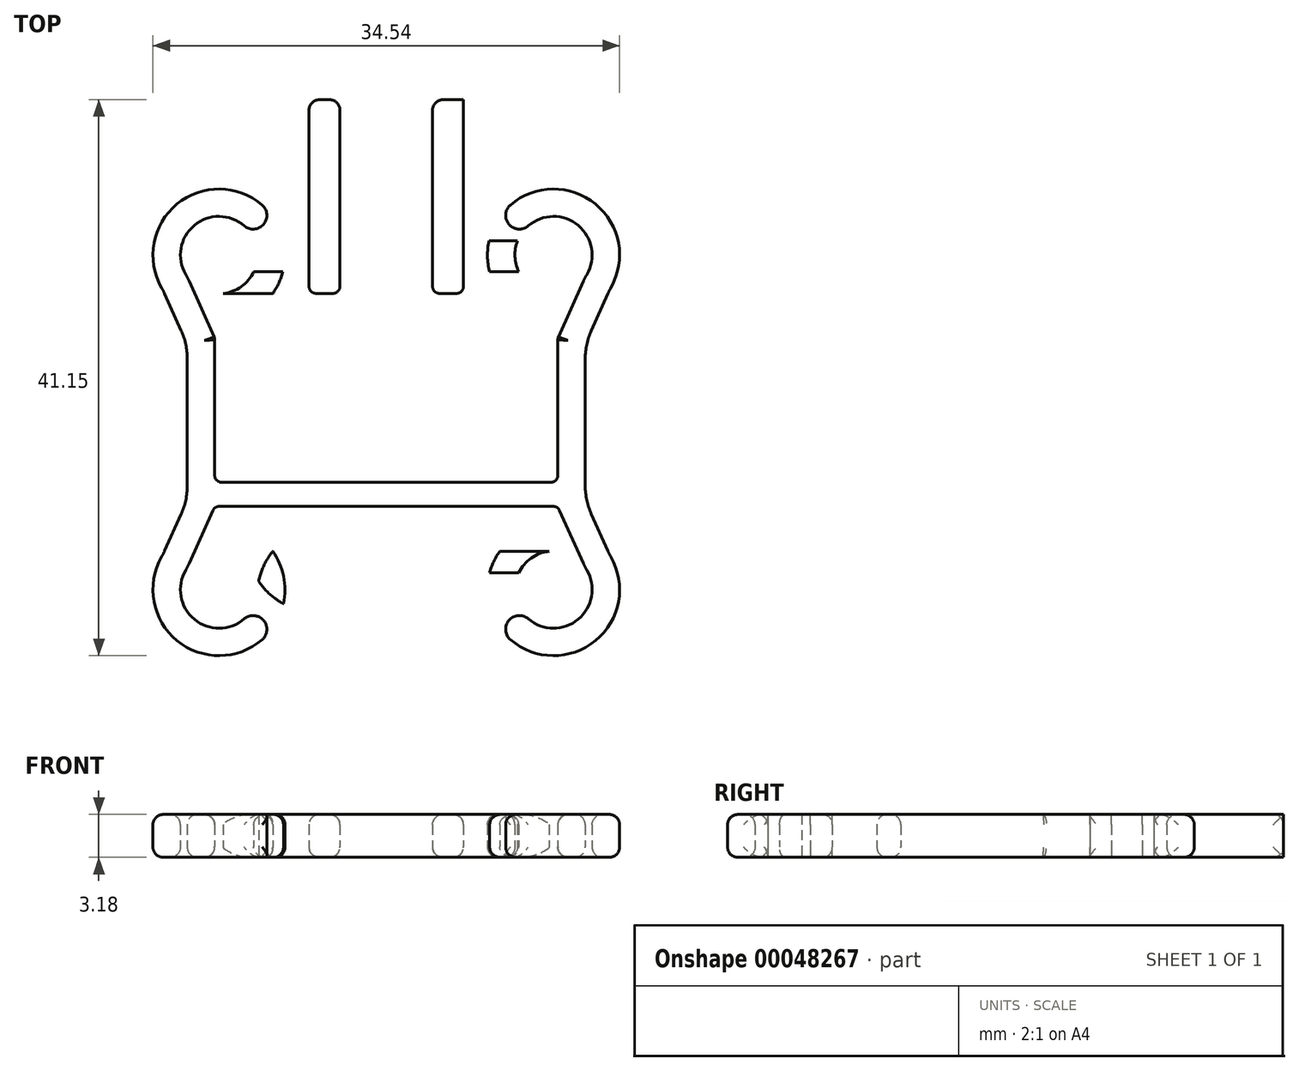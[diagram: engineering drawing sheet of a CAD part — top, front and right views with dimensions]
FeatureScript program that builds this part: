
annotation { "Feature Type Name" : "Feature", "Feature Type Description" : "" }
export const myFeature = defineFeature(function(context is Context, id is Id, definition is map)
    precondition{}
    {
        {
            var Q0;
            Q0=qCreatedBy(makeId("Top.planeOp"),FACE);
            var sketch = newSketch(context, id + "F0", { "sketchPlane" : qUnion([Q0])});
            skCircle(sketch, "E0", {"center": v(-12.38, 12.38) * mm, "radius": 2.86 * mm});
            skCircle(sketch, "E1", {"center": v(12.38, 12.38) * mm, "radius": 2.86 * mm});
            skCircle(sketch, "E2", {"center": v(12.38, -12.38) * mm, "radius": 2.86 * mm});
            skCircle(sketch, "E3", {"center": v(-12.38, -12.38) * mm, "radius": 2.86 * mm});
            skCircle(sketch, "E4", {"center": v(-12.38, 12.38) * mm, "radius": 4.89 * mm});
            skCircle(sketch, "E5", {"center": v(12.38, 12.38) * mm, "radius": 4.89 * mm});
            skCircle(sketch, "E6", {"center": v(12.38, -12.38) * mm, "radius": 4.89 * mm});
            skCircle(sketch, "E7", {"center": v(-12.38, -12.38) * mm, "radius": 4.89 * mm});
            skPoint(sketch, "E8.rect.middle", {"position": v(0, 0) * mm});
            skLineSegment(sketch, "E9.rect.bottom", {"start": v(14.73, 11.14) * mm, "end": v(-14.73, 11.14) * mm});
            skLineSegment(sketch, "E9.rect.top", {"start": v(14.73, -11.14) * mm, "end": v(-14.73, -11.14) * mm});
            skLineSegment(sketch, "E9.rect.left", {"start": v(14.73, 11.14) * mm, "end": v(14.73, -11.14) * mm});
            skLineSegment(sketch, "E9.rect.right", {"start": v(-14.73, 11.14) * mm, "end": v(-14.73, -11.14) * mm});
            skLineSegment(sketch, "E10.rect.bottom", {"start": v(12.7, 6.22) * mm, "end": v(-12.7, 6.22) * mm});
            skLineSegment(sketch, "E10.rect.top", {"start": v(12.7, -6.22) * mm, "end": v(-12.7, -6.22) * mm});
            skLineSegment(sketch, "E11.rect.bottom", {"start": v(12.7, 4.44) * mm, "end": v(-12.7, 4.44) * mm});
            skLineSegment(sketch, "E11.rect.top", {"start": v(12.7, -4.45) * mm, "end": v(-12.7, -4.45) * mm});
            skLineSegment(sketch, "E12.rect.bottom", {"start": v(12.7, 9.54) * mm, "end": v(-12.7, 9.54) * mm});
            skLineSegment(sketch, "E12.rect.top", {"start": v(12.7, -9.54) * mm, "end": v(-12.7, -9.54) * mm});
            skLineSegment(sketch, "E12.rect.left", {"start": v(12.7, 9.54) * mm, "end": v(12.7, -9.54) * mm});
            skLineSegment(sketch, "E12.rect.right", {"start": v(-12.7, 9.54) * mm, "end": v(-12.7, -9.54) * mm});
            skLineSegment(sketch, "E13.rect.bottom", {"start": v(5.72, 23.88) * mm, "end": v(3.43, 23.88) * mm});
            skLineSegment(sketch, "E13.rect.top", {"start": v(5.72, 11.14) * mm, "end": v(-5.71, 11.14) * mm});
            skLineSegment(sketch, "E13.rect.left", {"start": v(5.72, 23.88) * mm, "end": v(5.72, 11.14) * mm});
            skLineSegment(sketch, "E13.rect.right", {"start": v(-5.71, 23.88) * mm, "end": v(-5.71, 11.14) * mm});
            skLineSegment(sketch, "E14.top", {"start": v(-3.43, 11.14) * mm, "end": v(3.43, 11.14) * mm});
            skLineSegment(sketch, "E14.left", {"start": v(-3.43, 20.97) * mm, "end": v(-3.43, 11.14) * mm});
            skLineSegment(sketch, "E14.right", {"start": v(3.43, 20.97) * mm, "end": v(3.43, 11.14) * mm});
            skLineSegment(sketch, "E15", {"start": v(-5.71, 11.14) * mm, "end": v(-5.71, 6.22) * mm});
            skLineSegment(sketch, "E16", {"start": v(-5.71, 6.22) * mm, "end": v(-3.43, 6.22) * mm});
            skLineSegment(sketch, "E17", {"start": v(-3.43, 6.22) * mm, "end": v(-3.43, 11.14) * mm});
            skLineSegment(sketch, "E18", {"start": v(3.43, 11.14) * mm, "end": v(3.43, 6.22) * mm});
            skLineSegment(sketch, "E19", {"start": v(3.43, 6.22) * mm, "end": v(5.72, 6.22) * mm});
            skLineSegment(sketch, "E20", {"start": v(5.72, 6.22) * mm, "end": v(5.72, 11.14) * mm});
            skLineSegment(sketch, "E21.rect.bottom", {"start": v(-0.89, 4.44) * mm, "end": v(0.89, 4.44) * mm});
            skLineSegment(sketch, "E21.rect.top", {"start": v(-0.89, -4.44) * mm, "end": v(0.89, -4.44) * mm});
            skLineSegment(sketch, "E21.rect.left", {"start": v(-0.89, 4.44) * mm, "end": v(-0.89, -4.44) * mm});
            skLineSegment(sketch, "E21.rect.right", {"start": v(0.89, 4.44) * mm, "end": v(0.89, -4.44) * mm});
            skLineSegment(sketch, "E22.top", {"start": v(-3.43, 23.88) * mm, "end": v(-5.71, 23.88) * mm});
            skLineSegment(sketch, "E22.left", {"start": v(-3.43, 20.97) * mm, "end": v(-3.43, 23.88) * mm});
            skLineSegment(sketch, "E22.right", {"start": v(-5.71, 20.97) * mm, "end": v(-5.71, 23.88) * mm});
            skLineSegment(sketch, "E23.top", {"start": v(3.43, 23.88) * mm, "end": v(5.72, 23.88) * mm});
            skLineSegment(sketch, "E23.left", {"start": v(3.43, 20.97) * mm, "end": v(3.43, 23.88) * mm});
            skLineSegment(sketch, "E23.right", {"start": v(5.72, 20.97) * mm, "end": v(5.72, 23.88) * mm});
            skLineSegment(sketch, "E24.bottom", {"start": v(-10.35, 11.14) * mm, "end": v(-6.54, 11.14) * mm});
            skLineSegment(sketch, "E24.top", {"start": v(-10.35, 13.42) * mm, "end": v(-6.54, 13.42) * mm});
            skLineSegment(sketch, "E24.left", {"start": v(-10.35, 11.14) * mm, "end": v(-10.35, 13.42) * mm});
            skLineSegment(sketch, "E24.right", {"start": v(-6.54, 11.14) * mm, "end": v(-6.54, 13.42) * mm});
            skPoint(sketch, "E25.oppositeSnap0", {"position": v(-8.45, 13.42) * mm});
            skLineSegment(sketch, "E25.bottom", {"start": v(6.54, 11.14) * mm, "end": v(10.35, 11.14) * mm});
            skLineSegment(sketch, "E25.top", {"start": v(6.54, 13.42) * mm, "end": v(10.35, 13.42) * mm});
            skLineSegment(sketch, "E25.left", {"start": v(6.54, 11.14) * mm, "end": v(6.54, 13.42) * mm});
            skLineSegment(sketch, "E25.right", {"start": v(10.35, 11.14) * mm, "end": v(10.35, 13.42) * mm});
            skLineSegment(sketch, "E26", {"start": v(-10.35, 13.42) * mm, "end": v(-6.54, 17.1) * mm});
            skLineSegment(sketch, "E27", {"start": v(-6.54, 17.1) * mm, "end": v(-6.54, 13.42) * mm});
            skLineSegment(sketch, "E28", {"start": v(6.54, 13.42) * mm, "end": v(6.54, 17.1) * mm});
            skLineSegment(sketch, "E29", {"start": v(6.54, 17.1) * mm, "end": v(10.35, 13.42) * mm});
            skLineSegment(sketch, "E30.bottom", {"start": v(-10.35, -11.14) * mm, "end": v(-6.54, -11.14) * mm});
            skLineSegment(sketch, "E30.top", {"start": v(-10.35, -13.42) * mm, "end": v(-6.54, -13.42) * mm});
            skLineSegment(sketch, "E30.left", {"start": v(-10.35, -11.14) * mm, "end": v(-10.35, -13.42) * mm});
            skLineSegment(sketch, "E30.right", {"start": v(-6.54, -11.14) * mm, "end": v(-6.54, -13.42) * mm});
            skLineSegment(sketch, "E31.bottom", {"start": v(6.54, -13.42) * mm, "end": v(10.35, -13.42) * mm});
            skLineSegment(sketch, "E31.top", {"start": v(6.54, -11.14) * mm, "end": v(10.35, -11.14) * mm});
            skLineSegment(sketch, "E31.left", {"start": v(6.54, -13.42) * mm, "end": v(6.54, -11.14) * mm});
            skLineSegment(sketch, "E31.right", {"start": v(10.35, -13.42) * mm, "end": v(10.35, -11.14) * mm});
            skLineSegment(sketch, "E32", {"start": v(10.35, -13.42) * mm, "end": v(6.54, -17.1) * mm});
            skLineSegment(sketch, "E33", {"start": v(6.54, -17.1) * mm, "end": v(6.54, -13.42) * mm});
            skLineSegment(sketch, "E34", {"start": v(-6.54, -13.42) * mm, "end": v(-6.54, -17.1) * mm});
            skLineSegment(sketch, "E35", {"start": v(-6.54, -17.1) * mm, "end": v(-10.35, -13.42) * mm});
            skLineSegment(sketch, "E36", {"start": v(-12.7, -6.22) * mm, "end": v(-15.16, -11.7) * mm});
            skLineSegment(sketch, "E37", {"start": v(-15.16, -11.7) * mm, "end": v(-17.22, -11.7) * mm});
            skLineSegment(sketch, "E38", {"start": v(-17.22, -11.7) * mm, "end": v(-14.73, -6.15) * mm});
            skLineSegment(sketch, "E39", {"start": v(15.16, -11.7) * mm, "end": v(17.22, -11.7) * mm});
            skLineSegment(sketch, "E40", {"start": v(17.22, -11.7) * mm, "end": v(14.73, -6.15) * mm});
            skLineSegment(sketch, "E41", {"start": v(15.16, -11.7) * mm, "end": v(12.7, -6.22) * mm});
            skLineSegment(sketch, "E42", {"start": v(15.16, 11.7) * mm, "end": v(17.22, 11.7) * mm});
            skLineSegment(sketch, "E43", {"start": v(17.22, 11.7) * mm, "end": v(14.73, 6.14) * mm});
            skLineSegment(sketch, "E44", {"start": v(12.7, 6.22) * mm, "end": v(15.16, 11.7) * mm});
            skLineSegment(sketch, "E45", {"start": v(-15.16, 11.7) * mm, "end": v(-17.22, 11.7) * mm});
            skLineSegment(sketch, "E46", {"start": v(-17.22, 11.7) * mm, "end": v(-14.73, 6.14) * mm});
            skLineSegment(sketch, "E47", {"start": v(-15.16, 11.7) * mm, "end": v(-12.7, 6.22) * mm});
            skLineSegment(sketch, "E48", {"start": v(-16.52, 9.78) * mm, "end": v(-14.73, 5.79) * mm});
            skLineSegment(sketch, "E49", {"start": v(14.73, 5.79) * mm, "end": v(16.52, 9.78) * mm});
            skLineSegment(sketch, "E50", {"start": v(-16.52, -9.78) * mm, "end": v(-14.73, -5.79) * mm});
            skLineSegment(sketch, "E51", {"start": v(14.73, -5.79) * mm, "end": v(16.52, -9.78) * mm});
            skSolve(sketch);
        }
        {
            var Q0;
            {var subQ3=sQuery(id+"F0.wireOp",EDGE,"E9.rect.bottom");var subQ5=sQuery(id+"F0.wireOp",EDGE,"E0");var subQ7=makeQuery(id+"F0.imprint","INTERSECT",VERTEX,{"disambiguationData":[OD(0.0)],"derivedFrom":[subQ5,subQ3]});Q0=makeQuery(id+"F0.imprint","IMPRINT",FACE,{"disambiguationData":[TD([[makeQuery(id+"F0.imprint","IMPRINT",EDGE,{"disambiguationData":[TD([[subQ7,1.0]])],"derivedFrom":subQ5}),-1.0]])]});}
            var Q1;
            {var subQ0=sQuery(id+"F0.wireOp",EDGE,"E1");var subQ1=sQuery(id+"F0.wireOp",EDGE,"E9.rect.bottom");var subQ3=makeQuery(id+"F0.imprint","INTERSECT",VERTEX,{"disambiguationData":[OD(0.0)],"derivedFrom":[subQ0,subQ1]});Q1=makeQuery(id+"F0.imprint","IMPRINT",FACE,{"disambiguationData":[TD([[makeQuery(id+"F0.imprint","IMPRINT",EDGE,{"disambiguationData":[TD([[subQ3,1.0]])],"derivedFrom":subQ0}),-1.0]])]});}
            var Q2;
            {var subQ3=sQuery(id+"F0.wireOp",EDGE,"E9.rect.top");var subQ5=sQuery(id+"F0.wireOp",EDGE,"E2");var subQ7=makeQuery(id+"F0.imprint","INTERSECT",VERTEX,{"disambiguationData":[OD(0.0)],"derivedFrom":[subQ5,subQ3]});Q2=makeQuery(id+"F0.imprint","IMPRINT",FACE,{"disambiguationData":[TD([[makeQuery(id+"F0.imprint","IMPRINT",EDGE,{"disambiguationData":[TD([[subQ7,1.0]])],"derivedFrom":subQ5}),-1.0]])]});}
            var Q3;
            {var subQ3=sQuery(id+"F0.wireOp",EDGE,"E9.rect.top");var subQ5=sQuery(id+"F0.wireOp",EDGE,"E3");var subQ7=makeQuery(id+"F0.imprint","INTERSECT",VERTEX,{"disambiguationData":[OD(0.0)],"derivedFrom":[subQ5,subQ3]});Q3=makeQuery(id+"F0.imprint","IMPRINT",FACE,{"disambiguationData":[TD([[makeQuery(id+"F0.imprint","IMPRINT",EDGE,{"disambiguationData":[TD([[subQ7,1.0]])],"derivedFrom":subQ5}),-1.0]])]});}
            var Q4;
            {var subQ2=sQuery(id+"F0.wireOp",EDGE,"E10.rect.top");Q4=makeQuery(id+"F0.imprint","IMPRINT",FACE,{"disambiguationData":[TD([[makeQuery(id+"F0.imprint","IMPRINT",EDGE,{"derivedFrom":subQ2}),-1.0]])]});}
            var Q5;
            {var subQ1=sQuery(id+"F0.wireOp",EDGE,"E4");var subQ7=sQuery(id+"F0.wireOp",EDGE,"E9.rect.right");var subQ8=makeQuery(id+"F0.imprint","INTERSECT",VERTEX,{"derivedFrom":[subQ1,subQ7]});Q5=makeQuery(id+"F0.imprint","IMPRINT",FACE,{"disambiguationData":[TD([[makeQuery(id+"F0.imprint","IMPRINT",EDGE,{"disambiguationData":[TD([[subQ8,-1.0]])],"derivedFrom":subQ1}),1.0]])]});}
            var Q6;
            {var subQ7=sQuery(id+"F0.wireOp",EDGE,"E9.rect.right");var subQ9=sQuery(id+"F0.wireOp",EDGE,"E4");var subQ11=makeQuery(id+"F0.imprint","INTERSECT",VERTEX,{"derivedFrom":[subQ9,subQ7]});Q6=makeQuery(id+"F0.imprint","IMPRINT",FACE,{"disambiguationData":[TD([[makeQuery(id+"F0.imprint","IMPRINT",EDGE,{"disambiguationData":[TD([[subQ11,-1.0]])],"derivedFrom":subQ9}),-1.0]])]});}
            var Q7;
            {var subQ1=sQuery(id+"F0.wireOp",EDGE,"E7");var subQ5=sQuery(id+"F0.wireOp",EDGE,"E9.rect.right");var subQ6=makeQuery(id+"F0.imprint","INTERSECT",VERTEX,{"derivedFrom":[subQ1,subQ5]});Q7=makeQuery(id+"F0.imprint","IMPRINT",FACE,{"disambiguationData":[TD([[makeQuery(id+"F0.imprint","IMPRINT",EDGE,{"disambiguationData":[TD([[subQ6,1.0]])],"derivedFrom":subQ1}),1.0]])]});}
            var Q8;
            {var subQ7=sQuery(id+"F0.wireOp",EDGE,"E5");var subQ9=sQuery(id+"F0.wireOp",EDGE,"E9.rect.left");var subQ11=makeQuery(id+"F0.imprint","INTERSECT",VERTEX,{"derivedFrom":[subQ7,subQ9]});Q8=makeQuery(id+"F0.imprint","IMPRINT",FACE,{"disambiguationData":[TD([[makeQuery(id+"F0.imprint","IMPRINT",EDGE,{"disambiguationData":[TD([[subQ11,1.0]])],"derivedFrom":subQ7}),-1.0]])]});}
            var Q9;
            {var subQ1=sQuery(id+"F0.wireOp",EDGE,"E5");var subQ7=sQuery(id+"F0.wireOp",EDGE,"E9.rect.left");var subQ8=makeQuery(id+"F0.imprint","INTERSECT",VERTEX,{"derivedFrom":[subQ1,subQ7]});Q9=makeQuery(id+"F0.imprint","IMPRINT",FACE,{"disambiguationData":[TD([[makeQuery(id+"F0.imprint","IMPRINT",EDGE,{"disambiguationData":[TD([[subQ8,1.0]])],"derivedFrom":subQ1}),1.0]])]});}
            var Q10;
            {var subQ1=sQuery(id+"F0.wireOp",EDGE,"E6");var subQ7=sQuery(id+"F0.wireOp",EDGE,"E9.rect.left");var subQ9=makeQuery(id+"F0.imprint","INTERSECT",VERTEX,{"derivedFrom":[subQ1,subQ7]});Q10=makeQuery(id+"F0.imprint","IMPRINT",FACE,{"disambiguationData":[TD([[makeQuery(id+"F0.imprint","IMPRINT",EDGE,{"disambiguationData":[TD([[subQ9,-1.0]])],"derivedFrom":subQ1}),1.0]])]});}
            var Q11;
            {var subQ4=sQuery(id+"F0.wireOp",EDGE,"E16");Q11=makeQuery(id+"F0.imprint","IMPRINT",FACE,{"disambiguationData":[TD([[makeQuery(id+"F0.imprint","IMPRINT",EDGE,{"derivedFrom":subQ4}),1.0]])]});}
            var Q12;
            {var subQ0=sQuery(id+"F0.wireOp",EDGE,"E17");var subQ1=sQuery(id+"F0.wireOp",EDGE,"E12.rect.bottom");var subQ2=makeQuery(id+"F0.imprint","INTERSECT",VERTEX,{"derivedFrom":[subQ1,subQ0]});Q12=makeQuery(id+"F0.imprint","IMPRINT",FACE,{"disambiguationData":[TD([[makeQuery(id+"F0.imprint","IMPRINT",EDGE,{"disambiguationData":[TD([[subQ2,-1.0]])],"derivedFrom":subQ1}),-1.0]])]});}
            var Q13;
            {var subQ1=sQuery(id+"F0.wireOp",EDGE,"b3d8b3c6-d051-494b-8968-ba9f3ebd01f7.rect.top");var subQ5=sQuery(id+"F0.wireOp",EDGE,"E13.rect.right");var subQ6=makeQuery(id+"F0.imprint","INTERSECT",VERTEX,{"derivedFrom":[subQ5,subQ1]});Q13=makeQuery(id+"F0.imprint","IMPRINT",FACE,{"disambiguationData":[TD([[makeQuery(id+"F0.imprint","IMPRINT",EDGE,{"disambiguationData":[TD([[subQ6,1.0]])],"derivedFrom":subQ1}),1.0]])]});}
            var Q14;
            {var subQ1=sQuery(id+"F0.wireOp",EDGE,"b3d8b3c6-d051-494b-8968-ba9f3ebd01f7.rect.top");var subQ5=sQuery(id+"F0.wireOp",EDGE,"E13.rect.left");var subQ6=makeQuery(id+"F0.imprint","INTERSECT",VERTEX,{"derivedFrom":[subQ5,subQ1]});Q14=makeQuery(id+"F0.imprint","IMPRINT",FACE,{"disambiguationData":[TD([[makeQuery(id+"F0.imprint","IMPRINT",EDGE,{"disambiguationData":[TD([[subQ6,-1.0]])],"derivedFrom":subQ1}),1.0]])]});}
            var Q15;
            {var subQ1=sQuery(id+"F0.wireOp",EDGE,"E12.rect.bottom");var subQ5=sQuery(id+"F0.wireOp",EDGE,"E20");var subQ6=makeQuery(id+"F0.imprint","INTERSECT",VERTEX,{"derivedFrom":[subQ1,subQ5]});Q15=makeQuery(id+"F0.imprint","IMPRINT",FACE,{"disambiguationData":[TD([[makeQuery(id+"F0.imprint","IMPRINT",EDGE,{"disambiguationData":[TD([[subQ6,-1.0]])],"derivedFrom":subQ1}),-1.0]])]});}
            var Q16;
            {var subQ4=sQuery(id+"F0.wireOp",EDGE,"E19");Q16=makeQuery(id+"F0.imprint","IMPRINT",FACE,{"disambiguationData":[TD([[makeQuery(id+"F0.imprint","IMPRINT",EDGE,{"derivedFrom":subQ4}),1.0]])]});}
            var Q17;
            {var subQ0=sQuery(id+"F0.wireOp",EDGE,"E22.bottom");Q17=makeQuery(id+"F0.imprint","IMPRINT",FACE,{"disambiguationData":[TD([[makeQuery(id+"F0.imprint","IMPRINT",EDGE,{"derivedFrom":subQ0}),1.0]])]});}
            var Q18;
            Q18=makeQuery(id+"F0.imprint","IMPRINT",FACE,{"disambiguationData":[TD([[makeQuery(id+"F0.imprint","IMPRINT",EDGE,{"derivedFrom":sQuery(id+"F0.wireOp",EDGE,"E22.bottom")}),-1.0]])]});
            var Q19;
            {var subQ5=sQuery(id+"F0.wireOp",EDGE,"E23.bottom");Q19=makeQuery(id+"F0.imprint","IMPRINT",FACE,{"disambiguationData":[TD([[makeQuery(id+"F0.imprint","IMPRINT",EDGE,{"derivedFrom":subQ5}),-1.0]])]});}
            var Q20;
            Q20=makeQuery(id+"F0.imprint","IMPRINT",FACE,{"disambiguationData":[TD([[makeQuery(id+"F0.imprint","IMPRINT",EDGE,{"derivedFrom":sQuery(id+"F0.wireOp",EDGE,"E23.bottom")}),1.0]])]});
            var Q21;
            {var subQ2=sQuery(id+"F0.wireOp",EDGE,"E13.rect.right");Q21=makeQuery(id+"F0.imprint","IMPRINT",FACE,{"disambiguationData":[TD([[makeQuery(id+"F0.imprint","IMPRINT",EDGE,{"derivedFrom":subQ2}),1.0]])]});}
            var Q22;
            {var subQ2=sQuery(id+"F0.wireOp",EDGE,"E13.rect.left");Q22=makeQuery(id+"F0.imprint","IMPRINT",FACE,{"disambiguationData":[TD([[makeQuery(id+"F0.imprint","IMPRINT",EDGE,{"derivedFrom":subQ2}),-1.0]])]});}
            var Q23;
            {var subQ1=sQuery(id+"F0.wireOp",EDGE,"E3");var subQ5=sQuery(id+"F0.wireOp",EDGE,"E9.rect.top");var subQ6=makeQuery(id+"F0.imprint","INTERSECT",VERTEX,{"derivedFrom":[subQ1,subQ5]});Q23=makeQuery(id+"F0.imprint","IMPRINT",FACE,{"disambiguationData":[TD([[makeQuery(id+"F0.imprint","IMPRINT",EDGE,{"disambiguationData":[TD([[subQ6,-1.0]])],"derivedFrom":subQ1}),-1.0]])]});}
            var Q24;
            {var subQ0=sQuery(id+"F0.wireOp",EDGE,"E29");var subQ1=sQuery(id+"F0.wireOp",EDGE,"E1");var subQ2=makeQuery(id+"F0.imprint","INTERSECT",VERTEX,{"derivedFrom":[subQ1,subQ0]});Q24=makeQuery(id+"F0.imprint","IMPRINT",FACE,{"disambiguationData":[TD([[makeQuery(id+"F0.imprint","IMPRINT",EDGE,{"disambiguationData":[TD([[subQ2,1.0]])],"derivedFrom":subQ1}),-1.0]])]});}
            var Q25;
            {var subQ9=sQuery(id+"F0.wireOp",EDGE,"E16");Q25=makeQuery(id+"F0.imprint","IMPRINT",FACE,{"disambiguationData":[TD([[makeQuery(id+"F0.imprint","IMPRINT",EDGE,{"derivedFrom":subQ9}),-1.0]])]});}
            var Q26;
            {var subQ0=sQuery(id+"F0.wireOp",EDGE,"E45");Q26=makeQuery(id+"F0.imprint","IMPRINT",FACE,{"disambiguationData":[TD([[makeQuery(id+"F0.imprint","IMPRINT",EDGE,{"derivedFrom":subQ0}),-1.0]])]});}
            var Q27;
            {var subQ3=sQuery(id+"F0.wireOp",EDGE,"E42");Q27=makeQuery(id+"F0.imprint","IMPRINT",FACE,{"disambiguationData":[TD([[makeQuery(id+"F0.imprint","IMPRINT",EDGE,{"derivedFrom":subQ3}),-1.0]])]});}
            var Q28;
            {var subQ0=sQuery(id+"F0.wireOp",EDGE,"E39");Q28=makeQuery(id+"F0.imprint","IMPRINT",FACE,{"disambiguationData":[TD([[makeQuery(id+"F0.imprint","IMPRINT",EDGE,{"derivedFrom":subQ0}),-1.0]])]});}
            var Q29;
            {var subQ5=sQuery(id+"F0.wireOp",EDGE,"E37");Q29=makeQuery(id+"F0.imprint","IMPRINT",FACE,{"disambiguationData":[TD([[makeQuery(id+"F0.imprint","IMPRINT",EDGE,{"derivedFrom":subQ5}),1.0]])]});}
            var Q30;
            {var subQ0=sQuery(id+"F0.wireOp",EDGE,"E38");var subQ1=sQuery(id+"F0.wireOp",EDGE,"E7");var subQ2=makeQuery(id+"F0.imprint","INTERSECT",VERTEX,{"derivedFrom":[subQ1,subQ0]});Q30=makeQuery(id+"F0.imprint","IMPRINT",FACE,{"disambiguationData":[TD([[makeQuery(id+"F0.imprint","IMPRINT",EDGE,{"disambiguationData":[TD([[subQ2,1.0]])],"derivedFrom":subQ1}),-1.0]])]});}
            var Q31;
            {var subQ0=sQuery(id+"F0.wireOp",EDGE,"E40");var subQ1=sQuery(id+"F0.wireOp",EDGE,"E6");var subQ2=makeQuery(id+"F0.imprint","INTERSECT",VERTEX,{"derivedFrom":[subQ1,subQ0]});Q31=makeQuery(id+"F0.imprint","IMPRINT",FACE,{"disambiguationData":[TD([[makeQuery(id+"F0.imprint","IMPRINT",EDGE,{"disambiguationData":[TD([[subQ2,-1.0]])],"derivedFrom":subQ1}),-1.0]])]});}
            var Q32;
            {var subQ1=sQuery(id+"F0.wireOp",EDGE,"E5");var subQ3=sQuery(id+"F0.wireOp",EDGE,"E43");var subQ5=makeQuery(id+"F0.imprint","INTERSECT",VERTEX,{"derivedFrom":[subQ1,subQ3]});Q32=makeQuery(id+"F0.imprint","IMPRINT",FACE,{"disambiguationData":[TD([[makeQuery(id+"F0.imprint","IMPRINT",EDGE,{"disambiguationData":[TD([[subQ5,1.0]])],"derivedFrom":subQ1}),-1.0]])]});}
            var Q33;
            {var subQ0=sQuery(id+"F0.wireOp",EDGE,"E46");var subQ1=sQuery(id+"F0.wireOp",EDGE,"E4");var subQ2=makeQuery(id+"F0.imprint","INTERSECT",VERTEX,{"derivedFrom":[subQ1,subQ0]});Q33=makeQuery(id+"F0.imprint","IMPRINT",FACE,{"disambiguationData":[TD([[makeQuery(id+"F0.imprint","IMPRINT",EDGE,{"disambiguationData":[TD([[subQ2,-1.0]])],"derivedFrom":subQ1}),-1.0]])]});}
            var Q34;
            {var subQ0=sQuery(id+"F0.wireOp",EDGE,"E45");Q34=makeQuery(id+"F0.imprint","IMPRINT",FACE,{"disambiguationData":[TD([[makeQuery(id+"F0.imprint","IMPRINT",EDGE,{"derivedFrom":subQ0}),1.0]])]});}
            var Q35;
            {var subQ9=sQuery(id+"F0.wireOp",EDGE,"E37");Q35=makeQuery(id+"F0.imprint","IMPRINT",FACE,{"disambiguationData":[TD([[makeQuery(id+"F0.imprint","IMPRINT",EDGE,{"derivedFrom":subQ9}),-1.0]])]});}
            var Q36;
            {var subQ0=sQuery(id+"F0.wireOp",EDGE,"E39");Q36=makeQuery(id+"F0.imprint","IMPRINT",FACE,{"disambiguationData":[TD([[makeQuery(id+"F0.imprint","IMPRINT",EDGE,{"derivedFrom":subQ0}),1.0]])]});}
            var Q37;
            {var subQ0=sQuery(id+"F0.wireOp",EDGE,"E38");var subQ1=sQuery(id+"F0.wireOp",EDGE,"E7");var subQ3=makeQuery(id+"F0.imprint","INTERSECT",VERTEX,{"derivedFrom":[subQ1,subQ0]});Q37=makeQuery(id+"F0.imprint","IMPRINT",FACE,{"disambiguationData":[TD([[makeQuery(id+"F0.imprint","IMPRINT",EDGE,{"disambiguationData":[TD([[subQ3,-1.0]])],"derivedFrom":subQ1}),1.0]])]});}
            var Q38;
            {var subQ0=sQuery(id+"F0.wireOp",EDGE,"E40");var subQ1=sQuery(id+"F0.wireOp",EDGE,"E6");var subQ3=makeQuery(id+"F0.imprint","INTERSECT",VERTEX,{"derivedFrom":[subQ1,subQ0]});Q38=makeQuery(id+"F0.imprint","IMPRINT",FACE,{"disambiguationData":[TD([[makeQuery(id+"F0.imprint","IMPRINT",EDGE,{"disambiguationData":[TD([[subQ3,1.0]])],"derivedFrom":subQ1}),1.0]])]});}
            var Q39;
            {var subQ0=sQuery(id+"F0.wireOp",EDGE,"E43");var subQ1=sQuery(id+"F0.wireOp",EDGE,"E5");var subQ3=makeQuery(id+"F0.imprint","INTERSECT",VERTEX,{"derivedFrom":[subQ1,subQ0]});Q39=makeQuery(id+"F0.imprint","IMPRINT",FACE,{"disambiguationData":[TD([[makeQuery(id+"F0.imprint","IMPRINT",EDGE,{"disambiguationData":[TD([[subQ3,-1.0]])],"derivedFrom":subQ1}),1.0]])]});}
            var Q40;
            {var subQ0=sQuery(id+"F0.wireOp",EDGE,"E46");var subQ1=sQuery(id+"F0.wireOp",EDGE,"E4");var subQ3=makeQuery(id+"F0.imprint","INTERSECT",VERTEX,{"derivedFrom":[subQ1,subQ0]});Q40=makeQuery(id+"F0.imprint","IMPRINT",FACE,{"disambiguationData":[TD([[makeQuery(id+"F0.imprint","IMPRINT",EDGE,{"disambiguationData":[TD([[subQ3,1.0]])],"derivedFrom":subQ1}),1.0]])]});}
            var Q41;
            {var subQ0=sQuery(id+"F0.wireOp",EDGE,"E50");Q41=makeQuery(id+"F0.imprint","IMPRINT",FACE,{"disambiguationData":[TD([[makeQuery(id+"F0.imprint","IMPRINT",EDGE,{"derivedFrom":subQ0}),-1.0]])]});}
            var Q42;
            {var subQ0=sQuery(id+"F0.wireOp",EDGE,"E51");Q42=makeQuery(id+"F0.imprint","IMPRINT",FACE,{"disambiguationData":[TD([[makeQuery(id+"F0.imprint","IMPRINT",EDGE,{"derivedFrom":subQ0}),-1.0]])]});}
            var Q43;
            {var subQ0=sQuery(id+"F0.wireOp",EDGE,"E49");Q43=makeQuery(id+"F0.imprint","IMPRINT",FACE,{"disambiguationData":[TD([[makeQuery(id+"F0.imprint","IMPRINT",EDGE,{"derivedFrom":subQ0}),1.0]])]});}
            var Q44;
            {var subQ0=sQuery(id+"F0.wireOp",EDGE,"E48");Q44=makeQuery(id+"F0.imprint","IMPRINT",FACE,{"disambiguationData":[TD([[makeQuery(id+"F0.imprint","IMPRINT",EDGE,{"derivedFrom":subQ0}),1.0]])]});}
            extrude(context, id + "F1", {"entities" : qUnion([Q0, Q1, Q2, Q3, Q4, Q5, Q6, Q7, Q8, Q9, Q10, Q11, Q12, Q13, Q14, Q15, Q16, Q17, Q18, Q19, Q20, Q21, Q22, Q23, Q24, Q25, Q26, Q27, Q28, Q29, Q30, Q31, Q32, Q33, Q34, Q35, Q36, Q37, Q38, Q39, Q40, Q41, Q42, Q43, Q44]), "depth" : 3.17 * mm});
        }
        {
            var Q0;
            Q0=makeQuery(id+"F1.opExtrude","SWEPT_EDGE",EDGE,{"disambiguationData":[OSD([sQuery(id+"F0.wireOp",EDGE,"E0"),sQuery(id+"F0.wireOp",EDGE,"E26")])]});
            var Q1;
            Q1=makeQuery(id+"F1.opExtrude","SWEPT_EDGE",EDGE,{"disambiguationData":[OSD([sQuery(id+"F0.wireOp",EDGE,"E4"),sQuery(id+"F0.wireOp",EDGE,"E26")])]});
            var Q2;
            Q2=makeQuery(id+"F1.opExtrude","SWEPT_EDGE",EDGE,{"disambiguationData":[OSD([sQuery(id+"F0.wireOp",EDGE,"E1"),sQuery(id+"F0.wireOp",EDGE,"E29")])]});
            var Q3;
            Q3=makeQuery(id+"F1.opExtrude","SWEPT_EDGE",EDGE,{"disambiguationData":[OSD([sQuery(id+"F0.wireOp",EDGE,"E5"),sQuery(id+"F0.wireOp",EDGE,"E29")])]});
            var Q4;
            Q4=makeQuery(id+"F1.opExtrude","SWEPT_EDGE",EDGE,{"disambiguationData":[OSD([sQuery(id+"F0.wireOp",EDGE,"E7"),sQuery(id+"F0.wireOp",EDGE,"E35")])]});
            var Q5;
            Q5=makeQuery(id+"F1.opExtrude","SWEPT_EDGE",EDGE,{"disambiguationData":[OSD([sQuery(id+"F0.wireOp",EDGE,"E3"),sQuery(id+"F0.wireOp",EDGE,"E35")])]});
            var Q6;
            Q6=makeQuery(id+"F1.opExtrude","SWEPT_EDGE",EDGE,{"disambiguationData":[OSD([sQuery(id+"F0.wireOp",EDGE,"E6"),sQuery(id+"F0.wireOp",EDGE,"E32")])]});
            var Q7;
            Q7=makeQuery(id+"F1.opExtrude","SWEPT_EDGE",EDGE,{"disambiguationData":[OSD([sQuery(id+"F0.wireOp",EDGE,"E2"),sQuery(id+"F0.wireOp",EDGE,"E32")])]});
            fillet(context, id + "F2", {"entities" : qUnion([Q0, Q1, Q2, Q3, Q4, Q5, Q6, Q7]), "radius" : 1.02 * mm, "tangentPropagation" : true, "allowEdgeOverflow" : false});
        }
        {
            var Q0;
            Q0=makeQuery(id+"F1.opExtrude","SWEPT_EDGE",EDGE,{"disambiguationData":[OSD([sQuery(id+"F0.wireOp",EDGE,"E9.rect.right"),sQuery(id+"F0.wireOp",EDGE,"E48")])]});
            var Q1;
            Q1=makeQuery(id+"F1.opExtrude","SWEPT_EDGE",EDGE,{"disambiguationData":[OSD([sQuery(id+"F0.wireOp",EDGE,"E4"),sQuery(id+"F0.wireOp",EDGE,"E48")])]});
            var Q2;
            Q2=makeQuery(id+"F1.opExtrude","SWEPT_EDGE",EDGE,{"disambiguationData":[OSD([sQuery(id+"F0.wireOp",EDGE,"E9.rect.right"),sQuery(id+"F0.wireOp",EDGE,"E50")])]});
            var Q3;
            Q3=makeQuery(id+"F1.opExtrude","SWEPT_EDGE",EDGE,{"disambiguationData":[OSD([sQuery(id+"F0.wireOp",EDGE,"E7"),sQuery(id+"F0.wireOp",EDGE,"E50")])]});
            var Q4;
            Q4=makeQuery(id+"F1.opExtrude","SWEPT_EDGE",EDGE,{"disambiguationData":[OSD([sQuery(id+"F0.wireOp",EDGE,"E2"),sQuery(id+"F0.wireOp",EDGE,"E9.rect.left")])]});
            var Q5;
            Q5=makeQuery(id+"F1.opExtrude","SWEPT_EDGE",EDGE,{"disambiguationData":[OSD([sQuery(id+"F0.wireOp",EDGE,"E3"),sQuery(id+"F0.wireOp",EDGE,"E9.rect.right")])]});
            var Q6;
            Q6=makeQuery(id+"F1.opExtrude","SWEPT_EDGE",EDGE,{"disambiguationData":[OSD([sQuery(id+"F0.wireOp",EDGE,"E6"),sQuery(id+"F0.wireOp",EDGE,"E51")])]});
            var Q7;
            Q7=makeQuery(id+"F1.opExtrude","SWEPT_EDGE",EDGE,{"disambiguationData":[OSD([sQuery(id+"F0.wireOp",EDGE,"E9.rect.left"),sQuery(id+"F0.wireOp",EDGE,"E51")])]});
            var Q8;
            Q8=makeQuery(id+"F1.opExtrude","SWEPT_EDGE",EDGE,{"disambiguationData":[OSD([sQuery(id+"F0.wireOp",EDGE,"E9.rect.left"),sQuery(id+"F0.wireOp",EDGE,"E49")])]});
            var Q9;
            Q9=makeQuery(id+"F1.opExtrude","SWEPT_EDGE",EDGE,{"disambiguationData":[OSD([sQuery(id+"F0.wireOp",EDGE,"E5"),sQuery(id+"F0.wireOp",EDGE,"E49")])]});
            var Q10;
            Q10=makeQuery(id+"F1.opExtrude","SWEPT_EDGE",EDGE,{"disambiguationData":[OSD([sQuery(id+"F0.wireOp",EDGE,"E9.rect.left"),sQuery(id+"F0.wireOp",EDGE,"E44")])]});
            var Q11;
            Q11=makeQuery(id+"F1.opExtrude","SWEPT_EDGE",EDGE,{"disambiguationData":[OSD([sQuery(id+"F0.wireOp",EDGE,"E0"),sQuery(id+"F0.wireOp",EDGE,"E9.rect.right")])]});
            fillet(context, id + "F3", {"entities" : qUnion([Q0, Q1, Q2, Q3, Q4, Q5, Q6, Q7, Q8, Q9, Q10, Q11]), "radius" : 5.08 * mm, "tangentPropagation" : true, "allowEdgeOverflow" : false});
        }
        {
            var Q0;
            Q0=makeQuery(id+"F1.opExtrude","SWEPT_EDGE",EDGE,{"disambiguationData":[OSD([sQuery(id+"F0.wireOp",EDGE,"E11.rect.top"),sQuery(id+"F0.wireOp",EDGE,"E12.rect.left")])]});
            var Q1;
            Q1=makeQuery(id+"F1.opExtrude","SWEPT_EDGE",EDGE,{"disambiguationData":[OSD([sQuery(id+"F0.wireOp",EDGE,"E11.rect.bottom"),sQuery(id+"F0.wireOp",EDGE,"E12.rect.left")])]});
            var Q2;
            Q2=makeQuery(id+"F1.opExtrude","SWEPT_EDGE",EDGE,{"disambiguationData":[OSD([sQuery(id+"F0.wireOp",EDGE,"E10.rect.top"),sQuery(id+"F0.wireOp",EDGE,"E12.rect.left"),sQuery(id+"F0.wireOp",EDGE,"E41")])]});
            var Q3;
            Q3=makeQuery(id+"F1.opExtrude","SWEPT_EDGE",EDGE,{"disambiguationData":[OSD([sQuery(id+"F0.wireOp",EDGE,"E10.rect.top"),sQuery(id+"F0.wireOp",EDGE,"E12.rect.right"),sQuery(id+"F0.wireOp",EDGE,"E36")])]});
            var Q4;
            Q4=makeQuery(id+"F1.opExtrude","SWEPT_EDGE",EDGE,{"disambiguationData":[OSD([sQuery(id+"F0.wireOp",EDGE,"E11.rect.bottom"),sQuery(id+"F0.wireOp",EDGE,"E12.rect.right")])]});
            var Q5;
            Q5=makeQuery(id+"F1.opExtrude","SWEPT_EDGE",EDGE,{"disambiguationData":[OSD([sQuery(id+"F0.wireOp",EDGE,"E11.rect.top"),sQuery(id+"F0.wireOp",EDGE,"E12.rect.right")])]});
            var Q6;
            Q6=makeQuery(id+"F1.opExtrude","SWEPT_EDGE",EDGE,{"disambiguationData":[OSD([sQuery(id+"F0.wireOp",EDGE,"E10.rect.bottom"),sQuery(id+"F0.wireOp",EDGE,"E12.rect.right"),sQuery(id+"F0.wireOp",EDGE,"E47")])]});
            var Q7;
            Q7=makeQuery(id+"F1.opExtrude","SWEPT_EDGE",EDGE,{"disambiguationData":[OSD([sQuery(id+"F0.wireOp",EDGE,"E10.rect.bottom"),sQuery(id+"F0.wireOp",EDGE,"E16"),sQuery(id+"F0.wireOp",EDGE,"E17")])]});
            var Q8;
            Q8=makeQuery(id+"F1.opExtrude","SWEPT_EDGE",EDGE,{"disambiguationData":[OSD([sQuery(id+"F0.wireOp",EDGE,"E10.rect.bottom"),sQuery(id+"F0.wireOp",EDGE,"E19"),sQuery(id+"F0.wireOp",EDGE,"E20")])]});
            var Q9;
            Q9=makeQuery(id+"F1.opExtrude","SWEPT_EDGE",EDGE,{"disambiguationData":[OSD([sQuery(id+"F0.wireOp",EDGE,"E10.rect.bottom"),sQuery(id+"F0.wireOp",EDGE,"E15"),sQuery(id+"F0.wireOp",EDGE,"E16")])]});
            var Q10;
            Q10=makeQuery(id+"F1.opExtrude","SWEPT_EDGE",EDGE,{"disambiguationData":[OSD([sQuery(id+"F0.wireOp",EDGE,"E10.rect.bottom"),sQuery(id+"F0.wireOp",EDGE,"E18"),sQuery(id+"F0.wireOp",EDGE,"E19")])]});
            var Q11;
            Q11=makeQuery(id+"F1.opExtrude","SWEPT_EDGE",EDGE,{"disambiguationData":[OSD([sQuery(id+"F0.wireOp",EDGE,"E10.rect.bottom"),sQuery(id+"F0.wireOp",EDGE,"E12.rect.left"),sQuery(id+"F0.wireOp",EDGE,"E44")])]});
            fillet(context, id + "F4", {"entities" : qUnion([Q0, Q1, Q2, Q3, Q4, Q5, Q6, Q7, Q8, Q9, Q10, Q11]), "radius" : 0.5 * mm, "tangentPropagation" : true, "allowEdgeOverflow" : false});
        }
        {
            var Q0;
            Q0=makeQuery(id+"F1.opExtrude","CAP_EDGE",EDGE,{"disambiguationData":[OSD([sQuery(id+"F0.wireOp",EDGE,"E4")])],"isStart":false});
            var Q1;
            {var subQ0=sQuery(id+"F0.wireOp",EDGE,"E48");var subQ1=sQuery(id+"F0.wireOp",EDGE,"E4");Q1=makeQuery(id+"F3.opFillet","BLEND_EDGE",EDGE,{"blendedFrom":[makeQuery(id+"F1.opExtrude","SWEPT_EDGE",EDGE,{"disambiguationData":[OSD([subQ1,subQ0])]}),makeQuery(id+"F1.opExtrude","CAP_FACE",FACE,{"disambiguationData":[OSD([sQuery(id+"F0.wireOp",EDGE,"E0"),sQuery(id+"F0.wireOp",EDGE,"E1"),sQuery(id+"F0.wireOp",EDGE,"E2"),sQuery(id+"F0.wireOp",EDGE,"E3"),subQ1,sQuery(id+"F0.wireOp",EDGE,"E5"),sQuery(id+"F0.wireOp",EDGE,"E6"),sQuery(id+"F0.wireOp",EDGE,"E7"),sQuery(id+"F0.wireOp",EDGE,"E9.rect.left"),sQuery(id+"F0.wireOp",EDGE,"E9.rect.right"),sQuery(id+"F0.wireOp",EDGE,"E10.rect.bottom"),sQuery(id+"F0.wireOp",EDGE,"E10.rect.top"),sQuery(id+"F0.wireOp",EDGE,"E11.rect.bottom"),sQuery(id+"F0.wireOp",EDGE,"E11.rect.top"),sQuery(id+"F0.wireOp",EDGE,"E12.rect.left"),sQuery(id+"F0.wireOp",EDGE,"E12.rect.right"),sQuery(id+"F0.wireOp",EDGE,"E13.rect.left"),sQuery(id+"F0.wireOp",EDGE,"E13.rect.right"),sQuery(id+"F0.wireOp",EDGE,"E14.left"),sQuery(id+"F0.wireOp",EDGE,"E14.right"),sQuery(id+"F0.wireOp",EDGE,"E15"),sQuery(id+"F0.wireOp",EDGE,"E17"),sQuery(id+"F0.wireOp",EDGE,"E18"),sQuery(id+"F0.wireOp",EDGE,"E20"),sQuery(id+"F0.wireOp",EDGE,"E21.rect.bottom"),sQuery(id+"F0.wireOp",EDGE,"E21.rect.top"),sQuery(id+"F0.wireOp",EDGE,"E22.left"),sQuery(id+"F0.wireOp",EDGE,"E22.right"),sQuery(id+"F0.wireOp",EDGE,"E23.top"),sQuery(id+"F0.wireOp",EDGE,"E23.left"),sQuery(id+"F0.wireOp",EDGE,"E23.right"),sQuery(id+"F0.wireOp",EDGE,"E22.top"),sQuery(id+"F0.wireOp",EDGE,"E26"),sQuery(id+"F0.wireOp",EDGE,"E29"),sQuery(id+"F0.wireOp",EDGE,"E32"),sQuery(id+"F0.wireOp",EDGE,"E35"),sQuery(id+"F0.wireOp",EDGE,"E36"),sQuery(id+"F0.wireOp",EDGE,"E41"),sQuery(id+"F0.wireOp",EDGE,"E44"),sQuery(id+"F0.wireOp",EDGE,"E47"),subQ0,sQuery(id+"F0.wireOp",EDGE,"E49"),sQuery(id+"F0.wireOp",EDGE,"E50"),sQuery(id+"F0.wireOp",EDGE,"E51")])],"isStart":false})],"blendedInto":[makeQuery(id+"F1.opExtrude","CAP_FACE",FACE,{"disambiguationData":[OSD([sQuery(id+"F0.wireOp",EDGE,"E0"),sQuery(id+"F0.wireOp",EDGE,"E1"),sQuery(id+"F0.wireOp",EDGE,"E2"),sQuery(id+"F0.wireOp",EDGE,"E3"),subQ1,sQuery(id+"F0.wireOp",EDGE,"E5"),sQuery(id+"F0.wireOp",EDGE,"E6"),sQuery(id+"F0.wireOp",EDGE,"E7"),sQuery(id+"F0.wireOp",EDGE,"E9.rect.left"),sQuery(id+"F0.wireOp",EDGE,"E9.rect.right"),sQuery(id+"F0.wireOp",EDGE,"E10.rect.bottom"),sQuery(id+"F0.wireOp",EDGE,"E10.rect.top"),sQuery(id+"F0.wireOp",EDGE,"E11.rect.bottom"),sQuery(id+"F0.wireOp",EDGE,"E11.rect.top"),sQuery(id+"F0.wireOp",EDGE,"E12.rect.left"),sQuery(id+"F0.wireOp",EDGE,"E12.rect.right"),sQuery(id+"F0.wireOp",EDGE,"E13.rect.left"),sQuery(id+"F0.wireOp",EDGE,"E13.rect.right"),sQuery(id+"F0.wireOp",EDGE,"E14.left"),sQuery(id+"F0.wireOp",EDGE,"E14.right"),sQuery(id+"F0.wireOp",EDGE,"E15"),sQuery(id+"F0.wireOp",EDGE,"E17"),sQuery(id+"F0.wireOp",EDGE,"E18"),sQuery(id+"F0.wireOp",EDGE,"E20"),sQuery(id+"F0.wireOp",EDGE,"E21.rect.bottom"),sQuery(id+"F0.wireOp",EDGE,"E21.rect.top"),sQuery(id+"F0.wireOp",EDGE,"E22.left"),sQuery(id+"F0.wireOp",EDGE,"E22.right"),sQuery(id+"F0.wireOp",EDGE,"E23.top"),sQuery(id+"F0.wireOp",EDGE,"E23.left"),sQuery(id+"F0.wireOp",EDGE,"E23.right"),sQuery(id+"F0.wireOp",EDGE,"E22.top"),sQuery(id+"F0.wireOp",EDGE,"E26"),sQuery(id+"F0.wireOp",EDGE,"E29"),sQuery(id+"F0.wireOp",EDGE,"E32"),sQuery(id+"F0.wireOp",EDGE,"E35"),sQuery(id+"F0.wireOp",EDGE,"E36"),sQuery(id+"F0.wireOp",EDGE,"E41"),sQuery(id+"F0.wireOp",EDGE,"E44"),sQuery(id+"F0.wireOp",EDGE,"E47"),subQ0,sQuery(id+"F0.wireOp",EDGE,"E49"),sQuery(id+"F0.wireOp",EDGE,"E50"),sQuery(id+"F0.wireOp",EDGE,"E51")])],"isStart":false})]});}
            var Q2;
            Q2=makeQuery(id+"F1.opExtrude","CAP_EDGE",EDGE,{"disambiguationData":[OSD([sQuery(id+"F0.wireOp",EDGE,"E48")])],"isStart":false});
            var Q3;
            {var subQ0=sQuery(id+"F0.wireOp",EDGE,"E48");var subQ1=sQuery(id+"F0.wireOp",EDGE,"E9.rect.right");Q3=makeQuery(id+"F3.opFillet","BLEND_EDGE",EDGE,{"blendedFrom":[makeQuery(id+"F1.opExtrude","SWEPT_EDGE",EDGE,{"disambiguationData":[OSD([subQ1,subQ0])]}),makeQuery(id+"F1.opExtrude","CAP_FACE",FACE,{"disambiguationData":[OSD([sQuery(id+"F0.wireOp",EDGE,"E0"),sQuery(id+"F0.wireOp",EDGE,"E1"),sQuery(id+"F0.wireOp",EDGE,"E2"),sQuery(id+"F0.wireOp",EDGE,"E3"),sQuery(id+"F0.wireOp",EDGE,"E4"),sQuery(id+"F0.wireOp",EDGE,"E5"),sQuery(id+"F0.wireOp",EDGE,"E6"),sQuery(id+"F0.wireOp",EDGE,"E7"),sQuery(id+"F0.wireOp",EDGE,"E9.rect.left"),subQ1,sQuery(id+"F0.wireOp",EDGE,"E10.rect.bottom"),sQuery(id+"F0.wireOp",EDGE,"E10.rect.top"),sQuery(id+"F0.wireOp",EDGE,"E11.rect.bottom"),sQuery(id+"F0.wireOp",EDGE,"E11.rect.top"),sQuery(id+"F0.wireOp",EDGE,"E12.rect.left"),sQuery(id+"F0.wireOp",EDGE,"E12.rect.right"),sQuery(id+"F0.wireOp",EDGE,"E13.rect.left"),sQuery(id+"F0.wireOp",EDGE,"E13.rect.right"),sQuery(id+"F0.wireOp",EDGE,"E14.left"),sQuery(id+"F0.wireOp",EDGE,"E14.right"),sQuery(id+"F0.wireOp",EDGE,"E15"),sQuery(id+"F0.wireOp",EDGE,"E17"),sQuery(id+"F0.wireOp",EDGE,"E18"),sQuery(id+"F0.wireOp",EDGE,"E20"),sQuery(id+"F0.wireOp",EDGE,"E21.rect.bottom"),sQuery(id+"F0.wireOp",EDGE,"E21.rect.top"),sQuery(id+"F0.wireOp",EDGE,"E22.left"),sQuery(id+"F0.wireOp",EDGE,"E22.right"),sQuery(id+"F0.wireOp",EDGE,"E23.top"),sQuery(id+"F0.wireOp",EDGE,"E23.left"),sQuery(id+"F0.wireOp",EDGE,"E23.right"),sQuery(id+"F0.wireOp",EDGE,"E22.top"),sQuery(id+"F0.wireOp",EDGE,"E26"),sQuery(id+"F0.wireOp",EDGE,"E29"),sQuery(id+"F0.wireOp",EDGE,"E32"),sQuery(id+"F0.wireOp",EDGE,"E35"),sQuery(id+"F0.wireOp",EDGE,"E36"),sQuery(id+"F0.wireOp",EDGE,"E41"),sQuery(id+"F0.wireOp",EDGE,"E44"),sQuery(id+"F0.wireOp",EDGE,"E47"),subQ0,sQuery(id+"F0.wireOp",EDGE,"E49"),sQuery(id+"F0.wireOp",EDGE,"E50"),sQuery(id+"F0.wireOp",EDGE,"E51")])],"isStart":false})],"blendedInto":[makeQuery(id+"F1.opExtrude","CAP_FACE",FACE,{"disambiguationData":[OSD([sQuery(id+"F0.wireOp",EDGE,"E0"),sQuery(id+"F0.wireOp",EDGE,"E1"),sQuery(id+"F0.wireOp",EDGE,"E2"),sQuery(id+"F0.wireOp",EDGE,"E3"),sQuery(id+"F0.wireOp",EDGE,"E4"),sQuery(id+"F0.wireOp",EDGE,"E5"),sQuery(id+"F0.wireOp",EDGE,"E6"),sQuery(id+"F0.wireOp",EDGE,"E7"),sQuery(id+"F0.wireOp",EDGE,"E9.rect.left"),subQ1,sQuery(id+"F0.wireOp",EDGE,"E10.rect.bottom"),sQuery(id+"F0.wireOp",EDGE,"E10.rect.top"),sQuery(id+"F0.wireOp",EDGE,"E11.rect.bottom"),sQuery(id+"F0.wireOp",EDGE,"E11.rect.top"),sQuery(id+"F0.wireOp",EDGE,"E12.rect.left"),sQuery(id+"F0.wireOp",EDGE,"E12.rect.right"),sQuery(id+"F0.wireOp",EDGE,"E13.rect.left"),sQuery(id+"F0.wireOp",EDGE,"E13.rect.right"),sQuery(id+"F0.wireOp",EDGE,"E14.left"),sQuery(id+"F0.wireOp",EDGE,"E14.right"),sQuery(id+"F0.wireOp",EDGE,"E15"),sQuery(id+"F0.wireOp",EDGE,"E17"),sQuery(id+"F0.wireOp",EDGE,"E18"),sQuery(id+"F0.wireOp",EDGE,"E20"),sQuery(id+"F0.wireOp",EDGE,"E21.rect.bottom"),sQuery(id+"F0.wireOp",EDGE,"E21.rect.top"),sQuery(id+"F0.wireOp",EDGE,"E22.left"),sQuery(id+"F0.wireOp",EDGE,"E22.right"),sQuery(id+"F0.wireOp",EDGE,"E23.top"),sQuery(id+"F0.wireOp",EDGE,"E23.left"),sQuery(id+"F0.wireOp",EDGE,"E23.right"),sQuery(id+"F0.wireOp",EDGE,"E22.top"),sQuery(id+"F0.wireOp",EDGE,"E26"),sQuery(id+"F0.wireOp",EDGE,"E29"),sQuery(id+"F0.wireOp",EDGE,"E32"),sQuery(id+"F0.wireOp",EDGE,"E35"),sQuery(id+"F0.wireOp",EDGE,"E36"),sQuery(id+"F0.wireOp",EDGE,"E41"),sQuery(id+"F0.wireOp",EDGE,"E44"),sQuery(id+"F0.wireOp",EDGE,"E47"),subQ0,sQuery(id+"F0.wireOp",EDGE,"E49"),sQuery(id+"F0.wireOp",EDGE,"E50"),sQuery(id+"F0.wireOp",EDGE,"E51")])],"isStart":false})]});}
            var Q4;
            {var subQ0=sQuery(id+"F0.wireOp",EDGE,"E9.rect.right");Q4=makeQuery(id+"F1.opExtrude","CAP_EDGE",EDGE,{"disambiguationData":[OSD([subQ0]),TDD([makeQuery(id+"F0.imprint","IMPRINT",EDGE,{"disambiguationData":[TD([[makeQuery(id+"F0.imprint","INTERSECT",VERTEX,{"derivedFrom":[subQ0,sQuery(id+"F0.wireOp",EDGE,"E48")]}),-1.0]])],"derivedFrom":subQ0})])],"isStart":false});}
            var Q5;
            {var subQ0=sQuery(id+"F0.wireOp",EDGE,"E50");var subQ1=sQuery(id+"F0.wireOp",EDGE,"E9.rect.right");Q5=makeQuery(id+"F3.opFillet","BLEND_EDGE",EDGE,{"blendedFrom":[makeQuery(id+"F1.opExtrude","SWEPT_EDGE",EDGE,{"disambiguationData":[OSD([subQ1,subQ0])]}),makeQuery(id+"F1.opExtrude","CAP_FACE",FACE,{"disambiguationData":[OSD([sQuery(id+"F0.wireOp",EDGE,"E0"),sQuery(id+"F0.wireOp",EDGE,"E1"),sQuery(id+"F0.wireOp",EDGE,"E2"),sQuery(id+"F0.wireOp",EDGE,"E3"),sQuery(id+"F0.wireOp",EDGE,"E4"),sQuery(id+"F0.wireOp",EDGE,"E5"),sQuery(id+"F0.wireOp",EDGE,"E6"),sQuery(id+"F0.wireOp",EDGE,"E7"),sQuery(id+"F0.wireOp",EDGE,"E9.rect.left"),subQ1,sQuery(id+"F0.wireOp",EDGE,"E10.rect.bottom"),sQuery(id+"F0.wireOp",EDGE,"E10.rect.top"),sQuery(id+"F0.wireOp",EDGE,"E11.rect.bottom"),sQuery(id+"F0.wireOp",EDGE,"E11.rect.top"),sQuery(id+"F0.wireOp",EDGE,"E12.rect.left"),sQuery(id+"F0.wireOp",EDGE,"E12.rect.right"),sQuery(id+"F0.wireOp",EDGE,"E13.rect.left"),sQuery(id+"F0.wireOp",EDGE,"E13.rect.right"),sQuery(id+"F0.wireOp",EDGE,"E14.left"),sQuery(id+"F0.wireOp",EDGE,"E14.right"),sQuery(id+"F0.wireOp",EDGE,"E15"),sQuery(id+"F0.wireOp",EDGE,"E17"),sQuery(id+"F0.wireOp",EDGE,"E18"),sQuery(id+"F0.wireOp",EDGE,"E20"),sQuery(id+"F0.wireOp",EDGE,"E21.rect.bottom"),sQuery(id+"F0.wireOp",EDGE,"E21.rect.top"),sQuery(id+"F0.wireOp",EDGE,"E22.left"),sQuery(id+"F0.wireOp",EDGE,"E22.right"),sQuery(id+"F0.wireOp",EDGE,"E23.top"),sQuery(id+"F0.wireOp",EDGE,"E23.left"),sQuery(id+"F0.wireOp",EDGE,"E23.right"),sQuery(id+"F0.wireOp",EDGE,"E22.top"),sQuery(id+"F0.wireOp",EDGE,"E26"),sQuery(id+"F0.wireOp",EDGE,"E29"),sQuery(id+"F0.wireOp",EDGE,"E32"),sQuery(id+"F0.wireOp",EDGE,"E35"),sQuery(id+"F0.wireOp",EDGE,"E36"),sQuery(id+"F0.wireOp",EDGE,"E41"),sQuery(id+"F0.wireOp",EDGE,"E44"),sQuery(id+"F0.wireOp",EDGE,"E47"),sQuery(id+"F0.wireOp",EDGE,"E48"),sQuery(id+"F0.wireOp",EDGE,"E49"),subQ0,sQuery(id+"F0.wireOp",EDGE,"E51")])],"isStart":false})],"blendedInto":[makeQuery(id+"F1.opExtrude","CAP_FACE",FACE,{"disambiguationData":[OSD([sQuery(id+"F0.wireOp",EDGE,"E0"),sQuery(id+"F0.wireOp",EDGE,"E1"),sQuery(id+"F0.wireOp",EDGE,"E2"),sQuery(id+"F0.wireOp",EDGE,"E3"),sQuery(id+"F0.wireOp",EDGE,"E4"),sQuery(id+"F0.wireOp",EDGE,"E5"),sQuery(id+"F0.wireOp",EDGE,"E6"),sQuery(id+"F0.wireOp",EDGE,"E7"),sQuery(id+"F0.wireOp",EDGE,"E9.rect.left"),subQ1,sQuery(id+"F0.wireOp",EDGE,"E10.rect.bottom"),sQuery(id+"F0.wireOp",EDGE,"E10.rect.top"),sQuery(id+"F0.wireOp",EDGE,"E11.rect.bottom"),sQuery(id+"F0.wireOp",EDGE,"E11.rect.top"),sQuery(id+"F0.wireOp",EDGE,"E12.rect.left"),sQuery(id+"F0.wireOp",EDGE,"E12.rect.right"),sQuery(id+"F0.wireOp",EDGE,"E13.rect.left"),sQuery(id+"F0.wireOp",EDGE,"E13.rect.right"),sQuery(id+"F0.wireOp",EDGE,"E14.left"),sQuery(id+"F0.wireOp",EDGE,"E14.right"),sQuery(id+"F0.wireOp",EDGE,"E15"),sQuery(id+"F0.wireOp",EDGE,"E17"),sQuery(id+"F0.wireOp",EDGE,"E18"),sQuery(id+"F0.wireOp",EDGE,"E20"),sQuery(id+"F0.wireOp",EDGE,"E21.rect.bottom"),sQuery(id+"F0.wireOp",EDGE,"E21.rect.top"),sQuery(id+"F0.wireOp",EDGE,"E22.left"),sQuery(id+"F0.wireOp",EDGE,"E22.right"),sQuery(id+"F0.wireOp",EDGE,"E23.top"),sQuery(id+"F0.wireOp",EDGE,"E23.left"),sQuery(id+"F0.wireOp",EDGE,"E23.right"),sQuery(id+"F0.wireOp",EDGE,"E22.top"),sQuery(id+"F0.wireOp",EDGE,"E26"),sQuery(id+"F0.wireOp",EDGE,"E29"),sQuery(id+"F0.wireOp",EDGE,"E32"),sQuery(id+"F0.wireOp",EDGE,"E35"),sQuery(id+"F0.wireOp",EDGE,"E36"),sQuery(id+"F0.wireOp",EDGE,"E41"),sQuery(id+"F0.wireOp",EDGE,"E44"),sQuery(id+"F0.wireOp",EDGE,"E47"),sQuery(id+"F0.wireOp",EDGE,"E48"),sQuery(id+"F0.wireOp",EDGE,"E49"),subQ0,sQuery(id+"F0.wireOp",EDGE,"E51")])],"isStart":false})]});}
            var Q6;
            Q6=makeQuery(id+"F1.opExtrude","CAP_EDGE",EDGE,{"disambiguationData":[OSD([sQuery(id+"F0.wireOp",EDGE,"E50")])],"isStart":false});
            var Q7;
            Q7=makeQuery(id+"F1.opExtrude","CAP_EDGE",EDGE,{"disambiguationData":[OSD([sQuery(id+"F0.wireOp",EDGE,"E7")])],"isStart":false});
            var Q8;
            {var subQ0=sQuery(id+"F0.wireOp",EDGE,"E35");var subQ1=sQuery(id+"F0.wireOp",EDGE,"E3");Q8=makeQuery(id+"F2.opFillet","BLEND_EDGE",EDGE,{"blendedFrom":[makeQuery(id+"F1.opExtrude","SWEPT_EDGE",EDGE,{"disambiguationData":[OSD([subQ1,subQ0])]}),makeQuery(id+"F1.opExtrude","CAP_FACE",FACE,{"disambiguationData":[OSD([sQuery(id+"F0.wireOp",EDGE,"E0"),sQuery(id+"F0.wireOp",EDGE,"E1"),sQuery(id+"F0.wireOp",EDGE,"E2"),subQ1,sQuery(id+"F0.wireOp",EDGE,"E4"),sQuery(id+"F0.wireOp",EDGE,"E5"),sQuery(id+"F0.wireOp",EDGE,"E6"),sQuery(id+"F0.wireOp",EDGE,"E7"),sQuery(id+"F0.wireOp",EDGE,"E9.rect.left"),sQuery(id+"F0.wireOp",EDGE,"E9.rect.right"),sQuery(id+"F0.wireOp",EDGE,"E10.rect.bottom"),sQuery(id+"F0.wireOp",EDGE,"E10.rect.top"),sQuery(id+"F0.wireOp",EDGE,"E11.rect.bottom"),sQuery(id+"F0.wireOp",EDGE,"E11.rect.top"),sQuery(id+"F0.wireOp",EDGE,"E12.rect.left"),sQuery(id+"F0.wireOp",EDGE,"E12.rect.right"),sQuery(id+"F0.wireOp",EDGE,"E13.rect.left"),sQuery(id+"F0.wireOp",EDGE,"E13.rect.right"),sQuery(id+"F0.wireOp",EDGE,"E14.left"),sQuery(id+"F0.wireOp",EDGE,"E14.right"),sQuery(id+"F0.wireOp",EDGE,"E15"),sQuery(id+"F0.wireOp",EDGE,"E17"),sQuery(id+"F0.wireOp",EDGE,"E18"),sQuery(id+"F0.wireOp",EDGE,"E20"),sQuery(id+"F0.wireOp",EDGE,"E21.rect.bottom"),sQuery(id+"F0.wireOp",EDGE,"E21.rect.top"),sQuery(id+"F0.wireOp",EDGE,"E22.left"),sQuery(id+"F0.wireOp",EDGE,"E22.right"),sQuery(id+"F0.wireOp",EDGE,"E23.top"),sQuery(id+"F0.wireOp",EDGE,"E23.left"),sQuery(id+"F0.wireOp",EDGE,"E23.right"),sQuery(id+"F0.wireOp",EDGE,"E22.top"),sQuery(id+"F0.wireOp",EDGE,"E26"),sQuery(id+"F0.wireOp",EDGE,"E29"),sQuery(id+"F0.wireOp",EDGE,"E32"),subQ0,sQuery(id+"F0.wireOp",EDGE,"E36"),sQuery(id+"F0.wireOp",EDGE,"E41"),sQuery(id+"F0.wireOp",EDGE,"E44"),sQuery(id+"F0.wireOp",EDGE,"E47"),sQuery(id+"F0.wireOp",EDGE,"E48"),sQuery(id+"F0.wireOp",EDGE,"E49"),sQuery(id+"F0.wireOp",EDGE,"E50"),sQuery(id+"F0.wireOp",EDGE,"E51")])],"isStart":false})],"blendedInto":[makeQuery(id+"F1.opExtrude","CAP_FACE",FACE,{"disambiguationData":[OSD([sQuery(id+"F0.wireOp",EDGE,"E0"),sQuery(id+"F0.wireOp",EDGE,"E1"),sQuery(id+"F0.wireOp",EDGE,"E2"),subQ1,sQuery(id+"F0.wireOp",EDGE,"E4"),sQuery(id+"F0.wireOp",EDGE,"E5"),sQuery(id+"F0.wireOp",EDGE,"E6"),sQuery(id+"F0.wireOp",EDGE,"E7"),sQuery(id+"F0.wireOp",EDGE,"E9.rect.left"),sQuery(id+"F0.wireOp",EDGE,"E9.rect.right"),sQuery(id+"F0.wireOp",EDGE,"E10.rect.bottom"),sQuery(id+"F0.wireOp",EDGE,"E10.rect.top"),sQuery(id+"F0.wireOp",EDGE,"E11.rect.bottom"),sQuery(id+"F0.wireOp",EDGE,"E11.rect.top"),sQuery(id+"F0.wireOp",EDGE,"E12.rect.left"),sQuery(id+"F0.wireOp",EDGE,"E12.rect.right"),sQuery(id+"F0.wireOp",EDGE,"E13.rect.left"),sQuery(id+"F0.wireOp",EDGE,"E13.rect.right"),sQuery(id+"F0.wireOp",EDGE,"E14.left"),sQuery(id+"F0.wireOp",EDGE,"E14.right"),sQuery(id+"F0.wireOp",EDGE,"E15"),sQuery(id+"F0.wireOp",EDGE,"E17"),sQuery(id+"F0.wireOp",EDGE,"E18"),sQuery(id+"F0.wireOp",EDGE,"E20"),sQuery(id+"F0.wireOp",EDGE,"E21.rect.bottom"),sQuery(id+"F0.wireOp",EDGE,"E21.rect.top"),sQuery(id+"F0.wireOp",EDGE,"E22.left"),sQuery(id+"F0.wireOp",EDGE,"E22.right"),sQuery(id+"F0.wireOp",EDGE,"E23.top"),sQuery(id+"F0.wireOp",EDGE,"E23.left"),sQuery(id+"F0.wireOp",EDGE,"E23.right"),sQuery(id+"F0.wireOp",EDGE,"E22.top"),sQuery(id+"F0.wireOp",EDGE,"E26"),sQuery(id+"F0.wireOp",EDGE,"E29"),sQuery(id+"F0.wireOp",EDGE,"E32"),subQ0,sQuery(id+"F0.wireOp",EDGE,"E36"),sQuery(id+"F0.wireOp",EDGE,"E41"),sQuery(id+"F0.wireOp",EDGE,"E44"),sQuery(id+"F0.wireOp",EDGE,"E47"),sQuery(id+"F0.wireOp",EDGE,"E48"),sQuery(id+"F0.wireOp",EDGE,"E49"),sQuery(id+"F0.wireOp",EDGE,"E50"),sQuery(id+"F0.wireOp",EDGE,"E51")])],"isStart":false})]});}
            var Q9;
            Q9=makeQuery(id+"F1.opExtrude","CAP_EDGE",EDGE,{"disambiguationData":[OSD([sQuery(id+"F0.wireOp",EDGE,"E3")])],"isStart":false});
            var Q10;
            Q10=makeQuery(id+"F1.opExtrude","CAP_EDGE",EDGE,{"disambiguationData":[OSD([sQuery(id+"F0.wireOp",EDGE,"E36")])],"isStart":false});
            var Q11;
            Q11=makeQuery(id+"F1.opExtrude","CAP_EDGE",EDGE,{"disambiguationData":[OSD([sQuery(id+"F0.wireOp",EDGE,"E10.rect.top")])],"isStart":false});
            var Q12;
            {var subQ0=sQuery(id+"F0.wireOp",EDGE,"E36");var subQ1=sQuery(id+"F0.wireOp",EDGE,"E12.rect.right");var subQ2=sQuery(id+"F0.wireOp",EDGE,"E10.rect.top");Q12=makeQuery(id+"F4.opFillet","BLEND_EDGE",EDGE,{"blendedFrom":[makeQuery(id+"F1.opExtrude","SWEPT_EDGE",EDGE,{"disambiguationData":[OSD([subQ2,subQ1,subQ0])]}),makeQuery(id+"F1.opExtrude","CAP_FACE",FACE,{"disambiguationData":[OSD([sQuery(id+"F0.wireOp",EDGE,"E0"),sQuery(id+"F0.wireOp",EDGE,"E1"),sQuery(id+"F0.wireOp",EDGE,"E2"),sQuery(id+"F0.wireOp",EDGE,"E3"),sQuery(id+"F0.wireOp",EDGE,"E4"),sQuery(id+"F0.wireOp",EDGE,"E5"),sQuery(id+"F0.wireOp",EDGE,"E6"),sQuery(id+"F0.wireOp",EDGE,"E7"),sQuery(id+"F0.wireOp",EDGE,"E9.rect.left"),sQuery(id+"F0.wireOp",EDGE,"E9.rect.right"),sQuery(id+"F0.wireOp",EDGE,"E10.rect.bottom"),subQ2,sQuery(id+"F0.wireOp",EDGE,"E11.rect.bottom"),sQuery(id+"F0.wireOp",EDGE,"E11.rect.top"),sQuery(id+"F0.wireOp",EDGE,"E12.rect.left"),subQ1,sQuery(id+"F0.wireOp",EDGE,"E13.rect.left"),sQuery(id+"F0.wireOp",EDGE,"E13.rect.right"),sQuery(id+"F0.wireOp",EDGE,"E14.left"),sQuery(id+"F0.wireOp",EDGE,"E14.right"),sQuery(id+"F0.wireOp",EDGE,"E15"),sQuery(id+"F0.wireOp",EDGE,"E17"),sQuery(id+"F0.wireOp",EDGE,"E18"),sQuery(id+"F0.wireOp",EDGE,"E20"),sQuery(id+"F0.wireOp",EDGE,"E21.rect.bottom"),sQuery(id+"F0.wireOp",EDGE,"E21.rect.top"),sQuery(id+"F0.wireOp",EDGE,"E22.left"),sQuery(id+"F0.wireOp",EDGE,"E22.right"),sQuery(id+"F0.wireOp",EDGE,"E23.top"),sQuery(id+"F0.wireOp",EDGE,"E23.left"),sQuery(id+"F0.wireOp",EDGE,"E23.right"),sQuery(id+"F0.wireOp",EDGE,"E22.top"),sQuery(id+"F0.wireOp",EDGE,"E26"),sQuery(id+"F0.wireOp",EDGE,"E29"),sQuery(id+"F0.wireOp",EDGE,"E32"),sQuery(id+"F0.wireOp",EDGE,"E35"),subQ0,sQuery(id+"F0.wireOp",EDGE,"E41"),sQuery(id+"F0.wireOp",EDGE,"E44"),sQuery(id+"F0.wireOp",EDGE,"E47"),sQuery(id+"F0.wireOp",EDGE,"E48"),sQuery(id+"F0.wireOp",EDGE,"E49"),sQuery(id+"F0.wireOp",EDGE,"E50"),sQuery(id+"F0.wireOp",EDGE,"E51")])],"isStart":false})],"blendedInto":[makeQuery(id+"F1.opExtrude","CAP_FACE",FACE,{"disambiguationData":[OSD([sQuery(id+"F0.wireOp",EDGE,"E0"),sQuery(id+"F0.wireOp",EDGE,"E1"),sQuery(id+"F0.wireOp",EDGE,"E2"),sQuery(id+"F0.wireOp",EDGE,"E3"),sQuery(id+"F0.wireOp",EDGE,"E4"),sQuery(id+"F0.wireOp",EDGE,"E5"),sQuery(id+"F0.wireOp",EDGE,"E6"),sQuery(id+"F0.wireOp",EDGE,"E7"),sQuery(id+"F0.wireOp",EDGE,"E9.rect.left"),sQuery(id+"F0.wireOp",EDGE,"E9.rect.right"),sQuery(id+"F0.wireOp",EDGE,"E10.rect.bottom"),subQ2,sQuery(id+"F0.wireOp",EDGE,"E11.rect.bottom"),sQuery(id+"F0.wireOp",EDGE,"E11.rect.top"),sQuery(id+"F0.wireOp",EDGE,"E12.rect.left"),subQ1,sQuery(id+"F0.wireOp",EDGE,"E13.rect.left"),sQuery(id+"F0.wireOp",EDGE,"E13.rect.right"),sQuery(id+"F0.wireOp",EDGE,"E14.left"),sQuery(id+"F0.wireOp",EDGE,"E14.right"),sQuery(id+"F0.wireOp",EDGE,"E15"),sQuery(id+"F0.wireOp",EDGE,"E17"),sQuery(id+"F0.wireOp",EDGE,"E18"),sQuery(id+"F0.wireOp",EDGE,"E20"),sQuery(id+"F0.wireOp",EDGE,"E21.rect.bottom"),sQuery(id+"F0.wireOp",EDGE,"E21.rect.top"),sQuery(id+"F0.wireOp",EDGE,"E22.left"),sQuery(id+"F0.wireOp",EDGE,"E22.right"),sQuery(id+"F0.wireOp",EDGE,"E23.top"),sQuery(id+"F0.wireOp",EDGE,"E23.left"),sQuery(id+"F0.wireOp",EDGE,"E23.right"),sQuery(id+"F0.wireOp",EDGE,"E22.top"),sQuery(id+"F0.wireOp",EDGE,"E26"),sQuery(id+"F0.wireOp",EDGE,"E29"),sQuery(id+"F0.wireOp",EDGE,"E32"),sQuery(id+"F0.wireOp",EDGE,"E35"),subQ0,sQuery(id+"F0.wireOp",EDGE,"E41"),sQuery(id+"F0.wireOp",EDGE,"E44"),sQuery(id+"F0.wireOp",EDGE,"E47"),sQuery(id+"F0.wireOp",EDGE,"E48"),sQuery(id+"F0.wireOp",EDGE,"E49"),sQuery(id+"F0.wireOp",EDGE,"E50"),sQuery(id+"F0.wireOp",EDGE,"E51")])],"isStart":false})]});}
            var Q13;
            {var subQ0=sQuery(id+"F0.wireOp",EDGE,"E41");var subQ1=sQuery(id+"F0.wireOp",EDGE,"E12.rect.left");var subQ2=sQuery(id+"F0.wireOp",EDGE,"E10.rect.top");Q13=makeQuery(id+"F4.opFillet","BLEND_EDGE",EDGE,{"blendedFrom":[makeQuery(id+"F1.opExtrude","SWEPT_EDGE",EDGE,{"disambiguationData":[OSD([subQ2,subQ1,subQ0])]}),makeQuery(id+"F1.opExtrude","CAP_FACE",FACE,{"disambiguationData":[OSD([sQuery(id+"F0.wireOp",EDGE,"E0"),sQuery(id+"F0.wireOp",EDGE,"E1"),sQuery(id+"F0.wireOp",EDGE,"E2"),sQuery(id+"F0.wireOp",EDGE,"E3"),sQuery(id+"F0.wireOp",EDGE,"E4"),sQuery(id+"F0.wireOp",EDGE,"E5"),sQuery(id+"F0.wireOp",EDGE,"E6"),sQuery(id+"F0.wireOp",EDGE,"E7"),sQuery(id+"F0.wireOp",EDGE,"E9.rect.left"),sQuery(id+"F0.wireOp",EDGE,"E9.rect.right"),sQuery(id+"F0.wireOp",EDGE,"E10.rect.bottom"),subQ2,sQuery(id+"F0.wireOp",EDGE,"E11.rect.bottom"),sQuery(id+"F0.wireOp",EDGE,"E11.rect.top"),subQ1,sQuery(id+"F0.wireOp",EDGE,"E12.rect.right"),sQuery(id+"F0.wireOp",EDGE,"E13.rect.left"),sQuery(id+"F0.wireOp",EDGE,"E13.rect.right"),sQuery(id+"F0.wireOp",EDGE,"E14.left"),sQuery(id+"F0.wireOp",EDGE,"E14.right"),sQuery(id+"F0.wireOp",EDGE,"E15"),sQuery(id+"F0.wireOp",EDGE,"E17"),sQuery(id+"F0.wireOp",EDGE,"E18"),sQuery(id+"F0.wireOp",EDGE,"E20"),sQuery(id+"F0.wireOp",EDGE,"E21.rect.bottom"),sQuery(id+"F0.wireOp",EDGE,"E21.rect.top"),sQuery(id+"F0.wireOp",EDGE,"E22.left"),sQuery(id+"F0.wireOp",EDGE,"E22.right"),sQuery(id+"F0.wireOp",EDGE,"E23.top"),sQuery(id+"F0.wireOp",EDGE,"E23.left"),sQuery(id+"F0.wireOp",EDGE,"E23.right"),sQuery(id+"F0.wireOp",EDGE,"E22.top"),sQuery(id+"F0.wireOp",EDGE,"E26"),sQuery(id+"F0.wireOp",EDGE,"E29"),sQuery(id+"F0.wireOp",EDGE,"E32"),sQuery(id+"F0.wireOp",EDGE,"E35"),sQuery(id+"F0.wireOp",EDGE,"E36"),subQ0,sQuery(id+"F0.wireOp",EDGE,"E44"),sQuery(id+"F0.wireOp",EDGE,"E47"),sQuery(id+"F0.wireOp",EDGE,"E48"),sQuery(id+"F0.wireOp",EDGE,"E49"),sQuery(id+"F0.wireOp",EDGE,"E50"),sQuery(id+"F0.wireOp",EDGE,"E51")])],"isStart":false})],"blendedInto":[makeQuery(id+"F1.opExtrude","CAP_FACE",FACE,{"disambiguationData":[OSD([sQuery(id+"F0.wireOp",EDGE,"E0"),sQuery(id+"F0.wireOp",EDGE,"E1"),sQuery(id+"F0.wireOp",EDGE,"E2"),sQuery(id+"F0.wireOp",EDGE,"E3"),sQuery(id+"F0.wireOp",EDGE,"E4"),sQuery(id+"F0.wireOp",EDGE,"E5"),sQuery(id+"F0.wireOp",EDGE,"E6"),sQuery(id+"F0.wireOp",EDGE,"E7"),sQuery(id+"F0.wireOp",EDGE,"E9.rect.left"),sQuery(id+"F0.wireOp",EDGE,"E9.rect.right"),sQuery(id+"F0.wireOp",EDGE,"E10.rect.bottom"),subQ2,sQuery(id+"F0.wireOp",EDGE,"E11.rect.bottom"),sQuery(id+"F0.wireOp",EDGE,"E11.rect.top"),subQ1,sQuery(id+"F0.wireOp",EDGE,"E12.rect.right"),sQuery(id+"F0.wireOp",EDGE,"E13.rect.left"),sQuery(id+"F0.wireOp",EDGE,"E13.rect.right"),sQuery(id+"F0.wireOp",EDGE,"E14.left"),sQuery(id+"F0.wireOp",EDGE,"E14.right"),sQuery(id+"F0.wireOp",EDGE,"E15"),sQuery(id+"F0.wireOp",EDGE,"E17"),sQuery(id+"F0.wireOp",EDGE,"E18"),sQuery(id+"F0.wireOp",EDGE,"E20"),sQuery(id+"F0.wireOp",EDGE,"E21.rect.bottom"),sQuery(id+"F0.wireOp",EDGE,"E21.rect.top"),sQuery(id+"F0.wireOp",EDGE,"E22.left"),sQuery(id+"F0.wireOp",EDGE,"E22.right"),sQuery(id+"F0.wireOp",EDGE,"E23.top"),sQuery(id+"F0.wireOp",EDGE,"E23.left"),sQuery(id+"F0.wireOp",EDGE,"E23.right"),sQuery(id+"F0.wireOp",EDGE,"E22.top"),sQuery(id+"F0.wireOp",EDGE,"E26"),sQuery(id+"F0.wireOp",EDGE,"E29"),sQuery(id+"F0.wireOp",EDGE,"E32"),sQuery(id+"F0.wireOp",EDGE,"E35"),sQuery(id+"F0.wireOp",EDGE,"E36"),subQ0,sQuery(id+"F0.wireOp",EDGE,"E44"),sQuery(id+"F0.wireOp",EDGE,"E47"),sQuery(id+"F0.wireOp",EDGE,"E48"),sQuery(id+"F0.wireOp",EDGE,"E49"),sQuery(id+"F0.wireOp",EDGE,"E50"),sQuery(id+"F0.wireOp",EDGE,"E51")])],"isStart":false})]});}
            var Q14;
            Q14=makeQuery(id+"F1.opExtrude","CAP_EDGE",EDGE,{"disambiguationData":[OSD([sQuery(id+"F0.wireOp",EDGE,"E41")])],"isStart":false});
            var Q15;
            {var subQ0=sQuery(id+"F0.wireOp",EDGE,"E9.rect.left");var subQ1=sQuery(id+"F0.wireOp",EDGE,"E2");Q15=makeQuery(id+"F3.opFillet","BLEND_EDGE",EDGE,{"blendedFrom":[makeQuery(id+"F1.opExtrude","SWEPT_EDGE",EDGE,{"disambiguationData":[OSD([subQ1,subQ0])]}),makeQuery(id+"F1.opExtrude","CAP_FACE",FACE,{"disambiguationData":[OSD([sQuery(id+"F0.wireOp",EDGE,"E0"),sQuery(id+"F0.wireOp",EDGE,"E1"),subQ1,sQuery(id+"F0.wireOp",EDGE,"E3"),sQuery(id+"F0.wireOp",EDGE,"E4"),sQuery(id+"F0.wireOp",EDGE,"E5"),sQuery(id+"F0.wireOp",EDGE,"E6"),sQuery(id+"F0.wireOp",EDGE,"E7"),subQ0,sQuery(id+"F0.wireOp",EDGE,"E9.rect.right"),sQuery(id+"F0.wireOp",EDGE,"E10.rect.bottom"),sQuery(id+"F0.wireOp",EDGE,"E10.rect.top"),sQuery(id+"F0.wireOp",EDGE,"E11.rect.bottom"),sQuery(id+"F0.wireOp",EDGE,"E11.rect.top"),sQuery(id+"F0.wireOp",EDGE,"E12.rect.left"),sQuery(id+"F0.wireOp",EDGE,"E12.rect.right"),sQuery(id+"F0.wireOp",EDGE,"E13.rect.left"),sQuery(id+"F0.wireOp",EDGE,"E13.rect.right"),sQuery(id+"F0.wireOp",EDGE,"E14.left"),sQuery(id+"F0.wireOp",EDGE,"E14.right"),sQuery(id+"F0.wireOp",EDGE,"E15"),sQuery(id+"F0.wireOp",EDGE,"E17"),sQuery(id+"F0.wireOp",EDGE,"E18"),sQuery(id+"F0.wireOp",EDGE,"E20"),sQuery(id+"F0.wireOp",EDGE,"E21.rect.bottom"),sQuery(id+"F0.wireOp",EDGE,"E21.rect.top"),sQuery(id+"F0.wireOp",EDGE,"E22.left"),sQuery(id+"F0.wireOp",EDGE,"E22.right"),sQuery(id+"F0.wireOp",EDGE,"E23.top"),sQuery(id+"F0.wireOp",EDGE,"E23.left"),sQuery(id+"F0.wireOp",EDGE,"E23.right"),sQuery(id+"F0.wireOp",EDGE,"E22.top"),sQuery(id+"F0.wireOp",EDGE,"E26"),sQuery(id+"F0.wireOp",EDGE,"E29"),sQuery(id+"F0.wireOp",EDGE,"E32"),sQuery(id+"F0.wireOp",EDGE,"E35"),sQuery(id+"F0.wireOp",EDGE,"E36"),sQuery(id+"F0.wireOp",EDGE,"E41"),sQuery(id+"F0.wireOp",EDGE,"E44"),sQuery(id+"F0.wireOp",EDGE,"E47"),sQuery(id+"F0.wireOp",EDGE,"E48"),sQuery(id+"F0.wireOp",EDGE,"E49"),sQuery(id+"F0.wireOp",EDGE,"E50"),sQuery(id+"F0.wireOp",EDGE,"E51")])],"isStart":false})],"blendedInto":[makeQuery(id+"F1.opExtrude","CAP_FACE",FACE,{"disambiguationData":[OSD([sQuery(id+"F0.wireOp",EDGE,"E0"),sQuery(id+"F0.wireOp",EDGE,"E1"),subQ1,sQuery(id+"F0.wireOp",EDGE,"E3"),sQuery(id+"F0.wireOp",EDGE,"E4"),sQuery(id+"F0.wireOp",EDGE,"E5"),sQuery(id+"F0.wireOp",EDGE,"E6"),sQuery(id+"F0.wireOp",EDGE,"E7"),subQ0,sQuery(id+"F0.wireOp",EDGE,"E9.rect.right"),sQuery(id+"F0.wireOp",EDGE,"E10.rect.bottom"),sQuery(id+"F0.wireOp",EDGE,"E10.rect.top"),sQuery(id+"F0.wireOp",EDGE,"E11.rect.bottom"),sQuery(id+"F0.wireOp",EDGE,"E11.rect.top"),sQuery(id+"F0.wireOp",EDGE,"E12.rect.left"),sQuery(id+"F0.wireOp",EDGE,"E12.rect.right"),sQuery(id+"F0.wireOp",EDGE,"E13.rect.left"),sQuery(id+"F0.wireOp",EDGE,"E13.rect.right"),sQuery(id+"F0.wireOp",EDGE,"E14.left"),sQuery(id+"F0.wireOp",EDGE,"E14.right"),sQuery(id+"F0.wireOp",EDGE,"E15"),sQuery(id+"F0.wireOp",EDGE,"E17"),sQuery(id+"F0.wireOp",EDGE,"E18"),sQuery(id+"F0.wireOp",EDGE,"E20"),sQuery(id+"F0.wireOp",EDGE,"E21.rect.bottom"),sQuery(id+"F0.wireOp",EDGE,"E21.rect.top"),sQuery(id+"F0.wireOp",EDGE,"E22.left"),sQuery(id+"F0.wireOp",EDGE,"E22.right"),sQuery(id+"F0.wireOp",EDGE,"E23.top"),sQuery(id+"F0.wireOp",EDGE,"E23.left"),sQuery(id+"F0.wireOp",EDGE,"E23.right"),sQuery(id+"F0.wireOp",EDGE,"E22.top"),sQuery(id+"F0.wireOp",EDGE,"E26"),sQuery(id+"F0.wireOp",EDGE,"E29"),sQuery(id+"F0.wireOp",EDGE,"E32"),sQuery(id+"F0.wireOp",EDGE,"E35"),sQuery(id+"F0.wireOp",EDGE,"E36"),sQuery(id+"F0.wireOp",EDGE,"E41"),sQuery(id+"F0.wireOp",EDGE,"E44"),sQuery(id+"F0.wireOp",EDGE,"E47"),sQuery(id+"F0.wireOp",EDGE,"E48"),sQuery(id+"F0.wireOp",EDGE,"E49"),sQuery(id+"F0.wireOp",EDGE,"E50"),sQuery(id+"F0.wireOp",EDGE,"E51")])],"isStart":false})]});}
            var Q16;
            {var subQ0=sQuery(id+"F0.wireOp",EDGE,"E9.rect.right");var subQ1=sQuery(id+"F0.wireOp",EDGE,"E3");Q16=makeQuery(id+"F3.opFillet","BLEND_EDGE",EDGE,{"blendedFrom":[makeQuery(id+"F1.opExtrude","SWEPT_EDGE",EDGE,{"disambiguationData":[OSD([subQ1,subQ0])]}),makeQuery(id+"F1.opExtrude","CAP_FACE",FACE,{"disambiguationData":[OSD([sQuery(id+"F0.wireOp",EDGE,"E0"),sQuery(id+"F0.wireOp",EDGE,"E1"),sQuery(id+"F0.wireOp",EDGE,"E2"),subQ1,sQuery(id+"F0.wireOp",EDGE,"E4"),sQuery(id+"F0.wireOp",EDGE,"E5"),sQuery(id+"F0.wireOp",EDGE,"E6"),sQuery(id+"F0.wireOp",EDGE,"E7"),sQuery(id+"F0.wireOp",EDGE,"E9.rect.left"),subQ0,sQuery(id+"F0.wireOp",EDGE,"E10.rect.bottom"),sQuery(id+"F0.wireOp",EDGE,"E10.rect.top"),sQuery(id+"F0.wireOp",EDGE,"E11.rect.bottom"),sQuery(id+"F0.wireOp",EDGE,"E11.rect.top"),sQuery(id+"F0.wireOp",EDGE,"E12.rect.left"),sQuery(id+"F0.wireOp",EDGE,"E12.rect.right"),sQuery(id+"F0.wireOp",EDGE,"E13.rect.left"),sQuery(id+"F0.wireOp",EDGE,"E13.rect.right"),sQuery(id+"F0.wireOp",EDGE,"E14.left"),sQuery(id+"F0.wireOp",EDGE,"E14.right"),sQuery(id+"F0.wireOp",EDGE,"E15"),sQuery(id+"F0.wireOp",EDGE,"E17"),sQuery(id+"F0.wireOp",EDGE,"E18"),sQuery(id+"F0.wireOp",EDGE,"E20"),sQuery(id+"F0.wireOp",EDGE,"E21.rect.bottom"),sQuery(id+"F0.wireOp",EDGE,"E21.rect.top"),sQuery(id+"F0.wireOp",EDGE,"E22.left"),sQuery(id+"F0.wireOp",EDGE,"E22.right"),sQuery(id+"F0.wireOp",EDGE,"E23.top"),sQuery(id+"F0.wireOp",EDGE,"E23.left"),sQuery(id+"F0.wireOp",EDGE,"E23.right"),sQuery(id+"F0.wireOp",EDGE,"E22.top"),sQuery(id+"F0.wireOp",EDGE,"E26"),sQuery(id+"F0.wireOp",EDGE,"E29"),sQuery(id+"F0.wireOp",EDGE,"E32"),sQuery(id+"F0.wireOp",EDGE,"E35"),sQuery(id+"F0.wireOp",EDGE,"E36"),sQuery(id+"F0.wireOp",EDGE,"E41"),sQuery(id+"F0.wireOp",EDGE,"E44"),sQuery(id+"F0.wireOp",EDGE,"E47"),sQuery(id+"F0.wireOp",EDGE,"E48"),sQuery(id+"F0.wireOp",EDGE,"E49"),sQuery(id+"F0.wireOp",EDGE,"E50"),sQuery(id+"F0.wireOp",EDGE,"E51")])],"isStart":false})],"blendedInto":[makeQuery(id+"F1.opExtrude","CAP_FACE",FACE,{"disambiguationData":[OSD([sQuery(id+"F0.wireOp",EDGE,"E0"),sQuery(id+"F0.wireOp",EDGE,"E1"),sQuery(id+"F0.wireOp",EDGE,"E2"),subQ1,sQuery(id+"F0.wireOp",EDGE,"E4"),sQuery(id+"F0.wireOp",EDGE,"E5"),sQuery(id+"F0.wireOp",EDGE,"E6"),sQuery(id+"F0.wireOp",EDGE,"E7"),sQuery(id+"F0.wireOp",EDGE,"E9.rect.left"),subQ0,sQuery(id+"F0.wireOp",EDGE,"E10.rect.bottom"),sQuery(id+"F0.wireOp",EDGE,"E10.rect.top"),sQuery(id+"F0.wireOp",EDGE,"E11.rect.bottom"),sQuery(id+"F0.wireOp",EDGE,"E11.rect.top"),sQuery(id+"F0.wireOp",EDGE,"E12.rect.left"),sQuery(id+"F0.wireOp",EDGE,"E12.rect.right"),sQuery(id+"F0.wireOp",EDGE,"E13.rect.left"),sQuery(id+"F0.wireOp",EDGE,"E13.rect.right"),sQuery(id+"F0.wireOp",EDGE,"E14.left"),sQuery(id+"F0.wireOp",EDGE,"E14.right"),sQuery(id+"F0.wireOp",EDGE,"E15"),sQuery(id+"F0.wireOp",EDGE,"E17"),sQuery(id+"F0.wireOp",EDGE,"E18"),sQuery(id+"F0.wireOp",EDGE,"E20"),sQuery(id+"F0.wireOp",EDGE,"E21.rect.bottom"),sQuery(id+"F0.wireOp",EDGE,"E21.rect.top"),sQuery(id+"F0.wireOp",EDGE,"E22.left"),sQuery(id+"F0.wireOp",EDGE,"E22.right"),sQuery(id+"F0.wireOp",EDGE,"E23.top"),sQuery(id+"F0.wireOp",EDGE,"E23.left"),sQuery(id+"F0.wireOp",EDGE,"E23.right"),sQuery(id+"F0.wireOp",EDGE,"E22.top"),sQuery(id+"F0.wireOp",EDGE,"E26"),sQuery(id+"F0.wireOp",EDGE,"E29"),sQuery(id+"F0.wireOp",EDGE,"E32"),sQuery(id+"F0.wireOp",EDGE,"E35"),sQuery(id+"F0.wireOp",EDGE,"E36"),sQuery(id+"F0.wireOp",EDGE,"E41"),sQuery(id+"F0.wireOp",EDGE,"E44"),sQuery(id+"F0.wireOp",EDGE,"E47"),sQuery(id+"F0.wireOp",EDGE,"E48"),sQuery(id+"F0.wireOp",EDGE,"E49"),sQuery(id+"F0.wireOp",EDGE,"E50"),sQuery(id+"F0.wireOp",EDGE,"E51")])],"isStart":false})]});}
            var Q17;
            Q17=makeQuery(id+"F1.opExtrude","CAP_EDGE",EDGE,{"disambiguationData":[OSD([sQuery(id+"F0.wireOp",EDGE,"E2")])],"isStart":false});
            var Q18;
            {var subQ0=sQuery(id+"F0.wireOp",EDGE,"E32");var subQ1=sQuery(id+"F0.wireOp",EDGE,"E6");Q18=makeQuery(id+"F2.opFillet","BLEND_EDGE",EDGE,{"blendedFrom":[makeQuery(id+"F1.opExtrude","SWEPT_EDGE",EDGE,{"disambiguationData":[OSD([subQ1,subQ0])]}),makeQuery(id+"F1.opExtrude","CAP_FACE",FACE,{"disambiguationData":[OSD([sQuery(id+"F0.wireOp",EDGE,"E0"),sQuery(id+"F0.wireOp",EDGE,"E1"),sQuery(id+"F0.wireOp",EDGE,"E2"),sQuery(id+"F0.wireOp",EDGE,"E3"),sQuery(id+"F0.wireOp",EDGE,"E4"),sQuery(id+"F0.wireOp",EDGE,"E5"),subQ1,sQuery(id+"F0.wireOp",EDGE,"E7"),sQuery(id+"F0.wireOp",EDGE,"E9.rect.left"),sQuery(id+"F0.wireOp",EDGE,"E9.rect.right"),sQuery(id+"F0.wireOp",EDGE,"E10.rect.bottom"),sQuery(id+"F0.wireOp",EDGE,"E10.rect.top"),sQuery(id+"F0.wireOp",EDGE,"E11.rect.bottom"),sQuery(id+"F0.wireOp",EDGE,"E11.rect.top"),sQuery(id+"F0.wireOp",EDGE,"E12.rect.left"),sQuery(id+"F0.wireOp",EDGE,"E12.rect.right"),sQuery(id+"F0.wireOp",EDGE,"E13.rect.left"),sQuery(id+"F0.wireOp",EDGE,"E13.rect.right"),sQuery(id+"F0.wireOp",EDGE,"E14.left"),sQuery(id+"F0.wireOp",EDGE,"E14.right"),sQuery(id+"F0.wireOp",EDGE,"E15"),sQuery(id+"F0.wireOp",EDGE,"E17"),sQuery(id+"F0.wireOp",EDGE,"E18"),sQuery(id+"F0.wireOp",EDGE,"E20"),sQuery(id+"F0.wireOp",EDGE,"E21.rect.bottom"),sQuery(id+"F0.wireOp",EDGE,"E21.rect.top"),sQuery(id+"F0.wireOp",EDGE,"E22.left"),sQuery(id+"F0.wireOp",EDGE,"E22.right"),sQuery(id+"F0.wireOp",EDGE,"E23.top"),sQuery(id+"F0.wireOp",EDGE,"E23.left"),sQuery(id+"F0.wireOp",EDGE,"E23.right"),sQuery(id+"F0.wireOp",EDGE,"E22.top"),sQuery(id+"F0.wireOp",EDGE,"E26"),sQuery(id+"F0.wireOp",EDGE,"E29"),subQ0,sQuery(id+"F0.wireOp",EDGE,"E35"),sQuery(id+"F0.wireOp",EDGE,"E36"),sQuery(id+"F0.wireOp",EDGE,"E41"),sQuery(id+"F0.wireOp",EDGE,"E44"),sQuery(id+"F0.wireOp",EDGE,"E47"),sQuery(id+"F0.wireOp",EDGE,"E48"),sQuery(id+"F0.wireOp",EDGE,"E49"),sQuery(id+"F0.wireOp",EDGE,"E50"),sQuery(id+"F0.wireOp",EDGE,"E51")])],"isStart":false})],"blendedInto":[makeQuery(id+"F1.opExtrude","CAP_FACE",FACE,{"disambiguationData":[OSD([sQuery(id+"F0.wireOp",EDGE,"E0"),sQuery(id+"F0.wireOp",EDGE,"E1"),sQuery(id+"F0.wireOp",EDGE,"E2"),sQuery(id+"F0.wireOp",EDGE,"E3"),sQuery(id+"F0.wireOp",EDGE,"E4"),sQuery(id+"F0.wireOp",EDGE,"E5"),subQ1,sQuery(id+"F0.wireOp",EDGE,"E7"),sQuery(id+"F0.wireOp",EDGE,"E9.rect.left"),sQuery(id+"F0.wireOp",EDGE,"E9.rect.right"),sQuery(id+"F0.wireOp",EDGE,"E10.rect.bottom"),sQuery(id+"F0.wireOp",EDGE,"E10.rect.top"),sQuery(id+"F0.wireOp",EDGE,"E11.rect.bottom"),sQuery(id+"F0.wireOp",EDGE,"E11.rect.top"),sQuery(id+"F0.wireOp",EDGE,"E12.rect.left"),sQuery(id+"F0.wireOp",EDGE,"E12.rect.right"),sQuery(id+"F0.wireOp",EDGE,"E13.rect.left"),sQuery(id+"F0.wireOp",EDGE,"E13.rect.right"),sQuery(id+"F0.wireOp",EDGE,"E14.left"),sQuery(id+"F0.wireOp",EDGE,"E14.right"),sQuery(id+"F0.wireOp",EDGE,"E15"),sQuery(id+"F0.wireOp",EDGE,"E17"),sQuery(id+"F0.wireOp",EDGE,"E18"),sQuery(id+"F0.wireOp",EDGE,"E20"),sQuery(id+"F0.wireOp",EDGE,"E21.rect.bottom"),sQuery(id+"F0.wireOp",EDGE,"E21.rect.top"),sQuery(id+"F0.wireOp",EDGE,"E22.left"),sQuery(id+"F0.wireOp",EDGE,"E22.right"),sQuery(id+"F0.wireOp",EDGE,"E23.top"),sQuery(id+"F0.wireOp",EDGE,"E23.left"),sQuery(id+"F0.wireOp",EDGE,"E23.right"),sQuery(id+"F0.wireOp",EDGE,"E22.top"),sQuery(id+"F0.wireOp",EDGE,"E26"),sQuery(id+"F0.wireOp",EDGE,"E29"),subQ0,sQuery(id+"F0.wireOp",EDGE,"E35"),sQuery(id+"F0.wireOp",EDGE,"E36"),sQuery(id+"F0.wireOp",EDGE,"E41"),sQuery(id+"F0.wireOp",EDGE,"E44"),sQuery(id+"F0.wireOp",EDGE,"E47"),sQuery(id+"F0.wireOp",EDGE,"E48"),sQuery(id+"F0.wireOp",EDGE,"E49"),sQuery(id+"F0.wireOp",EDGE,"E50"),sQuery(id+"F0.wireOp",EDGE,"E51")])],"isStart":false})]});}
            var Q19;
            Q19=makeQuery(id+"F1.opExtrude","CAP_EDGE",EDGE,{"disambiguationData":[OSD([sQuery(id+"F0.wireOp",EDGE,"E6")])],"isStart":false});
            var Q20;
            Q20=makeQuery(id+"F1.opExtrude","CAP_EDGE",EDGE,{"disambiguationData":[OSD([sQuery(id+"F0.wireOp",EDGE,"E51")])],"isStart":false});
            var Q21;
            {var subQ0=sQuery(id+"F0.wireOp",EDGE,"E51");var subQ1=sQuery(id+"F0.wireOp",EDGE,"E6");Q21=makeQuery(id+"F3.opFillet","BLEND_EDGE",EDGE,{"blendedFrom":[makeQuery(id+"F1.opExtrude","SWEPT_EDGE",EDGE,{"disambiguationData":[OSD([subQ1,subQ0])]}),makeQuery(id+"F1.opExtrude","CAP_FACE",FACE,{"disambiguationData":[OSD([sQuery(id+"F0.wireOp",EDGE,"E0"),sQuery(id+"F0.wireOp",EDGE,"E1"),sQuery(id+"F0.wireOp",EDGE,"E2"),sQuery(id+"F0.wireOp",EDGE,"E3"),sQuery(id+"F0.wireOp",EDGE,"E4"),sQuery(id+"F0.wireOp",EDGE,"E5"),subQ1,sQuery(id+"F0.wireOp",EDGE,"E7"),sQuery(id+"F0.wireOp",EDGE,"E9.rect.left"),sQuery(id+"F0.wireOp",EDGE,"E9.rect.right"),sQuery(id+"F0.wireOp",EDGE,"E10.rect.bottom"),sQuery(id+"F0.wireOp",EDGE,"E10.rect.top"),sQuery(id+"F0.wireOp",EDGE,"E11.rect.bottom"),sQuery(id+"F0.wireOp",EDGE,"E11.rect.top"),sQuery(id+"F0.wireOp",EDGE,"E12.rect.left"),sQuery(id+"F0.wireOp",EDGE,"E12.rect.right"),sQuery(id+"F0.wireOp",EDGE,"E13.rect.left"),sQuery(id+"F0.wireOp",EDGE,"E13.rect.right"),sQuery(id+"F0.wireOp",EDGE,"E14.left"),sQuery(id+"F0.wireOp",EDGE,"E14.right"),sQuery(id+"F0.wireOp",EDGE,"E15"),sQuery(id+"F0.wireOp",EDGE,"E17"),sQuery(id+"F0.wireOp",EDGE,"E18"),sQuery(id+"F0.wireOp",EDGE,"E20"),sQuery(id+"F0.wireOp",EDGE,"E21.rect.bottom"),sQuery(id+"F0.wireOp",EDGE,"E21.rect.top"),sQuery(id+"F0.wireOp",EDGE,"E22.left"),sQuery(id+"F0.wireOp",EDGE,"E22.right"),sQuery(id+"F0.wireOp",EDGE,"E23.top"),sQuery(id+"F0.wireOp",EDGE,"E23.left"),sQuery(id+"F0.wireOp",EDGE,"E23.right"),sQuery(id+"F0.wireOp",EDGE,"E22.top"),sQuery(id+"F0.wireOp",EDGE,"E26"),sQuery(id+"F0.wireOp",EDGE,"E29"),sQuery(id+"F0.wireOp",EDGE,"E32"),sQuery(id+"F0.wireOp",EDGE,"E35"),sQuery(id+"F0.wireOp",EDGE,"E36"),sQuery(id+"F0.wireOp",EDGE,"E41"),sQuery(id+"F0.wireOp",EDGE,"E44"),sQuery(id+"F0.wireOp",EDGE,"E47"),sQuery(id+"F0.wireOp",EDGE,"E48"),sQuery(id+"F0.wireOp",EDGE,"E49"),sQuery(id+"F0.wireOp",EDGE,"E50"),subQ0])],"isStart":false})],"blendedInto":[makeQuery(id+"F1.opExtrude","CAP_FACE",FACE,{"disambiguationData":[OSD([sQuery(id+"F0.wireOp",EDGE,"E0"),sQuery(id+"F0.wireOp",EDGE,"E1"),sQuery(id+"F0.wireOp",EDGE,"E2"),sQuery(id+"F0.wireOp",EDGE,"E3"),sQuery(id+"F0.wireOp",EDGE,"E4"),sQuery(id+"F0.wireOp",EDGE,"E5"),subQ1,sQuery(id+"F0.wireOp",EDGE,"E7"),sQuery(id+"F0.wireOp",EDGE,"E9.rect.left"),sQuery(id+"F0.wireOp",EDGE,"E9.rect.right"),sQuery(id+"F0.wireOp",EDGE,"E10.rect.bottom"),sQuery(id+"F0.wireOp",EDGE,"E10.rect.top"),sQuery(id+"F0.wireOp",EDGE,"E11.rect.bottom"),sQuery(id+"F0.wireOp",EDGE,"E11.rect.top"),sQuery(id+"F0.wireOp",EDGE,"E12.rect.left"),sQuery(id+"F0.wireOp",EDGE,"E12.rect.right"),sQuery(id+"F0.wireOp",EDGE,"E13.rect.left"),sQuery(id+"F0.wireOp",EDGE,"E13.rect.right"),sQuery(id+"F0.wireOp",EDGE,"E14.left"),sQuery(id+"F0.wireOp",EDGE,"E14.right"),sQuery(id+"F0.wireOp",EDGE,"E15"),sQuery(id+"F0.wireOp",EDGE,"E17"),sQuery(id+"F0.wireOp",EDGE,"E18"),sQuery(id+"F0.wireOp",EDGE,"E20"),sQuery(id+"F0.wireOp",EDGE,"E21.rect.bottom"),sQuery(id+"F0.wireOp",EDGE,"E21.rect.top"),sQuery(id+"F0.wireOp",EDGE,"E22.left"),sQuery(id+"F0.wireOp",EDGE,"E22.right"),sQuery(id+"F0.wireOp",EDGE,"E23.top"),sQuery(id+"F0.wireOp",EDGE,"E23.left"),sQuery(id+"F0.wireOp",EDGE,"E23.right"),sQuery(id+"F0.wireOp",EDGE,"E22.top"),sQuery(id+"F0.wireOp",EDGE,"E26"),sQuery(id+"F0.wireOp",EDGE,"E29"),sQuery(id+"F0.wireOp",EDGE,"E32"),sQuery(id+"F0.wireOp",EDGE,"E35"),sQuery(id+"F0.wireOp",EDGE,"E36"),sQuery(id+"F0.wireOp",EDGE,"E41"),sQuery(id+"F0.wireOp",EDGE,"E44"),sQuery(id+"F0.wireOp",EDGE,"E47"),sQuery(id+"F0.wireOp",EDGE,"E48"),sQuery(id+"F0.wireOp",EDGE,"E49"),sQuery(id+"F0.wireOp",EDGE,"E50"),subQ0])],"isStart":false})]});}
            var Q22;
            {var subQ0=sQuery(id+"F0.wireOp",EDGE,"E51");var subQ1=sQuery(id+"F0.wireOp",EDGE,"E9.rect.left");Q22=makeQuery(id+"F3.opFillet","BLEND_EDGE",EDGE,{"blendedFrom":[makeQuery(id+"F1.opExtrude","SWEPT_EDGE",EDGE,{"disambiguationData":[OSD([subQ1,subQ0])]}),makeQuery(id+"F1.opExtrude","CAP_FACE",FACE,{"disambiguationData":[OSD([sQuery(id+"F0.wireOp",EDGE,"E0"),sQuery(id+"F0.wireOp",EDGE,"E1"),sQuery(id+"F0.wireOp",EDGE,"E2"),sQuery(id+"F0.wireOp",EDGE,"E3"),sQuery(id+"F0.wireOp",EDGE,"E4"),sQuery(id+"F0.wireOp",EDGE,"E5"),sQuery(id+"F0.wireOp",EDGE,"E6"),sQuery(id+"F0.wireOp",EDGE,"E7"),subQ1,sQuery(id+"F0.wireOp",EDGE,"E9.rect.right"),sQuery(id+"F0.wireOp",EDGE,"E10.rect.bottom"),sQuery(id+"F0.wireOp",EDGE,"E10.rect.top"),sQuery(id+"F0.wireOp",EDGE,"E11.rect.bottom"),sQuery(id+"F0.wireOp",EDGE,"E11.rect.top"),sQuery(id+"F0.wireOp",EDGE,"E12.rect.left"),sQuery(id+"F0.wireOp",EDGE,"E12.rect.right"),sQuery(id+"F0.wireOp",EDGE,"E13.rect.left"),sQuery(id+"F0.wireOp",EDGE,"E13.rect.right"),sQuery(id+"F0.wireOp",EDGE,"E14.left"),sQuery(id+"F0.wireOp",EDGE,"E14.right"),sQuery(id+"F0.wireOp",EDGE,"E15"),sQuery(id+"F0.wireOp",EDGE,"E17"),sQuery(id+"F0.wireOp",EDGE,"E18"),sQuery(id+"F0.wireOp",EDGE,"E20"),sQuery(id+"F0.wireOp",EDGE,"E21.rect.bottom"),sQuery(id+"F0.wireOp",EDGE,"E21.rect.top"),sQuery(id+"F0.wireOp",EDGE,"E22.left"),sQuery(id+"F0.wireOp",EDGE,"E22.right"),sQuery(id+"F0.wireOp",EDGE,"E23.top"),sQuery(id+"F0.wireOp",EDGE,"E23.left"),sQuery(id+"F0.wireOp",EDGE,"E23.right"),sQuery(id+"F0.wireOp",EDGE,"E22.top"),sQuery(id+"F0.wireOp",EDGE,"E26"),sQuery(id+"F0.wireOp",EDGE,"E29"),sQuery(id+"F0.wireOp",EDGE,"E32"),sQuery(id+"F0.wireOp",EDGE,"E35"),sQuery(id+"F0.wireOp",EDGE,"E36"),sQuery(id+"F0.wireOp",EDGE,"E41"),sQuery(id+"F0.wireOp",EDGE,"E44"),sQuery(id+"F0.wireOp",EDGE,"E47"),sQuery(id+"F0.wireOp",EDGE,"E48"),sQuery(id+"F0.wireOp",EDGE,"E49"),sQuery(id+"F0.wireOp",EDGE,"E50"),subQ0])],"isStart":false})],"blendedInto":[makeQuery(id+"F1.opExtrude","CAP_FACE",FACE,{"disambiguationData":[OSD([sQuery(id+"F0.wireOp",EDGE,"E0"),sQuery(id+"F0.wireOp",EDGE,"E1"),sQuery(id+"F0.wireOp",EDGE,"E2"),sQuery(id+"F0.wireOp",EDGE,"E3"),sQuery(id+"F0.wireOp",EDGE,"E4"),sQuery(id+"F0.wireOp",EDGE,"E5"),sQuery(id+"F0.wireOp",EDGE,"E6"),sQuery(id+"F0.wireOp",EDGE,"E7"),subQ1,sQuery(id+"F0.wireOp",EDGE,"E9.rect.right"),sQuery(id+"F0.wireOp",EDGE,"E10.rect.bottom"),sQuery(id+"F0.wireOp",EDGE,"E10.rect.top"),sQuery(id+"F0.wireOp",EDGE,"E11.rect.bottom"),sQuery(id+"F0.wireOp",EDGE,"E11.rect.top"),sQuery(id+"F0.wireOp",EDGE,"E12.rect.left"),sQuery(id+"F0.wireOp",EDGE,"E12.rect.right"),sQuery(id+"F0.wireOp",EDGE,"E13.rect.left"),sQuery(id+"F0.wireOp",EDGE,"E13.rect.right"),sQuery(id+"F0.wireOp",EDGE,"E14.left"),sQuery(id+"F0.wireOp",EDGE,"E14.right"),sQuery(id+"F0.wireOp",EDGE,"E15"),sQuery(id+"F0.wireOp",EDGE,"E17"),sQuery(id+"F0.wireOp",EDGE,"E18"),sQuery(id+"F0.wireOp",EDGE,"E20"),sQuery(id+"F0.wireOp",EDGE,"E21.rect.bottom"),sQuery(id+"F0.wireOp",EDGE,"E21.rect.top"),sQuery(id+"F0.wireOp",EDGE,"E22.left"),sQuery(id+"F0.wireOp",EDGE,"E22.right"),sQuery(id+"F0.wireOp",EDGE,"E23.top"),sQuery(id+"F0.wireOp",EDGE,"E23.left"),sQuery(id+"F0.wireOp",EDGE,"E23.right"),sQuery(id+"F0.wireOp",EDGE,"E22.top"),sQuery(id+"F0.wireOp",EDGE,"E26"),sQuery(id+"F0.wireOp",EDGE,"E29"),sQuery(id+"F0.wireOp",EDGE,"E32"),sQuery(id+"F0.wireOp",EDGE,"E35"),sQuery(id+"F0.wireOp",EDGE,"E36"),sQuery(id+"F0.wireOp",EDGE,"E41"),sQuery(id+"F0.wireOp",EDGE,"E44"),sQuery(id+"F0.wireOp",EDGE,"E47"),sQuery(id+"F0.wireOp",EDGE,"E48"),sQuery(id+"F0.wireOp",EDGE,"E49"),sQuery(id+"F0.wireOp",EDGE,"E50"),subQ0])],"isStart":false})]});}
            var Q23;
            {var subQ0=sQuery(id+"F0.wireOp",EDGE,"E9.rect.left");Q23=makeQuery(id+"F1.opExtrude","CAP_EDGE",EDGE,{"disambiguationData":[OSD([subQ0]),TDD([makeQuery(id+"F0.imprint","IMPRINT",EDGE,{"disambiguationData":[TD([[makeQuery(id+"F0.imprint","INTERSECT",VERTEX,{"derivedFrom":[subQ0,sQuery(id+"F0.wireOp",EDGE,"E49")]}),-1.0]])],"derivedFrom":subQ0})])],"isStart":false});}
            var Q24;
            {var subQ0=sQuery(id+"F0.wireOp",EDGE,"E49");var subQ1=sQuery(id+"F0.wireOp",EDGE,"E9.rect.left");Q24=makeQuery(id+"F3.opFillet","BLEND_EDGE",EDGE,{"blendedFrom":[makeQuery(id+"F1.opExtrude","SWEPT_EDGE",EDGE,{"disambiguationData":[OSD([subQ1,subQ0])]}),makeQuery(id+"F1.opExtrude","CAP_FACE",FACE,{"disambiguationData":[OSD([sQuery(id+"F0.wireOp",EDGE,"E0"),sQuery(id+"F0.wireOp",EDGE,"E1"),sQuery(id+"F0.wireOp",EDGE,"E2"),sQuery(id+"F0.wireOp",EDGE,"E3"),sQuery(id+"F0.wireOp",EDGE,"E4"),sQuery(id+"F0.wireOp",EDGE,"E5"),sQuery(id+"F0.wireOp",EDGE,"E6"),sQuery(id+"F0.wireOp",EDGE,"E7"),subQ1,sQuery(id+"F0.wireOp",EDGE,"E9.rect.right"),sQuery(id+"F0.wireOp",EDGE,"E10.rect.bottom"),sQuery(id+"F0.wireOp",EDGE,"E10.rect.top"),sQuery(id+"F0.wireOp",EDGE,"E11.rect.bottom"),sQuery(id+"F0.wireOp",EDGE,"E11.rect.top"),sQuery(id+"F0.wireOp",EDGE,"E12.rect.left"),sQuery(id+"F0.wireOp",EDGE,"E12.rect.right"),sQuery(id+"F0.wireOp",EDGE,"E13.rect.left"),sQuery(id+"F0.wireOp",EDGE,"E13.rect.right"),sQuery(id+"F0.wireOp",EDGE,"E14.left"),sQuery(id+"F0.wireOp",EDGE,"E14.right"),sQuery(id+"F0.wireOp",EDGE,"E15"),sQuery(id+"F0.wireOp",EDGE,"E17"),sQuery(id+"F0.wireOp",EDGE,"E18"),sQuery(id+"F0.wireOp",EDGE,"E20"),sQuery(id+"F0.wireOp",EDGE,"E21.rect.bottom"),sQuery(id+"F0.wireOp",EDGE,"E21.rect.top"),sQuery(id+"F0.wireOp",EDGE,"E22.left"),sQuery(id+"F0.wireOp",EDGE,"E22.right"),sQuery(id+"F0.wireOp",EDGE,"E23.top"),sQuery(id+"F0.wireOp",EDGE,"E23.left"),sQuery(id+"F0.wireOp",EDGE,"E23.right"),sQuery(id+"F0.wireOp",EDGE,"E22.top"),sQuery(id+"F0.wireOp",EDGE,"E26"),sQuery(id+"F0.wireOp",EDGE,"E29"),sQuery(id+"F0.wireOp",EDGE,"E32"),sQuery(id+"F0.wireOp",EDGE,"E35"),sQuery(id+"F0.wireOp",EDGE,"E36"),sQuery(id+"F0.wireOp",EDGE,"E41"),sQuery(id+"F0.wireOp",EDGE,"E44"),sQuery(id+"F0.wireOp",EDGE,"E47"),sQuery(id+"F0.wireOp",EDGE,"E48"),subQ0,sQuery(id+"F0.wireOp",EDGE,"E50"),sQuery(id+"F0.wireOp",EDGE,"E51")])],"isStart":false})],"blendedInto":[makeQuery(id+"F1.opExtrude","CAP_FACE",FACE,{"disambiguationData":[OSD([sQuery(id+"F0.wireOp",EDGE,"E0"),sQuery(id+"F0.wireOp",EDGE,"E1"),sQuery(id+"F0.wireOp",EDGE,"E2"),sQuery(id+"F0.wireOp",EDGE,"E3"),sQuery(id+"F0.wireOp",EDGE,"E4"),sQuery(id+"F0.wireOp",EDGE,"E5"),sQuery(id+"F0.wireOp",EDGE,"E6"),sQuery(id+"F0.wireOp",EDGE,"E7"),subQ1,sQuery(id+"F0.wireOp",EDGE,"E9.rect.right"),sQuery(id+"F0.wireOp",EDGE,"E10.rect.bottom"),sQuery(id+"F0.wireOp",EDGE,"E10.rect.top"),sQuery(id+"F0.wireOp",EDGE,"E11.rect.bottom"),sQuery(id+"F0.wireOp",EDGE,"E11.rect.top"),sQuery(id+"F0.wireOp",EDGE,"E12.rect.left"),sQuery(id+"F0.wireOp",EDGE,"E12.rect.right"),sQuery(id+"F0.wireOp",EDGE,"E13.rect.left"),sQuery(id+"F0.wireOp",EDGE,"E13.rect.right"),sQuery(id+"F0.wireOp",EDGE,"E14.left"),sQuery(id+"F0.wireOp",EDGE,"E14.right"),sQuery(id+"F0.wireOp",EDGE,"E15"),sQuery(id+"F0.wireOp",EDGE,"E17"),sQuery(id+"F0.wireOp",EDGE,"E18"),sQuery(id+"F0.wireOp",EDGE,"E20"),sQuery(id+"F0.wireOp",EDGE,"E21.rect.bottom"),sQuery(id+"F0.wireOp",EDGE,"E21.rect.top"),sQuery(id+"F0.wireOp",EDGE,"E22.left"),sQuery(id+"F0.wireOp",EDGE,"E22.right"),sQuery(id+"F0.wireOp",EDGE,"E23.top"),sQuery(id+"F0.wireOp",EDGE,"E23.left"),sQuery(id+"F0.wireOp",EDGE,"E23.right"),sQuery(id+"F0.wireOp",EDGE,"E22.top"),sQuery(id+"F0.wireOp",EDGE,"E26"),sQuery(id+"F0.wireOp",EDGE,"E29"),sQuery(id+"F0.wireOp",EDGE,"E32"),sQuery(id+"F0.wireOp",EDGE,"E35"),sQuery(id+"F0.wireOp",EDGE,"E36"),sQuery(id+"F0.wireOp",EDGE,"E41"),sQuery(id+"F0.wireOp",EDGE,"E44"),sQuery(id+"F0.wireOp",EDGE,"E47"),sQuery(id+"F0.wireOp",EDGE,"E48"),subQ0,sQuery(id+"F0.wireOp",EDGE,"E50"),sQuery(id+"F0.wireOp",EDGE,"E51")])],"isStart":false})]});}
            var Q25;
            Q25=makeQuery(id+"F1.opExtrude","CAP_EDGE",EDGE,{"disambiguationData":[OSD([sQuery(id+"F0.wireOp",EDGE,"E49")])],"isStart":false});
            var Q26;
            Q26=makeQuery(id+"F1.opExtrude","CAP_EDGE",EDGE,{"disambiguationData":[OSD([sQuery(id+"F0.wireOp",EDGE,"E5")])],"isStart":false});
            var Q27;
            {var subQ0=sQuery(id+"F0.wireOp",EDGE,"E49");var subQ1=sQuery(id+"F0.wireOp",EDGE,"E5");Q27=makeQuery(id+"F3.opFillet","BLEND_EDGE",EDGE,{"blendedFrom":[makeQuery(id+"F1.opExtrude","SWEPT_EDGE",EDGE,{"disambiguationData":[OSD([subQ1,subQ0])]}),makeQuery(id+"F1.opExtrude","CAP_FACE",FACE,{"disambiguationData":[OSD([sQuery(id+"F0.wireOp",EDGE,"E0"),sQuery(id+"F0.wireOp",EDGE,"E1"),sQuery(id+"F0.wireOp",EDGE,"E2"),sQuery(id+"F0.wireOp",EDGE,"E3"),sQuery(id+"F0.wireOp",EDGE,"E4"),subQ1,sQuery(id+"F0.wireOp",EDGE,"E6"),sQuery(id+"F0.wireOp",EDGE,"E7"),sQuery(id+"F0.wireOp",EDGE,"E9.rect.left"),sQuery(id+"F0.wireOp",EDGE,"E9.rect.right"),sQuery(id+"F0.wireOp",EDGE,"E10.rect.bottom"),sQuery(id+"F0.wireOp",EDGE,"E10.rect.top"),sQuery(id+"F0.wireOp",EDGE,"E11.rect.bottom"),sQuery(id+"F0.wireOp",EDGE,"E11.rect.top"),sQuery(id+"F0.wireOp",EDGE,"E12.rect.left"),sQuery(id+"F0.wireOp",EDGE,"E12.rect.right"),sQuery(id+"F0.wireOp",EDGE,"E13.rect.left"),sQuery(id+"F0.wireOp",EDGE,"E13.rect.right"),sQuery(id+"F0.wireOp",EDGE,"E14.left"),sQuery(id+"F0.wireOp",EDGE,"E14.right"),sQuery(id+"F0.wireOp",EDGE,"E15"),sQuery(id+"F0.wireOp",EDGE,"E17"),sQuery(id+"F0.wireOp",EDGE,"E18"),sQuery(id+"F0.wireOp",EDGE,"E20"),sQuery(id+"F0.wireOp",EDGE,"E21.rect.bottom"),sQuery(id+"F0.wireOp",EDGE,"E21.rect.top"),sQuery(id+"F0.wireOp",EDGE,"E22.left"),sQuery(id+"F0.wireOp",EDGE,"E22.right"),sQuery(id+"F0.wireOp",EDGE,"E23.top"),sQuery(id+"F0.wireOp",EDGE,"E23.left"),sQuery(id+"F0.wireOp",EDGE,"E23.right"),sQuery(id+"F0.wireOp",EDGE,"E22.top"),sQuery(id+"F0.wireOp",EDGE,"E26"),sQuery(id+"F0.wireOp",EDGE,"E29"),sQuery(id+"F0.wireOp",EDGE,"E32"),sQuery(id+"F0.wireOp",EDGE,"E35"),sQuery(id+"F0.wireOp",EDGE,"E36"),sQuery(id+"F0.wireOp",EDGE,"E41"),sQuery(id+"F0.wireOp",EDGE,"E44"),sQuery(id+"F0.wireOp",EDGE,"E47"),sQuery(id+"F0.wireOp",EDGE,"E48"),subQ0,sQuery(id+"F0.wireOp",EDGE,"E50"),sQuery(id+"F0.wireOp",EDGE,"E51")])],"isStart":false})],"blendedInto":[makeQuery(id+"F1.opExtrude","CAP_FACE",FACE,{"disambiguationData":[OSD([sQuery(id+"F0.wireOp",EDGE,"E0"),sQuery(id+"F0.wireOp",EDGE,"E1"),sQuery(id+"F0.wireOp",EDGE,"E2"),sQuery(id+"F0.wireOp",EDGE,"E3"),sQuery(id+"F0.wireOp",EDGE,"E4"),subQ1,sQuery(id+"F0.wireOp",EDGE,"E6"),sQuery(id+"F0.wireOp",EDGE,"E7"),sQuery(id+"F0.wireOp",EDGE,"E9.rect.left"),sQuery(id+"F0.wireOp",EDGE,"E9.rect.right"),sQuery(id+"F0.wireOp",EDGE,"E10.rect.bottom"),sQuery(id+"F0.wireOp",EDGE,"E10.rect.top"),sQuery(id+"F0.wireOp",EDGE,"E11.rect.bottom"),sQuery(id+"F0.wireOp",EDGE,"E11.rect.top"),sQuery(id+"F0.wireOp",EDGE,"E12.rect.left"),sQuery(id+"F0.wireOp",EDGE,"E12.rect.right"),sQuery(id+"F0.wireOp",EDGE,"E13.rect.left"),sQuery(id+"F0.wireOp",EDGE,"E13.rect.right"),sQuery(id+"F0.wireOp",EDGE,"E14.left"),sQuery(id+"F0.wireOp",EDGE,"E14.right"),sQuery(id+"F0.wireOp",EDGE,"E15"),sQuery(id+"F0.wireOp",EDGE,"E17"),sQuery(id+"F0.wireOp",EDGE,"E18"),sQuery(id+"F0.wireOp",EDGE,"E20"),sQuery(id+"F0.wireOp",EDGE,"E21.rect.bottom"),sQuery(id+"F0.wireOp",EDGE,"E21.rect.top"),sQuery(id+"F0.wireOp",EDGE,"E22.left"),sQuery(id+"F0.wireOp",EDGE,"E22.right"),sQuery(id+"F0.wireOp",EDGE,"E23.top"),sQuery(id+"F0.wireOp",EDGE,"E23.left"),sQuery(id+"F0.wireOp",EDGE,"E23.right"),sQuery(id+"F0.wireOp",EDGE,"E22.top"),sQuery(id+"F0.wireOp",EDGE,"E26"),sQuery(id+"F0.wireOp",EDGE,"E29"),sQuery(id+"F0.wireOp",EDGE,"E32"),sQuery(id+"F0.wireOp",EDGE,"E35"),sQuery(id+"F0.wireOp",EDGE,"E36"),sQuery(id+"F0.wireOp",EDGE,"E41"),sQuery(id+"F0.wireOp",EDGE,"E44"),sQuery(id+"F0.wireOp",EDGE,"E47"),sQuery(id+"F0.wireOp",EDGE,"E48"),subQ0,sQuery(id+"F0.wireOp",EDGE,"E50"),sQuery(id+"F0.wireOp",EDGE,"E51")])],"isStart":false})]});}
            var Q28;
            {var subQ0=sQuery(id+"F0.wireOp",EDGE,"E29");var subQ1=sQuery(id+"F0.wireOp",EDGE,"E1");Q28=makeQuery(id+"F2.opFillet","BLEND_EDGE",EDGE,{"blendedFrom":[makeQuery(id+"F1.opExtrude","SWEPT_EDGE",EDGE,{"disambiguationData":[OSD([subQ1,subQ0])]}),makeQuery(id+"F1.opExtrude","CAP_FACE",FACE,{"disambiguationData":[OSD([sQuery(id+"F0.wireOp",EDGE,"E0"),subQ1,sQuery(id+"F0.wireOp",EDGE,"E2"),sQuery(id+"F0.wireOp",EDGE,"E3"),sQuery(id+"F0.wireOp",EDGE,"E4"),sQuery(id+"F0.wireOp",EDGE,"E5"),sQuery(id+"F0.wireOp",EDGE,"E6"),sQuery(id+"F0.wireOp",EDGE,"E7"),sQuery(id+"F0.wireOp",EDGE,"E9.rect.left"),sQuery(id+"F0.wireOp",EDGE,"E9.rect.right"),sQuery(id+"F0.wireOp",EDGE,"E10.rect.bottom"),sQuery(id+"F0.wireOp",EDGE,"E10.rect.top"),sQuery(id+"F0.wireOp",EDGE,"E11.rect.bottom"),sQuery(id+"F0.wireOp",EDGE,"E11.rect.top"),sQuery(id+"F0.wireOp",EDGE,"E12.rect.left"),sQuery(id+"F0.wireOp",EDGE,"E12.rect.right"),sQuery(id+"F0.wireOp",EDGE,"E13.rect.left"),sQuery(id+"F0.wireOp",EDGE,"E13.rect.right"),sQuery(id+"F0.wireOp",EDGE,"E14.left"),sQuery(id+"F0.wireOp",EDGE,"E14.right"),sQuery(id+"F0.wireOp",EDGE,"E15"),sQuery(id+"F0.wireOp",EDGE,"E17"),sQuery(id+"F0.wireOp",EDGE,"E18"),sQuery(id+"F0.wireOp",EDGE,"E20"),sQuery(id+"F0.wireOp",EDGE,"E21.rect.bottom"),sQuery(id+"F0.wireOp",EDGE,"E21.rect.top"),sQuery(id+"F0.wireOp",EDGE,"E22.left"),sQuery(id+"F0.wireOp",EDGE,"E22.right"),sQuery(id+"F0.wireOp",EDGE,"E23.top"),sQuery(id+"F0.wireOp",EDGE,"E23.left"),sQuery(id+"F0.wireOp",EDGE,"E23.right"),sQuery(id+"F0.wireOp",EDGE,"E22.top"),sQuery(id+"F0.wireOp",EDGE,"E26"),subQ0,sQuery(id+"F0.wireOp",EDGE,"E32"),sQuery(id+"F0.wireOp",EDGE,"E35"),sQuery(id+"F0.wireOp",EDGE,"E36"),sQuery(id+"F0.wireOp",EDGE,"E41"),sQuery(id+"F0.wireOp",EDGE,"E44"),sQuery(id+"F0.wireOp",EDGE,"E47"),sQuery(id+"F0.wireOp",EDGE,"E48"),sQuery(id+"F0.wireOp",EDGE,"E49"),sQuery(id+"F0.wireOp",EDGE,"E50"),sQuery(id+"F0.wireOp",EDGE,"E51")])],"isStart":false})],"blendedInto":[makeQuery(id+"F1.opExtrude","CAP_FACE",FACE,{"disambiguationData":[OSD([sQuery(id+"F0.wireOp",EDGE,"E0"),subQ1,sQuery(id+"F0.wireOp",EDGE,"E2"),sQuery(id+"F0.wireOp",EDGE,"E3"),sQuery(id+"F0.wireOp",EDGE,"E4"),sQuery(id+"F0.wireOp",EDGE,"E5"),sQuery(id+"F0.wireOp",EDGE,"E6"),sQuery(id+"F0.wireOp",EDGE,"E7"),sQuery(id+"F0.wireOp",EDGE,"E9.rect.left"),sQuery(id+"F0.wireOp",EDGE,"E9.rect.right"),sQuery(id+"F0.wireOp",EDGE,"E10.rect.bottom"),sQuery(id+"F0.wireOp",EDGE,"E10.rect.top"),sQuery(id+"F0.wireOp",EDGE,"E11.rect.bottom"),sQuery(id+"F0.wireOp",EDGE,"E11.rect.top"),sQuery(id+"F0.wireOp",EDGE,"E12.rect.left"),sQuery(id+"F0.wireOp",EDGE,"E12.rect.right"),sQuery(id+"F0.wireOp",EDGE,"E13.rect.left"),sQuery(id+"F0.wireOp",EDGE,"E13.rect.right"),sQuery(id+"F0.wireOp",EDGE,"E14.left"),sQuery(id+"F0.wireOp",EDGE,"E14.right"),sQuery(id+"F0.wireOp",EDGE,"E15"),sQuery(id+"F0.wireOp",EDGE,"E17"),sQuery(id+"F0.wireOp",EDGE,"E18"),sQuery(id+"F0.wireOp",EDGE,"E20"),sQuery(id+"F0.wireOp",EDGE,"E21.rect.bottom"),sQuery(id+"F0.wireOp",EDGE,"E21.rect.top"),sQuery(id+"F0.wireOp",EDGE,"E22.left"),sQuery(id+"F0.wireOp",EDGE,"E22.right"),sQuery(id+"F0.wireOp",EDGE,"E23.top"),sQuery(id+"F0.wireOp",EDGE,"E23.left"),sQuery(id+"F0.wireOp",EDGE,"E23.right"),sQuery(id+"F0.wireOp",EDGE,"E22.top"),sQuery(id+"F0.wireOp",EDGE,"E26"),subQ0,sQuery(id+"F0.wireOp",EDGE,"E32"),sQuery(id+"F0.wireOp",EDGE,"E35"),sQuery(id+"F0.wireOp",EDGE,"E36"),sQuery(id+"F0.wireOp",EDGE,"E41"),sQuery(id+"F0.wireOp",EDGE,"E44"),sQuery(id+"F0.wireOp",EDGE,"E47"),sQuery(id+"F0.wireOp",EDGE,"E48"),sQuery(id+"F0.wireOp",EDGE,"E49"),sQuery(id+"F0.wireOp",EDGE,"E50"),sQuery(id+"F0.wireOp",EDGE,"E51")])],"isStart":false})]});}
            var Q29;
            Q29=makeQuery(id+"F1.opExtrude","CAP_EDGE",EDGE,{"disambiguationData":[OSD([sQuery(id+"F0.wireOp",EDGE,"E1")])],"isStart":false});
            var Q30;
            Q30=makeQuery(id+"F1.opExtrude","CAP_EDGE",EDGE,{"disambiguationData":[OSD([sQuery(id+"F0.wireOp",EDGE,"E44")])],"isStart":false});
            var Q31;
            {var subQ0=sQuery(id+"F0.wireOp",EDGE,"E44");var subQ1=sQuery(id+"F0.wireOp",EDGE,"E12.rect.left");var subQ2=sQuery(id+"F0.wireOp",EDGE,"E10.rect.bottom");Q31=makeQuery(id+"F4.opFillet","BLEND_EDGE",EDGE,{"blendedFrom":[makeQuery(id+"F1.opExtrude","SWEPT_EDGE",EDGE,{"disambiguationData":[OSD([subQ2,subQ1,subQ0])]}),makeQuery(id+"F1.opExtrude","CAP_FACE",FACE,{"disambiguationData":[OSD([sQuery(id+"F0.wireOp",EDGE,"E0"),sQuery(id+"F0.wireOp",EDGE,"E1"),sQuery(id+"F0.wireOp",EDGE,"E2"),sQuery(id+"F0.wireOp",EDGE,"E3"),sQuery(id+"F0.wireOp",EDGE,"E4"),sQuery(id+"F0.wireOp",EDGE,"E5"),sQuery(id+"F0.wireOp",EDGE,"E6"),sQuery(id+"F0.wireOp",EDGE,"E7"),sQuery(id+"F0.wireOp",EDGE,"E9.rect.left"),sQuery(id+"F0.wireOp",EDGE,"E9.rect.right"),subQ2,sQuery(id+"F0.wireOp",EDGE,"E10.rect.top"),sQuery(id+"F0.wireOp",EDGE,"E11.rect.bottom"),sQuery(id+"F0.wireOp",EDGE,"E11.rect.top"),subQ1,sQuery(id+"F0.wireOp",EDGE,"E12.rect.right"),sQuery(id+"F0.wireOp",EDGE,"E13.rect.left"),sQuery(id+"F0.wireOp",EDGE,"E13.rect.right"),sQuery(id+"F0.wireOp",EDGE,"E14.left"),sQuery(id+"F0.wireOp",EDGE,"E14.right"),sQuery(id+"F0.wireOp",EDGE,"E15"),sQuery(id+"F0.wireOp",EDGE,"E17"),sQuery(id+"F0.wireOp",EDGE,"E18"),sQuery(id+"F0.wireOp",EDGE,"E20"),sQuery(id+"F0.wireOp",EDGE,"E21.rect.bottom"),sQuery(id+"F0.wireOp",EDGE,"E21.rect.top"),sQuery(id+"F0.wireOp",EDGE,"E22.left"),sQuery(id+"F0.wireOp",EDGE,"E22.right"),sQuery(id+"F0.wireOp",EDGE,"E23.top"),sQuery(id+"F0.wireOp",EDGE,"E23.left"),sQuery(id+"F0.wireOp",EDGE,"E23.right"),sQuery(id+"F0.wireOp",EDGE,"E22.top"),sQuery(id+"F0.wireOp",EDGE,"E26"),sQuery(id+"F0.wireOp",EDGE,"E29"),sQuery(id+"F0.wireOp",EDGE,"E32"),sQuery(id+"F0.wireOp",EDGE,"E35"),sQuery(id+"F0.wireOp",EDGE,"E36"),sQuery(id+"F0.wireOp",EDGE,"E41"),subQ0,sQuery(id+"F0.wireOp",EDGE,"E47"),sQuery(id+"F0.wireOp",EDGE,"E48"),sQuery(id+"F0.wireOp",EDGE,"E49"),sQuery(id+"F0.wireOp",EDGE,"E50"),sQuery(id+"F0.wireOp",EDGE,"E51")])],"isStart":false})],"blendedInto":[makeQuery(id+"F1.opExtrude","CAP_FACE",FACE,{"disambiguationData":[OSD([sQuery(id+"F0.wireOp",EDGE,"E0"),sQuery(id+"F0.wireOp",EDGE,"E1"),sQuery(id+"F0.wireOp",EDGE,"E2"),sQuery(id+"F0.wireOp",EDGE,"E3"),sQuery(id+"F0.wireOp",EDGE,"E4"),sQuery(id+"F0.wireOp",EDGE,"E5"),sQuery(id+"F0.wireOp",EDGE,"E6"),sQuery(id+"F0.wireOp",EDGE,"E7"),sQuery(id+"F0.wireOp",EDGE,"E9.rect.left"),sQuery(id+"F0.wireOp",EDGE,"E9.rect.right"),subQ2,sQuery(id+"F0.wireOp",EDGE,"E10.rect.top"),sQuery(id+"F0.wireOp",EDGE,"E11.rect.bottom"),sQuery(id+"F0.wireOp",EDGE,"E11.rect.top"),subQ1,sQuery(id+"F0.wireOp",EDGE,"E12.rect.right"),sQuery(id+"F0.wireOp",EDGE,"E13.rect.left"),sQuery(id+"F0.wireOp",EDGE,"E13.rect.right"),sQuery(id+"F0.wireOp",EDGE,"E14.left"),sQuery(id+"F0.wireOp",EDGE,"E14.right"),sQuery(id+"F0.wireOp",EDGE,"E15"),sQuery(id+"F0.wireOp",EDGE,"E17"),sQuery(id+"F0.wireOp",EDGE,"E18"),sQuery(id+"F0.wireOp",EDGE,"E20"),sQuery(id+"F0.wireOp",EDGE,"E21.rect.bottom"),sQuery(id+"F0.wireOp",EDGE,"E21.rect.top"),sQuery(id+"F0.wireOp",EDGE,"E22.left"),sQuery(id+"F0.wireOp",EDGE,"E22.right"),sQuery(id+"F0.wireOp",EDGE,"E23.top"),sQuery(id+"F0.wireOp",EDGE,"E23.left"),sQuery(id+"F0.wireOp",EDGE,"E23.right"),sQuery(id+"F0.wireOp",EDGE,"E22.top"),sQuery(id+"F0.wireOp",EDGE,"E26"),sQuery(id+"F0.wireOp",EDGE,"E29"),sQuery(id+"F0.wireOp",EDGE,"E32"),sQuery(id+"F0.wireOp",EDGE,"E35"),sQuery(id+"F0.wireOp",EDGE,"E36"),sQuery(id+"F0.wireOp",EDGE,"E41"),subQ0,sQuery(id+"F0.wireOp",EDGE,"E47"),sQuery(id+"F0.wireOp",EDGE,"E48"),sQuery(id+"F0.wireOp",EDGE,"E49"),sQuery(id+"F0.wireOp",EDGE,"E50"),sQuery(id+"F0.wireOp",EDGE,"E51")])],"isStart":false})]});}
            var Q32;
            {var subQ0=sQuery(id+"F0.wireOp",EDGE,"E10.rect.bottom");Q32=makeQuery(id+"F1.opExtrude","CAP_EDGE",EDGE,{"disambiguationData":[OSD([subQ0]),TDD([makeQuery(id+"F0.imprint","IMPRINT",EDGE,{"disambiguationData":[TD([[makeQuery(id+"F0.imprint","INTERSECT",VERTEX,{"derivedFrom":[subQ0,sQuery(id+"F0.wireOp",EDGE,"E12.rect.left"),sQuery(id+"F0.wireOp",EDGE,"E44")]}),-1.0]])],"derivedFrom":subQ0})])],"isStart":false});}
            var Q33;
            {var subQ0=sQuery(id+"F0.wireOp",EDGE,"E44");var subQ1=sQuery(id+"F0.wireOp",EDGE,"E9.rect.left");Q33=makeQuery(id+"F3.opFillet","BLEND_EDGE",EDGE,{"blendedFrom":[makeQuery(id+"F1.opExtrude","SWEPT_EDGE",EDGE,{"disambiguationData":[OSD([subQ1,subQ0])]}),makeQuery(id+"F1.opExtrude","CAP_FACE",FACE,{"disambiguationData":[OSD([sQuery(id+"F0.wireOp",EDGE,"E0"),sQuery(id+"F0.wireOp",EDGE,"E1"),sQuery(id+"F0.wireOp",EDGE,"E2"),sQuery(id+"F0.wireOp",EDGE,"E3"),sQuery(id+"F0.wireOp",EDGE,"E4"),sQuery(id+"F0.wireOp",EDGE,"E5"),sQuery(id+"F0.wireOp",EDGE,"E6"),sQuery(id+"F0.wireOp",EDGE,"E7"),subQ1,sQuery(id+"F0.wireOp",EDGE,"E9.rect.right"),sQuery(id+"F0.wireOp",EDGE,"E10.rect.bottom"),sQuery(id+"F0.wireOp",EDGE,"E10.rect.top"),sQuery(id+"F0.wireOp",EDGE,"E11.rect.bottom"),sQuery(id+"F0.wireOp",EDGE,"E11.rect.top"),sQuery(id+"F0.wireOp",EDGE,"E12.rect.left"),sQuery(id+"F0.wireOp",EDGE,"E12.rect.right"),sQuery(id+"F0.wireOp",EDGE,"E13.rect.left"),sQuery(id+"F0.wireOp",EDGE,"E13.rect.right"),sQuery(id+"F0.wireOp",EDGE,"E14.left"),sQuery(id+"F0.wireOp",EDGE,"E14.right"),sQuery(id+"F0.wireOp",EDGE,"E15"),sQuery(id+"F0.wireOp",EDGE,"E17"),sQuery(id+"F0.wireOp",EDGE,"E18"),sQuery(id+"F0.wireOp",EDGE,"E20"),sQuery(id+"F0.wireOp",EDGE,"E21.rect.bottom"),sQuery(id+"F0.wireOp",EDGE,"E21.rect.top"),sQuery(id+"F0.wireOp",EDGE,"E22.left"),sQuery(id+"F0.wireOp",EDGE,"E22.right"),sQuery(id+"F0.wireOp",EDGE,"E23.top"),sQuery(id+"F0.wireOp",EDGE,"E23.left"),sQuery(id+"F0.wireOp",EDGE,"E23.right"),sQuery(id+"F0.wireOp",EDGE,"E22.top"),sQuery(id+"F0.wireOp",EDGE,"E26"),sQuery(id+"F0.wireOp",EDGE,"E29"),sQuery(id+"F0.wireOp",EDGE,"E32"),sQuery(id+"F0.wireOp",EDGE,"E35"),sQuery(id+"F0.wireOp",EDGE,"E36"),sQuery(id+"F0.wireOp",EDGE,"E41"),subQ0,sQuery(id+"F0.wireOp",EDGE,"E47"),sQuery(id+"F0.wireOp",EDGE,"E48"),sQuery(id+"F0.wireOp",EDGE,"E49"),sQuery(id+"F0.wireOp",EDGE,"E50"),sQuery(id+"F0.wireOp",EDGE,"E51")])],"isStart":false})],"blendedInto":[makeQuery(id+"F1.opExtrude","CAP_FACE",FACE,{"disambiguationData":[OSD([sQuery(id+"F0.wireOp",EDGE,"E0"),sQuery(id+"F0.wireOp",EDGE,"E1"),sQuery(id+"F0.wireOp",EDGE,"E2"),sQuery(id+"F0.wireOp",EDGE,"E3"),sQuery(id+"F0.wireOp",EDGE,"E4"),sQuery(id+"F0.wireOp",EDGE,"E5"),sQuery(id+"F0.wireOp",EDGE,"E6"),sQuery(id+"F0.wireOp",EDGE,"E7"),subQ1,sQuery(id+"F0.wireOp",EDGE,"E9.rect.right"),sQuery(id+"F0.wireOp",EDGE,"E10.rect.bottom"),sQuery(id+"F0.wireOp",EDGE,"E10.rect.top"),sQuery(id+"F0.wireOp",EDGE,"E11.rect.bottom"),sQuery(id+"F0.wireOp",EDGE,"E11.rect.top"),sQuery(id+"F0.wireOp",EDGE,"E12.rect.left"),sQuery(id+"F0.wireOp",EDGE,"E12.rect.right"),sQuery(id+"F0.wireOp",EDGE,"E13.rect.left"),sQuery(id+"F0.wireOp",EDGE,"E13.rect.right"),sQuery(id+"F0.wireOp",EDGE,"E14.left"),sQuery(id+"F0.wireOp",EDGE,"E14.right"),sQuery(id+"F0.wireOp",EDGE,"E15"),sQuery(id+"F0.wireOp",EDGE,"E17"),sQuery(id+"F0.wireOp",EDGE,"E18"),sQuery(id+"F0.wireOp",EDGE,"E20"),sQuery(id+"F0.wireOp",EDGE,"E21.rect.bottom"),sQuery(id+"F0.wireOp",EDGE,"E21.rect.top"),sQuery(id+"F0.wireOp",EDGE,"E22.left"),sQuery(id+"F0.wireOp",EDGE,"E22.right"),sQuery(id+"F0.wireOp",EDGE,"E23.top"),sQuery(id+"F0.wireOp",EDGE,"E23.left"),sQuery(id+"F0.wireOp",EDGE,"E23.right"),sQuery(id+"F0.wireOp",EDGE,"E22.top"),sQuery(id+"F0.wireOp",EDGE,"E26"),sQuery(id+"F0.wireOp",EDGE,"E29"),sQuery(id+"F0.wireOp",EDGE,"E32"),sQuery(id+"F0.wireOp",EDGE,"E35"),sQuery(id+"F0.wireOp",EDGE,"E36"),sQuery(id+"F0.wireOp",EDGE,"E41"),subQ0,sQuery(id+"F0.wireOp",EDGE,"E47"),sQuery(id+"F0.wireOp",EDGE,"E48"),sQuery(id+"F0.wireOp",EDGE,"E49"),sQuery(id+"F0.wireOp",EDGE,"E50"),sQuery(id+"F0.wireOp",EDGE,"E51")])],"isStart":false})]});}
            var Q34;
            {var subQ0=sQuery(id+"F0.wireOp",EDGE,"E20");var subQ1=sQuery(id+"F0.wireOp",EDGE,"E10.rect.bottom");Q34=makeQuery(id+"F4.opFillet","BLEND_EDGE",EDGE,{"blendedFrom":[makeQuery(id+"F1.opExtrude","SWEPT_EDGE",EDGE,{"disambiguationData":[OSD([subQ1,sQuery(id+"F0.wireOp",EDGE,"E19"),subQ0])]}),makeQuery(id+"F1.opExtrude","CAP_FACE",FACE,{"disambiguationData":[OSD([sQuery(id+"F0.wireOp",EDGE,"E0"),sQuery(id+"F0.wireOp",EDGE,"E1"),sQuery(id+"F0.wireOp",EDGE,"E2"),sQuery(id+"F0.wireOp",EDGE,"E3"),sQuery(id+"F0.wireOp",EDGE,"E4"),sQuery(id+"F0.wireOp",EDGE,"E5"),sQuery(id+"F0.wireOp",EDGE,"E6"),sQuery(id+"F0.wireOp",EDGE,"E7"),sQuery(id+"F0.wireOp",EDGE,"E9.rect.left"),sQuery(id+"F0.wireOp",EDGE,"E9.rect.right"),subQ1,sQuery(id+"F0.wireOp",EDGE,"E10.rect.top"),sQuery(id+"F0.wireOp",EDGE,"E11.rect.bottom"),sQuery(id+"F0.wireOp",EDGE,"E11.rect.top"),sQuery(id+"F0.wireOp",EDGE,"E12.rect.left"),sQuery(id+"F0.wireOp",EDGE,"E12.rect.right"),sQuery(id+"F0.wireOp",EDGE,"E13.rect.left"),sQuery(id+"F0.wireOp",EDGE,"E13.rect.right"),sQuery(id+"F0.wireOp",EDGE,"E14.left"),sQuery(id+"F0.wireOp",EDGE,"E14.right"),sQuery(id+"F0.wireOp",EDGE,"E15"),sQuery(id+"F0.wireOp",EDGE,"E17"),sQuery(id+"F0.wireOp",EDGE,"E18"),subQ0,sQuery(id+"F0.wireOp",EDGE,"E21.rect.bottom"),sQuery(id+"F0.wireOp",EDGE,"E21.rect.top"),sQuery(id+"F0.wireOp",EDGE,"E22.left"),sQuery(id+"F0.wireOp",EDGE,"E22.right"),sQuery(id+"F0.wireOp",EDGE,"E23.top"),sQuery(id+"F0.wireOp",EDGE,"E23.left"),sQuery(id+"F0.wireOp",EDGE,"E23.right"),sQuery(id+"F0.wireOp",EDGE,"E22.top"),sQuery(id+"F0.wireOp",EDGE,"E26"),sQuery(id+"F0.wireOp",EDGE,"E29"),sQuery(id+"F0.wireOp",EDGE,"E32"),sQuery(id+"F0.wireOp",EDGE,"E35"),sQuery(id+"F0.wireOp",EDGE,"E36"),sQuery(id+"F0.wireOp",EDGE,"E41"),sQuery(id+"F0.wireOp",EDGE,"E44"),sQuery(id+"F0.wireOp",EDGE,"E47"),sQuery(id+"F0.wireOp",EDGE,"E48"),sQuery(id+"F0.wireOp",EDGE,"E49"),sQuery(id+"F0.wireOp",EDGE,"E50"),sQuery(id+"F0.wireOp",EDGE,"E51")])],"isStart":false})],"blendedInto":[makeQuery(id+"F1.opExtrude","CAP_FACE",FACE,{"disambiguationData":[OSD([sQuery(id+"F0.wireOp",EDGE,"E0"),sQuery(id+"F0.wireOp",EDGE,"E1"),sQuery(id+"F0.wireOp",EDGE,"E2"),sQuery(id+"F0.wireOp",EDGE,"E3"),sQuery(id+"F0.wireOp",EDGE,"E4"),sQuery(id+"F0.wireOp",EDGE,"E5"),sQuery(id+"F0.wireOp",EDGE,"E6"),sQuery(id+"F0.wireOp",EDGE,"E7"),sQuery(id+"F0.wireOp",EDGE,"E9.rect.left"),sQuery(id+"F0.wireOp",EDGE,"E9.rect.right"),subQ1,sQuery(id+"F0.wireOp",EDGE,"E10.rect.top"),sQuery(id+"F0.wireOp",EDGE,"E11.rect.bottom"),sQuery(id+"F0.wireOp",EDGE,"E11.rect.top"),sQuery(id+"F0.wireOp",EDGE,"E12.rect.left"),sQuery(id+"F0.wireOp",EDGE,"E12.rect.right"),sQuery(id+"F0.wireOp",EDGE,"E13.rect.left"),sQuery(id+"F0.wireOp",EDGE,"E13.rect.right"),sQuery(id+"F0.wireOp",EDGE,"E14.left"),sQuery(id+"F0.wireOp",EDGE,"E14.right"),sQuery(id+"F0.wireOp",EDGE,"E15"),sQuery(id+"F0.wireOp",EDGE,"E17"),sQuery(id+"F0.wireOp",EDGE,"E18"),subQ0,sQuery(id+"F0.wireOp",EDGE,"E21.rect.bottom"),sQuery(id+"F0.wireOp",EDGE,"E21.rect.top"),sQuery(id+"F0.wireOp",EDGE,"E22.left"),sQuery(id+"F0.wireOp",EDGE,"E22.right"),sQuery(id+"F0.wireOp",EDGE,"E23.top"),sQuery(id+"F0.wireOp",EDGE,"E23.left"),sQuery(id+"F0.wireOp",EDGE,"E23.right"),sQuery(id+"F0.wireOp",EDGE,"E22.top"),sQuery(id+"F0.wireOp",EDGE,"E26"),sQuery(id+"F0.wireOp",EDGE,"E29"),sQuery(id+"F0.wireOp",EDGE,"E32"),sQuery(id+"F0.wireOp",EDGE,"E35"),sQuery(id+"F0.wireOp",EDGE,"E36"),sQuery(id+"F0.wireOp",EDGE,"E41"),sQuery(id+"F0.wireOp",EDGE,"E44"),sQuery(id+"F0.wireOp",EDGE,"E47"),sQuery(id+"F0.wireOp",EDGE,"E48"),sQuery(id+"F0.wireOp",EDGE,"E49"),sQuery(id+"F0.wireOp",EDGE,"E50"),sQuery(id+"F0.wireOp",EDGE,"E51")])],"isStart":false})]});}
            var Q35;
            Q35=makeQuery(id+"F1.opExtrude","CAP_EDGE",EDGE,{"disambiguationData":[OSD([sQuery(id+"F0.wireOp",EDGE,"E13.rect.left"),sQuery(id+"F0.wireOp",EDGE,"E20"),sQuery(id+"F0.wireOp",EDGE,"E23.right")])],"isStart":false});
            var Q36;
            Q36=makeQuery(id+"F1.opExtrude","CAP_EDGE",EDGE,{"disambiguationData":[OSD([sQuery(id+"F0.wireOp",EDGE,"E14.right"),sQuery(id+"F0.wireOp",EDGE,"E18"),sQuery(id+"F0.wireOp",EDGE,"E23.left")])],"isStart":false});
            var Q37;
            {var subQ0=sQuery(id+"F0.wireOp",EDGE,"E18");var subQ1=sQuery(id+"F0.wireOp",EDGE,"E10.rect.bottom");Q37=makeQuery(id+"F4.opFillet","BLEND_EDGE",EDGE,{"blendedFrom":[makeQuery(id+"F1.opExtrude","SWEPT_EDGE",EDGE,{"disambiguationData":[OSD([subQ1,subQ0,sQuery(id+"F0.wireOp",EDGE,"E19")])]}),makeQuery(id+"F1.opExtrude","CAP_FACE",FACE,{"disambiguationData":[OSD([sQuery(id+"F0.wireOp",EDGE,"E0"),sQuery(id+"F0.wireOp",EDGE,"E1"),sQuery(id+"F0.wireOp",EDGE,"E2"),sQuery(id+"F0.wireOp",EDGE,"E3"),sQuery(id+"F0.wireOp",EDGE,"E4"),sQuery(id+"F0.wireOp",EDGE,"E5"),sQuery(id+"F0.wireOp",EDGE,"E6"),sQuery(id+"F0.wireOp",EDGE,"E7"),sQuery(id+"F0.wireOp",EDGE,"E9.rect.left"),sQuery(id+"F0.wireOp",EDGE,"E9.rect.right"),subQ1,sQuery(id+"F0.wireOp",EDGE,"E10.rect.top"),sQuery(id+"F0.wireOp",EDGE,"E11.rect.bottom"),sQuery(id+"F0.wireOp",EDGE,"E11.rect.top"),sQuery(id+"F0.wireOp",EDGE,"E12.rect.left"),sQuery(id+"F0.wireOp",EDGE,"E12.rect.right"),sQuery(id+"F0.wireOp",EDGE,"E13.rect.left"),sQuery(id+"F0.wireOp",EDGE,"E13.rect.right"),sQuery(id+"F0.wireOp",EDGE,"E14.left"),sQuery(id+"F0.wireOp",EDGE,"E14.right"),sQuery(id+"F0.wireOp",EDGE,"E15"),sQuery(id+"F0.wireOp",EDGE,"E17"),subQ0,sQuery(id+"F0.wireOp",EDGE,"E20"),sQuery(id+"F0.wireOp",EDGE,"E21.rect.bottom"),sQuery(id+"F0.wireOp",EDGE,"E21.rect.top"),sQuery(id+"F0.wireOp",EDGE,"E22.left"),sQuery(id+"F0.wireOp",EDGE,"E22.right"),sQuery(id+"F0.wireOp",EDGE,"E23.top"),sQuery(id+"F0.wireOp",EDGE,"E23.left"),sQuery(id+"F0.wireOp",EDGE,"E23.right"),sQuery(id+"F0.wireOp",EDGE,"E22.top"),sQuery(id+"F0.wireOp",EDGE,"E26"),sQuery(id+"F0.wireOp",EDGE,"E29"),sQuery(id+"F0.wireOp",EDGE,"E32"),sQuery(id+"F0.wireOp",EDGE,"E35"),sQuery(id+"F0.wireOp",EDGE,"E36"),sQuery(id+"F0.wireOp",EDGE,"E41"),sQuery(id+"F0.wireOp",EDGE,"E44"),sQuery(id+"F0.wireOp",EDGE,"E47"),sQuery(id+"F0.wireOp",EDGE,"E48"),sQuery(id+"F0.wireOp",EDGE,"E49"),sQuery(id+"F0.wireOp",EDGE,"E50"),sQuery(id+"F0.wireOp",EDGE,"E51")])],"isStart":false})],"blendedInto":[makeQuery(id+"F1.opExtrude","CAP_FACE",FACE,{"disambiguationData":[OSD([sQuery(id+"F0.wireOp",EDGE,"E0"),sQuery(id+"F0.wireOp",EDGE,"E1"),sQuery(id+"F0.wireOp",EDGE,"E2"),sQuery(id+"F0.wireOp",EDGE,"E3"),sQuery(id+"F0.wireOp",EDGE,"E4"),sQuery(id+"F0.wireOp",EDGE,"E5"),sQuery(id+"F0.wireOp",EDGE,"E6"),sQuery(id+"F0.wireOp",EDGE,"E7"),sQuery(id+"F0.wireOp",EDGE,"E9.rect.left"),sQuery(id+"F0.wireOp",EDGE,"E9.rect.right"),subQ1,sQuery(id+"F0.wireOp",EDGE,"E10.rect.top"),sQuery(id+"F0.wireOp",EDGE,"E11.rect.bottom"),sQuery(id+"F0.wireOp",EDGE,"E11.rect.top"),sQuery(id+"F0.wireOp",EDGE,"E12.rect.left"),sQuery(id+"F0.wireOp",EDGE,"E12.rect.right"),sQuery(id+"F0.wireOp",EDGE,"E13.rect.left"),sQuery(id+"F0.wireOp",EDGE,"E13.rect.right"),sQuery(id+"F0.wireOp",EDGE,"E14.left"),sQuery(id+"F0.wireOp",EDGE,"E14.right"),sQuery(id+"F0.wireOp",EDGE,"E15"),sQuery(id+"F0.wireOp",EDGE,"E17"),subQ0,sQuery(id+"F0.wireOp",EDGE,"E20"),sQuery(id+"F0.wireOp",EDGE,"E21.rect.bottom"),sQuery(id+"F0.wireOp",EDGE,"E21.rect.top"),sQuery(id+"F0.wireOp",EDGE,"E22.left"),sQuery(id+"F0.wireOp",EDGE,"E22.right"),sQuery(id+"F0.wireOp",EDGE,"E23.top"),sQuery(id+"F0.wireOp",EDGE,"E23.left"),sQuery(id+"F0.wireOp",EDGE,"E23.right"),sQuery(id+"F0.wireOp",EDGE,"E22.top"),sQuery(id+"F0.wireOp",EDGE,"E26"),sQuery(id+"F0.wireOp",EDGE,"E29"),sQuery(id+"F0.wireOp",EDGE,"E32"),sQuery(id+"F0.wireOp",EDGE,"E35"),sQuery(id+"F0.wireOp",EDGE,"E36"),sQuery(id+"F0.wireOp",EDGE,"E41"),sQuery(id+"F0.wireOp",EDGE,"E44"),sQuery(id+"F0.wireOp",EDGE,"E47"),sQuery(id+"F0.wireOp",EDGE,"E48"),sQuery(id+"F0.wireOp",EDGE,"E49"),sQuery(id+"F0.wireOp",EDGE,"E50"),sQuery(id+"F0.wireOp",EDGE,"E51")])],"isStart":false})]});}
            var Q38;
            {var subQ0=sQuery(id+"F0.wireOp",EDGE,"E10.rect.bottom");Q38=makeQuery(id+"F1.opExtrude","CAP_EDGE",EDGE,{"disambiguationData":[OSD([subQ0]),TDD([makeQuery(id+"F0.imprint","IMPRINT",EDGE,{"disambiguationData":[TD([[makeQuery(id+"F0.imprint","INTERSECT",VERTEX,{"derivedFrom":[subQ0,sQuery(id+"F0.wireOp",EDGE,"E16"),sQuery(id+"F0.wireOp",EDGE,"E17")]}),1.0]])],"derivedFrom":subQ0})])],"isStart":false});}
            var Q39;
            Q39=makeQuery(id+"F1.opExtrude","CAP_EDGE",EDGE,{"disambiguationData":[OSD([sQuery(id+"F0.wireOp",EDGE,"E23.top")])],"isStart":false});
            var Q40;
            Q40=makeQuery(id+"F1.opExtrude","SWEPT_EDGE",EDGE,{"disambiguationData":[OSD([sQuery(id+"F0.wireOp",EDGE,"E23.top"),sQuery(id+"F0.wireOp",EDGE,"E23.left")])]});
            var Q41;
            Q41=makeQuery(id+"F1.opExtrude","SWEPT_EDGE",EDGE,{"disambiguationData":[OSD([sQuery(id+"F0.wireOp",EDGE,"E23.top"),sQuery(id+"F0.wireOp",EDGE,"E23.right")])]});
            var Q42;
            Q42=makeQuery(id+"F1.opExtrude","CAP_EDGE",EDGE,{"disambiguationData":[OSD([sQuery(id+"F0.wireOp",EDGE,"E23.top")])],"isStart":true});
            var Q43;
            {var subQ0=sQuery(id+"F0.wireOp",EDGE,"E17");var subQ1=sQuery(id+"F0.wireOp",EDGE,"E10.rect.bottom");Q43=makeQuery(id+"F4.opFillet","BLEND_EDGE",EDGE,{"blendedFrom":[makeQuery(id+"F1.opExtrude","SWEPT_EDGE",EDGE,{"disambiguationData":[OSD([subQ1,sQuery(id+"F0.wireOp",EDGE,"E16"),subQ0])]}),makeQuery(id+"F1.opExtrude","CAP_FACE",FACE,{"disambiguationData":[OSD([sQuery(id+"F0.wireOp",EDGE,"E0"),sQuery(id+"F0.wireOp",EDGE,"E1"),sQuery(id+"F0.wireOp",EDGE,"E2"),sQuery(id+"F0.wireOp",EDGE,"E3"),sQuery(id+"F0.wireOp",EDGE,"E4"),sQuery(id+"F0.wireOp",EDGE,"E5"),sQuery(id+"F0.wireOp",EDGE,"E6"),sQuery(id+"F0.wireOp",EDGE,"E7"),sQuery(id+"F0.wireOp",EDGE,"E9.rect.left"),sQuery(id+"F0.wireOp",EDGE,"E9.rect.right"),subQ1,sQuery(id+"F0.wireOp",EDGE,"E10.rect.top"),sQuery(id+"F0.wireOp",EDGE,"E11.rect.bottom"),sQuery(id+"F0.wireOp",EDGE,"E11.rect.top"),sQuery(id+"F0.wireOp",EDGE,"E12.rect.left"),sQuery(id+"F0.wireOp",EDGE,"E12.rect.right"),sQuery(id+"F0.wireOp",EDGE,"E13.rect.left"),sQuery(id+"F0.wireOp",EDGE,"E13.rect.right"),sQuery(id+"F0.wireOp",EDGE,"E14.left"),sQuery(id+"F0.wireOp",EDGE,"E14.right"),sQuery(id+"F0.wireOp",EDGE,"E15"),subQ0,sQuery(id+"F0.wireOp",EDGE,"E18"),sQuery(id+"F0.wireOp",EDGE,"E20"),sQuery(id+"F0.wireOp",EDGE,"E21.rect.bottom"),sQuery(id+"F0.wireOp",EDGE,"E21.rect.top"),sQuery(id+"F0.wireOp",EDGE,"E22.left"),sQuery(id+"F0.wireOp",EDGE,"E22.right"),sQuery(id+"F0.wireOp",EDGE,"E23.top"),sQuery(id+"F0.wireOp",EDGE,"E23.left"),sQuery(id+"F0.wireOp",EDGE,"E23.right"),sQuery(id+"F0.wireOp",EDGE,"E22.top"),sQuery(id+"F0.wireOp",EDGE,"E26"),sQuery(id+"F0.wireOp",EDGE,"E29"),sQuery(id+"F0.wireOp",EDGE,"E32"),sQuery(id+"F0.wireOp",EDGE,"E35"),sQuery(id+"F0.wireOp",EDGE,"E36"),sQuery(id+"F0.wireOp",EDGE,"E41"),sQuery(id+"F0.wireOp",EDGE,"E44"),sQuery(id+"F0.wireOp",EDGE,"E47"),sQuery(id+"F0.wireOp",EDGE,"E48"),sQuery(id+"F0.wireOp",EDGE,"E49"),sQuery(id+"F0.wireOp",EDGE,"E50"),sQuery(id+"F0.wireOp",EDGE,"E51")])],"isStart":false})],"blendedInto":[makeQuery(id+"F1.opExtrude","CAP_FACE",FACE,{"disambiguationData":[OSD([sQuery(id+"F0.wireOp",EDGE,"E0"),sQuery(id+"F0.wireOp",EDGE,"E1"),sQuery(id+"F0.wireOp",EDGE,"E2"),sQuery(id+"F0.wireOp",EDGE,"E3"),sQuery(id+"F0.wireOp",EDGE,"E4"),sQuery(id+"F0.wireOp",EDGE,"E5"),sQuery(id+"F0.wireOp",EDGE,"E6"),sQuery(id+"F0.wireOp",EDGE,"E7"),sQuery(id+"F0.wireOp",EDGE,"E9.rect.left"),sQuery(id+"F0.wireOp",EDGE,"E9.rect.right"),subQ1,sQuery(id+"F0.wireOp",EDGE,"E10.rect.top"),sQuery(id+"F0.wireOp",EDGE,"E11.rect.bottom"),sQuery(id+"F0.wireOp",EDGE,"E11.rect.top"),sQuery(id+"F0.wireOp",EDGE,"E12.rect.left"),sQuery(id+"F0.wireOp",EDGE,"E12.rect.right"),sQuery(id+"F0.wireOp",EDGE,"E13.rect.left"),sQuery(id+"F0.wireOp",EDGE,"E13.rect.right"),sQuery(id+"F0.wireOp",EDGE,"E14.left"),sQuery(id+"F0.wireOp",EDGE,"E14.right"),sQuery(id+"F0.wireOp",EDGE,"E15"),subQ0,sQuery(id+"F0.wireOp",EDGE,"E18"),sQuery(id+"F0.wireOp",EDGE,"E20"),sQuery(id+"F0.wireOp",EDGE,"E21.rect.bottom"),sQuery(id+"F0.wireOp",EDGE,"E21.rect.top"),sQuery(id+"F0.wireOp",EDGE,"E22.left"),sQuery(id+"F0.wireOp",EDGE,"E22.right"),sQuery(id+"F0.wireOp",EDGE,"E23.top"),sQuery(id+"F0.wireOp",EDGE,"E23.left"),sQuery(id+"F0.wireOp",EDGE,"E23.right"),sQuery(id+"F0.wireOp",EDGE,"E22.top"),sQuery(id+"F0.wireOp",EDGE,"E26"),sQuery(id+"F0.wireOp",EDGE,"E29"),sQuery(id+"F0.wireOp",EDGE,"E32"),sQuery(id+"F0.wireOp",EDGE,"E35"),sQuery(id+"F0.wireOp",EDGE,"E36"),sQuery(id+"F0.wireOp",EDGE,"E41"),sQuery(id+"F0.wireOp",EDGE,"E44"),sQuery(id+"F0.wireOp",EDGE,"E47"),sQuery(id+"F0.wireOp",EDGE,"E48"),sQuery(id+"F0.wireOp",EDGE,"E49"),sQuery(id+"F0.wireOp",EDGE,"E50"),sQuery(id+"F0.wireOp",EDGE,"E51")])],"isStart":false})]});}
            var Q44;
            Q44=makeQuery(id+"F1.opExtrude","CAP_EDGE",EDGE,{"disambiguationData":[OSD([sQuery(id+"F0.wireOp",EDGE,"E14.left"),sQuery(id+"F0.wireOp",EDGE,"E17"),sQuery(id+"F0.wireOp",EDGE,"E22.left")])],"isStart":false});
            var Q45;
            Q45=makeQuery(id+"F1.opExtrude","CAP_EDGE",EDGE,{"disambiguationData":[OSD([sQuery(id+"F0.wireOp",EDGE,"E22.top")])],"isStart":false});
            var Q46;
            Q46=makeQuery(id+"F1.opExtrude","SWEPT_EDGE",EDGE,{"disambiguationData":[OSD([sQuery(id+"F0.wireOp",EDGE,"E22.left"),sQuery(id+"F0.wireOp",EDGE,"E22.top")])]});
            var Q47;
            Q47=makeQuery(id+"F1.opExtrude","CAP_EDGE",EDGE,{"disambiguationData":[OSD([sQuery(id+"F0.wireOp",EDGE,"E22.top")])],"isStart":true});
            var Q48;
            Q48=makeQuery(id+"F1.opExtrude","SWEPT_EDGE",EDGE,{"disambiguationData":[OSD([sQuery(id+"F0.wireOp",EDGE,"E22.right"),sQuery(id+"F0.wireOp",EDGE,"E22.top")])]});
            var Q49;
            Q49=makeQuery(id+"F1.opExtrude","CAP_EDGE",EDGE,{"disambiguationData":[OSD([sQuery(id+"F0.wireOp",EDGE,"E13.rect.right"),sQuery(id+"F0.wireOp",EDGE,"E15"),sQuery(id+"F0.wireOp",EDGE,"E22.right")])],"isStart":false});
            var Q50;
            {var subQ0=sQuery(id+"F0.wireOp",EDGE,"E15");var subQ1=sQuery(id+"F0.wireOp",EDGE,"E10.rect.bottom");Q50=makeQuery(id+"F4.opFillet","BLEND_EDGE",EDGE,{"blendedFrom":[makeQuery(id+"F1.opExtrude","SWEPT_EDGE",EDGE,{"disambiguationData":[OSD([subQ1,subQ0,sQuery(id+"F0.wireOp",EDGE,"E16")])]}),makeQuery(id+"F1.opExtrude","CAP_FACE",FACE,{"disambiguationData":[OSD([sQuery(id+"F0.wireOp",EDGE,"E0"),sQuery(id+"F0.wireOp",EDGE,"E1"),sQuery(id+"F0.wireOp",EDGE,"E2"),sQuery(id+"F0.wireOp",EDGE,"E3"),sQuery(id+"F0.wireOp",EDGE,"E4"),sQuery(id+"F0.wireOp",EDGE,"E5"),sQuery(id+"F0.wireOp",EDGE,"E6"),sQuery(id+"F0.wireOp",EDGE,"E7"),sQuery(id+"F0.wireOp",EDGE,"E9.rect.left"),sQuery(id+"F0.wireOp",EDGE,"E9.rect.right"),subQ1,sQuery(id+"F0.wireOp",EDGE,"E10.rect.top"),sQuery(id+"F0.wireOp",EDGE,"E11.rect.bottom"),sQuery(id+"F0.wireOp",EDGE,"E11.rect.top"),sQuery(id+"F0.wireOp",EDGE,"E12.rect.left"),sQuery(id+"F0.wireOp",EDGE,"E12.rect.right"),sQuery(id+"F0.wireOp",EDGE,"E13.rect.left"),sQuery(id+"F0.wireOp",EDGE,"E13.rect.right"),sQuery(id+"F0.wireOp",EDGE,"E14.left"),sQuery(id+"F0.wireOp",EDGE,"E14.right"),subQ0,sQuery(id+"F0.wireOp",EDGE,"E17"),sQuery(id+"F0.wireOp",EDGE,"E18"),sQuery(id+"F0.wireOp",EDGE,"E20"),sQuery(id+"F0.wireOp",EDGE,"E21.rect.bottom"),sQuery(id+"F0.wireOp",EDGE,"E21.rect.top"),sQuery(id+"F0.wireOp",EDGE,"E22.left"),sQuery(id+"F0.wireOp",EDGE,"E22.right"),sQuery(id+"F0.wireOp",EDGE,"E23.top"),sQuery(id+"F0.wireOp",EDGE,"E23.left"),sQuery(id+"F0.wireOp",EDGE,"E23.right"),sQuery(id+"F0.wireOp",EDGE,"E22.top"),sQuery(id+"F0.wireOp",EDGE,"E26"),sQuery(id+"F0.wireOp",EDGE,"E29"),sQuery(id+"F0.wireOp",EDGE,"E32"),sQuery(id+"F0.wireOp",EDGE,"E35"),sQuery(id+"F0.wireOp",EDGE,"E36"),sQuery(id+"F0.wireOp",EDGE,"E41"),sQuery(id+"F0.wireOp",EDGE,"E44"),sQuery(id+"F0.wireOp",EDGE,"E47"),sQuery(id+"F0.wireOp",EDGE,"E48"),sQuery(id+"F0.wireOp",EDGE,"E49"),sQuery(id+"F0.wireOp",EDGE,"E50"),sQuery(id+"F0.wireOp",EDGE,"E51")])],"isStart":false})],"blendedInto":[makeQuery(id+"F1.opExtrude","CAP_FACE",FACE,{"disambiguationData":[OSD([sQuery(id+"F0.wireOp",EDGE,"E0"),sQuery(id+"F0.wireOp",EDGE,"E1"),sQuery(id+"F0.wireOp",EDGE,"E2"),sQuery(id+"F0.wireOp",EDGE,"E3"),sQuery(id+"F0.wireOp",EDGE,"E4"),sQuery(id+"F0.wireOp",EDGE,"E5"),sQuery(id+"F0.wireOp",EDGE,"E6"),sQuery(id+"F0.wireOp",EDGE,"E7"),sQuery(id+"F0.wireOp",EDGE,"E9.rect.left"),sQuery(id+"F0.wireOp",EDGE,"E9.rect.right"),subQ1,sQuery(id+"F0.wireOp",EDGE,"E10.rect.top"),sQuery(id+"F0.wireOp",EDGE,"E11.rect.bottom"),sQuery(id+"F0.wireOp",EDGE,"E11.rect.top"),sQuery(id+"F0.wireOp",EDGE,"E12.rect.left"),sQuery(id+"F0.wireOp",EDGE,"E12.rect.right"),sQuery(id+"F0.wireOp",EDGE,"E13.rect.left"),sQuery(id+"F0.wireOp",EDGE,"E13.rect.right"),sQuery(id+"F0.wireOp",EDGE,"E14.left"),sQuery(id+"F0.wireOp",EDGE,"E14.right"),subQ0,sQuery(id+"F0.wireOp",EDGE,"E17"),sQuery(id+"F0.wireOp",EDGE,"E18"),sQuery(id+"F0.wireOp",EDGE,"E20"),sQuery(id+"F0.wireOp",EDGE,"E21.rect.bottom"),sQuery(id+"F0.wireOp",EDGE,"E21.rect.top"),sQuery(id+"F0.wireOp",EDGE,"E22.left"),sQuery(id+"F0.wireOp",EDGE,"E22.right"),sQuery(id+"F0.wireOp",EDGE,"E23.top"),sQuery(id+"F0.wireOp",EDGE,"E23.left"),sQuery(id+"F0.wireOp",EDGE,"E23.right"),sQuery(id+"F0.wireOp",EDGE,"E22.top"),sQuery(id+"F0.wireOp",EDGE,"E26"),sQuery(id+"F0.wireOp",EDGE,"E29"),sQuery(id+"F0.wireOp",EDGE,"E32"),sQuery(id+"F0.wireOp",EDGE,"E35"),sQuery(id+"F0.wireOp",EDGE,"E36"),sQuery(id+"F0.wireOp",EDGE,"E41"),sQuery(id+"F0.wireOp",EDGE,"E44"),sQuery(id+"F0.wireOp",EDGE,"E47"),sQuery(id+"F0.wireOp",EDGE,"E48"),sQuery(id+"F0.wireOp",EDGE,"E49"),sQuery(id+"F0.wireOp",EDGE,"E50"),sQuery(id+"F0.wireOp",EDGE,"E51")])],"isStart":false})]});}
            var Q51;
            {var subQ0=sQuery(id+"F0.wireOp",EDGE,"E10.rect.bottom");Q51=makeQuery(id+"F1.opExtrude","CAP_EDGE",EDGE,{"disambiguationData":[OSD([subQ0]),TDD([makeQuery(id+"F0.imprint","IMPRINT",EDGE,{"disambiguationData":[TD([[makeQuery(id+"F0.imprint","INTERSECT",VERTEX,{"derivedFrom":[subQ0,sQuery(id+"F0.wireOp",EDGE,"E12.rect.right"),sQuery(id+"F0.wireOp",EDGE,"E47")]}),1.0]])],"derivedFrom":subQ0})])],"isStart":false});}
            var Q52;
            {var subQ0=sQuery(id+"F0.wireOp",EDGE,"E47");var subQ1=sQuery(id+"F0.wireOp",EDGE,"E12.rect.right");var subQ2=sQuery(id+"F0.wireOp",EDGE,"E10.rect.bottom");Q52=makeQuery(id+"F4.opFillet","BLEND_EDGE",EDGE,{"blendedFrom":[makeQuery(id+"F1.opExtrude","SWEPT_EDGE",EDGE,{"disambiguationData":[OSD([subQ2,subQ1,subQ0])]}),makeQuery(id+"F1.opExtrude","CAP_FACE",FACE,{"disambiguationData":[OSD([sQuery(id+"F0.wireOp",EDGE,"E0"),sQuery(id+"F0.wireOp",EDGE,"E1"),sQuery(id+"F0.wireOp",EDGE,"E2"),sQuery(id+"F0.wireOp",EDGE,"E3"),sQuery(id+"F0.wireOp",EDGE,"E4"),sQuery(id+"F0.wireOp",EDGE,"E5"),sQuery(id+"F0.wireOp",EDGE,"E6"),sQuery(id+"F0.wireOp",EDGE,"E7"),sQuery(id+"F0.wireOp",EDGE,"E9.rect.left"),sQuery(id+"F0.wireOp",EDGE,"E9.rect.right"),subQ2,sQuery(id+"F0.wireOp",EDGE,"E10.rect.top"),sQuery(id+"F0.wireOp",EDGE,"E11.rect.bottom"),sQuery(id+"F0.wireOp",EDGE,"E11.rect.top"),sQuery(id+"F0.wireOp",EDGE,"E12.rect.left"),subQ1,sQuery(id+"F0.wireOp",EDGE,"E13.rect.left"),sQuery(id+"F0.wireOp",EDGE,"E13.rect.right"),sQuery(id+"F0.wireOp",EDGE,"E14.left"),sQuery(id+"F0.wireOp",EDGE,"E14.right"),sQuery(id+"F0.wireOp",EDGE,"E15"),sQuery(id+"F0.wireOp",EDGE,"E17"),sQuery(id+"F0.wireOp",EDGE,"E18"),sQuery(id+"F0.wireOp",EDGE,"E20"),sQuery(id+"F0.wireOp",EDGE,"E21.rect.bottom"),sQuery(id+"F0.wireOp",EDGE,"E21.rect.top"),sQuery(id+"F0.wireOp",EDGE,"E22.left"),sQuery(id+"F0.wireOp",EDGE,"E22.right"),sQuery(id+"F0.wireOp",EDGE,"E23.top"),sQuery(id+"F0.wireOp",EDGE,"E23.left"),sQuery(id+"F0.wireOp",EDGE,"E23.right"),sQuery(id+"F0.wireOp",EDGE,"E22.top"),sQuery(id+"F0.wireOp",EDGE,"E26"),sQuery(id+"F0.wireOp",EDGE,"E29"),sQuery(id+"F0.wireOp",EDGE,"E32"),sQuery(id+"F0.wireOp",EDGE,"E35"),sQuery(id+"F0.wireOp",EDGE,"E36"),sQuery(id+"F0.wireOp",EDGE,"E41"),sQuery(id+"F0.wireOp",EDGE,"E44"),subQ0,sQuery(id+"F0.wireOp",EDGE,"E48"),sQuery(id+"F0.wireOp",EDGE,"E49"),sQuery(id+"F0.wireOp",EDGE,"E50"),sQuery(id+"F0.wireOp",EDGE,"E51")])],"isStart":false})],"blendedInto":[makeQuery(id+"F1.opExtrude","CAP_FACE",FACE,{"disambiguationData":[OSD([sQuery(id+"F0.wireOp",EDGE,"E0"),sQuery(id+"F0.wireOp",EDGE,"E1"),sQuery(id+"F0.wireOp",EDGE,"E2"),sQuery(id+"F0.wireOp",EDGE,"E3"),sQuery(id+"F0.wireOp",EDGE,"E4"),sQuery(id+"F0.wireOp",EDGE,"E5"),sQuery(id+"F0.wireOp",EDGE,"E6"),sQuery(id+"F0.wireOp",EDGE,"E7"),sQuery(id+"F0.wireOp",EDGE,"E9.rect.left"),sQuery(id+"F0.wireOp",EDGE,"E9.rect.right"),subQ2,sQuery(id+"F0.wireOp",EDGE,"E10.rect.top"),sQuery(id+"F0.wireOp",EDGE,"E11.rect.bottom"),sQuery(id+"F0.wireOp",EDGE,"E11.rect.top"),sQuery(id+"F0.wireOp",EDGE,"E12.rect.left"),subQ1,sQuery(id+"F0.wireOp",EDGE,"E13.rect.left"),sQuery(id+"F0.wireOp",EDGE,"E13.rect.right"),sQuery(id+"F0.wireOp",EDGE,"E14.left"),sQuery(id+"F0.wireOp",EDGE,"E14.right"),sQuery(id+"F0.wireOp",EDGE,"E15"),sQuery(id+"F0.wireOp",EDGE,"E17"),sQuery(id+"F0.wireOp",EDGE,"E18"),sQuery(id+"F0.wireOp",EDGE,"E20"),sQuery(id+"F0.wireOp",EDGE,"E21.rect.bottom"),sQuery(id+"F0.wireOp",EDGE,"E21.rect.top"),sQuery(id+"F0.wireOp",EDGE,"E22.left"),sQuery(id+"F0.wireOp",EDGE,"E22.right"),sQuery(id+"F0.wireOp",EDGE,"E23.top"),sQuery(id+"F0.wireOp",EDGE,"E23.left"),sQuery(id+"F0.wireOp",EDGE,"E23.right"),sQuery(id+"F0.wireOp",EDGE,"E22.top"),sQuery(id+"F0.wireOp",EDGE,"E26"),sQuery(id+"F0.wireOp",EDGE,"E29"),sQuery(id+"F0.wireOp",EDGE,"E32"),sQuery(id+"F0.wireOp",EDGE,"E35"),sQuery(id+"F0.wireOp",EDGE,"E36"),sQuery(id+"F0.wireOp",EDGE,"E41"),sQuery(id+"F0.wireOp",EDGE,"E44"),subQ0,sQuery(id+"F0.wireOp",EDGE,"E48"),sQuery(id+"F0.wireOp",EDGE,"E49"),sQuery(id+"F0.wireOp",EDGE,"E50"),sQuery(id+"F0.wireOp",EDGE,"E51")])],"isStart":false})]});}
            var Q53;
            Q53=makeQuery(id+"F1.opExtrude","CAP_EDGE",EDGE,{"disambiguationData":[OSD([sQuery(id+"F0.wireOp",EDGE,"E0")])],"isStart":false});
            var Q54;
            Q54=makeQuery(id+"F1.opExtrude","CAP_EDGE",EDGE,{"disambiguationData":[OSD([sQuery(id+"F0.wireOp",EDGE,"E47")])],"isStart":false});
            var Q55;
            {var subQ0=sQuery(id+"F0.wireOp",EDGE,"E26");var subQ1=sQuery(id+"F0.wireOp",EDGE,"E4");Q55=makeQuery(id+"F2.opFillet","BLEND_EDGE",EDGE,{"blendedFrom":[makeQuery(id+"F1.opExtrude","SWEPT_EDGE",EDGE,{"disambiguationData":[OSD([subQ1,subQ0])]}),makeQuery(id+"F1.opExtrude","CAP_FACE",FACE,{"disambiguationData":[OSD([sQuery(id+"F0.wireOp",EDGE,"E0"),sQuery(id+"F0.wireOp",EDGE,"E1"),sQuery(id+"F0.wireOp",EDGE,"E2"),sQuery(id+"F0.wireOp",EDGE,"E3"),subQ1,sQuery(id+"F0.wireOp",EDGE,"E5"),sQuery(id+"F0.wireOp",EDGE,"E6"),sQuery(id+"F0.wireOp",EDGE,"E7"),sQuery(id+"F0.wireOp",EDGE,"E9.rect.left"),sQuery(id+"F0.wireOp",EDGE,"E9.rect.right"),sQuery(id+"F0.wireOp",EDGE,"E10.rect.bottom"),sQuery(id+"F0.wireOp",EDGE,"E10.rect.top"),sQuery(id+"F0.wireOp",EDGE,"E11.rect.bottom"),sQuery(id+"F0.wireOp",EDGE,"E11.rect.top"),sQuery(id+"F0.wireOp",EDGE,"E12.rect.left"),sQuery(id+"F0.wireOp",EDGE,"E12.rect.right"),sQuery(id+"F0.wireOp",EDGE,"E13.rect.left"),sQuery(id+"F0.wireOp",EDGE,"E13.rect.right"),sQuery(id+"F0.wireOp",EDGE,"E14.left"),sQuery(id+"F0.wireOp",EDGE,"E14.right"),sQuery(id+"F0.wireOp",EDGE,"E15"),sQuery(id+"F0.wireOp",EDGE,"E17"),sQuery(id+"F0.wireOp",EDGE,"E18"),sQuery(id+"F0.wireOp",EDGE,"E20"),sQuery(id+"F0.wireOp",EDGE,"E21.rect.bottom"),sQuery(id+"F0.wireOp",EDGE,"E21.rect.top"),sQuery(id+"F0.wireOp",EDGE,"E22.left"),sQuery(id+"F0.wireOp",EDGE,"E22.right"),sQuery(id+"F0.wireOp",EDGE,"E23.top"),sQuery(id+"F0.wireOp",EDGE,"E23.left"),sQuery(id+"F0.wireOp",EDGE,"E23.right"),sQuery(id+"F0.wireOp",EDGE,"E22.top"),subQ0,sQuery(id+"F0.wireOp",EDGE,"E29"),sQuery(id+"F0.wireOp",EDGE,"E32"),sQuery(id+"F0.wireOp",EDGE,"E35"),sQuery(id+"F0.wireOp",EDGE,"E36"),sQuery(id+"F0.wireOp",EDGE,"E41"),sQuery(id+"F0.wireOp",EDGE,"E44"),sQuery(id+"F0.wireOp",EDGE,"E47"),sQuery(id+"F0.wireOp",EDGE,"E48"),sQuery(id+"F0.wireOp",EDGE,"E49"),sQuery(id+"F0.wireOp",EDGE,"E50"),sQuery(id+"F0.wireOp",EDGE,"E51")])],"isStart":false})],"blendedInto":[makeQuery(id+"F1.opExtrude","CAP_FACE",FACE,{"disambiguationData":[OSD([sQuery(id+"F0.wireOp",EDGE,"E0"),sQuery(id+"F0.wireOp",EDGE,"E1"),sQuery(id+"F0.wireOp",EDGE,"E2"),sQuery(id+"F0.wireOp",EDGE,"E3"),subQ1,sQuery(id+"F0.wireOp",EDGE,"E5"),sQuery(id+"F0.wireOp",EDGE,"E6"),sQuery(id+"F0.wireOp",EDGE,"E7"),sQuery(id+"F0.wireOp",EDGE,"E9.rect.left"),sQuery(id+"F0.wireOp",EDGE,"E9.rect.right"),sQuery(id+"F0.wireOp",EDGE,"E10.rect.bottom"),sQuery(id+"F0.wireOp",EDGE,"E10.rect.top"),sQuery(id+"F0.wireOp",EDGE,"E11.rect.bottom"),sQuery(id+"F0.wireOp",EDGE,"E11.rect.top"),sQuery(id+"F0.wireOp",EDGE,"E12.rect.left"),sQuery(id+"F0.wireOp",EDGE,"E12.rect.right"),sQuery(id+"F0.wireOp",EDGE,"E13.rect.left"),sQuery(id+"F0.wireOp",EDGE,"E13.rect.right"),sQuery(id+"F0.wireOp",EDGE,"E14.left"),sQuery(id+"F0.wireOp",EDGE,"E14.right"),sQuery(id+"F0.wireOp",EDGE,"E15"),sQuery(id+"F0.wireOp",EDGE,"E17"),sQuery(id+"F0.wireOp",EDGE,"E18"),sQuery(id+"F0.wireOp",EDGE,"E20"),sQuery(id+"F0.wireOp",EDGE,"E21.rect.bottom"),sQuery(id+"F0.wireOp",EDGE,"E21.rect.top"),sQuery(id+"F0.wireOp",EDGE,"E22.left"),sQuery(id+"F0.wireOp",EDGE,"E22.right"),sQuery(id+"F0.wireOp",EDGE,"E23.top"),sQuery(id+"F0.wireOp",EDGE,"E23.left"),sQuery(id+"F0.wireOp",EDGE,"E23.right"),sQuery(id+"F0.wireOp",EDGE,"E22.top"),subQ0,sQuery(id+"F0.wireOp",EDGE,"E29"),sQuery(id+"F0.wireOp",EDGE,"E32"),sQuery(id+"F0.wireOp",EDGE,"E35"),sQuery(id+"F0.wireOp",EDGE,"E36"),sQuery(id+"F0.wireOp",EDGE,"E41"),sQuery(id+"F0.wireOp",EDGE,"E44"),sQuery(id+"F0.wireOp",EDGE,"E47"),sQuery(id+"F0.wireOp",EDGE,"E48"),sQuery(id+"F0.wireOp",EDGE,"E49"),sQuery(id+"F0.wireOp",EDGE,"E50"),sQuery(id+"F0.wireOp",EDGE,"E51")])],"isStart":false})]});}
            var Q56;
            Q56=makeQuery(id+"F1.opExtrude","CAP_EDGE",EDGE,{"disambiguationData":[OSD([sQuery(id+"F0.wireOp",EDGE,"E12.rect.right")])],"isStart":false});
            var Q57;
            {var subQ0=sQuery(id+"F0.wireOp",EDGE,"E12.rect.right");var subQ1=sQuery(id+"F0.wireOp",EDGE,"E11.rect.bottom");Q57=makeQuery(id+"F4.opFillet","BLEND_EDGE",EDGE,{"blendedFrom":[makeQuery(id+"F1.opExtrude","SWEPT_EDGE",EDGE,{"disambiguationData":[OSD([subQ1,subQ0])]}),makeQuery(id+"F1.opExtrude","CAP_FACE",FACE,{"disambiguationData":[OSD([sQuery(id+"F0.wireOp",EDGE,"E0"),sQuery(id+"F0.wireOp",EDGE,"E1"),sQuery(id+"F0.wireOp",EDGE,"E2"),sQuery(id+"F0.wireOp",EDGE,"E3"),sQuery(id+"F0.wireOp",EDGE,"E4"),sQuery(id+"F0.wireOp",EDGE,"E5"),sQuery(id+"F0.wireOp",EDGE,"E6"),sQuery(id+"F0.wireOp",EDGE,"E7"),sQuery(id+"F0.wireOp",EDGE,"E9.rect.left"),sQuery(id+"F0.wireOp",EDGE,"E9.rect.right"),sQuery(id+"F0.wireOp",EDGE,"E10.rect.bottom"),sQuery(id+"F0.wireOp",EDGE,"E10.rect.top"),subQ1,sQuery(id+"F0.wireOp",EDGE,"E11.rect.top"),sQuery(id+"F0.wireOp",EDGE,"E12.rect.left"),subQ0,sQuery(id+"F0.wireOp",EDGE,"E13.rect.left"),sQuery(id+"F0.wireOp",EDGE,"E13.rect.right"),sQuery(id+"F0.wireOp",EDGE,"E14.left"),sQuery(id+"F0.wireOp",EDGE,"E14.right"),sQuery(id+"F0.wireOp",EDGE,"E15"),sQuery(id+"F0.wireOp",EDGE,"E17"),sQuery(id+"F0.wireOp",EDGE,"E18"),sQuery(id+"F0.wireOp",EDGE,"E20"),sQuery(id+"F0.wireOp",EDGE,"E21.rect.bottom"),sQuery(id+"F0.wireOp",EDGE,"E21.rect.top"),sQuery(id+"F0.wireOp",EDGE,"E22.left"),sQuery(id+"F0.wireOp",EDGE,"E22.right"),sQuery(id+"F0.wireOp",EDGE,"E23.top"),sQuery(id+"F0.wireOp",EDGE,"E23.left"),sQuery(id+"F0.wireOp",EDGE,"E23.right"),sQuery(id+"F0.wireOp",EDGE,"E22.top"),sQuery(id+"F0.wireOp",EDGE,"E26"),sQuery(id+"F0.wireOp",EDGE,"E29"),sQuery(id+"F0.wireOp",EDGE,"E32"),sQuery(id+"F0.wireOp",EDGE,"E35"),sQuery(id+"F0.wireOp",EDGE,"E36"),sQuery(id+"F0.wireOp",EDGE,"E41"),sQuery(id+"F0.wireOp",EDGE,"E44"),sQuery(id+"F0.wireOp",EDGE,"E47"),sQuery(id+"F0.wireOp",EDGE,"E48"),sQuery(id+"F0.wireOp",EDGE,"E49"),sQuery(id+"F0.wireOp",EDGE,"E50"),sQuery(id+"F0.wireOp",EDGE,"E51")])],"isStart":false})],"blendedInto":[makeQuery(id+"F1.opExtrude","CAP_FACE",FACE,{"disambiguationData":[OSD([sQuery(id+"F0.wireOp",EDGE,"E0"),sQuery(id+"F0.wireOp",EDGE,"E1"),sQuery(id+"F0.wireOp",EDGE,"E2"),sQuery(id+"F0.wireOp",EDGE,"E3"),sQuery(id+"F0.wireOp",EDGE,"E4"),sQuery(id+"F0.wireOp",EDGE,"E5"),sQuery(id+"F0.wireOp",EDGE,"E6"),sQuery(id+"F0.wireOp",EDGE,"E7"),sQuery(id+"F0.wireOp",EDGE,"E9.rect.left"),sQuery(id+"F0.wireOp",EDGE,"E9.rect.right"),sQuery(id+"F0.wireOp",EDGE,"E10.rect.bottom"),sQuery(id+"F0.wireOp",EDGE,"E10.rect.top"),subQ1,sQuery(id+"F0.wireOp",EDGE,"E11.rect.top"),sQuery(id+"F0.wireOp",EDGE,"E12.rect.left"),subQ0,sQuery(id+"F0.wireOp",EDGE,"E13.rect.left"),sQuery(id+"F0.wireOp",EDGE,"E13.rect.right"),sQuery(id+"F0.wireOp",EDGE,"E14.left"),sQuery(id+"F0.wireOp",EDGE,"E14.right"),sQuery(id+"F0.wireOp",EDGE,"E15"),sQuery(id+"F0.wireOp",EDGE,"E17"),sQuery(id+"F0.wireOp",EDGE,"E18"),sQuery(id+"F0.wireOp",EDGE,"E20"),sQuery(id+"F0.wireOp",EDGE,"E21.rect.bottom"),sQuery(id+"F0.wireOp",EDGE,"E21.rect.top"),sQuery(id+"F0.wireOp",EDGE,"E22.left"),sQuery(id+"F0.wireOp",EDGE,"E22.right"),sQuery(id+"F0.wireOp",EDGE,"E23.top"),sQuery(id+"F0.wireOp",EDGE,"E23.left"),sQuery(id+"F0.wireOp",EDGE,"E23.right"),sQuery(id+"F0.wireOp",EDGE,"E22.top"),sQuery(id+"F0.wireOp",EDGE,"E26"),sQuery(id+"F0.wireOp",EDGE,"E29"),sQuery(id+"F0.wireOp",EDGE,"E32"),sQuery(id+"F0.wireOp",EDGE,"E35"),sQuery(id+"F0.wireOp",EDGE,"E36"),sQuery(id+"F0.wireOp",EDGE,"E41"),sQuery(id+"F0.wireOp",EDGE,"E44"),sQuery(id+"F0.wireOp",EDGE,"E47"),sQuery(id+"F0.wireOp",EDGE,"E48"),sQuery(id+"F0.wireOp",EDGE,"E49"),sQuery(id+"F0.wireOp",EDGE,"E50"),sQuery(id+"F0.wireOp",EDGE,"E51")])],"isStart":false})]});}
            var Q58;
            {var subQ0=sQuery(id+"F0.wireOp",EDGE,"E12.rect.right");var subQ1=sQuery(id+"F0.wireOp",EDGE,"E11.rect.top");Q58=makeQuery(id+"F4.opFillet","BLEND_EDGE",EDGE,{"blendedFrom":[makeQuery(id+"F1.opExtrude","SWEPT_EDGE",EDGE,{"disambiguationData":[OSD([subQ1,subQ0])]}),makeQuery(id+"F1.opExtrude","CAP_FACE",FACE,{"disambiguationData":[OSD([sQuery(id+"F0.wireOp",EDGE,"E0"),sQuery(id+"F0.wireOp",EDGE,"E1"),sQuery(id+"F0.wireOp",EDGE,"E2"),sQuery(id+"F0.wireOp",EDGE,"E3"),sQuery(id+"F0.wireOp",EDGE,"E4"),sQuery(id+"F0.wireOp",EDGE,"E5"),sQuery(id+"F0.wireOp",EDGE,"E6"),sQuery(id+"F0.wireOp",EDGE,"E7"),sQuery(id+"F0.wireOp",EDGE,"E9.rect.left"),sQuery(id+"F0.wireOp",EDGE,"E9.rect.right"),sQuery(id+"F0.wireOp",EDGE,"E10.rect.bottom"),sQuery(id+"F0.wireOp",EDGE,"E10.rect.top"),sQuery(id+"F0.wireOp",EDGE,"E11.rect.bottom"),subQ1,sQuery(id+"F0.wireOp",EDGE,"E12.rect.left"),subQ0,sQuery(id+"F0.wireOp",EDGE,"E13.rect.left"),sQuery(id+"F0.wireOp",EDGE,"E13.rect.right"),sQuery(id+"F0.wireOp",EDGE,"E14.left"),sQuery(id+"F0.wireOp",EDGE,"E14.right"),sQuery(id+"F0.wireOp",EDGE,"E15"),sQuery(id+"F0.wireOp",EDGE,"E17"),sQuery(id+"F0.wireOp",EDGE,"E18"),sQuery(id+"F0.wireOp",EDGE,"E20"),sQuery(id+"F0.wireOp",EDGE,"E21.rect.bottom"),sQuery(id+"F0.wireOp",EDGE,"E21.rect.top"),sQuery(id+"F0.wireOp",EDGE,"E22.left"),sQuery(id+"F0.wireOp",EDGE,"E22.right"),sQuery(id+"F0.wireOp",EDGE,"E23.top"),sQuery(id+"F0.wireOp",EDGE,"E23.left"),sQuery(id+"F0.wireOp",EDGE,"E23.right"),sQuery(id+"F0.wireOp",EDGE,"E22.top"),sQuery(id+"F0.wireOp",EDGE,"E26"),sQuery(id+"F0.wireOp",EDGE,"E29"),sQuery(id+"F0.wireOp",EDGE,"E32"),sQuery(id+"F0.wireOp",EDGE,"E35"),sQuery(id+"F0.wireOp",EDGE,"E36"),sQuery(id+"F0.wireOp",EDGE,"E41"),sQuery(id+"F0.wireOp",EDGE,"E44"),sQuery(id+"F0.wireOp",EDGE,"E47"),sQuery(id+"F0.wireOp",EDGE,"E48"),sQuery(id+"F0.wireOp",EDGE,"E49"),sQuery(id+"F0.wireOp",EDGE,"E50"),sQuery(id+"F0.wireOp",EDGE,"E51")])],"isStart":false})],"blendedInto":[makeQuery(id+"F1.opExtrude","CAP_FACE",FACE,{"disambiguationData":[OSD([sQuery(id+"F0.wireOp",EDGE,"E0"),sQuery(id+"F0.wireOp",EDGE,"E1"),sQuery(id+"F0.wireOp",EDGE,"E2"),sQuery(id+"F0.wireOp",EDGE,"E3"),sQuery(id+"F0.wireOp",EDGE,"E4"),sQuery(id+"F0.wireOp",EDGE,"E5"),sQuery(id+"F0.wireOp",EDGE,"E6"),sQuery(id+"F0.wireOp",EDGE,"E7"),sQuery(id+"F0.wireOp",EDGE,"E9.rect.left"),sQuery(id+"F0.wireOp",EDGE,"E9.rect.right"),sQuery(id+"F0.wireOp",EDGE,"E10.rect.bottom"),sQuery(id+"F0.wireOp",EDGE,"E10.rect.top"),sQuery(id+"F0.wireOp",EDGE,"E11.rect.bottom"),subQ1,sQuery(id+"F0.wireOp",EDGE,"E12.rect.left"),subQ0,sQuery(id+"F0.wireOp",EDGE,"E13.rect.left"),sQuery(id+"F0.wireOp",EDGE,"E13.rect.right"),sQuery(id+"F0.wireOp",EDGE,"E14.left"),sQuery(id+"F0.wireOp",EDGE,"E14.right"),sQuery(id+"F0.wireOp",EDGE,"E15"),sQuery(id+"F0.wireOp",EDGE,"E17"),sQuery(id+"F0.wireOp",EDGE,"E18"),sQuery(id+"F0.wireOp",EDGE,"E20"),sQuery(id+"F0.wireOp",EDGE,"E21.rect.bottom"),sQuery(id+"F0.wireOp",EDGE,"E21.rect.top"),sQuery(id+"F0.wireOp",EDGE,"E22.left"),sQuery(id+"F0.wireOp",EDGE,"E22.right"),sQuery(id+"F0.wireOp",EDGE,"E23.top"),sQuery(id+"F0.wireOp",EDGE,"E23.left"),sQuery(id+"F0.wireOp",EDGE,"E23.right"),sQuery(id+"F0.wireOp",EDGE,"E22.top"),sQuery(id+"F0.wireOp",EDGE,"E26"),sQuery(id+"F0.wireOp",EDGE,"E29"),sQuery(id+"F0.wireOp",EDGE,"E32"),sQuery(id+"F0.wireOp",EDGE,"E35"),sQuery(id+"F0.wireOp",EDGE,"E36"),sQuery(id+"F0.wireOp",EDGE,"E41"),sQuery(id+"F0.wireOp",EDGE,"E44"),sQuery(id+"F0.wireOp",EDGE,"E47"),sQuery(id+"F0.wireOp",EDGE,"E48"),sQuery(id+"F0.wireOp",EDGE,"E49"),sQuery(id+"F0.wireOp",EDGE,"E50"),sQuery(id+"F0.wireOp",EDGE,"E51")])],"isStart":false})]});}
            var Q59;
            Q59=makeQuery(id+"F1.opExtrude","CAP_EDGE",EDGE,{"disambiguationData":[OSD([sQuery(id+"F0.wireOp",EDGE,"E11.rect.top"),sQuery(id+"F0.wireOp",EDGE,"E21.rect.top")])],"isStart":false});
            var Q60;
            Q60=makeQuery(id+"F1.opExtrude","CAP_EDGE",EDGE,{"disambiguationData":[OSD([sQuery(id+"F0.wireOp",EDGE,"E11.rect.bottom"),sQuery(id+"F0.wireOp",EDGE,"E21.rect.bottom")])],"isStart":false});
            var Q61;
            {var subQ0=sQuery(id+"F0.wireOp",EDGE,"E12.rect.left");var subQ1=sQuery(id+"F0.wireOp",EDGE,"E11.rect.bottom");Q61=makeQuery(id+"F4.opFillet","BLEND_EDGE",EDGE,{"blendedFrom":[makeQuery(id+"F1.opExtrude","SWEPT_EDGE",EDGE,{"disambiguationData":[OSD([subQ1,subQ0])]}),makeQuery(id+"F1.opExtrude","CAP_FACE",FACE,{"disambiguationData":[OSD([sQuery(id+"F0.wireOp",EDGE,"E0"),sQuery(id+"F0.wireOp",EDGE,"E1"),sQuery(id+"F0.wireOp",EDGE,"E2"),sQuery(id+"F0.wireOp",EDGE,"E3"),sQuery(id+"F0.wireOp",EDGE,"E4"),sQuery(id+"F0.wireOp",EDGE,"E5"),sQuery(id+"F0.wireOp",EDGE,"E6"),sQuery(id+"F0.wireOp",EDGE,"E7"),sQuery(id+"F0.wireOp",EDGE,"E9.rect.left"),sQuery(id+"F0.wireOp",EDGE,"E9.rect.right"),sQuery(id+"F0.wireOp",EDGE,"E10.rect.bottom"),sQuery(id+"F0.wireOp",EDGE,"E10.rect.top"),subQ1,sQuery(id+"F0.wireOp",EDGE,"E11.rect.top"),subQ0,sQuery(id+"F0.wireOp",EDGE,"E12.rect.right"),sQuery(id+"F0.wireOp",EDGE,"E13.rect.left"),sQuery(id+"F0.wireOp",EDGE,"E13.rect.right"),sQuery(id+"F0.wireOp",EDGE,"E14.left"),sQuery(id+"F0.wireOp",EDGE,"E14.right"),sQuery(id+"F0.wireOp",EDGE,"E15"),sQuery(id+"F0.wireOp",EDGE,"E17"),sQuery(id+"F0.wireOp",EDGE,"E18"),sQuery(id+"F0.wireOp",EDGE,"E20"),sQuery(id+"F0.wireOp",EDGE,"E21.rect.bottom"),sQuery(id+"F0.wireOp",EDGE,"E21.rect.top"),sQuery(id+"F0.wireOp",EDGE,"E22.left"),sQuery(id+"F0.wireOp",EDGE,"E22.right"),sQuery(id+"F0.wireOp",EDGE,"E23.top"),sQuery(id+"F0.wireOp",EDGE,"E23.left"),sQuery(id+"F0.wireOp",EDGE,"E23.right"),sQuery(id+"F0.wireOp",EDGE,"E22.top"),sQuery(id+"F0.wireOp",EDGE,"E26"),sQuery(id+"F0.wireOp",EDGE,"E29"),sQuery(id+"F0.wireOp",EDGE,"E32"),sQuery(id+"F0.wireOp",EDGE,"E35"),sQuery(id+"F0.wireOp",EDGE,"E36"),sQuery(id+"F0.wireOp",EDGE,"E41"),sQuery(id+"F0.wireOp",EDGE,"E44"),sQuery(id+"F0.wireOp",EDGE,"E47"),sQuery(id+"F0.wireOp",EDGE,"E48"),sQuery(id+"F0.wireOp",EDGE,"E49"),sQuery(id+"F0.wireOp",EDGE,"E50"),sQuery(id+"F0.wireOp",EDGE,"E51")])],"isStart":false})],"blendedInto":[makeQuery(id+"F1.opExtrude","CAP_FACE",FACE,{"disambiguationData":[OSD([sQuery(id+"F0.wireOp",EDGE,"E0"),sQuery(id+"F0.wireOp",EDGE,"E1"),sQuery(id+"F0.wireOp",EDGE,"E2"),sQuery(id+"F0.wireOp",EDGE,"E3"),sQuery(id+"F0.wireOp",EDGE,"E4"),sQuery(id+"F0.wireOp",EDGE,"E5"),sQuery(id+"F0.wireOp",EDGE,"E6"),sQuery(id+"F0.wireOp",EDGE,"E7"),sQuery(id+"F0.wireOp",EDGE,"E9.rect.left"),sQuery(id+"F0.wireOp",EDGE,"E9.rect.right"),sQuery(id+"F0.wireOp",EDGE,"E10.rect.bottom"),sQuery(id+"F0.wireOp",EDGE,"E10.rect.top"),subQ1,sQuery(id+"F0.wireOp",EDGE,"E11.rect.top"),subQ0,sQuery(id+"F0.wireOp",EDGE,"E12.rect.right"),sQuery(id+"F0.wireOp",EDGE,"E13.rect.left"),sQuery(id+"F0.wireOp",EDGE,"E13.rect.right"),sQuery(id+"F0.wireOp",EDGE,"E14.left"),sQuery(id+"F0.wireOp",EDGE,"E14.right"),sQuery(id+"F0.wireOp",EDGE,"E15"),sQuery(id+"F0.wireOp",EDGE,"E17"),sQuery(id+"F0.wireOp",EDGE,"E18"),sQuery(id+"F0.wireOp",EDGE,"E20"),sQuery(id+"F0.wireOp",EDGE,"E21.rect.bottom"),sQuery(id+"F0.wireOp",EDGE,"E21.rect.top"),sQuery(id+"F0.wireOp",EDGE,"E22.left"),sQuery(id+"F0.wireOp",EDGE,"E22.right"),sQuery(id+"F0.wireOp",EDGE,"E23.top"),sQuery(id+"F0.wireOp",EDGE,"E23.left"),sQuery(id+"F0.wireOp",EDGE,"E23.right"),sQuery(id+"F0.wireOp",EDGE,"E22.top"),sQuery(id+"F0.wireOp",EDGE,"E26"),sQuery(id+"F0.wireOp",EDGE,"E29"),sQuery(id+"F0.wireOp",EDGE,"E32"),sQuery(id+"F0.wireOp",EDGE,"E35"),sQuery(id+"F0.wireOp",EDGE,"E36"),sQuery(id+"F0.wireOp",EDGE,"E41"),sQuery(id+"F0.wireOp",EDGE,"E44"),sQuery(id+"F0.wireOp",EDGE,"E47"),sQuery(id+"F0.wireOp",EDGE,"E48"),sQuery(id+"F0.wireOp",EDGE,"E49"),sQuery(id+"F0.wireOp",EDGE,"E50"),sQuery(id+"F0.wireOp",EDGE,"E51")])],"isStart":false})]});}
            var Q62;
            Q62=makeQuery(id+"F1.opExtrude","CAP_EDGE",EDGE,{"disambiguationData":[OSD([sQuery(id+"F0.wireOp",EDGE,"E12.rect.left")])],"isStart":false});
            var Q63;
            {var subQ0=sQuery(id+"F0.wireOp",EDGE,"E12.rect.left");var subQ1=sQuery(id+"F0.wireOp",EDGE,"E11.rect.top");Q63=makeQuery(id+"F4.opFillet","BLEND_EDGE",EDGE,{"blendedFrom":[makeQuery(id+"F1.opExtrude","SWEPT_EDGE",EDGE,{"disambiguationData":[OSD([subQ1,subQ0])]}),makeQuery(id+"F1.opExtrude","CAP_FACE",FACE,{"disambiguationData":[OSD([sQuery(id+"F0.wireOp",EDGE,"E0"),sQuery(id+"F0.wireOp",EDGE,"E1"),sQuery(id+"F0.wireOp",EDGE,"E2"),sQuery(id+"F0.wireOp",EDGE,"E3"),sQuery(id+"F0.wireOp",EDGE,"E4"),sQuery(id+"F0.wireOp",EDGE,"E5"),sQuery(id+"F0.wireOp",EDGE,"E6"),sQuery(id+"F0.wireOp",EDGE,"E7"),sQuery(id+"F0.wireOp",EDGE,"E9.rect.left"),sQuery(id+"F0.wireOp",EDGE,"E9.rect.right"),sQuery(id+"F0.wireOp",EDGE,"E10.rect.bottom"),sQuery(id+"F0.wireOp",EDGE,"E10.rect.top"),sQuery(id+"F0.wireOp",EDGE,"E11.rect.bottom"),subQ1,subQ0,sQuery(id+"F0.wireOp",EDGE,"E12.rect.right"),sQuery(id+"F0.wireOp",EDGE,"E13.rect.left"),sQuery(id+"F0.wireOp",EDGE,"E13.rect.right"),sQuery(id+"F0.wireOp",EDGE,"E14.left"),sQuery(id+"F0.wireOp",EDGE,"E14.right"),sQuery(id+"F0.wireOp",EDGE,"E15"),sQuery(id+"F0.wireOp",EDGE,"E17"),sQuery(id+"F0.wireOp",EDGE,"E18"),sQuery(id+"F0.wireOp",EDGE,"E20"),sQuery(id+"F0.wireOp",EDGE,"E21.rect.bottom"),sQuery(id+"F0.wireOp",EDGE,"E21.rect.top"),sQuery(id+"F0.wireOp",EDGE,"E22.left"),sQuery(id+"F0.wireOp",EDGE,"E22.right"),sQuery(id+"F0.wireOp",EDGE,"E23.top"),sQuery(id+"F0.wireOp",EDGE,"E23.left"),sQuery(id+"F0.wireOp",EDGE,"E23.right"),sQuery(id+"F0.wireOp",EDGE,"E22.top"),sQuery(id+"F0.wireOp",EDGE,"E26"),sQuery(id+"F0.wireOp",EDGE,"E29"),sQuery(id+"F0.wireOp",EDGE,"E32"),sQuery(id+"F0.wireOp",EDGE,"E35"),sQuery(id+"F0.wireOp",EDGE,"E36"),sQuery(id+"F0.wireOp",EDGE,"E41"),sQuery(id+"F0.wireOp",EDGE,"E44"),sQuery(id+"F0.wireOp",EDGE,"E47"),sQuery(id+"F0.wireOp",EDGE,"E48"),sQuery(id+"F0.wireOp",EDGE,"E49"),sQuery(id+"F0.wireOp",EDGE,"E50"),sQuery(id+"F0.wireOp",EDGE,"E51")])],"isStart":false})],"blendedInto":[makeQuery(id+"F1.opExtrude","CAP_FACE",FACE,{"disambiguationData":[OSD([sQuery(id+"F0.wireOp",EDGE,"E0"),sQuery(id+"F0.wireOp",EDGE,"E1"),sQuery(id+"F0.wireOp",EDGE,"E2"),sQuery(id+"F0.wireOp",EDGE,"E3"),sQuery(id+"F0.wireOp",EDGE,"E4"),sQuery(id+"F0.wireOp",EDGE,"E5"),sQuery(id+"F0.wireOp",EDGE,"E6"),sQuery(id+"F0.wireOp",EDGE,"E7"),sQuery(id+"F0.wireOp",EDGE,"E9.rect.left"),sQuery(id+"F0.wireOp",EDGE,"E9.rect.right"),sQuery(id+"F0.wireOp",EDGE,"E10.rect.bottom"),sQuery(id+"F0.wireOp",EDGE,"E10.rect.top"),sQuery(id+"F0.wireOp",EDGE,"E11.rect.bottom"),subQ1,subQ0,sQuery(id+"F0.wireOp",EDGE,"E12.rect.right"),sQuery(id+"F0.wireOp",EDGE,"E13.rect.left"),sQuery(id+"F0.wireOp",EDGE,"E13.rect.right"),sQuery(id+"F0.wireOp",EDGE,"E14.left"),sQuery(id+"F0.wireOp",EDGE,"E14.right"),sQuery(id+"F0.wireOp",EDGE,"E15"),sQuery(id+"F0.wireOp",EDGE,"E17"),sQuery(id+"F0.wireOp",EDGE,"E18"),sQuery(id+"F0.wireOp",EDGE,"E20"),sQuery(id+"F0.wireOp",EDGE,"E21.rect.bottom"),sQuery(id+"F0.wireOp",EDGE,"E21.rect.top"),sQuery(id+"F0.wireOp",EDGE,"E22.left"),sQuery(id+"F0.wireOp",EDGE,"E22.right"),sQuery(id+"F0.wireOp",EDGE,"E23.top"),sQuery(id+"F0.wireOp",EDGE,"E23.left"),sQuery(id+"F0.wireOp",EDGE,"E23.right"),sQuery(id+"F0.wireOp",EDGE,"E22.top"),sQuery(id+"F0.wireOp",EDGE,"E26"),sQuery(id+"F0.wireOp",EDGE,"E29"),sQuery(id+"F0.wireOp",EDGE,"E32"),sQuery(id+"F0.wireOp",EDGE,"E35"),sQuery(id+"F0.wireOp",EDGE,"E36"),sQuery(id+"F0.wireOp",EDGE,"E41"),sQuery(id+"F0.wireOp",EDGE,"E44"),sQuery(id+"F0.wireOp",EDGE,"E47"),sQuery(id+"F0.wireOp",EDGE,"E48"),sQuery(id+"F0.wireOp",EDGE,"E49"),sQuery(id+"F0.wireOp",EDGE,"E50"),sQuery(id+"F0.wireOp",EDGE,"E51")])],"isStart":false})]});}
            var Q64;
            Q64=makeQuery(id+"F1.opExtrude","CAP_EDGE",EDGE,{"disambiguationData":[OSD([sQuery(id+"F0.wireOp",EDGE,"E10.rect.top")])],"isStart":true});
            var Q65;
            {var subQ0=sQuery(id+"F0.wireOp",EDGE,"E41");var subQ1=sQuery(id+"F0.wireOp",EDGE,"E12.rect.left");var subQ2=sQuery(id+"F0.wireOp",EDGE,"E10.rect.top");Q65=makeQuery(id+"F4.opFillet","BLEND_EDGE",EDGE,{"blendedFrom":[makeQuery(id+"F1.opExtrude","SWEPT_EDGE",EDGE,{"disambiguationData":[OSD([subQ2,subQ1,subQ0])]}),makeQuery(id+"F1.opExtrude","CAP_FACE",FACE,{"disambiguationData":[OSD([sQuery(id+"F0.wireOp",EDGE,"E0"),sQuery(id+"F0.wireOp",EDGE,"E1"),sQuery(id+"F0.wireOp",EDGE,"E2"),sQuery(id+"F0.wireOp",EDGE,"E3"),sQuery(id+"F0.wireOp",EDGE,"E4"),sQuery(id+"F0.wireOp",EDGE,"E5"),sQuery(id+"F0.wireOp",EDGE,"E6"),sQuery(id+"F0.wireOp",EDGE,"E7"),sQuery(id+"F0.wireOp",EDGE,"E9.rect.left"),sQuery(id+"F0.wireOp",EDGE,"E9.rect.right"),sQuery(id+"F0.wireOp",EDGE,"E10.rect.bottom"),subQ2,sQuery(id+"F0.wireOp",EDGE,"E11.rect.bottom"),sQuery(id+"F0.wireOp",EDGE,"E11.rect.top"),subQ1,sQuery(id+"F0.wireOp",EDGE,"E12.rect.right"),sQuery(id+"F0.wireOp",EDGE,"E13.rect.left"),sQuery(id+"F0.wireOp",EDGE,"E13.rect.right"),sQuery(id+"F0.wireOp",EDGE,"E14.left"),sQuery(id+"F0.wireOp",EDGE,"E14.right"),sQuery(id+"F0.wireOp",EDGE,"E15"),sQuery(id+"F0.wireOp",EDGE,"E17"),sQuery(id+"F0.wireOp",EDGE,"E18"),sQuery(id+"F0.wireOp",EDGE,"E20"),sQuery(id+"F0.wireOp",EDGE,"E21.rect.bottom"),sQuery(id+"F0.wireOp",EDGE,"E21.rect.top"),sQuery(id+"F0.wireOp",EDGE,"E22.left"),sQuery(id+"F0.wireOp",EDGE,"E22.right"),sQuery(id+"F0.wireOp",EDGE,"E23.top"),sQuery(id+"F0.wireOp",EDGE,"E23.left"),sQuery(id+"F0.wireOp",EDGE,"E23.right"),sQuery(id+"F0.wireOp",EDGE,"E22.top"),sQuery(id+"F0.wireOp",EDGE,"E26"),sQuery(id+"F0.wireOp",EDGE,"E29"),sQuery(id+"F0.wireOp",EDGE,"E32"),sQuery(id+"F0.wireOp",EDGE,"E35"),sQuery(id+"F0.wireOp",EDGE,"E36"),subQ0,sQuery(id+"F0.wireOp",EDGE,"E44"),sQuery(id+"F0.wireOp",EDGE,"E47"),sQuery(id+"F0.wireOp",EDGE,"E48"),sQuery(id+"F0.wireOp",EDGE,"E49"),sQuery(id+"F0.wireOp",EDGE,"E50"),sQuery(id+"F0.wireOp",EDGE,"E51")])],"isStart":true})],"blendedInto":[makeQuery(id+"F1.opExtrude","CAP_FACE",FACE,{"disambiguationData":[OSD([sQuery(id+"F0.wireOp",EDGE,"E0"),sQuery(id+"F0.wireOp",EDGE,"E1"),sQuery(id+"F0.wireOp",EDGE,"E2"),sQuery(id+"F0.wireOp",EDGE,"E3"),sQuery(id+"F0.wireOp",EDGE,"E4"),sQuery(id+"F0.wireOp",EDGE,"E5"),sQuery(id+"F0.wireOp",EDGE,"E6"),sQuery(id+"F0.wireOp",EDGE,"E7"),sQuery(id+"F0.wireOp",EDGE,"E9.rect.left"),sQuery(id+"F0.wireOp",EDGE,"E9.rect.right"),sQuery(id+"F0.wireOp",EDGE,"E10.rect.bottom"),subQ2,sQuery(id+"F0.wireOp",EDGE,"E11.rect.bottom"),sQuery(id+"F0.wireOp",EDGE,"E11.rect.top"),subQ1,sQuery(id+"F0.wireOp",EDGE,"E12.rect.right"),sQuery(id+"F0.wireOp",EDGE,"E13.rect.left"),sQuery(id+"F0.wireOp",EDGE,"E13.rect.right"),sQuery(id+"F0.wireOp",EDGE,"E14.left"),sQuery(id+"F0.wireOp",EDGE,"E14.right"),sQuery(id+"F0.wireOp",EDGE,"E15"),sQuery(id+"F0.wireOp",EDGE,"E17"),sQuery(id+"F0.wireOp",EDGE,"E18"),sQuery(id+"F0.wireOp",EDGE,"E20"),sQuery(id+"F0.wireOp",EDGE,"E21.rect.bottom"),sQuery(id+"F0.wireOp",EDGE,"E21.rect.top"),sQuery(id+"F0.wireOp",EDGE,"E22.left"),sQuery(id+"F0.wireOp",EDGE,"E22.right"),sQuery(id+"F0.wireOp",EDGE,"E23.top"),sQuery(id+"F0.wireOp",EDGE,"E23.left"),sQuery(id+"F0.wireOp",EDGE,"E23.right"),sQuery(id+"F0.wireOp",EDGE,"E22.top"),sQuery(id+"F0.wireOp",EDGE,"E26"),sQuery(id+"F0.wireOp",EDGE,"E29"),sQuery(id+"F0.wireOp",EDGE,"E32"),sQuery(id+"F0.wireOp",EDGE,"E35"),sQuery(id+"F0.wireOp",EDGE,"E36"),subQ0,sQuery(id+"F0.wireOp",EDGE,"E44"),sQuery(id+"F0.wireOp",EDGE,"E47"),sQuery(id+"F0.wireOp",EDGE,"E48"),sQuery(id+"F0.wireOp",EDGE,"E49"),sQuery(id+"F0.wireOp",EDGE,"E50"),sQuery(id+"F0.wireOp",EDGE,"E51")])],"isStart":true})]});}
            var Q66;
            Q66=makeQuery(id+"F1.opExtrude","CAP_EDGE",EDGE,{"disambiguationData":[OSD([sQuery(id+"F0.wireOp",EDGE,"E41")])],"isStart":true});
            var Q67;
            Q67=makeQuery(id+"F1.opExtrude","CAP_EDGE",EDGE,{"disambiguationData":[OSD([sQuery(id+"F0.wireOp",EDGE,"E2")])],"isStart":true});
            var Q68;
            {var subQ0=sQuery(id+"F0.wireOp",EDGE,"E32");var subQ1=sQuery(id+"F0.wireOp",EDGE,"E6");Q68=makeQuery(id+"F2.opFillet","BLEND_EDGE",EDGE,{"blendedFrom":[makeQuery(id+"F1.opExtrude","SWEPT_EDGE",EDGE,{"disambiguationData":[OSD([subQ1,subQ0])]}),makeQuery(id+"F1.opExtrude","CAP_FACE",FACE,{"disambiguationData":[OSD([sQuery(id+"F0.wireOp",EDGE,"E0"),sQuery(id+"F0.wireOp",EDGE,"E1"),sQuery(id+"F0.wireOp",EDGE,"E2"),sQuery(id+"F0.wireOp",EDGE,"E3"),sQuery(id+"F0.wireOp",EDGE,"E4"),sQuery(id+"F0.wireOp",EDGE,"E5"),subQ1,sQuery(id+"F0.wireOp",EDGE,"E7"),sQuery(id+"F0.wireOp",EDGE,"E9.rect.left"),sQuery(id+"F0.wireOp",EDGE,"E9.rect.right"),sQuery(id+"F0.wireOp",EDGE,"E10.rect.bottom"),sQuery(id+"F0.wireOp",EDGE,"E10.rect.top"),sQuery(id+"F0.wireOp",EDGE,"E11.rect.bottom"),sQuery(id+"F0.wireOp",EDGE,"E11.rect.top"),sQuery(id+"F0.wireOp",EDGE,"E12.rect.left"),sQuery(id+"F0.wireOp",EDGE,"E12.rect.right"),sQuery(id+"F0.wireOp",EDGE,"E13.rect.left"),sQuery(id+"F0.wireOp",EDGE,"E13.rect.right"),sQuery(id+"F0.wireOp",EDGE,"E14.left"),sQuery(id+"F0.wireOp",EDGE,"E14.right"),sQuery(id+"F0.wireOp",EDGE,"E15"),sQuery(id+"F0.wireOp",EDGE,"E17"),sQuery(id+"F0.wireOp",EDGE,"E18"),sQuery(id+"F0.wireOp",EDGE,"E20"),sQuery(id+"F0.wireOp",EDGE,"E21.rect.bottom"),sQuery(id+"F0.wireOp",EDGE,"E21.rect.top"),sQuery(id+"F0.wireOp",EDGE,"E22.left"),sQuery(id+"F0.wireOp",EDGE,"E22.right"),sQuery(id+"F0.wireOp",EDGE,"E23.top"),sQuery(id+"F0.wireOp",EDGE,"E23.left"),sQuery(id+"F0.wireOp",EDGE,"E23.right"),sQuery(id+"F0.wireOp",EDGE,"E22.top"),sQuery(id+"F0.wireOp",EDGE,"E26"),sQuery(id+"F0.wireOp",EDGE,"E29"),subQ0,sQuery(id+"F0.wireOp",EDGE,"E35"),sQuery(id+"F0.wireOp",EDGE,"E36"),sQuery(id+"F0.wireOp",EDGE,"E41"),sQuery(id+"F0.wireOp",EDGE,"E44"),sQuery(id+"F0.wireOp",EDGE,"E47"),sQuery(id+"F0.wireOp",EDGE,"E48"),sQuery(id+"F0.wireOp",EDGE,"E49"),sQuery(id+"F0.wireOp",EDGE,"E50"),sQuery(id+"F0.wireOp",EDGE,"E51")])],"isStart":true})],"blendedInto":[makeQuery(id+"F1.opExtrude","CAP_FACE",FACE,{"disambiguationData":[OSD([sQuery(id+"F0.wireOp",EDGE,"E0"),sQuery(id+"F0.wireOp",EDGE,"E1"),sQuery(id+"F0.wireOp",EDGE,"E2"),sQuery(id+"F0.wireOp",EDGE,"E3"),sQuery(id+"F0.wireOp",EDGE,"E4"),sQuery(id+"F0.wireOp",EDGE,"E5"),subQ1,sQuery(id+"F0.wireOp",EDGE,"E7"),sQuery(id+"F0.wireOp",EDGE,"E9.rect.left"),sQuery(id+"F0.wireOp",EDGE,"E9.rect.right"),sQuery(id+"F0.wireOp",EDGE,"E10.rect.bottom"),sQuery(id+"F0.wireOp",EDGE,"E10.rect.top"),sQuery(id+"F0.wireOp",EDGE,"E11.rect.bottom"),sQuery(id+"F0.wireOp",EDGE,"E11.rect.top"),sQuery(id+"F0.wireOp",EDGE,"E12.rect.left"),sQuery(id+"F0.wireOp",EDGE,"E12.rect.right"),sQuery(id+"F0.wireOp",EDGE,"E13.rect.left"),sQuery(id+"F0.wireOp",EDGE,"E13.rect.right"),sQuery(id+"F0.wireOp",EDGE,"E14.left"),sQuery(id+"F0.wireOp",EDGE,"E14.right"),sQuery(id+"F0.wireOp",EDGE,"E15"),sQuery(id+"F0.wireOp",EDGE,"E17"),sQuery(id+"F0.wireOp",EDGE,"E18"),sQuery(id+"F0.wireOp",EDGE,"E20"),sQuery(id+"F0.wireOp",EDGE,"E21.rect.bottom"),sQuery(id+"F0.wireOp",EDGE,"E21.rect.top"),sQuery(id+"F0.wireOp",EDGE,"E22.left"),sQuery(id+"F0.wireOp",EDGE,"E22.right"),sQuery(id+"F0.wireOp",EDGE,"E23.top"),sQuery(id+"F0.wireOp",EDGE,"E23.left"),sQuery(id+"F0.wireOp",EDGE,"E23.right"),sQuery(id+"F0.wireOp",EDGE,"E22.top"),sQuery(id+"F0.wireOp",EDGE,"E26"),sQuery(id+"F0.wireOp",EDGE,"E29"),subQ0,sQuery(id+"F0.wireOp",EDGE,"E35"),sQuery(id+"F0.wireOp",EDGE,"E36"),sQuery(id+"F0.wireOp",EDGE,"E41"),sQuery(id+"F0.wireOp",EDGE,"E44"),sQuery(id+"F0.wireOp",EDGE,"E47"),sQuery(id+"F0.wireOp",EDGE,"E48"),sQuery(id+"F0.wireOp",EDGE,"E49"),sQuery(id+"F0.wireOp",EDGE,"E50"),sQuery(id+"F0.wireOp",EDGE,"E51")])],"isStart":true})]});}
            var Q69;
            {var subQ0=sQuery(id+"F0.wireOp",EDGE,"E9.rect.left");var subQ1=sQuery(id+"F0.wireOp",EDGE,"E2");Q69=makeQuery(id+"F3.opFillet","BLEND_EDGE",EDGE,{"blendedFrom":[makeQuery(id+"F1.opExtrude","SWEPT_EDGE",EDGE,{"disambiguationData":[OSD([subQ1,subQ0])]}),makeQuery(id+"F1.opExtrude","CAP_FACE",FACE,{"disambiguationData":[OSD([sQuery(id+"F0.wireOp",EDGE,"E0"),sQuery(id+"F0.wireOp",EDGE,"E1"),subQ1,sQuery(id+"F0.wireOp",EDGE,"E3"),sQuery(id+"F0.wireOp",EDGE,"E4"),sQuery(id+"F0.wireOp",EDGE,"E5"),sQuery(id+"F0.wireOp",EDGE,"E6"),sQuery(id+"F0.wireOp",EDGE,"E7"),subQ0,sQuery(id+"F0.wireOp",EDGE,"E9.rect.right"),sQuery(id+"F0.wireOp",EDGE,"E10.rect.bottom"),sQuery(id+"F0.wireOp",EDGE,"E10.rect.top"),sQuery(id+"F0.wireOp",EDGE,"E11.rect.bottom"),sQuery(id+"F0.wireOp",EDGE,"E11.rect.top"),sQuery(id+"F0.wireOp",EDGE,"E12.rect.left"),sQuery(id+"F0.wireOp",EDGE,"E12.rect.right"),sQuery(id+"F0.wireOp",EDGE,"E13.rect.left"),sQuery(id+"F0.wireOp",EDGE,"E13.rect.right"),sQuery(id+"F0.wireOp",EDGE,"E14.left"),sQuery(id+"F0.wireOp",EDGE,"E14.right"),sQuery(id+"F0.wireOp",EDGE,"E15"),sQuery(id+"F0.wireOp",EDGE,"E17"),sQuery(id+"F0.wireOp",EDGE,"E18"),sQuery(id+"F0.wireOp",EDGE,"E20"),sQuery(id+"F0.wireOp",EDGE,"E21.rect.bottom"),sQuery(id+"F0.wireOp",EDGE,"E21.rect.top"),sQuery(id+"F0.wireOp",EDGE,"E22.left"),sQuery(id+"F0.wireOp",EDGE,"E22.right"),sQuery(id+"F0.wireOp",EDGE,"E23.top"),sQuery(id+"F0.wireOp",EDGE,"E23.left"),sQuery(id+"F0.wireOp",EDGE,"E23.right"),sQuery(id+"F0.wireOp",EDGE,"E22.top"),sQuery(id+"F0.wireOp",EDGE,"E26"),sQuery(id+"F0.wireOp",EDGE,"E29"),sQuery(id+"F0.wireOp",EDGE,"E32"),sQuery(id+"F0.wireOp",EDGE,"E35"),sQuery(id+"F0.wireOp",EDGE,"E36"),sQuery(id+"F0.wireOp",EDGE,"E41"),sQuery(id+"F0.wireOp",EDGE,"E44"),sQuery(id+"F0.wireOp",EDGE,"E47"),sQuery(id+"F0.wireOp",EDGE,"E48"),sQuery(id+"F0.wireOp",EDGE,"E49"),sQuery(id+"F0.wireOp",EDGE,"E50"),sQuery(id+"F0.wireOp",EDGE,"E51")])],"isStart":true})],"blendedInto":[makeQuery(id+"F1.opExtrude","CAP_FACE",FACE,{"disambiguationData":[OSD([sQuery(id+"F0.wireOp",EDGE,"E0"),sQuery(id+"F0.wireOp",EDGE,"E1"),subQ1,sQuery(id+"F0.wireOp",EDGE,"E3"),sQuery(id+"F0.wireOp",EDGE,"E4"),sQuery(id+"F0.wireOp",EDGE,"E5"),sQuery(id+"F0.wireOp",EDGE,"E6"),sQuery(id+"F0.wireOp",EDGE,"E7"),subQ0,sQuery(id+"F0.wireOp",EDGE,"E9.rect.right"),sQuery(id+"F0.wireOp",EDGE,"E10.rect.bottom"),sQuery(id+"F0.wireOp",EDGE,"E10.rect.top"),sQuery(id+"F0.wireOp",EDGE,"E11.rect.bottom"),sQuery(id+"F0.wireOp",EDGE,"E11.rect.top"),sQuery(id+"F0.wireOp",EDGE,"E12.rect.left"),sQuery(id+"F0.wireOp",EDGE,"E12.rect.right"),sQuery(id+"F0.wireOp",EDGE,"E13.rect.left"),sQuery(id+"F0.wireOp",EDGE,"E13.rect.right"),sQuery(id+"F0.wireOp",EDGE,"E14.left"),sQuery(id+"F0.wireOp",EDGE,"E14.right"),sQuery(id+"F0.wireOp",EDGE,"E15"),sQuery(id+"F0.wireOp",EDGE,"E17"),sQuery(id+"F0.wireOp",EDGE,"E18"),sQuery(id+"F0.wireOp",EDGE,"E20"),sQuery(id+"F0.wireOp",EDGE,"E21.rect.bottom"),sQuery(id+"F0.wireOp",EDGE,"E21.rect.top"),sQuery(id+"F0.wireOp",EDGE,"E22.left"),sQuery(id+"F0.wireOp",EDGE,"E22.right"),sQuery(id+"F0.wireOp",EDGE,"E23.top"),sQuery(id+"F0.wireOp",EDGE,"E23.left"),sQuery(id+"F0.wireOp",EDGE,"E23.right"),sQuery(id+"F0.wireOp",EDGE,"E22.top"),sQuery(id+"F0.wireOp",EDGE,"E26"),sQuery(id+"F0.wireOp",EDGE,"E29"),sQuery(id+"F0.wireOp",EDGE,"E32"),sQuery(id+"F0.wireOp",EDGE,"E35"),sQuery(id+"F0.wireOp",EDGE,"E36"),sQuery(id+"F0.wireOp",EDGE,"E41"),sQuery(id+"F0.wireOp",EDGE,"E44"),sQuery(id+"F0.wireOp",EDGE,"E47"),sQuery(id+"F0.wireOp",EDGE,"E48"),sQuery(id+"F0.wireOp",EDGE,"E49"),sQuery(id+"F0.wireOp",EDGE,"E50"),sQuery(id+"F0.wireOp",EDGE,"E51")])],"isStart":true})]});}
            var Q70;
            Q70=makeQuery(id+"F1.opExtrude","CAP_EDGE",EDGE,{"disambiguationData":[OSD([sQuery(id+"F0.wireOp",EDGE,"E6")])],"isStart":true});
            var Q71;
            {var subQ0=sQuery(id+"F0.wireOp",EDGE,"E51");var subQ1=sQuery(id+"F0.wireOp",EDGE,"E6");Q71=makeQuery(id+"F3.opFillet","BLEND_EDGE",EDGE,{"blendedFrom":[makeQuery(id+"F1.opExtrude","SWEPT_EDGE",EDGE,{"disambiguationData":[OSD([subQ1,subQ0])]}),makeQuery(id+"F1.opExtrude","CAP_FACE",FACE,{"disambiguationData":[OSD([sQuery(id+"F0.wireOp",EDGE,"E0"),sQuery(id+"F0.wireOp",EDGE,"E1"),sQuery(id+"F0.wireOp",EDGE,"E2"),sQuery(id+"F0.wireOp",EDGE,"E3"),sQuery(id+"F0.wireOp",EDGE,"E4"),sQuery(id+"F0.wireOp",EDGE,"E5"),subQ1,sQuery(id+"F0.wireOp",EDGE,"E7"),sQuery(id+"F0.wireOp",EDGE,"E9.rect.left"),sQuery(id+"F0.wireOp",EDGE,"E9.rect.right"),sQuery(id+"F0.wireOp",EDGE,"E10.rect.bottom"),sQuery(id+"F0.wireOp",EDGE,"E10.rect.top"),sQuery(id+"F0.wireOp",EDGE,"E11.rect.bottom"),sQuery(id+"F0.wireOp",EDGE,"E11.rect.top"),sQuery(id+"F0.wireOp",EDGE,"E12.rect.left"),sQuery(id+"F0.wireOp",EDGE,"E12.rect.right"),sQuery(id+"F0.wireOp",EDGE,"E13.rect.left"),sQuery(id+"F0.wireOp",EDGE,"E13.rect.right"),sQuery(id+"F0.wireOp",EDGE,"E14.left"),sQuery(id+"F0.wireOp",EDGE,"E14.right"),sQuery(id+"F0.wireOp",EDGE,"E15"),sQuery(id+"F0.wireOp",EDGE,"E17"),sQuery(id+"F0.wireOp",EDGE,"E18"),sQuery(id+"F0.wireOp",EDGE,"E20"),sQuery(id+"F0.wireOp",EDGE,"E21.rect.bottom"),sQuery(id+"F0.wireOp",EDGE,"E21.rect.top"),sQuery(id+"F0.wireOp",EDGE,"E22.left"),sQuery(id+"F0.wireOp",EDGE,"E22.right"),sQuery(id+"F0.wireOp",EDGE,"E23.top"),sQuery(id+"F0.wireOp",EDGE,"E23.left"),sQuery(id+"F0.wireOp",EDGE,"E23.right"),sQuery(id+"F0.wireOp",EDGE,"E22.top"),sQuery(id+"F0.wireOp",EDGE,"E26"),sQuery(id+"F0.wireOp",EDGE,"E29"),sQuery(id+"F0.wireOp",EDGE,"E32"),sQuery(id+"F0.wireOp",EDGE,"E35"),sQuery(id+"F0.wireOp",EDGE,"E36"),sQuery(id+"F0.wireOp",EDGE,"E41"),sQuery(id+"F0.wireOp",EDGE,"E44"),sQuery(id+"F0.wireOp",EDGE,"E47"),sQuery(id+"F0.wireOp",EDGE,"E48"),sQuery(id+"F0.wireOp",EDGE,"E49"),sQuery(id+"F0.wireOp",EDGE,"E50"),subQ0])],"isStart":true})],"blendedInto":[makeQuery(id+"F1.opExtrude","CAP_FACE",FACE,{"disambiguationData":[OSD([sQuery(id+"F0.wireOp",EDGE,"E0"),sQuery(id+"F0.wireOp",EDGE,"E1"),sQuery(id+"F0.wireOp",EDGE,"E2"),sQuery(id+"F0.wireOp",EDGE,"E3"),sQuery(id+"F0.wireOp",EDGE,"E4"),sQuery(id+"F0.wireOp",EDGE,"E5"),subQ1,sQuery(id+"F0.wireOp",EDGE,"E7"),sQuery(id+"F0.wireOp",EDGE,"E9.rect.left"),sQuery(id+"F0.wireOp",EDGE,"E9.rect.right"),sQuery(id+"F0.wireOp",EDGE,"E10.rect.bottom"),sQuery(id+"F0.wireOp",EDGE,"E10.rect.top"),sQuery(id+"F0.wireOp",EDGE,"E11.rect.bottom"),sQuery(id+"F0.wireOp",EDGE,"E11.rect.top"),sQuery(id+"F0.wireOp",EDGE,"E12.rect.left"),sQuery(id+"F0.wireOp",EDGE,"E12.rect.right"),sQuery(id+"F0.wireOp",EDGE,"E13.rect.left"),sQuery(id+"F0.wireOp",EDGE,"E13.rect.right"),sQuery(id+"F0.wireOp",EDGE,"E14.left"),sQuery(id+"F0.wireOp",EDGE,"E14.right"),sQuery(id+"F0.wireOp",EDGE,"E15"),sQuery(id+"F0.wireOp",EDGE,"E17"),sQuery(id+"F0.wireOp",EDGE,"E18"),sQuery(id+"F0.wireOp",EDGE,"E20"),sQuery(id+"F0.wireOp",EDGE,"E21.rect.bottom"),sQuery(id+"F0.wireOp",EDGE,"E21.rect.top"),sQuery(id+"F0.wireOp",EDGE,"E22.left"),sQuery(id+"F0.wireOp",EDGE,"E22.right"),sQuery(id+"F0.wireOp",EDGE,"E23.top"),sQuery(id+"F0.wireOp",EDGE,"E23.left"),sQuery(id+"F0.wireOp",EDGE,"E23.right"),sQuery(id+"F0.wireOp",EDGE,"E22.top"),sQuery(id+"F0.wireOp",EDGE,"E26"),sQuery(id+"F0.wireOp",EDGE,"E29"),sQuery(id+"F0.wireOp",EDGE,"E32"),sQuery(id+"F0.wireOp",EDGE,"E35"),sQuery(id+"F0.wireOp",EDGE,"E36"),sQuery(id+"F0.wireOp",EDGE,"E41"),sQuery(id+"F0.wireOp",EDGE,"E44"),sQuery(id+"F0.wireOp",EDGE,"E47"),sQuery(id+"F0.wireOp",EDGE,"E48"),sQuery(id+"F0.wireOp",EDGE,"E49"),sQuery(id+"F0.wireOp",EDGE,"E50"),subQ0])],"isStart":true})]});}
            var Q72;
            Q72=makeQuery(id+"F1.opExtrude","CAP_EDGE",EDGE,{"disambiguationData":[OSD([sQuery(id+"F0.wireOp",EDGE,"E51")])],"isStart":true});
            var Q73;
            {var subQ0=sQuery(id+"F0.wireOp",EDGE,"E51");var subQ1=sQuery(id+"F0.wireOp",EDGE,"E9.rect.left");Q73=makeQuery(id+"F3.opFillet","BLEND_EDGE",EDGE,{"blendedFrom":[makeQuery(id+"F1.opExtrude","SWEPT_EDGE",EDGE,{"disambiguationData":[OSD([subQ1,subQ0])]}),makeQuery(id+"F1.opExtrude","CAP_FACE",FACE,{"disambiguationData":[OSD([sQuery(id+"F0.wireOp",EDGE,"E0"),sQuery(id+"F0.wireOp",EDGE,"E1"),sQuery(id+"F0.wireOp",EDGE,"E2"),sQuery(id+"F0.wireOp",EDGE,"E3"),sQuery(id+"F0.wireOp",EDGE,"E4"),sQuery(id+"F0.wireOp",EDGE,"E5"),sQuery(id+"F0.wireOp",EDGE,"E6"),sQuery(id+"F0.wireOp",EDGE,"E7"),subQ1,sQuery(id+"F0.wireOp",EDGE,"E9.rect.right"),sQuery(id+"F0.wireOp",EDGE,"E10.rect.bottom"),sQuery(id+"F0.wireOp",EDGE,"E10.rect.top"),sQuery(id+"F0.wireOp",EDGE,"E11.rect.bottom"),sQuery(id+"F0.wireOp",EDGE,"E11.rect.top"),sQuery(id+"F0.wireOp",EDGE,"E12.rect.left"),sQuery(id+"F0.wireOp",EDGE,"E12.rect.right"),sQuery(id+"F0.wireOp",EDGE,"E13.rect.left"),sQuery(id+"F0.wireOp",EDGE,"E13.rect.right"),sQuery(id+"F0.wireOp",EDGE,"E14.left"),sQuery(id+"F0.wireOp",EDGE,"E14.right"),sQuery(id+"F0.wireOp",EDGE,"E15"),sQuery(id+"F0.wireOp",EDGE,"E17"),sQuery(id+"F0.wireOp",EDGE,"E18"),sQuery(id+"F0.wireOp",EDGE,"E20"),sQuery(id+"F0.wireOp",EDGE,"E21.rect.bottom"),sQuery(id+"F0.wireOp",EDGE,"E21.rect.top"),sQuery(id+"F0.wireOp",EDGE,"E22.left"),sQuery(id+"F0.wireOp",EDGE,"E22.right"),sQuery(id+"F0.wireOp",EDGE,"E23.top"),sQuery(id+"F0.wireOp",EDGE,"E23.left"),sQuery(id+"F0.wireOp",EDGE,"E23.right"),sQuery(id+"F0.wireOp",EDGE,"E22.top"),sQuery(id+"F0.wireOp",EDGE,"E26"),sQuery(id+"F0.wireOp",EDGE,"E29"),sQuery(id+"F0.wireOp",EDGE,"E32"),sQuery(id+"F0.wireOp",EDGE,"E35"),sQuery(id+"F0.wireOp",EDGE,"E36"),sQuery(id+"F0.wireOp",EDGE,"E41"),sQuery(id+"F0.wireOp",EDGE,"E44"),sQuery(id+"F0.wireOp",EDGE,"E47"),sQuery(id+"F0.wireOp",EDGE,"E48"),sQuery(id+"F0.wireOp",EDGE,"E49"),sQuery(id+"F0.wireOp",EDGE,"E50"),subQ0])],"isStart":true})],"blendedInto":[makeQuery(id+"F1.opExtrude","CAP_FACE",FACE,{"disambiguationData":[OSD([sQuery(id+"F0.wireOp",EDGE,"E0"),sQuery(id+"F0.wireOp",EDGE,"E1"),sQuery(id+"F0.wireOp",EDGE,"E2"),sQuery(id+"F0.wireOp",EDGE,"E3"),sQuery(id+"F0.wireOp",EDGE,"E4"),sQuery(id+"F0.wireOp",EDGE,"E5"),sQuery(id+"F0.wireOp",EDGE,"E6"),sQuery(id+"F0.wireOp",EDGE,"E7"),subQ1,sQuery(id+"F0.wireOp",EDGE,"E9.rect.right"),sQuery(id+"F0.wireOp",EDGE,"E10.rect.bottom"),sQuery(id+"F0.wireOp",EDGE,"E10.rect.top"),sQuery(id+"F0.wireOp",EDGE,"E11.rect.bottom"),sQuery(id+"F0.wireOp",EDGE,"E11.rect.top"),sQuery(id+"F0.wireOp",EDGE,"E12.rect.left"),sQuery(id+"F0.wireOp",EDGE,"E12.rect.right"),sQuery(id+"F0.wireOp",EDGE,"E13.rect.left"),sQuery(id+"F0.wireOp",EDGE,"E13.rect.right"),sQuery(id+"F0.wireOp",EDGE,"E14.left"),sQuery(id+"F0.wireOp",EDGE,"E14.right"),sQuery(id+"F0.wireOp",EDGE,"E15"),sQuery(id+"F0.wireOp",EDGE,"E17"),sQuery(id+"F0.wireOp",EDGE,"E18"),sQuery(id+"F0.wireOp",EDGE,"E20"),sQuery(id+"F0.wireOp",EDGE,"E21.rect.bottom"),sQuery(id+"F0.wireOp",EDGE,"E21.rect.top"),sQuery(id+"F0.wireOp",EDGE,"E22.left"),sQuery(id+"F0.wireOp",EDGE,"E22.right"),sQuery(id+"F0.wireOp",EDGE,"E23.top"),sQuery(id+"F0.wireOp",EDGE,"E23.left"),sQuery(id+"F0.wireOp",EDGE,"E23.right"),sQuery(id+"F0.wireOp",EDGE,"E22.top"),sQuery(id+"F0.wireOp",EDGE,"E26"),sQuery(id+"F0.wireOp",EDGE,"E29"),sQuery(id+"F0.wireOp",EDGE,"E32"),sQuery(id+"F0.wireOp",EDGE,"E35"),sQuery(id+"F0.wireOp",EDGE,"E36"),sQuery(id+"F0.wireOp",EDGE,"E41"),sQuery(id+"F0.wireOp",EDGE,"E44"),sQuery(id+"F0.wireOp",EDGE,"E47"),sQuery(id+"F0.wireOp",EDGE,"E48"),sQuery(id+"F0.wireOp",EDGE,"E49"),sQuery(id+"F0.wireOp",EDGE,"E50"),subQ0])],"isStart":true})]});}
            var Q74;
            {var subQ0=sQuery(id+"F0.wireOp",EDGE,"E9.rect.left");Q74=makeQuery(id+"F1.opExtrude","CAP_EDGE",EDGE,{"disambiguationData":[OSD([subQ0]),TDD([makeQuery(id+"F0.imprint","IMPRINT",EDGE,{"disambiguationData":[TD([[makeQuery(id+"F0.imprint","INTERSECT",VERTEX,{"derivedFrom":[subQ0,sQuery(id+"F0.wireOp",EDGE,"E49")]}),-1.0]])],"derivedFrom":subQ0})])],"isStart":true});}
            var Q75;
            {var subQ0=sQuery(id+"F0.wireOp",EDGE,"E49");var subQ1=sQuery(id+"F0.wireOp",EDGE,"E9.rect.left");Q75=makeQuery(id+"F3.opFillet","BLEND_EDGE",EDGE,{"blendedFrom":[makeQuery(id+"F1.opExtrude","SWEPT_EDGE",EDGE,{"disambiguationData":[OSD([subQ1,subQ0])]}),makeQuery(id+"F1.opExtrude","CAP_FACE",FACE,{"disambiguationData":[OSD([sQuery(id+"F0.wireOp",EDGE,"E0"),sQuery(id+"F0.wireOp",EDGE,"E1"),sQuery(id+"F0.wireOp",EDGE,"E2"),sQuery(id+"F0.wireOp",EDGE,"E3"),sQuery(id+"F0.wireOp",EDGE,"E4"),sQuery(id+"F0.wireOp",EDGE,"E5"),sQuery(id+"F0.wireOp",EDGE,"E6"),sQuery(id+"F0.wireOp",EDGE,"E7"),subQ1,sQuery(id+"F0.wireOp",EDGE,"E9.rect.right"),sQuery(id+"F0.wireOp",EDGE,"E10.rect.bottom"),sQuery(id+"F0.wireOp",EDGE,"E10.rect.top"),sQuery(id+"F0.wireOp",EDGE,"E11.rect.bottom"),sQuery(id+"F0.wireOp",EDGE,"E11.rect.top"),sQuery(id+"F0.wireOp",EDGE,"E12.rect.left"),sQuery(id+"F0.wireOp",EDGE,"E12.rect.right"),sQuery(id+"F0.wireOp",EDGE,"E13.rect.left"),sQuery(id+"F0.wireOp",EDGE,"E13.rect.right"),sQuery(id+"F0.wireOp",EDGE,"E14.left"),sQuery(id+"F0.wireOp",EDGE,"E14.right"),sQuery(id+"F0.wireOp",EDGE,"E15"),sQuery(id+"F0.wireOp",EDGE,"E17"),sQuery(id+"F0.wireOp",EDGE,"E18"),sQuery(id+"F0.wireOp",EDGE,"E20"),sQuery(id+"F0.wireOp",EDGE,"E21.rect.bottom"),sQuery(id+"F0.wireOp",EDGE,"E21.rect.top"),sQuery(id+"F0.wireOp",EDGE,"E22.left"),sQuery(id+"F0.wireOp",EDGE,"E22.right"),sQuery(id+"F0.wireOp",EDGE,"E23.top"),sQuery(id+"F0.wireOp",EDGE,"E23.left"),sQuery(id+"F0.wireOp",EDGE,"E23.right"),sQuery(id+"F0.wireOp",EDGE,"E22.top"),sQuery(id+"F0.wireOp",EDGE,"E26"),sQuery(id+"F0.wireOp",EDGE,"E29"),sQuery(id+"F0.wireOp",EDGE,"E32"),sQuery(id+"F0.wireOp",EDGE,"E35"),sQuery(id+"F0.wireOp",EDGE,"E36"),sQuery(id+"F0.wireOp",EDGE,"E41"),sQuery(id+"F0.wireOp",EDGE,"E44"),sQuery(id+"F0.wireOp",EDGE,"E47"),sQuery(id+"F0.wireOp",EDGE,"E48"),subQ0,sQuery(id+"F0.wireOp",EDGE,"E50"),sQuery(id+"F0.wireOp",EDGE,"E51")])],"isStart":true})],"blendedInto":[makeQuery(id+"F1.opExtrude","CAP_FACE",FACE,{"disambiguationData":[OSD([sQuery(id+"F0.wireOp",EDGE,"E0"),sQuery(id+"F0.wireOp",EDGE,"E1"),sQuery(id+"F0.wireOp",EDGE,"E2"),sQuery(id+"F0.wireOp",EDGE,"E3"),sQuery(id+"F0.wireOp",EDGE,"E4"),sQuery(id+"F0.wireOp",EDGE,"E5"),sQuery(id+"F0.wireOp",EDGE,"E6"),sQuery(id+"F0.wireOp",EDGE,"E7"),subQ1,sQuery(id+"F0.wireOp",EDGE,"E9.rect.right"),sQuery(id+"F0.wireOp",EDGE,"E10.rect.bottom"),sQuery(id+"F0.wireOp",EDGE,"E10.rect.top"),sQuery(id+"F0.wireOp",EDGE,"E11.rect.bottom"),sQuery(id+"F0.wireOp",EDGE,"E11.rect.top"),sQuery(id+"F0.wireOp",EDGE,"E12.rect.left"),sQuery(id+"F0.wireOp",EDGE,"E12.rect.right"),sQuery(id+"F0.wireOp",EDGE,"E13.rect.left"),sQuery(id+"F0.wireOp",EDGE,"E13.rect.right"),sQuery(id+"F0.wireOp",EDGE,"E14.left"),sQuery(id+"F0.wireOp",EDGE,"E14.right"),sQuery(id+"F0.wireOp",EDGE,"E15"),sQuery(id+"F0.wireOp",EDGE,"E17"),sQuery(id+"F0.wireOp",EDGE,"E18"),sQuery(id+"F0.wireOp",EDGE,"E20"),sQuery(id+"F0.wireOp",EDGE,"E21.rect.bottom"),sQuery(id+"F0.wireOp",EDGE,"E21.rect.top"),sQuery(id+"F0.wireOp",EDGE,"E22.left"),sQuery(id+"F0.wireOp",EDGE,"E22.right"),sQuery(id+"F0.wireOp",EDGE,"E23.top"),sQuery(id+"F0.wireOp",EDGE,"E23.left"),sQuery(id+"F0.wireOp",EDGE,"E23.right"),sQuery(id+"F0.wireOp",EDGE,"E22.top"),sQuery(id+"F0.wireOp",EDGE,"E26"),sQuery(id+"F0.wireOp",EDGE,"E29"),sQuery(id+"F0.wireOp",EDGE,"E32"),sQuery(id+"F0.wireOp",EDGE,"E35"),sQuery(id+"F0.wireOp",EDGE,"E36"),sQuery(id+"F0.wireOp",EDGE,"E41"),sQuery(id+"F0.wireOp",EDGE,"E44"),sQuery(id+"F0.wireOp",EDGE,"E47"),sQuery(id+"F0.wireOp",EDGE,"E48"),subQ0,sQuery(id+"F0.wireOp",EDGE,"E50"),sQuery(id+"F0.wireOp",EDGE,"E51")])],"isStart":true})]});}
            var Q76;
            Q76=makeQuery(id+"F1.opExtrude","CAP_EDGE",EDGE,{"disambiguationData":[OSD([sQuery(id+"F0.wireOp",EDGE,"E49")])],"isStart":true});
            var Q77;
            {var subQ0=sQuery(id+"F0.wireOp",EDGE,"E49");var subQ1=sQuery(id+"F0.wireOp",EDGE,"E5");Q77=makeQuery(id+"F3.opFillet","BLEND_EDGE",EDGE,{"blendedFrom":[makeQuery(id+"F1.opExtrude","SWEPT_EDGE",EDGE,{"disambiguationData":[OSD([subQ1,subQ0])]}),makeQuery(id+"F1.opExtrude","CAP_FACE",FACE,{"disambiguationData":[OSD([sQuery(id+"F0.wireOp",EDGE,"E0"),sQuery(id+"F0.wireOp",EDGE,"E1"),sQuery(id+"F0.wireOp",EDGE,"E2"),sQuery(id+"F0.wireOp",EDGE,"E3"),sQuery(id+"F0.wireOp",EDGE,"E4"),subQ1,sQuery(id+"F0.wireOp",EDGE,"E6"),sQuery(id+"F0.wireOp",EDGE,"E7"),sQuery(id+"F0.wireOp",EDGE,"E9.rect.left"),sQuery(id+"F0.wireOp",EDGE,"E9.rect.right"),sQuery(id+"F0.wireOp",EDGE,"E10.rect.bottom"),sQuery(id+"F0.wireOp",EDGE,"E10.rect.top"),sQuery(id+"F0.wireOp",EDGE,"E11.rect.bottom"),sQuery(id+"F0.wireOp",EDGE,"E11.rect.top"),sQuery(id+"F0.wireOp",EDGE,"E12.rect.left"),sQuery(id+"F0.wireOp",EDGE,"E12.rect.right"),sQuery(id+"F0.wireOp",EDGE,"E13.rect.left"),sQuery(id+"F0.wireOp",EDGE,"E13.rect.right"),sQuery(id+"F0.wireOp",EDGE,"E14.left"),sQuery(id+"F0.wireOp",EDGE,"E14.right"),sQuery(id+"F0.wireOp",EDGE,"E15"),sQuery(id+"F0.wireOp",EDGE,"E17"),sQuery(id+"F0.wireOp",EDGE,"E18"),sQuery(id+"F0.wireOp",EDGE,"E20"),sQuery(id+"F0.wireOp",EDGE,"E21.rect.bottom"),sQuery(id+"F0.wireOp",EDGE,"E21.rect.top"),sQuery(id+"F0.wireOp",EDGE,"E22.left"),sQuery(id+"F0.wireOp",EDGE,"E22.right"),sQuery(id+"F0.wireOp",EDGE,"E23.top"),sQuery(id+"F0.wireOp",EDGE,"E23.left"),sQuery(id+"F0.wireOp",EDGE,"E23.right"),sQuery(id+"F0.wireOp",EDGE,"E22.top"),sQuery(id+"F0.wireOp",EDGE,"E26"),sQuery(id+"F0.wireOp",EDGE,"E29"),sQuery(id+"F0.wireOp",EDGE,"E32"),sQuery(id+"F0.wireOp",EDGE,"E35"),sQuery(id+"F0.wireOp",EDGE,"E36"),sQuery(id+"F0.wireOp",EDGE,"E41"),sQuery(id+"F0.wireOp",EDGE,"E44"),sQuery(id+"F0.wireOp",EDGE,"E47"),sQuery(id+"F0.wireOp",EDGE,"E48"),subQ0,sQuery(id+"F0.wireOp",EDGE,"E50"),sQuery(id+"F0.wireOp",EDGE,"E51")])],"isStart":true})],"blendedInto":[makeQuery(id+"F1.opExtrude","CAP_FACE",FACE,{"disambiguationData":[OSD([sQuery(id+"F0.wireOp",EDGE,"E0"),sQuery(id+"F0.wireOp",EDGE,"E1"),sQuery(id+"F0.wireOp",EDGE,"E2"),sQuery(id+"F0.wireOp",EDGE,"E3"),sQuery(id+"F0.wireOp",EDGE,"E4"),subQ1,sQuery(id+"F0.wireOp",EDGE,"E6"),sQuery(id+"F0.wireOp",EDGE,"E7"),sQuery(id+"F0.wireOp",EDGE,"E9.rect.left"),sQuery(id+"F0.wireOp",EDGE,"E9.rect.right"),sQuery(id+"F0.wireOp",EDGE,"E10.rect.bottom"),sQuery(id+"F0.wireOp",EDGE,"E10.rect.top"),sQuery(id+"F0.wireOp",EDGE,"E11.rect.bottom"),sQuery(id+"F0.wireOp",EDGE,"E11.rect.top"),sQuery(id+"F0.wireOp",EDGE,"E12.rect.left"),sQuery(id+"F0.wireOp",EDGE,"E12.rect.right"),sQuery(id+"F0.wireOp",EDGE,"E13.rect.left"),sQuery(id+"F0.wireOp",EDGE,"E13.rect.right"),sQuery(id+"F0.wireOp",EDGE,"E14.left"),sQuery(id+"F0.wireOp",EDGE,"E14.right"),sQuery(id+"F0.wireOp",EDGE,"E15"),sQuery(id+"F0.wireOp",EDGE,"E17"),sQuery(id+"F0.wireOp",EDGE,"E18"),sQuery(id+"F0.wireOp",EDGE,"E20"),sQuery(id+"F0.wireOp",EDGE,"E21.rect.bottom"),sQuery(id+"F0.wireOp",EDGE,"E21.rect.top"),sQuery(id+"F0.wireOp",EDGE,"E22.left"),sQuery(id+"F0.wireOp",EDGE,"E22.right"),sQuery(id+"F0.wireOp",EDGE,"E23.top"),sQuery(id+"F0.wireOp",EDGE,"E23.left"),sQuery(id+"F0.wireOp",EDGE,"E23.right"),sQuery(id+"F0.wireOp",EDGE,"E22.top"),sQuery(id+"F0.wireOp",EDGE,"E26"),sQuery(id+"F0.wireOp",EDGE,"E29"),sQuery(id+"F0.wireOp",EDGE,"E32"),sQuery(id+"F0.wireOp",EDGE,"E35"),sQuery(id+"F0.wireOp",EDGE,"E36"),sQuery(id+"F0.wireOp",EDGE,"E41"),sQuery(id+"F0.wireOp",EDGE,"E44"),sQuery(id+"F0.wireOp",EDGE,"E47"),sQuery(id+"F0.wireOp",EDGE,"E48"),subQ0,sQuery(id+"F0.wireOp",EDGE,"E50"),sQuery(id+"F0.wireOp",EDGE,"E51")])],"isStart":true})]});}
            var Q78;
            {var subQ0=sQuery(id+"F0.wireOp",EDGE,"E10.rect.bottom");Q78=makeQuery(id+"F1.opExtrude","CAP_EDGE",EDGE,{"disambiguationData":[OSD([subQ0]),TDD([makeQuery(id+"F0.imprint","IMPRINT",EDGE,{"disambiguationData":[TD([[makeQuery(id+"F0.imprint","INTERSECT",VERTEX,{"derivedFrom":[subQ0,sQuery(id+"F0.wireOp",EDGE,"E12.rect.left"),sQuery(id+"F0.wireOp",EDGE,"E44")]}),-1.0]])],"derivedFrom":subQ0})])],"isStart":true});}
            var Q79;
            {var subQ0=sQuery(id+"F0.wireOp",EDGE,"E44");var subQ1=sQuery(id+"F0.wireOp",EDGE,"E12.rect.left");var subQ2=sQuery(id+"F0.wireOp",EDGE,"E10.rect.bottom");Q79=makeQuery(id+"F4.opFillet","BLEND_EDGE",EDGE,{"blendedFrom":[makeQuery(id+"F1.opExtrude","SWEPT_EDGE",EDGE,{"disambiguationData":[OSD([subQ2,subQ1,subQ0])]}),makeQuery(id+"F1.opExtrude","CAP_FACE",FACE,{"disambiguationData":[OSD([sQuery(id+"F0.wireOp",EDGE,"E0"),sQuery(id+"F0.wireOp",EDGE,"E1"),sQuery(id+"F0.wireOp",EDGE,"E2"),sQuery(id+"F0.wireOp",EDGE,"E3"),sQuery(id+"F0.wireOp",EDGE,"E4"),sQuery(id+"F0.wireOp",EDGE,"E5"),sQuery(id+"F0.wireOp",EDGE,"E6"),sQuery(id+"F0.wireOp",EDGE,"E7"),sQuery(id+"F0.wireOp",EDGE,"E9.rect.left"),sQuery(id+"F0.wireOp",EDGE,"E9.rect.right"),subQ2,sQuery(id+"F0.wireOp",EDGE,"E10.rect.top"),sQuery(id+"F0.wireOp",EDGE,"E11.rect.bottom"),sQuery(id+"F0.wireOp",EDGE,"E11.rect.top"),subQ1,sQuery(id+"F0.wireOp",EDGE,"E12.rect.right"),sQuery(id+"F0.wireOp",EDGE,"E13.rect.left"),sQuery(id+"F0.wireOp",EDGE,"E13.rect.right"),sQuery(id+"F0.wireOp",EDGE,"E14.left"),sQuery(id+"F0.wireOp",EDGE,"E14.right"),sQuery(id+"F0.wireOp",EDGE,"E15"),sQuery(id+"F0.wireOp",EDGE,"E17"),sQuery(id+"F0.wireOp",EDGE,"E18"),sQuery(id+"F0.wireOp",EDGE,"E20"),sQuery(id+"F0.wireOp",EDGE,"E21.rect.bottom"),sQuery(id+"F0.wireOp",EDGE,"E21.rect.top"),sQuery(id+"F0.wireOp",EDGE,"E22.left"),sQuery(id+"F0.wireOp",EDGE,"E22.right"),sQuery(id+"F0.wireOp",EDGE,"E23.top"),sQuery(id+"F0.wireOp",EDGE,"E23.left"),sQuery(id+"F0.wireOp",EDGE,"E23.right"),sQuery(id+"F0.wireOp",EDGE,"E22.top"),sQuery(id+"F0.wireOp",EDGE,"E26"),sQuery(id+"F0.wireOp",EDGE,"E29"),sQuery(id+"F0.wireOp",EDGE,"E32"),sQuery(id+"F0.wireOp",EDGE,"E35"),sQuery(id+"F0.wireOp",EDGE,"E36"),sQuery(id+"F0.wireOp",EDGE,"E41"),subQ0,sQuery(id+"F0.wireOp",EDGE,"E47"),sQuery(id+"F0.wireOp",EDGE,"E48"),sQuery(id+"F0.wireOp",EDGE,"E49"),sQuery(id+"F0.wireOp",EDGE,"E50"),sQuery(id+"F0.wireOp",EDGE,"E51")])],"isStart":true})],"blendedInto":[makeQuery(id+"F1.opExtrude","CAP_FACE",FACE,{"disambiguationData":[OSD([sQuery(id+"F0.wireOp",EDGE,"E0"),sQuery(id+"F0.wireOp",EDGE,"E1"),sQuery(id+"F0.wireOp",EDGE,"E2"),sQuery(id+"F0.wireOp",EDGE,"E3"),sQuery(id+"F0.wireOp",EDGE,"E4"),sQuery(id+"F0.wireOp",EDGE,"E5"),sQuery(id+"F0.wireOp",EDGE,"E6"),sQuery(id+"F0.wireOp",EDGE,"E7"),sQuery(id+"F0.wireOp",EDGE,"E9.rect.left"),sQuery(id+"F0.wireOp",EDGE,"E9.rect.right"),subQ2,sQuery(id+"F0.wireOp",EDGE,"E10.rect.top"),sQuery(id+"F0.wireOp",EDGE,"E11.rect.bottom"),sQuery(id+"F0.wireOp",EDGE,"E11.rect.top"),subQ1,sQuery(id+"F0.wireOp",EDGE,"E12.rect.right"),sQuery(id+"F0.wireOp",EDGE,"E13.rect.left"),sQuery(id+"F0.wireOp",EDGE,"E13.rect.right"),sQuery(id+"F0.wireOp",EDGE,"E14.left"),sQuery(id+"F0.wireOp",EDGE,"E14.right"),sQuery(id+"F0.wireOp",EDGE,"E15"),sQuery(id+"F0.wireOp",EDGE,"E17"),sQuery(id+"F0.wireOp",EDGE,"E18"),sQuery(id+"F0.wireOp",EDGE,"E20"),sQuery(id+"F0.wireOp",EDGE,"E21.rect.bottom"),sQuery(id+"F0.wireOp",EDGE,"E21.rect.top"),sQuery(id+"F0.wireOp",EDGE,"E22.left"),sQuery(id+"F0.wireOp",EDGE,"E22.right"),sQuery(id+"F0.wireOp",EDGE,"E23.top"),sQuery(id+"F0.wireOp",EDGE,"E23.left"),sQuery(id+"F0.wireOp",EDGE,"E23.right"),sQuery(id+"F0.wireOp",EDGE,"E22.top"),sQuery(id+"F0.wireOp",EDGE,"E26"),sQuery(id+"F0.wireOp",EDGE,"E29"),sQuery(id+"F0.wireOp",EDGE,"E32"),sQuery(id+"F0.wireOp",EDGE,"E35"),sQuery(id+"F0.wireOp",EDGE,"E36"),sQuery(id+"F0.wireOp",EDGE,"E41"),subQ0,sQuery(id+"F0.wireOp",EDGE,"E47"),sQuery(id+"F0.wireOp",EDGE,"E48"),sQuery(id+"F0.wireOp",EDGE,"E49"),sQuery(id+"F0.wireOp",EDGE,"E50"),sQuery(id+"F0.wireOp",EDGE,"E51")])],"isStart":true})]});}
            var Q80;
            {var subQ0=sQuery(id+"F0.wireOp",EDGE,"E20");var subQ1=sQuery(id+"F0.wireOp",EDGE,"E10.rect.bottom");Q80=makeQuery(id+"F4.opFillet","BLEND_EDGE",EDGE,{"blendedFrom":[makeQuery(id+"F1.opExtrude","SWEPT_EDGE",EDGE,{"disambiguationData":[OSD([subQ1,sQuery(id+"F0.wireOp",EDGE,"E19"),subQ0])]}),makeQuery(id+"F1.opExtrude","CAP_FACE",FACE,{"disambiguationData":[OSD([sQuery(id+"F0.wireOp",EDGE,"E0"),sQuery(id+"F0.wireOp",EDGE,"E1"),sQuery(id+"F0.wireOp",EDGE,"E2"),sQuery(id+"F0.wireOp",EDGE,"E3"),sQuery(id+"F0.wireOp",EDGE,"E4"),sQuery(id+"F0.wireOp",EDGE,"E5"),sQuery(id+"F0.wireOp",EDGE,"E6"),sQuery(id+"F0.wireOp",EDGE,"E7"),sQuery(id+"F0.wireOp",EDGE,"E9.rect.left"),sQuery(id+"F0.wireOp",EDGE,"E9.rect.right"),subQ1,sQuery(id+"F0.wireOp",EDGE,"E10.rect.top"),sQuery(id+"F0.wireOp",EDGE,"E11.rect.bottom"),sQuery(id+"F0.wireOp",EDGE,"E11.rect.top"),sQuery(id+"F0.wireOp",EDGE,"E12.rect.left"),sQuery(id+"F0.wireOp",EDGE,"E12.rect.right"),sQuery(id+"F0.wireOp",EDGE,"E13.rect.left"),sQuery(id+"F0.wireOp",EDGE,"E13.rect.right"),sQuery(id+"F0.wireOp",EDGE,"E14.left"),sQuery(id+"F0.wireOp",EDGE,"E14.right"),sQuery(id+"F0.wireOp",EDGE,"E15"),sQuery(id+"F0.wireOp",EDGE,"E17"),sQuery(id+"F0.wireOp",EDGE,"E18"),subQ0,sQuery(id+"F0.wireOp",EDGE,"E21.rect.bottom"),sQuery(id+"F0.wireOp",EDGE,"E21.rect.top"),sQuery(id+"F0.wireOp",EDGE,"E22.left"),sQuery(id+"F0.wireOp",EDGE,"E22.right"),sQuery(id+"F0.wireOp",EDGE,"E23.top"),sQuery(id+"F0.wireOp",EDGE,"E23.left"),sQuery(id+"F0.wireOp",EDGE,"E23.right"),sQuery(id+"F0.wireOp",EDGE,"E22.top"),sQuery(id+"F0.wireOp",EDGE,"E26"),sQuery(id+"F0.wireOp",EDGE,"E29"),sQuery(id+"F0.wireOp",EDGE,"E32"),sQuery(id+"F0.wireOp",EDGE,"E35"),sQuery(id+"F0.wireOp",EDGE,"E36"),sQuery(id+"F0.wireOp",EDGE,"E41"),sQuery(id+"F0.wireOp",EDGE,"E44"),sQuery(id+"F0.wireOp",EDGE,"E47"),sQuery(id+"F0.wireOp",EDGE,"E48"),sQuery(id+"F0.wireOp",EDGE,"E49"),sQuery(id+"F0.wireOp",EDGE,"E50"),sQuery(id+"F0.wireOp",EDGE,"E51")])],"isStart":true})],"blendedInto":[makeQuery(id+"F1.opExtrude","CAP_FACE",FACE,{"disambiguationData":[OSD([sQuery(id+"F0.wireOp",EDGE,"E0"),sQuery(id+"F0.wireOp",EDGE,"E1"),sQuery(id+"F0.wireOp",EDGE,"E2"),sQuery(id+"F0.wireOp",EDGE,"E3"),sQuery(id+"F0.wireOp",EDGE,"E4"),sQuery(id+"F0.wireOp",EDGE,"E5"),sQuery(id+"F0.wireOp",EDGE,"E6"),sQuery(id+"F0.wireOp",EDGE,"E7"),sQuery(id+"F0.wireOp",EDGE,"E9.rect.left"),sQuery(id+"F0.wireOp",EDGE,"E9.rect.right"),subQ1,sQuery(id+"F0.wireOp",EDGE,"E10.rect.top"),sQuery(id+"F0.wireOp",EDGE,"E11.rect.bottom"),sQuery(id+"F0.wireOp",EDGE,"E11.rect.top"),sQuery(id+"F0.wireOp",EDGE,"E12.rect.left"),sQuery(id+"F0.wireOp",EDGE,"E12.rect.right"),sQuery(id+"F0.wireOp",EDGE,"E13.rect.left"),sQuery(id+"F0.wireOp",EDGE,"E13.rect.right"),sQuery(id+"F0.wireOp",EDGE,"E14.left"),sQuery(id+"F0.wireOp",EDGE,"E14.right"),sQuery(id+"F0.wireOp",EDGE,"E15"),sQuery(id+"F0.wireOp",EDGE,"E17"),sQuery(id+"F0.wireOp",EDGE,"E18"),subQ0,sQuery(id+"F0.wireOp",EDGE,"E21.rect.bottom"),sQuery(id+"F0.wireOp",EDGE,"E21.rect.top"),sQuery(id+"F0.wireOp",EDGE,"E22.left"),sQuery(id+"F0.wireOp",EDGE,"E22.right"),sQuery(id+"F0.wireOp",EDGE,"E23.top"),sQuery(id+"F0.wireOp",EDGE,"E23.left"),sQuery(id+"F0.wireOp",EDGE,"E23.right"),sQuery(id+"F0.wireOp",EDGE,"E22.top"),sQuery(id+"F0.wireOp",EDGE,"E26"),sQuery(id+"F0.wireOp",EDGE,"E29"),sQuery(id+"F0.wireOp",EDGE,"E32"),sQuery(id+"F0.wireOp",EDGE,"E35"),sQuery(id+"F0.wireOp",EDGE,"E36"),sQuery(id+"F0.wireOp",EDGE,"E41"),sQuery(id+"F0.wireOp",EDGE,"E44"),sQuery(id+"F0.wireOp",EDGE,"E47"),sQuery(id+"F0.wireOp",EDGE,"E48"),sQuery(id+"F0.wireOp",EDGE,"E49"),sQuery(id+"F0.wireOp",EDGE,"E50"),sQuery(id+"F0.wireOp",EDGE,"E51")])],"isStart":true})]});}
            var Q81;
            Q81=makeQuery(id+"F1.opExtrude","CAP_EDGE",EDGE,{"disambiguationData":[OSD([sQuery(id+"F0.wireOp",EDGE,"E13.rect.left"),sQuery(id+"F0.wireOp",EDGE,"E20"),sQuery(id+"F0.wireOp",EDGE,"E23.right")])],"isStart":true});
            var Q82;
            Q82=makeQuery(id+"F1.opExtrude","CAP_EDGE",EDGE,{"disambiguationData":[OSD([sQuery(id+"F0.wireOp",EDGE,"E5")])],"isStart":true});
            var Q83;
            Q83=makeQuery(id+"F1.opExtrude","CAP_EDGE",EDGE,{"disambiguationData":[OSD([sQuery(id+"F0.wireOp",EDGE,"E1")])],"isStart":true});
            var Q84;
            {var subQ0=sQuery(id+"F0.wireOp",EDGE,"E29");var subQ1=sQuery(id+"F0.wireOp",EDGE,"E1");Q84=makeQuery(id+"F2.opFillet","BLEND_EDGE",EDGE,{"blendedFrom":[makeQuery(id+"F1.opExtrude","SWEPT_EDGE",EDGE,{"disambiguationData":[OSD([subQ1,subQ0])]}),makeQuery(id+"F1.opExtrude","CAP_FACE",FACE,{"disambiguationData":[OSD([sQuery(id+"F0.wireOp",EDGE,"E0"),subQ1,sQuery(id+"F0.wireOp",EDGE,"E2"),sQuery(id+"F0.wireOp",EDGE,"E3"),sQuery(id+"F0.wireOp",EDGE,"E4"),sQuery(id+"F0.wireOp",EDGE,"E5"),sQuery(id+"F0.wireOp",EDGE,"E6"),sQuery(id+"F0.wireOp",EDGE,"E7"),sQuery(id+"F0.wireOp",EDGE,"E9.rect.left"),sQuery(id+"F0.wireOp",EDGE,"E9.rect.right"),sQuery(id+"F0.wireOp",EDGE,"E10.rect.bottom"),sQuery(id+"F0.wireOp",EDGE,"E10.rect.top"),sQuery(id+"F0.wireOp",EDGE,"E11.rect.bottom"),sQuery(id+"F0.wireOp",EDGE,"E11.rect.top"),sQuery(id+"F0.wireOp",EDGE,"E12.rect.left"),sQuery(id+"F0.wireOp",EDGE,"E12.rect.right"),sQuery(id+"F0.wireOp",EDGE,"E13.rect.left"),sQuery(id+"F0.wireOp",EDGE,"E13.rect.right"),sQuery(id+"F0.wireOp",EDGE,"E14.left"),sQuery(id+"F0.wireOp",EDGE,"E14.right"),sQuery(id+"F0.wireOp",EDGE,"E15"),sQuery(id+"F0.wireOp",EDGE,"E17"),sQuery(id+"F0.wireOp",EDGE,"E18"),sQuery(id+"F0.wireOp",EDGE,"E20"),sQuery(id+"F0.wireOp",EDGE,"E21.rect.bottom"),sQuery(id+"F0.wireOp",EDGE,"E21.rect.top"),sQuery(id+"F0.wireOp",EDGE,"E22.left"),sQuery(id+"F0.wireOp",EDGE,"E22.right"),sQuery(id+"F0.wireOp",EDGE,"E23.top"),sQuery(id+"F0.wireOp",EDGE,"E23.left"),sQuery(id+"F0.wireOp",EDGE,"E23.right"),sQuery(id+"F0.wireOp",EDGE,"E22.top"),sQuery(id+"F0.wireOp",EDGE,"E26"),subQ0,sQuery(id+"F0.wireOp",EDGE,"E32"),sQuery(id+"F0.wireOp",EDGE,"E35"),sQuery(id+"F0.wireOp",EDGE,"E36"),sQuery(id+"F0.wireOp",EDGE,"E41"),sQuery(id+"F0.wireOp",EDGE,"E44"),sQuery(id+"F0.wireOp",EDGE,"E47"),sQuery(id+"F0.wireOp",EDGE,"E48"),sQuery(id+"F0.wireOp",EDGE,"E49"),sQuery(id+"F0.wireOp",EDGE,"E50"),sQuery(id+"F0.wireOp",EDGE,"E51")])],"isStart":true})],"blendedInto":[makeQuery(id+"F1.opExtrude","CAP_FACE",FACE,{"disambiguationData":[OSD([sQuery(id+"F0.wireOp",EDGE,"E0"),subQ1,sQuery(id+"F0.wireOp",EDGE,"E2"),sQuery(id+"F0.wireOp",EDGE,"E3"),sQuery(id+"F0.wireOp",EDGE,"E4"),sQuery(id+"F0.wireOp",EDGE,"E5"),sQuery(id+"F0.wireOp",EDGE,"E6"),sQuery(id+"F0.wireOp",EDGE,"E7"),sQuery(id+"F0.wireOp",EDGE,"E9.rect.left"),sQuery(id+"F0.wireOp",EDGE,"E9.rect.right"),sQuery(id+"F0.wireOp",EDGE,"E10.rect.bottom"),sQuery(id+"F0.wireOp",EDGE,"E10.rect.top"),sQuery(id+"F0.wireOp",EDGE,"E11.rect.bottom"),sQuery(id+"F0.wireOp",EDGE,"E11.rect.top"),sQuery(id+"F0.wireOp",EDGE,"E12.rect.left"),sQuery(id+"F0.wireOp",EDGE,"E12.rect.right"),sQuery(id+"F0.wireOp",EDGE,"E13.rect.left"),sQuery(id+"F0.wireOp",EDGE,"E13.rect.right"),sQuery(id+"F0.wireOp",EDGE,"E14.left"),sQuery(id+"F0.wireOp",EDGE,"E14.right"),sQuery(id+"F0.wireOp",EDGE,"E15"),sQuery(id+"F0.wireOp",EDGE,"E17"),sQuery(id+"F0.wireOp",EDGE,"E18"),sQuery(id+"F0.wireOp",EDGE,"E20"),sQuery(id+"F0.wireOp",EDGE,"E21.rect.bottom"),sQuery(id+"F0.wireOp",EDGE,"E21.rect.top"),sQuery(id+"F0.wireOp",EDGE,"E22.left"),sQuery(id+"F0.wireOp",EDGE,"E22.right"),sQuery(id+"F0.wireOp",EDGE,"E23.top"),sQuery(id+"F0.wireOp",EDGE,"E23.left"),sQuery(id+"F0.wireOp",EDGE,"E23.right"),sQuery(id+"F0.wireOp",EDGE,"E22.top"),sQuery(id+"F0.wireOp",EDGE,"E26"),subQ0,sQuery(id+"F0.wireOp",EDGE,"E32"),sQuery(id+"F0.wireOp",EDGE,"E35"),sQuery(id+"F0.wireOp",EDGE,"E36"),sQuery(id+"F0.wireOp",EDGE,"E41"),sQuery(id+"F0.wireOp",EDGE,"E44"),sQuery(id+"F0.wireOp",EDGE,"E47"),sQuery(id+"F0.wireOp",EDGE,"E48"),sQuery(id+"F0.wireOp",EDGE,"E49"),sQuery(id+"F0.wireOp",EDGE,"E50"),sQuery(id+"F0.wireOp",EDGE,"E51")])],"isStart":true})]});}
            var Q85;
            Q85=makeQuery(id+"F1.opExtrude","CAP_EDGE",EDGE,{"disambiguationData":[OSD([sQuery(id+"F0.wireOp",EDGE,"E44")])],"isStart":true});
            var Q86;
            {var subQ0=sQuery(id+"F0.wireOp",EDGE,"E44");var subQ1=sQuery(id+"F0.wireOp",EDGE,"E9.rect.left");Q86=makeQuery(id+"F3.opFillet","BLEND_EDGE",EDGE,{"blendedFrom":[makeQuery(id+"F1.opExtrude","SWEPT_EDGE",EDGE,{"disambiguationData":[OSD([subQ1,subQ0])]}),makeQuery(id+"F1.opExtrude","CAP_FACE",FACE,{"disambiguationData":[OSD([sQuery(id+"F0.wireOp",EDGE,"E0"),sQuery(id+"F0.wireOp",EDGE,"E1"),sQuery(id+"F0.wireOp",EDGE,"E2"),sQuery(id+"F0.wireOp",EDGE,"E3"),sQuery(id+"F0.wireOp",EDGE,"E4"),sQuery(id+"F0.wireOp",EDGE,"E5"),sQuery(id+"F0.wireOp",EDGE,"E6"),sQuery(id+"F0.wireOp",EDGE,"E7"),subQ1,sQuery(id+"F0.wireOp",EDGE,"E9.rect.right"),sQuery(id+"F0.wireOp",EDGE,"E10.rect.bottom"),sQuery(id+"F0.wireOp",EDGE,"E10.rect.top"),sQuery(id+"F0.wireOp",EDGE,"E11.rect.bottom"),sQuery(id+"F0.wireOp",EDGE,"E11.rect.top"),sQuery(id+"F0.wireOp",EDGE,"E12.rect.left"),sQuery(id+"F0.wireOp",EDGE,"E12.rect.right"),sQuery(id+"F0.wireOp",EDGE,"E13.rect.left"),sQuery(id+"F0.wireOp",EDGE,"E13.rect.right"),sQuery(id+"F0.wireOp",EDGE,"E14.left"),sQuery(id+"F0.wireOp",EDGE,"E14.right"),sQuery(id+"F0.wireOp",EDGE,"E15"),sQuery(id+"F0.wireOp",EDGE,"E17"),sQuery(id+"F0.wireOp",EDGE,"E18"),sQuery(id+"F0.wireOp",EDGE,"E20"),sQuery(id+"F0.wireOp",EDGE,"E21.rect.bottom"),sQuery(id+"F0.wireOp",EDGE,"E21.rect.top"),sQuery(id+"F0.wireOp",EDGE,"E22.left"),sQuery(id+"F0.wireOp",EDGE,"E22.right"),sQuery(id+"F0.wireOp",EDGE,"E23.top"),sQuery(id+"F0.wireOp",EDGE,"E23.left"),sQuery(id+"F0.wireOp",EDGE,"E23.right"),sQuery(id+"F0.wireOp",EDGE,"E22.top"),sQuery(id+"F0.wireOp",EDGE,"E26"),sQuery(id+"F0.wireOp",EDGE,"E29"),sQuery(id+"F0.wireOp",EDGE,"E32"),sQuery(id+"F0.wireOp",EDGE,"E35"),sQuery(id+"F0.wireOp",EDGE,"E36"),sQuery(id+"F0.wireOp",EDGE,"E41"),subQ0,sQuery(id+"F0.wireOp",EDGE,"E47"),sQuery(id+"F0.wireOp",EDGE,"E48"),sQuery(id+"F0.wireOp",EDGE,"E49"),sQuery(id+"F0.wireOp",EDGE,"E50"),sQuery(id+"F0.wireOp",EDGE,"E51")])],"isStart":true})],"blendedInto":[makeQuery(id+"F1.opExtrude","CAP_FACE",FACE,{"disambiguationData":[OSD([sQuery(id+"F0.wireOp",EDGE,"E0"),sQuery(id+"F0.wireOp",EDGE,"E1"),sQuery(id+"F0.wireOp",EDGE,"E2"),sQuery(id+"F0.wireOp",EDGE,"E3"),sQuery(id+"F0.wireOp",EDGE,"E4"),sQuery(id+"F0.wireOp",EDGE,"E5"),sQuery(id+"F0.wireOp",EDGE,"E6"),sQuery(id+"F0.wireOp",EDGE,"E7"),subQ1,sQuery(id+"F0.wireOp",EDGE,"E9.rect.right"),sQuery(id+"F0.wireOp",EDGE,"E10.rect.bottom"),sQuery(id+"F0.wireOp",EDGE,"E10.rect.top"),sQuery(id+"F0.wireOp",EDGE,"E11.rect.bottom"),sQuery(id+"F0.wireOp",EDGE,"E11.rect.top"),sQuery(id+"F0.wireOp",EDGE,"E12.rect.left"),sQuery(id+"F0.wireOp",EDGE,"E12.rect.right"),sQuery(id+"F0.wireOp",EDGE,"E13.rect.left"),sQuery(id+"F0.wireOp",EDGE,"E13.rect.right"),sQuery(id+"F0.wireOp",EDGE,"E14.left"),sQuery(id+"F0.wireOp",EDGE,"E14.right"),sQuery(id+"F0.wireOp",EDGE,"E15"),sQuery(id+"F0.wireOp",EDGE,"E17"),sQuery(id+"F0.wireOp",EDGE,"E18"),sQuery(id+"F0.wireOp",EDGE,"E20"),sQuery(id+"F0.wireOp",EDGE,"E21.rect.bottom"),sQuery(id+"F0.wireOp",EDGE,"E21.rect.top"),sQuery(id+"F0.wireOp",EDGE,"E22.left"),sQuery(id+"F0.wireOp",EDGE,"E22.right"),sQuery(id+"F0.wireOp",EDGE,"E23.top"),sQuery(id+"F0.wireOp",EDGE,"E23.left"),sQuery(id+"F0.wireOp",EDGE,"E23.right"),sQuery(id+"F0.wireOp",EDGE,"E22.top"),sQuery(id+"F0.wireOp",EDGE,"E26"),sQuery(id+"F0.wireOp",EDGE,"E29"),sQuery(id+"F0.wireOp",EDGE,"E32"),sQuery(id+"F0.wireOp",EDGE,"E35"),sQuery(id+"F0.wireOp",EDGE,"E36"),sQuery(id+"F0.wireOp",EDGE,"E41"),subQ0,sQuery(id+"F0.wireOp",EDGE,"E47"),sQuery(id+"F0.wireOp",EDGE,"E48"),sQuery(id+"F0.wireOp",EDGE,"E49"),sQuery(id+"F0.wireOp",EDGE,"E50"),sQuery(id+"F0.wireOp",EDGE,"E51")])],"isStart":true})]});}
            var Q87;
            {var subQ0=sQuery(id+"F0.wireOp",EDGE,"E10.rect.bottom");Q87=makeQuery(id+"F1.opExtrude","CAP_EDGE",EDGE,{"disambiguationData":[OSD([subQ0]),TDD([makeQuery(id+"F0.imprint","IMPRINT",EDGE,{"disambiguationData":[TD([[makeQuery(id+"F0.imprint","INTERSECT",VERTEX,{"derivedFrom":[subQ0,sQuery(id+"F0.wireOp",EDGE,"E16"),sQuery(id+"F0.wireOp",EDGE,"E17")]}),1.0]])],"derivedFrom":subQ0})])],"isStart":true});}
            var Q88;
            {var subQ0=sQuery(id+"F0.wireOp",EDGE,"E18");var subQ1=sQuery(id+"F0.wireOp",EDGE,"E10.rect.bottom");Q88=makeQuery(id+"F4.opFillet","BLEND_EDGE",EDGE,{"blendedFrom":[makeQuery(id+"F1.opExtrude","SWEPT_EDGE",EDGE,{"disambiguationData":[OSD([subQ1,subQ0,sQuery(id+"F0.wireOp",EDGE,"E19")])]}),makeQuery(id+"F1.opExtrude","CAP_FACE",FACE,{"disambiguationData":[OSD([sQuery(id+"F0.wireOp",EDGE,"E0"),sQuery(id+"F0.wireOp",EDGE,"E1"),sQuery(id+"F0.wireOp",EDGE,"E2"),sQuery(id+"F0.wireOp",EDGE,"E3"),sQuery(id+"F0.wireOp",EDGE,"E4"),sQuery(id+"F0.wireOp",EDGE,"E5"),sQuery(id+"F0.wireOp",EDGE,"E6"),sQuery(id+"F0.wireOp",EDGE,"E7"),sQuery(id+"F0.wireOp",EDGE,"E9.rect.left"),sQuery(id+"F0.wireOp",EDGE,"E9.rect.right"),subQ1,sQuery(id+"F0.wireOp",EDGE,"E10.rect.top"),sQuery(id+"F0.wireOp",EDGE,"E11.rect.bottom"),sQuery(id+"F0.wireOp",EDGE,"E11.rect.top"),sQuery(id+"F0.wireOp",EDGE,"E12.rect.left"),sQuery(id+"F0.wireOp",EDGE,"E12.rect.right"),sQuery(id+"F0.wireOp",EDGE,"E13.rect.left"),sQuery(id+"F0.wireOp",EDGE,"E13.rect.right"),sQuery(id+"F0.wireOp",EDGE,"E14.left"),sQuery(id+"F0.wireOp",EDGE,"E14.right"),sQuery(id+"F0.wireOp",EDGE,"E15"),sQuery(id+"F0.wireOp",EDGE,"E17"),subQ0,sQuery(id+"F0.wireOp",EDGE,"E20"),sQuery(id+"F0.wireOp",EDGE,"E21.rect.bottom"),sQuery(id+"F0.wireOp",EDGE,"E21.rect.top"),sQuery(id+"F0.wireOp",EDGE,"E22.left"),sQuery(id+"F0.wireOp",EDGE,"E22.right"),sQuery(id+"F0.wireOp",EDGE,"E23.top"),sQuery(id+"F0.wireOp",EDGE,"E23.left"),sQuery(id+"F0.wireOp",EDGE,"E23.right"),sQuery(id+"F0.wireOp",EDGE,"E22.top"),sQuery(id+"F0.wireOp",EDGE,"E26"),sQuery(id+"F0.wireOp",EDGE,"E29"),sQuery(id+"F0.wireOp",EDGE,"E32"),sQuery(id+"F0.wireOp",EDGE,"E35"),sQuery(id+"F0.wireOp",EDGE,"E36"),sQuery(id+"F0.wireOp",EDGE,"E41"),sQuery(id+"F0.wireOp",EDGE,"E44"),sQuery(id+"F0.wireOp",EDGE,"E47"),sQuery(id+"F0.wireOp",EDGE,"E48"),sQuery(id+"F0.wireOp",EDGE,"E49"),sQuery(id+"F0.wireOp",EDGE,"E50"),sQuery(id+"F0.wireOp",EDGE,"E51")])],"isStart":true})],"blendedInto":[makeQuery(id+"F1.opExtrude","CAP_FACE",FACE,{"disambiguationData":[OSD([sQuery(id+"F0.wireOp",EDGE,"E0"),sQuery(id+"F0.wireOp",EDGE,"E1"),sQuery(id+"F0.wireOp",EDGE,"E2"),sQuery(id+"F0.wireOp",EDGE,"E3"),sQuery(id+"F0.wireOp",EDGE,"E4"),sQuery(id+"F0.wireOp",EDGE,"E5"),sQuery(id+"F0.wireOp",EDGE,"E6"),sQuery(id+"F0.wireOp",EDGE,"E7"),sQuery(id+"F0.wireOp",EDGE,"E9.rect.left"),sQuery(id+"F0.wireOp",EDGE,"E9.rect.right"),subQ1,sQuery(id+"F0.wireOp",EDGE,"E10.rect.top"),sQuery(id+"F0.wireOp",EDGE,"E11.rect.bottom"),sQuery(id+"F0.wireOp",EDGE,"E11.rect.top"),sQuery(id+"F0.wireOp",EDGE,"E12.rect.left"),sQuery(id+"F0.wireOp",EDGE,"E12.rect.right"),sQuery(id+"F0.wireOp",EDGE,"E13.rect.left"),sQuery(id+"F0.wireOp",EDGE,"E13.rect.right"),sQuery(id+"F0.wireOp",EDGE,"E14.left"),sQuery(id+"F0.wireOp",EDGE,"E14.right"),sQuery(id+"F0.wireOp",EDGE,"E15"),sQuery(id+"F0.wireOp",EDGE,"E17"),subQ0,sQuery(id+"F0.wireOp",EDGE,"E20"),sQuery(id+"F0.wireOp",EDGE,"E21.rect.bottom"),sQuery(id+"F0.wireOp",EDGE,"E21.rect.top"),sQuery(id+"F0.wireOp",EDGE,"E22.left"),sQuery(id+"F0.wireOp",EDGE,"E22.right"),sQuery(id+"F0.wireOp",EDGE,"E23.top"),sQuery(id+"F0.wireOp",EDGE,"E23.left"),sQuery(id+"F0.wireOp",EDGE,"E23.right"),sQuery(id+"F0.wireOp",EDGE,"E22.top"),sQuery(id+"F0.wireOp",EDGE,"E26"),sQuery(id+"F0.wireOp",EDGE,"E29"),sQuery(id+"F0.wireOp",EDGE,"E32"),sQuery(id+"F0.wireOp",EDGE,"E35"),sQuery(id+"F0.wireOp",EDGE,"E36"),sQuery(id+"F0.wireOp",EDGE,"E41"),sQuery(id+"F0.wireOp",EDGE,"E44"),sQuery(id+"F0.wireOp",EDGE,"E47"),sQuery(id+"F0.wireOp",EDGE,"E48"),sQuery(id+"F0.wireOp",EDGE,"E49"),sQuery(id+"F0.wireOp",EDGE,"E50"),sQuery(id+"F0.wireOp",EDGE,"E51")])],"isStart":true})]});}
            var Q89;
            Q89=makeQuery(id+"F1.opExtrude","CAP_EDGE",EDGE,{"disambiguationData":[OSD([sQuery(id+"F0.wireOp",EDGE,"E14.right"),sQuery(id+"F0.wireOp",EDGE,"E18"),sQuery(id+"F0.wireOp",EDGE,"E23.left")])],"isStart":true});
            var Q90;
            Q90=makeQuery(id+"F1.opExtrude","CAP_EDGE",EDGE,{"disambiguationData":[OSD([sQuery(id+"F0.wireOp",EDGE,"E14.left"),sQuery(id+"F0.wireOp",EDGE,"E17"),sQuery(id+"F0.wireOp",EDGE,"E22.left")])],"isStart":true});
            var Q91;
            {var subQ0=sQuery(id+"F0.wireOp",EDGE,"E17");var subQ1=sQuery(id+"F0.wireOp",EDGE,"E10.rect.bottom");Q91=makeQuery(id+"F4.opFillet","BLEND_EDGE",EDGE,{"blendedFrom":[makeQuery(id+"F1.opExtrude","SWEPT_EDGE",EDGE,{"disambiguationData":[OSD([subQ1,sQuery(id+"F0.wireOp",EDGE,"E16"),subQ0])]}),makeQuery(id+"F1.opExtrude","CAP_FACE",FACE,{"disambiguationData":[OSD([sQuery(id+"F0.wireOp",EDGE,"E0"),sQuery(id+"F0.wireOp",EDGE,"E1"),sQuery(id+"F0.wireOp",EDGE,"E2"),sQuery(id+"F0.wireOp",EDGE,"E3"),sQuery(id+"F0.wireOp",EDGE,"E4"),sQuery(id+"F0.wireOp",EDGE,"E5"),sQuery(id+"F0.wireOp",EDGE,"E6"),sQuery(id+"F0.wireOp",EDGE,"E7"),sQuery(id+"F0.wireOp",EDGE,"E9.rect.left"),sQuery(id+"F0.wireOp",EDGE,"E9.rect.right"),subQ1,sQuery(id+"F0.wireOp",EDGE,"E10.rect.top"),sQuery(id+"F0.wireOp",EDGE,"E11.rect.bottom"),sQuery(id+"F0.wireOp",EDGE,"E11.rect.top"),sQuery(id+"F0.wireOp",EDGE,"E12.rect.left"),sQuery(id+"F0.wireOp",EDGE,"E12.rect.right"),sQuery(id+"F0.wireOp",EDGE,"E13.rect.left"),sQuery(id+"F0.wireOp",EDGE,"E13.rect.right"),sQuery(id+"F0.wireOp",EDGE,"E14.left"),sQuery(id+"F0.wireOp",EDGE,"E14.right"),sQuery(id+"F0.wireOp",EDGE,"E15"),subQ0,sQuery(id+"F0.wireOp",EDGE,"E18"),sQuery(id+"F0.wireOp",EDGE,"E20"),sQuery(id+"F0.wireOp",EDGE,"E21.rect.bottom"),sQuery(id+"F0.wireOp",EDGE,"E21.rect.top"),sQuery(id+"F0.wireOp",EDGE,"E22.left"),sQuery(id+"F0.wireOp",EDGE,"E22.right"),sQuery(id+"F0.wireOp",EDGE,"E23.top"),sQuery(id+"F0.wireOp",EDGE,"E23.left"),sQuery(id+"F0.wireOp",EDGE,"E23.right"),sQuery(id+"F0.wireOp",EDGE,"E22.top"),sQuery(id+"F0.wireOp",EDGE,"E26"),sQuery(id+"F0.wireOp",EDGE,"E29"),sQuery(id+"F0.wireOp",EDGE,"E32"),sQuery(id+"F0.wireOp",EDGE,"E35"),sQuery(id+"F0.wireOp",EDGE,"E36"),sQuery(id+"F0.wireOp",EDGE,"E41"),sQuery(id+"F0.wireOp",EDGE,"E44"),sQuery(id+"F0.wireOp",EDGE,"E47"),sQuery(id+"F0.wireOp",EDGE,"E48"),sQuery(id+"F0.wireOp",EDGE,"E49"),sQuery(id+"F0.wireOp",EDGE,"E50"),sQuery(id+"F0.wireOp",EDGE,"E51")])],"isStart":true})],"blendedInto":[makeQuery(id+"F1.opExtrude","CAP_FACE",FACE,{"disambiguationData":[OSD([sQuery(id+"F0.wireOp",EDGE,"E0"),sQuery(id+"F0.wireOp",EDGE,"E1"),sQuery(id+"F0.wireOp",EDGE,"E2"),sQuery(id+"F0.wireOp",EDGE,"E3"),sQuery(id+"F0.wireOp",EDGE,"E4"),sQuery(id+"F0.wireOp",EDGE,"E5"),sQuery(id+"F0.wireOp",EDGE,"E6"),sQuery(id+"F0.wireOp",EDGE,"E7"),sQuery(id+"F0.wireOp",EDGE,"E9.rect.left"),sQuery(id+"F0.wireOp",EDGE,"E9.rect.right"),subQ1,sQuery(id+"F0.wireOp",EDGE,"E10.rect.top"),sQuery(id+"F0.wireOp",EDGE,"E11.rect.bottom"),sQuery(id+"F0.wireOp",EDGE,"E11.rect.top"),sQuery(id+"F0.wireOp",EDGE,"E12.rect.left"),sQuery(id+"F0.wireOp",EDGE,"E12.rect.right"),sQuery(id+"F0.wireOp",EDGE,"E13.rect.left"),sQuery(id+"F0.wireOp",EDGE,"E13.rect.right"),sQuery(id+"F0.wireOp",EDGE,"E14.left"),sQuery(id+"F0.wireOp",EDGE,"E14.right"),sQuery(id+"F0.wireOp",EDGE,"E15"),subQ0,sQuery(id+"F0.wireOp",EDGE,"E18"),sQuery(id+"F0.wireOp",EDGE,"E20"),sQuery(id+"F0.wireOp",EDGE,"E21.rect.bottom"),sQuery(id+"F0.wireOp",EDGE,"E21.rect.top"),sQuery(id+"F0.wireOp",EDGE,"E22.left"),sQuery(id+"F0.wireOp",EDGE,"E22.right"),sQuery(id+"F0.wireOp",EDGE,"E23.top"),sQuery(id+"F0.wireOp",EDGE,"E23.left"),sQuery(id+"F0.wireOp",EDGE,"E23.right"),sQuery(id+"F0.wireOp",EDGE,"E22.top"),sQuery(id+"F0.wireOp",EDGE,"E26"),sQuery(id+"F0.wireOp",EDGE,"E29"),sQuery(id+"F0.wireOp",EDGE,"E32"),sQuery(id+"F0.wireOp",EDGE,"E35"),sQuery(id+"F0.wireOp",EDGE,"E36"),sQuery(id+"F0.wireOp",EDGE,"E41"),sQuery(id+"F0.wireOp",EDGE,"E44"),sQuery(id+"F0.wireOp",EDGE,"E47"),sQuery(id+"F0.wireOp",EDGE,"E48"),sQuery(id+"F0.wireOp",EDGE,"E49"),sQuery(id+"F0.wireOp",EDGE,"E50"),sQuery(id+"F0.wireOp",EDGE,"E51")])],"isStart":true})]});}
            var Q92;
            Q92=makeQuery(id+"F1.opExtrude","CAP_EDGE",EDGE,{"disambiguationData":[OSD([sQuery(id+"F0.wireOp",EDGE,"E13.rect.right"),sQuery(id+"F0.wireOp",EDGE,"E15"),sQuery(id+"F0.wireOp",EDGE,"E22.right")])],"isStart":true});
            var Q93;
            {var subQ0=sQuery(id+"F0.wireOp",EDGE,"E15");var subQ1=sQuery(id+"F0.wireOp",EDGE,"E10.rect.bottom");Q93=makeQuery(id+"F4.opFillet","BLEND_EDGE",EDGE,{"blendedFrom":[makeQuery(id+"F1.opExtrude","SWEPT_EDGE",EDGE,{"disambiguationData":[OSD([subQ1,subQ0,sQuery(id+"F0.wireOp",EDGE,"E16")])]}),makeQuery(id+"F1.opExtrude","CAP_FACE",FACE,{"disambiguationData":[OSD([sQuery(id+"F0.wireOp",EDGE,"E0"),sQuery(id+"F0.wireOp",EDGE,"E1"),sQuery(id+"F0.wireOp",EDGE,"E2"),sQuery(id+"F0.wireOp",EDGE,"E3"),sQuery(id+"F0.wireOp",EDGE,"E4"),sQuery(id+"F0.wireOp",EDGE,"E5"),sQuery(id+"F0.wireOp",EDGE,"E6"),sQuery(id+"F0.wireOp",EDGE,"E7"),sQuery(id+"F0.wireOp",EDGE,"E9.rect.left"),sQuery(id+"F0.wireOp",EDGE,"E9.rect.right"),subQ1,sQuery(id+"F0.wireOp",EDGE,"E10.rect.top"),sQuery(id+"F0.wireOp",EDGE,"E11.rect.bottom"),sQuery(id+"F0.wireOp",EDGE,"E11.rect.top"),sQuery(id+"F0.wireOp",EDGE,"E12.rect.left"),sQuery(id+"F0.wireOp",EDGE,"E12.rect.right"),sQuery(id+"F0.wireOp",EDGE,"E13.rect.left"),sQuery(id+"F0.wireOp",EDGE,"E13.rect.right"),sQuery(id+"F0.wireOp",EDGE,"E14.left"),sQuery(id+"F0.wireOp",EDGE,"E14.right"),subQ0,sQuery(id+"F0.wireOp",EDGE,"E17"),sQuery(id+"F0.wireOp",EDGE,"E18"),sQuery(id+"F0.wireOp",EDGE,"E20"),sQuery(id+"F0.wireOp",EDGE,"E21.rect.bottom"),sQuery(id+"F0.wireOp",EDGE,"E21.rect.top"),sQuery(id+"F0.wireOp",EDGE,"E22.left"),sQuery(id+"F0.wireOp",EDGE,"E22.right"),sQuery(id+"F0.wireOp",EDGE,"E23.top"),sQuery(id+"F0.wireOp",EDGE,"E23.left"),sQuery(id+"F0.wireOp",EDGE,"E23.right"),sQuery(id+"F0.wireOp",EDGE,"E22.top"),sQuery(id+"F0.wireOp",EDGE,"E26"),sQuery(id+"F0.wireOp",EDGE,"E29"),sQuery(id+"F0.wireOp",EDGE,"E32"),sQuery(id+"F0.wireOp",EDGE,"E35"),sQuery(id+"F0.wireOp",EDGE,"E36"),sQuery(id+"F0.wireOp",EDGE,"E41"),sQuery(id+"F0.wireOp",EDGE,"E44"),sQuery(id+"F0.wireOp",EDGE,"E47"),sQuery(id+"F0.wireOp",EDGE,"E48"),sQuery(id+"F0.wireOp",EDGE,"E49"),sQuery(id+"F0.wireOp",EDGE,"E50"),sQuery(id+"F0.wireOp",EDGE,"E51")])],"isStart":true})],"blendedInto":[makeQuery(id+"F1.opExtrude","CAP_FACE",FACE,{"disambiguationData":[OSD([sQuery(id+"F0.wireOp",EDGE,"E0"),sQuery(id+"F0.wireOp",EDGE,"E1"),sQuery(id+"F0.wireOp",EDGE,"E2"),sQuery(id+"F0.wireOp",EDGE,"E3"),sQuery(id+"F0.wireOp",EDGE,"E4"),sQuery(id+"F0.wireOp",EDGE,"E5"),sQuery(id+"F0.wireOp",EDGE,"E6"),sQuery(id+"F0.wireOp",EDGE,"E7"),sQuery(id+"F0.wireOp",EDGE,"E9.rect.left"),sQuery(id+"F0.wireOp",EDGE,"E9.rect.right"),subQ1,sQuery(id+"F0.wireOp",EDGE,"E10.rect.top"),sQuery(id+"F0.wireOp",EDGE,"E11.rect.bottom"),sQuery(id+"F0.wireOp",EDGE,"E11.rect.top"),sQuery(id+"F0.wireOp",EDGE,"E12.rect.left"),sQuery(id+"F0.wireOp",EDGE,"E12.rect.right"),sQuery(id+"F0.wireOp",EDGE,"E13.rect.left"),sQuery(id+"F0.wireOp",EDGE,"E13.rect.right"),sQuery(id+"F0.wireOp",EDGE,"E14.left"),sQuery(id+"F0.wireOp",EDGE,"E14.right"),subQ0,sQuery(id+"F0.wireOp",EDGE,"E17"),sQuery(id+"F0.wireOp",EDGE,"E18"),sQuery(id+"F0.wireOp",EDGE,"E20"),sQuery(id+"F0.wireOp",EDGE,"E21.rect.bottom"),sQuery(id+"F0.wireOp",EDGE,"E21.rect.top"),sQuery(id+"F0.wireOp",EDGE,"E22.left"),sQuery(id+"F0.wireOp",EDGE,"E22.right"),sQuery(id+"F0.wireOp",EDGE,"E23.top"),sQuery(id+"F0.wireOp",EDGE,"E23.left"),sQuery(id+"F0.wireOp",EDGE,"E23.right"),sQuery(id+"F0.wireOp",EDGE,"E22.top"),sQuery(id+"F0.wireOp",EDGE,"E26"),sQuery(id+"F0.wireOp",EDGE,"E29"),sQuery(id+"F0.wireOp",EDGE,"E32"),sQuery(id+"F0.wireOp",EDGE,"E35"),sQuery(id+"F0.wireOp",EDGE,"E36"),sQuery(id+"F0.wireOp",EDGE,"E41"),sQuery(id+"F0.wireOp",EDGE,"E44"),sQuery(id+"F0.wireOp",EDGE,"E47"),sQuery(id+"F0.wireOp",EDGE,"E48"),sQuery(id+"F0.wireOp",EDGE,"E49"),sQuery(id+"F0.wireOp",EDGE,"E50"),sQuery(id+"F0.wireOp",EDGE,"E51")])],"isStart":true})]});}
            var Q94;
            {var subQ0=sQuery(id+"F0.wireOp",EDGE,"E10.rect.bottom");Q94=makeQuery(id+"F1.opExtrude","CAP_EDGE",EDGE,{"disambiguationData":[OSD([subQ0]),TDD([makeQuery(id+"F0.imprint","IMPRINT",EDGE,{"disambiguationData":[TD([[makeQuery(id+"F0.imprint","INTERSECT",VERTEX,{"derivedFrom":[subQ0,sQuery(id+"F0.wireOp",EDGE,"E12.rect.right"),sQuery(id+"F0.wireOp",EDGE,"E47")]}),1.0]])],"derivedFrom":subQ0})])],"isStart":true});}
            var Q95;
            {var subQ0=sQuery(id+"F0.wireOp",EDGE,"E47");var subQ1=sQuery(id+"F0.wireOp",EDGE,"E12.rect.right");var subQ2=sQuery(id+"F0.wireOp",EDGE,"E10.rect.bottom");Q95=makeQuery(id+"F4.opFillet","BLEND_EDGE",EDGE,{"blendedFrom":[makeQuery(id+"F1.opExtrude","SWEPT_EDGE",EDGE,{"disambiguationData":[OSD([subQ2,subQ1,subQ0])]}),makeQuery(id+"F1.opExtrude","CAP_FACE",FACE,{"disambiguationData":[OSD([sQuery(id+"F0.wireOp",EDGE,"E0"),sQuery(id+"F0.wireOp",EDGE,"E1"),sQuery(id+"F0.wireOp",EDGE,"E2"),sQuery(id+"F0.wireOp",EDGE,"E3"),sQuery(id+"F0.wireOp",EDGE,"E4"),sQuery(id+"F0.wireOp",EDGE,"E5"),sQuery(id+"F0.wireOp",EDGE,"E6"),sQuery(id+"F0.wireOp",EDGE,"E7"),sQuery(id+"F0.wireOp",EDGE,"E9.rect.left"),sQuery(id+"F0.wireOp",EDGE,"E9.rect.right"),subQ2,sQuery(id+"F0.wireOp",EDGE,"E10.rect.top"),sQuery(id+"F0.wireOp",EDGE,"E11.rect.bottom"),sQuery(id+"F0.wireOp",EDGE,"E11.rect.top"),sQuery(id+"F0.wireOp",EDGE,"E12.rect.left"),subQ1,sQuery(id+"F0.wireOp",EDGE,"E13.rect.left"),sQuery(id+"F0.wireOp",EDGE,"E13.rect.right"),sQuery(id+"F0.wireOp",EDGE,"E14.left"),sQuery(id+"F0.wireOp",EDGE,"E14.right"),sQuery(id+"F0.wireOp",EDGE,"E15"),sQuery(id+"F0.wireOp",EDGE,"E17"),sQuery(id+"F0.wireOp",EDGE,"E18"),sQuery(id+"F0.wireOp",EDGE,"E20"),sQuery(id+"F0.wireOp",EDGE,"E21.rect.bottom"),sQuery(id+"F0.wireOp",EDGE,"E21.rect.top"),sQuery(id+"F0.wireOp",EDGE,"E22.left"),sQuery(id+"F0.wireOp",EDGE,"E22.right"),sQuery(id+"F0.wireOp",EDGE,"E23.top"),sQuery(id+"F0.wireOp",EDGE,"E23.left"),sQuery(id+"F0.wireOp",EDGE,"E23.right"),sQuery(id+"F0.wireOp",EDGE,"E22.top"),sQuery(id+"F0.wireOp",EDGE,"E26"),sQuery(id+"F0.wireOp",EDGE,"E29"),sQuery(id+"F0.wireOp",EDGE,"E32"),sQuery(id+"F0.wireOp",EDGE,"E35"),sQuery(id+"F0.wireOp",EDGE,"E36"),sQuery(id+"F0.wireOp",EDGE,"E41"),sQuery(id+"F0.wireOp",EDGE,"E44"),subQ0,sQuery(id+"F0.wireOp",EDGE,"E48"),sQuery(id+"F0.wireOp",EDGE,"E49"),sQuery(id+"F0.wireOp",EDGE,"E50"),sQuery(id+"F0.wireOp",EDGE,"E51")])],"isStart":true})],"blendedInto":[makeQuery(id+"F1.opExtrude","CAP_FACE",FACE,{"disambiguationData":[OSD([sQuery(id+"F0.wireOp",EDGE,"E0"),sQuery(id+"F0.wireOp",EDGE,"E1"),sQuery(id+"F0.wireOp",EDGE,"E2"),sQuery(id+"F0.wireOp",EDGE,"E3"),sQuery(id+"F0.wireOp",EDGE,"E4"),sQuery(id+"F0.wireOp",EDGE,"E5"),sQuery(id+"F0.wireOp",EDGE,"E6"),sQuery(id+"F0.wireOp",EDGE,"E7"),sQuery(id+"F0.wireOp",EDGE,"E9.rect.left"),sQuery(id+"F0.wireOp",EDGE,"E9.rect.right"),subQ2,sQuery(id+"F0.wireOp",EDGE,"E10.rect.top"),sQuery(id+"F0.wireOp",EDGE,"E11.rect.bottom"),sQuery(id+"F0.wireOp",EDGE,"E11.rect.top"),sQuery(id+"F0.wireOp",EDGE,"E12.rect.left"),subQ1,sQuery(id+"F0.wireOp",EDGE,"E13.rect.left"),sQuery(id+"F0.wireOp",EDGE,"E13.rect.right"),sQuery(id+"F0.wireOp",EDGE,"E14.left"),sQuery(id+"F0.wireOp",EDGE,"E14.right"),sQuery(id+"F0.wireOp",EDGE,"E15"),sQuery(id+"F0.wireOp",EDGE,"E17"),sQuery(id+"F0.wireOp",EDGE,"E18"),sQuery(id+"F0.wireOp",EDGE,"E20"),sQuery(id+"F0.wireOp",EDGE,"E21.rect.bottom"),sQuery(id+"F0.wireOp",EDGE,"E21.rect.top"),sQuery(id+"F0.wireOp",EDGE,"E22.left"),sQuery(id+"F0.wireOp",EDGE,"E22.right"),sQuery(id+"F0.wireOp",EDGE,"E23.top"),sQuery(id+"F0.wireOp",EDGE,"E23.left"),sQuery(id+"F0.wireOp",EDGE,"E23.right"),sQuery(id+"F0.wireOp",EDGE,"E22.top"),sQuery(id+"F0.wireOp",EDGE,"E26"),sQuery(id+"F0.wireOp",EDGE,"E29"),sQuery(id+"F0.wireOp",EDGE,"E32"),sQuery(id+"F0.wireOp",EDGE,"E35"),sQuery(id+"F0.wireOp",EDGE,"E36"),sQuery(id+"F0.wireOp",EDGE,"E41"),sQuery(id+"F0.wireOp",EDGE,"E44"),subQ0,sQuery(id+"F0.wireOp",EDGE,"E48"),sQuery(id+"F0.wireOp",EDGE,"E49"),sQuery(id+"F0.wireOp",EDGE,"E50"),sQuery(id+"F0.wireOp",EDGE,"E51")])],"isStart":true})]});}
            var Q96;
            Q96=makeQuery(id+"F1.opExtrude","CAP_EDGE",EDGE,{"disambiguationData":[OSD([sQuery(id+"F0.wireOp",EDGE,"E47")])],"isStart":true});
            var Q97;
            Q97=makeQuery(id+"F1.opExtrude","CAP_EDGE",EDGE,{"disambiguationData":[OSD([sQuery(id+"F0.wireOp",EDGE,"E0")])],"isStart":true});
            var Q98;
            {var subQ0=sQuery(id+"F0.wireOp",EDGE,"E26");var subQ1=sQuery(id+"F0.wireOp",EDGE,"E4");Q98=makeQuery(id+"F2.opFillet","BLEND_EDGE",EDGE,{"blendedFrom":[makeQuery(id+"F1.opExtrude","SWEPT_EDGE",EDGE,{"disambiguationData":[OSD([subQ1,subQ0])]}),makeQuery(id+"F1.opExtrude","CAP_FACE",FACE,{"disambiguationData":[OSD([sQuery(id+"F0.wireOp",EDGE,"E0"),sQuery(id+"F0.wireOp",EDGE,"E1"),sQuery(id+"F0.wireOp",EDGE,"E2"),sQuery(id+"F0.wireOp",EDGE,"E3"),subQ1,sQuery(id+"F0.wireOp",EDGE,"E5"),sQuery(id+"F0.wireOp",EDGE,"E6"),sQuery(id+"F0.wireOp",EDGE,"E7"),sQuery(id+"F0.wireOp",EDGE,"E9.rect.left"),sQuery(id+"F0.wireOp",EDGE,"E9.rect.right"),sQuery(id+"F0.wireOp",EDGE,"E10.rect.bottom"),sQuery(id+"F0.wireOp",EDGE,"E10.rect.top"),sQuery(id+"F0.wireOp",EDGE,"E11.rect.bottom"),sQuery(id+"F0.wireOp",EDGE,"E11.rect.top"),sQuery(id+"F0.wireOp",EDGE,"E12.rect.left"),sQuery(id+"F0.wireOp",EDGE,"E12.rect.right"),sQuery(id+"F0.wireOp",EDGE,"E13.rect.left"),sQuery(id+"F0.wireOp",EDGE,"E13.rect.right"),sQuery(id+"F0.wireOp",EDGE,"E14.left"),sQuery(id+"F0.wireOp",EDGE,"E14.right"),sQuery(id+"F0.wireOp",EDGE,"E15"),sQuery(id+"F0.wireOp",EDGE,"E17"),sQuery(id+"F0.wireOp",EDGE,"E18"),sQuery(id+"F0.wireOp",EDGE,"E20"),sQuery(id+"F0.wireOp",EDGE,"E21.rect.bottom"),sQuery(id+"F0.wireOp",EDGE,"E21.rect.top"),sQuery(id+"F0.wireOp",EDGE,"E22.left"),sQuery(id+"F0.wireOp",EDGE,"E22.right"),sQuery(id+"F0.wireOp",EDGE,"E23.top"),sQuery(id+"F0.wireOp",EDGE,"E23.left"),sQuery(id+"F0.wireOp",EDGE,"E23.right"),sQuery(id+"F0.wireOp",EDGE,"E22.top"),subQ0,sQuery(id+"F0.wireOp",EDGE,"E29"),sQuery(id+"F0.wireOp",EDGE,"E32"),sQuery(id+"F0.wireOp",EDGE,"E35"),sQuery(id+"F0.wireOp",EDGE,"E36"),sQuery(id+"F0.wireOp",EDGE,"E41"),sQuery(id+"F0.wireOp",EDGE,"E44"),sQuery(id+"F0.wireOp",EDGE,"E47"),sQuery(id+"F0.wireOp",EDGE,"E48"),sQuery(id+"F0.wireOp",EDGE,"E49"),sQuery(id+"F0.wireOp",EDGE,"E50"),sQuery(id+"F0.wireOp",EDGE,"E51")])],"isStart":true})],"blendedInto":[makeQuery(id+"F1.opExtrude","CAP_FACE",FACE,{"disambiguationData":[OSD([sQuery(id+"F0.wireOp",EDGE,"E0"),sQuery(id+"F0.wireOp",EDGE,"E1"),sQuery(id+"F0.wireOp",EDGE,"E2"),sQuery(id+"F0.wireOp",EDGE,"E3"),subQ1,sQuery(id+"F0.wireOp",EDGE,"E5"),sQuery(id+"F0.wireOp",EDGE,"E6"),sQuery(id+"F0.wireOp",EDGE,"E7"),sQuery(id+"F0.wireOp",EDGE,"E9.rect.left"),sQuery(id+"F0.wireOp",EDGE,"E9.rect.right"),sQuery(id+"F0.wireOp",EDGE,"E10.rect.bottom"),sQuery(id+"F0.wireOp",EDGE,"E10.rect.top"),sQuery(id+"F0.wireOp",EDGE,"E11.rect.bottom"),sQuery(id+"F0.wireOp",EDGE,"E11.rect.top"),sQuery(id+"F0.wireOp",EDGE,"E12.rect.left"),sQuery(id+"F0.wireOp",EDGE,"E12.rect.right"),sQuery(id+"F0.wireOp",EDGE,"E13.rect.left"),sQuery(id+"F0.wireOp",EDGE,"E13.rect.right"),sQuery(id+"F0.wireOp",EDGE,"E14.left"),sQuery(id+"F0.wireOp",EDGE,"E14.right"),sQuery(id+"F0.wireOp",EDGE,"E15"),sQuery(id+"F0.wireOp",EDGE,"E17"),sQuery(id+"F0.wireOp",EDGE,"E18"),sQuery(id+"F0.wireOp",EDGE,"E20"),sQuery(id+"F0.wireOp",EDGE,"E21.rect.bottom"),sQuery(id+"F0.wireOp",EDGE,"E21.rect.top"),sQuery(id+"F0.wireOp",EDGE,"E22.left"),sQuery(id+"F0.wireOp",EDGE,"E22.right"),sQuery(id+"F0.wireOp",EDGE,"E23.top"),sQuery(id+"F0.wireOp",EDGE,"E23.left"),sQuery(id+"F0.wireOp",EDGE,"E23.right"),sQuery(id+"F0.wireOp",EDGE,"E22.top"),subQ0,sQuery(id+"F0.wireOp",EDGE,"E29"),sQuery(id+"F0.wireOp",EDGE,"E32"),sQuery(id+"F0.wireOp",EDGE,"E35"),sQuery(id+"F0.wireOp",EDGE,"E36"),sQuery(id+"F0.wireOp",EDGE,"E41"),sQuery(id+"F0.wireOp",EDGE,"E44"),sQuery(id+"F0.wireOp",EDGE,"E47"),sQuery(id+"F0.wireOp",EDGE,"E48"),sQuery(id+"F0.wireOp",EDGE,"E49"),sQuery(id+"F0.wireOp",EDGE,"E50"),sQuery(id+"F0.wireOp",EDGE,"E51")])],"isStart":true})]});}
            var Q99;
            Q99=makeQuery(id+"F1.opExtrude","CAP_EDGE",EDGE,{"disambiguationData":[OSD([sQuery(id+"F0.wireOp",EDGE,"E4")])],"isStart":true});
            var Q100;
            {var subQ0=sQuery(id+"F0.wireOp",EDGE,"E48");var subQ1=sQuery(id+"F0.wireOp",EDGE,"E4");Q100=makeQuery(id+"F3.opFillet","BLEND_EDGE",EDGE,{"blendedFrom":[makeQuery(id+"F1.opExtrude","SWEPT_EDGE",EDGE,{"disambiguationData":[OSD([subQ1,subQ0])]}),makeQuery(id+"F1.opExtrude","CAP_FACE",FACE,{"disambiguationData":[OSD([sQuery(id+"F0.wireOp",EDGE,"E0"),sQuery(id+"F0.wireOp",EDGE,"E1"),sQuery(id+"F0.wireOp",EDGE,"E2"),sQuery(id+"F0.wireOp",EDGE,"E3"),subQ1,sQuery(id+"F0.wireOp",EDGE,"E5"),sQuery(id+"F0.wireOp",EDGE,"E6"),sQuery(id+"F0.wireOp",EDGE,"E7"),sQuery(id+"F0.wireOp",EDGE,"E9.rect.left"),sQuery(id+"F0.wireOp",EDGE,"E9.rect.right"),sQuery(id+"F0.wireOp",EDGE,"E10.rect.bottom"),sQuery(id+"F0.wireOp",EDGE,"E10.rect.top"),sQuery(id+"F0.wireOp",EDGE,"E11.rect.bottom"),sQuery(id+"F0.wireOp",EDGE,"E11.rect.top"),sQuery(id+"F0.wireOp",EDGE,"E12.rect.left"),sQuery(id+"F0.wireOp",EDGE,"E12.rect.right"),sQuery(id+"F0.wireOp",EDGE,"E13.rect.left"),sQuery(id+"F0.wireOp",EDGE,"E13.rect.right"),sQuery(id+"F0.wireOp",EDGE,"E14.left"),sQuery(id+"F0.wireOp",EDGE,"E14.right"),sQuery(id+"F0.wireOp",EDGE,"E15"),sQuery(id+"F0.wireOp",EDGE,"E17"),sQuery(id+"F0.wireOp",EDGE,"E18"),sQuery(id+"F0.wireOp",EDGE,"E20"),sQuery(id+"F0.wireOp",EDGE,"E21.rect.bottom"),sQuery(id+"F0.wireOp",EDGE,"E21.rect.top"),sQuery(id+"F0.wireOp",EDGE,"E22.left"),sQuery(id+"F0.wireOp",EDGE,"E22.right"),sQuery(id+"F0.wireOp",EDGE,"E23.top"),sQuery(id+"F0.wireOp",EDGE,"E23.left"),sQuery(id+"F0.wireOp",EDGE,"E23.right"),sQuery(id+"F0.wireOp",EDGE,"E22.top"),sQuery(id+"F0.wireOp",EDGE,"E26"),sQuery(id+"F0.wireOp",EDGE,"E29"),sQuery(id+"F0.wireOp",EDGE,"E32"),sQuery(id+"F0.wireOp",EDGE,"E35"),sQuery(id+"F0.wireOp",EDGE,"E36"),sQuery(id+"F0.wireOp",EDGE,"E41"),sQuery(id+"F0.wireOp",EDGE,"E44"),sQuery(id+"F0.wireOp",EDGE,"E47"),subQ0,sQuery(id+"F0.wireOp",EDGE,"E49"),sQuery(id+"F0.wireOp",EDGE,"E50"),sQuery(id+"F0.wireOp",EDGE,"E51")])],"isStart":true})],"blendedInto":[makeQuery(id+"F1.opExtrude","CAP_FACE",FACE,{"disambiguationData":[OSD([sQuery(id+"F0.wireOp",EDGE,"E0"),sQuery(id+"F0.wireOp",EDGE,"E1"),sQuery(id+"F0.wireOp",EDGE,"E2"),sQuery(id+"F0.wireOp",EDGE,"E3"),subQ1,sQuery(id+"F0.wireOp",EDGE,"E5"),sQuery(id+"F0.wireOp",EDGE,"E6"),sQuery(id+"F0.wireOp",EDGE,"E7"),sQuery(id+"F0.wireOp",EDGE,"E9.rect.left"),sQuery(id+"F0.wireOp",EDGE,"E9.rect.right"),sQuery(id+"F0.wireOp",EDGE,"E10.rect.bottom"),sQuery(id+"F0.wireOp",EDGE,"E10.rect.top"),sQuery(id+"F0.wireOp",EDGE,"E11.rect.bottom"),sQuery(id+"F0.wireOp",EDGE,"E11.rect.top"),sQuery(id+"F0.wireOp",EDGE,"E12.rect.left"),sQuery(id+"F0.wireOp",EDGE,"E12.rect.right"),sQuery(id+"F0.wireOp",EDGE,"E13.rect.left"),sQuery(id+"F0.wireOp",EDGE,"E13.rect.right"),sQuery(id+"F0.wireOp",EDGE,"E14.left"),sQuery(id+"F0.wireOp",EDGE,"E14.right"),sQuery(id+"F0.wireOp",EDGE,"E15"),sQuery(id+"F0.wireOp",EDGE,"E17"),sQuery(id+"F0.wireOp",EDGE,"E18"),sQuery(id+"F0.wireOp",EDGE,"E20"),sQuery(id+"F0.wireOp",EDGE,"E21.rect.bottom"),sQuery(id+"F0.wireOp",EDGE,"E21.rect.top"),sQuery(id+"F0.wireOp",EDGE,"E22.left"),sQuery(id+"F0.wireOp",EDGE,"E22.right"),sQuery(id+"F0.wireOp",EDGE,"E23.top"),sQuery(id+"F0.wireOp",EDGE,"E23.left"),sQuery(id+"F0.wireOp",EDGE,"E23.right"),sQuery(id+"F0.wireOp",EDGE,"E22.top"),sQuery(id+"F0.wireOp",EDGE,"E26"),sQuery(id+"F0.wireOp",EDGE,"E29"),sQuery(id+"F0.wireOp",EDGE,"E32"),sQuery(id+"F0.wireOp",EDGE,"E35"),sQuery(id+"F0.wireOp",EDGE,"E36"),sQuery(id+"F0.wireOp",EDGE,"E41"),sQuery(id+"F0.wireOp",EDGE,"E44"),sQuery(id+"F0.wireOp",EDGE,"E47"),subQ0,sQuery(id+"F0.wireOp",EDGE,"E49"),sQuery(id+"F0.wireOp",EDGE,"E50"),sQuery(id+"F0.wireOp",EDGE,"E51")])],"isStart":true})]});}
            var Q101;
            Q101=makeQuery(id+"F1.opExtrude","CAP_EDGE",EDGE,{"disambiguationData":[OSD([sQuery(id+"F0.wireOp",EDGE,"E48")])],"isStart":true});
            var Q102;
            {var subQ0=sQuery(id+"F0.wireOp",EDGE,"E48");var subQ1=sQuery(id+"F0.wireOp",EDGE,"E9.rect.right");Q102=makeQuery(id+"F3.opFillet","BLEND_EDGE",EDGE,{"blendedFrom":[makeQuery(id+"F1.opExtrude","SWEPT_EDGE",EDGE,{"disambiguationData":[OSD([subQ1,subQ0])]}),makeQuery(id+"F1.opExtrude","CAP_FACE",FACE,{"disambiguationData":[OSD([sQuery(id+"F0.wireOp",EDGE,"E0"),sQuery(id+"F0.wireOp",EDGE,"E1"),sQuery(id+"F0.wireOp",EDGE,"E2"),sQuery(id+"F0.wireOp",EDGE,"E3"),sQuery(id+"F0.wireOp",EDGE,"E4"),sQuery(id+"F0.wireOp",EDGE,"E5"),sQuery(id+"F0.wireOp",EDGE,"E6"),sQuery(id+"F0.wireOp",EDGE,"E7"),sQuery(id+"F0.wireOp",EDGE,"E9.rect.left"),subQ1,sQuery(id+"F0.wireOp",EDGE,"E10.rect.bottom"),sQuery(id+"F0.wireOp",EDGE,"E10.rect.top"),sQuery(id+"F0.wireOp",EDGE,"E11.rect.bottom"),sQuery(id+"F0.wireOp",EDGE,"E11.rect.top"),sQuery(id+"F0.wireOp",EDGE,"E12.rect.left"),sQuery(id+"F0.wireOp",EDGE,"E12.rect.right"),sQuery(id+"F0.wireOp",EDGE,"E13.rect.left"),sQuery(id+"F0.wireOp",EDGE,"E13.rect.right"),sQuery(id+"F0.wireOp",EDGE,"E14.left"),sQuery(id+"F0.wireOp",EDGE,"E14.right"),sQuery(id+"F0.wireOp",EDGE,"E15"),sQuery(id+"F0.wireOp",EDGE,"E17"),sQuery(id+"F0.wireOp",EDGE,"E18"),sQuery(id+"F0.wireOp",EDGE,"E20"),sQuery(id+"F0.wireOp",EDGE,"E21.rect.bottom"),sQuery(id+"F0.wireOp",EDGE,"E21.rect.top"),sQuery(id+"F0.wireOp",EDGE,"E22.left"),sQuery(id+"F0.wireOp",EDGE,"E22.right"),sQuery(id+"F0.wireOp",EDGE,"E23.top"),sQuery(id+"F0.wireOp",EDGE,"E23.left"),sQuery(id+"F0.wireOp",EDGE,"E23.right"),sQuery(id+"F0.wireOp",EDGE,"E22.top"),sQuery(id+"F0.wireOp",EDGE,"E26"),sQuery(id+"F0.wireOp",EDGE,"E29"),sQuery(id+"F0.wireOp",EDGE,"E32"),sQuery(id+"F0.wireOp",EDGE,"E35"),sQuery(id+"F0.wireOp",EDGE,"E36"),sQuery(id+"F0.wireOp",EDGE,"E41"),sQuery(id+"F0.wireOp",EDGE,"E44"),sQuery(id+"F0.wireOp",EDGE,"E47"),subQ0,sQuery(id+"F0.wireOp",EDGE,"E49"),sQuery(id+"F0.wireOp",EDGE,"E50"),sQuery(id+"F0.wireOp",EDGE,"E51")])],"isStart":true})],"blendedInto":[makeQuery(id+"F1.opExtrude","CAP_FACE",FACE,{"disambiguationData":[OSD([sQuery(id+"F0.wireOp",EDGE,"E0"),sQuery(id+"F0.wireOp",EDGE,"E1"),sQuery(id+"F0.wireOp",EDGE,"E2"),sQuery(id+"F0.wireOp",EDGE,"E3"),sQuery(id+"F0.wireOp",EDGE,"E4"),sQuery(id+"F0.wireOp",EDGE,"E5"),sQuery(id+"F0.wireOp",EDGE,"E6"),sQuery(id+"F0.wireOp",EDGE,"E7"),sQuery(id+"F0.wireOp",EDGE,"E9.rect.left"),subQ1,sQuery(id+"F0.wireOp",EDGE,"E10.rect.bottom"),sQuery(id+"F0.wireOp",EDGE,"E10.rect.top"),sQuery(id+"F0.wireOp",EDGE,"E11.rect.bottom"),sQuery(id+"F0.wireOp",EDGE,"E11.rect.top"),sQuery(id+"F0.wireOp",EDGE,"E12.rect.left"),sQuery(id+"F0.wireOp",EDGE,"E12.rect.right"),sQuery(id+"F0.wireOp",EDGE,"E13.rect.left"),sQuery(id+"F0.wireOp",EDGE,"E13.rect.right"),sQuery(id+"F0.wireOp",EDGE,"E14.left"),sQuery(id+"F0.wireOp",EDGE,"E14.right"),sQuery(id+"F0.wireOp",EDGE,"E15"),sQuery(id+"F0.wireOp",EDGE,"E17"),sQuery(id+"F0.wireOp",EDGE,"E18"),sQuery(id+"F0.wireOp",EDGE,"E20"),sQuery(id+"F0.wireOp",EDGE,"E21.rect.bottom"),sQuery(id+"F0.wireOp",EDGE,"E21.rect.top"),sQuery(id+"F0.wireOp",EDGE,"E22.left"),sQuery(id+"F0.wireOp",EDGE,"E22.right"),sQuery(id+"F0.wireOp",EDGE,"E23.top"),sQuery(id+"F0.wireOp",EDGE,"E23.left"),sQuery(id+"F0.wireOp",EDGE,"E23.right"),sQuery(id+"F0.wireOp",EDGE,"E22.top"),sQuery(id+"F0.wireOp",EDGE,"E26"),sQuery(id+"F0.wireOp",EDGE,"E29"),sQuery(id+"F0.wireOp",EDGE,"E32"),sQuery(id+"F0.wireOp",EDGE,"E35"),sQuery(id+"F0.wireOp",EDGE,"E36"),sQuery(id+"F0.wireOp",EDGE,"E41"),sQuery(id+"F0.wireOp",EDGE,"E44"),sQuery(id+"F0.wireOp",EDGE,"E47"),subQ0,sQuery(id+"F0.wireOp",EDGE,"E49"),sQuery(id+"F0.wireOp",EDGE,"E50"),sQuery(id+"F0.wireOp",EDGE,"E51")])],"isStart":true})]});}
            var Q103;
            {var subQ0=sQuery(id+"F0.wireOp",EDGE,"E9.rect.right");Q103=makeQuery(id+"F1.opExtrude","CAP_EDGE",EDGE,{"disambiguationData":[OSD([subQ0]),TDD([makeQuery(id+"F0.imprint","IMPRINT",EDGE,{"disambiguationData":[TD([[makeQuery(id+"F0.imprint","INTERSECT",VERTEX,{"derivedFrom":[subQ0,sQuery(id+"F0.wireOp",EDGE,"E48")]}),-1.0]])],"derivedFrom":subQ0})])],"isStart":true});}
            var Q104;
            {var subQ0=sQuery(id+"F0.wireOp",EDGE,"E9.rect.right");Q104=makeQuery(id+"F1.opExtrude","CAP_EDGE",EDGE,{"disambiguationData":[OSD([subQ0]),TDD([makeQuery(id+"F0.imprint","IMPRINT",EDGE,{"disambiguationData":[TD([[makeQuery(id+"F0.imprint","INTERSECT",VERTEX,{"derivedFrom":[subQ0,sQuery(id+"F0.wireOp",EDGE,"E48")]}),-1.0]])],"derivedFrom":subQ0})])],"isStart":true});}
            var Q105;
            {var subQ0=sQuery(id+"F0.wireOp",EDGE,"E50");var subQ1=sQuery(id+"F0.wireOp",EDGE,"E9.rect.right");Q105=makeQuery(id+"F3.opFillet","BLEND_EDGE",EDGE,{"blendedFrom":[makeQuery(id+"F1.opExtrude","SWEPT_EDGE",EDGE,{"disambiguationData":[OSD([subQ1,subQ0])]}),makeQuery(id+"F1.opExtrude","CAP_FACE",FACE,{"disambiguationData":[OSD([sQuery(id+"F0.wireOp",EDGE,"E0"),sQuery(id+"F0.wireOp",EDGE,"E1"),sQuery(id+"F0.wireOp",EDGE,"E2"),sQuery(id+"F0.wireOp",EDGE,"E3"),sQuery(id+"F0.wireOp",EDGE,"E4"),sQuery(id+"F0.wireOp",EDGE,"E5"),sQuery(id+"F0.wireOp",EDGE,"E6"),sQuery(id+"F0.wireOp",EDGE,"E7"),sQuery(id+"F0.wireOp",EDGE,"E9.rect.left"),subQ1,sQuery(id+"F0.wireOp",EDGE,"E10.rect.bottom"),sQuery(id+"F0.wireOp",EDGE,"E10.rect.top"),sQuery(id+"F0.wireOp",EDGE,"E11.rect.bottom"),sQuery(id+"F0.wireOp",EDGE,"E11.rect.top"),sQuery(id+"F0.wireOp",EDGE,"E12.rect.left"),sQuery(id+"F0.wireOp",EDGE,"E12.rect.right"),sQuery(id+"F0.wireOp",EDGE,"E13.rect.left"),sQuery(id+"F0.wireOp",EDGE,"E13.rect.right"),sQuery(id+"F0.wireOp",EDGE,"E14.left"),sQuery(id+"F0.wireOp",EDGE,"E14.right"),sQuery(id+"F0.wireOp",EDGE,"E15"),sQuery(id+"F0.wireOp",EDGE,"E17"),sQuery(id+"F0.wireOp",EDGE,"E18"),sQuery(id+"F0.wireOp",EDGE,"E20"),sQuery(id+"F0.wireOp",EDGE,"E21.rect.bottom"),sQuery(id+"F0.wireOp",EDGE,"E21.rect.top"),sQuery(id+"F0.wireOp",EDGE,"E22.left"),sQuery(id+"F0.wireOp",EDGE,"E22.right"),sQuery(id+"F0.wireOp",EDGE,"E23.top"),sQuery(id+"F0.wireOp",EDGE,"E23.left"),sQuery(id+"F0.wireOp",EDGE,"E23.right"),sQuery(id+"F0.wireOp",EDGE,"E22.top"),sQuery(id+"F0.wireOp",EDGE,"E26"),sQuery(id+"F0.wireOp",EDGE,"E29"),sQuery(id+"F0.wireOp",EDGE,"E32"),sQuery(id+"F0.wireOp",EDGE,"E35"),sQuery(id+"F0.wireOp",EDGE,"E36"),sQuery(id+"F0.wireOp",EDGE,"E41"),sQuery(id+"F0.wireOp",EDGE,"E44"),sQuery(id+"F0.wireOp",EDGE,"E47"),sQuery(id+"F0.wireOp",EDGE,"E48"),sQuery(id+"F0.wireOp",EDGE,"E49"),subQ0,sQuery(id+"F0.wireOp",EDGE,"E51")])],"isStart":true})],"blendedInto":[makeQuery(id+"F1.opExtrude","CAP_FACE",FACE,{"disambiguationData":[OSD([sQuery(id+"F0.wireOp",EDGE,"E0"),sQuery(id+"F0.wireOp",EDGE,"E1"),sQuery(id+"F0.wireOp",EDGE,"E2"),sQuery(id+"F0.wireOp",EDGE,"E3"),sQuery(id+"F0.wireOp",EDGE,"E4"),sQuery(id+"F0.wireOp",EDGE,"E5"),sQuery(id+"F0.wireOp",EDGE,"E6"),sQuery(id+"F0.wireOp",EDGE,"E7"),sQuery(id+"F0.wireOp",EDGE,"E9.rect.left"),subQ1,sQuery(id+"F0.wireOp",EDGE,"E10.rect.bottom"),sQuery(id+"F0.wireOp",EDGE,"E10.rect.top"),sQuery(id+"F0.wireOp",EDGE,"E11.rect.bottom"),sQuery(id+"F0.wireOp",EDGE,"E11.rect.top"),sQuery(id+"F0.wireOp",EDGE,"E12.rect.left"),sQuery(id+"F0.wireOp",EDGE,"E12.rect.right"),sQuery(id+"F0.wireOp",EDGE,"E13.rect.left"),sQuery(id+"F0.wireOp",EDGE,"E13.rect.right"),sQuery(id+"F0.wireOp",EDGE,"E14.left"),sQuery(id+"F0.wireOp",EDGE,"E14.right"),sQuery(id+"F0.wireOp",EDGE,"E15"),sQuery(id+"F0.wireOp",EDGE,"E17"),sQuery(id+"F0.wireOp",EDGE,"E18"),sQuery(id+"F0.wireOp",EDGE,"E20"),sQuery(id+"F0.wireOp",EDGE,"E21.rect.bottom"),sQuery(id+"F0.wireOp",EDGE,"E21.rect.top"),sQuery(id+"F0.wireOp",EDGE,"E22.left"),sQuery(id+"F0.wireOp",EDGE,"E22.right"),sQuery(id+"F0.wireOp",EDGE,"E23.top"),sQuery(id+"F0.wireOp",EDGE,"E23.left"),sQuery(id+"F0.wireOp",EDGE,"E23.right"),sQuery(id+"F0.wireOp",EDGE,"E22.top"),sQuery(id+"F0.wireOp",EDGE,"E26"),sQuery(id+"F0.wireOp",EDGE,"E29"),sQuery(id+"F0.wireOp",EDGE,"E32"),sQuery(id+"F0.wireOp",EDGE,"E35"),sQuery(id+"F0.wireOp",EDGE,"E36"),sQuery(id+"F0.wireOp",EDGE,"E41"),sQuery(id+"F0.wireOp",EDGE,"E44"),sQuery(id+"F0.wireOp",EDGE,"E47"),sQuery(id+"F0.wireOp",EDGE,"E48"),sQuery(id+"F0.wireOp",EDGE,"E49"),subQ0,sQuery(id+"F0.wireOp",EDGE,"E51")])],"isStart":true})]});}
            var Q106;
            Q106=makeQuery(id+"F1.opExtrude","CAP_EDGE",EDGE,{"disambiguationData":[OSD([sQuery(id+"F0.wireOp",EDGE,"E50")])],"isStart":true});
            var Q107;
            Q107=makeQuery(id+"F1.opExtrude","CAP_EDGE",EDGE,{"disambiguationData":[OSD([sQuery(id+"F0.wireOp",EDGE,"E7")])],"isStart":true});
            var Q108;
            {var subQ0=sQuery(id+"F0.wireOp",EDGE,"E50");var subQ1=sQuery(id+"F0.wireOp",EDGE,"E7");Q108=makeQuery(id+"F3.opFillet","BLEND_EDGE",EDGE,{"blendedFrom":[makeQuery(id+"F1.opExtrude","SWEPT_EDGE",EDGE,{"disambiguationData":[OSD([subQ1,subQ0])]}),makeQuery(id+"F1.opExtrude","CAP_FACE",FACE,{"disambiguationData":[OSD([sQuery(id+"F0.wireOp",EDGE,"E0"),sQuery(id+"F0.wireOp",EDGE,"E1"),sQuery(id+"F0.wireOp",EDGE,"E2"),sQuery(id+"F0.wireOp",EDGE,"E3"),sQuery(id+"F0.wireOp",EDGE,"E4"),sQuery(id+"F0.wireOp",EDGE,"E5"),sQuery(id+"F0.wireOp",EDGE,"E6"),subQ1,sQuery(id+"F0.wireOp",EDGE,"E9.rect.left"),sQuery(id+"F0.wireOp",EDGE,"E9.rect.right"),sQuery(id+"F0.wireOp",EDGE,"E10.rect.bottom"),sQuery(id+"F0.wireOp",EDGE,"E10.rect.top"),sQuery(id+"F0.wireOp",EDGE,"E11.rect.bottom"),sQuery(id+"F0.wireOp",EDGE,"E11.rect.top"),sQuery(id+"F0.wireOp",EDGE,"E12.rect.left"),sQuery(id+"F0.wireOp",EDGE,"E12.rect.right"),sQuery(id+"F0.wireOp",EDGE,"E13.rect.left"),sQuery(id+"F0.wireOp",EDGE,"E13.rect.right"),sQuery(id+"F0.wireOp",EDGE,"E14.left"),sQuery(id+"F0.wireOp",EDGE,"E14.right"),sQuery(id+"F0.wireOp",EDGE,"E15"),sQuery(id+"F0.wireOp",EDGE,"E17"),sQuery(id+"F0.wireOp",EDGE,"E18"),sQuery(id+"F0.wireOp",EDGE,"E20"),sQuery(id+"F0.wireOp",EDGE,"E21.rect.bottom"),sQuery(id+"F0.wireOp",EDGE,"E21.rect.top"),sQuery(id+"F0.wireOp",EDGE,"E22.left"),sQuery(id+"F0.wireOp",EDGE,"E22.right"),sQuery(id+"F0.wireOp",EDGE,"E23.top"),sQuery(id+"F0.wireOp",EDGE,"E23.left"),sQuery(id+"F0.wireOp",EDGE,"E23.right"),sQuery(id+"F0.wireOp",EDGE,"E22.top"),sQuery(id+"F0.wireOp",EDGE,"E26"),sQuery(id+"F0.wireOp",EDGE,"E29"),sQuery(id+"F0.wireOp",EDGE,"E32"),sQuery(id+"F0.wireOp",EDGE,"E35"),sQuery(id+"F0.wireOp",EDGE,"E36"),sQuery(id+"F0.wireOp",EDGE,"E41"),sQuery(id+"F0.wireOp",EDGE,"E44"),sQuery(id+"F0.wireOp",EDGE,"E47"),sQuery(id+"F0.wireOp",EDGE,"E48"),sQuery(id+"F0.wireOp",EDGE,"E49"),subQ0,sQuery(id+"F0.wireOp",EDGE,"E51")])],"isStart":true})],"blendedInto":[makeQuery(id+"F1.opExtrude","CAP_FACE",FACE,{"disambiguationData":[OSD([sQuery(id+"F0.wireOp",EDGE,"E0"),sQuery(id+"F0.wireOp",EDGE,"E1"),sQuery(id+"F0.wireOp",EDGE,"E2"),sQuery(id+"F0.wireOp",EDGE,"E3"),sQuery(id+"F0.wireOp",EDGE,"E4"),sQuery(id+"F0.wireOp",EDGE,"E5"),sQuery(id+"F0.wireOp",EDGE,"E6"),subQ1,sQuery(id+"F0.wireOp",EDGE,"E9.rect.left"),sQuery(id+"F0.wireOp",EDGE,"E9.rect.right"),sQuery(id+"F0.wireOp",EDGE,"E10.rect.bottom"),sQuery(id+"F0.wireOp",EDGE,"E10.rect.top"),sQuery(id+"F0.wireOp",EDGE,"E11.rect.bottom"),sQuery(id+"F0.wireOp",EDGE,"E11.rect.top"),sQuery(id+"F0.wireOp",EDGE,"E12.rect.left"),sQuery(id+"F0.wireOp",EDGE,"E12.rect.right"),sQuery(id+"F0.wireOp",EDGE,"E13.rect.left"),sQuery(id+"F0.wireOp",EDGE,"E13.rect.right"),sQuery(id+"F0.wireOp",EDGE,"E14.left"),sQuery(id+"F0.wireOp",EDGE,"E14.right"),sQuery(id+"F0.wireOp",EDGE,"E15"),sQuery(id+"F0.wireOp",EDGE,"E17"),sQuery(id+"F0.wireOp",EDGE,"E18"),sQuery(id+"F0.wireOp",EDGE,"E20"),sQuery(id+"F0.wireOp",EDGE,"E21.rect.bottom"),sQuery(id+"F0.wireOp",EDGE,"E21.rect.top"),sQuery(id+"F0.wireOp",EDGE,"E22.left"),sQuery(id+"F0.wireOp",EDGE,"E22.right"),sQuery(id+"F0.wireOp",EDGE,"E23.top"),sQuery(id+"F0.wireOp",EDGE,"E23.left"),sQuery(id+"F0.wireOp",EDGE,"E23.right"),sQuery(id+"F0.wireOp",EDGE,"E22.top"),sQuery(id+"F0.wireOp",EDGE,"E26"),sQuery(id+"F0.wireOp",EDGE,"E29"),sQuery(id+"F0.wireOp",EDGE,"E32"),sQuery(id+"F0.wireOp",EDGE,"E35"),sQuery(id+"F0.wireOp",EDGE,"E36"),sQuery(id+"F0.wireOp",EDGE,"E41"),sQuery(id+"F0.wireOp",EDGE,"E44"),sQuery(id+"F0.wireOp",EDGE,"E47"),sQuery(id+"F0.wireOp",EDGE,"E48"),sQuery(id+"F0.wireOp",EDGE,"E49"),subQ0,sQuery(id+"F0.wireOp",EDGE,"E51")])],"isStart":true})]});}
            var Q109;
            {var subQ0=sQuery(id+"F0.wireOp",EDGE,"E35");var subQ1=sQuery(id+"F0.wireOp",EDGE,"E3");Q109=makeQuery(id+"F2.opFillet","BLEND_EDGE",EDGE,{"blendedFrom":[makeQuery(id+"F1.opExtrude","SWEPT_EDGE",EDGE,{"disambiguationData":[OSD([subQ1,subQ0])]}),makeQuery(id+"F1.opExtrude","CAP_FACE",FACE,{"disambiguationData":[OSD([sQuery(id+"F0.wireOp",EDGE,"E0"),sQuery(id+"F0.wireOp",EDGE,"E1"),sQuery(id+"F0.wireOp",EDGE,"E2"),subQ1,sQuery(id+"F0.wireOp",EDGE,"E4"),sQuery(id+"F0.wireOp",EDGE,"E5"),sQuery(id+"F0.wireOp",EDGE,"E6"),sQuery(id+"F0.wireOp",EDGE,"E7"),sQuery(id+"F0.wireOp",EDGE,"E9.rect.left"),sQuery(id+"F0.wireOp",EDGE,"E9.rect.right"),sQuery(id+"F0.wireOp",EDGE,"E10.rect.bottom"),sQuery(id+"F0.wireOp",EDGE,"E10.rect.top"),sQuery(id+"F0.wireOp",EDGE,"E11.rect.bottom"),sQuery(id+"F0.wireOp",EDGE,"E11.rect.top"),sQuery(id+"F0.wireOp",EDGE,"E12.rect.left"),sQuery(id+"F0.wireOp",EDGE,"E12.rect.right"),sQuery(id+"F0.wireOp",EDGE,"E13.rect.left"),sQuery(id+"F0.wireOp",EDGE,"E13.rect.right"),sQuery(id+"F0.wireOp",EDGE,"E14.left"),sQuery(id+"F0.wireOp",EDGE,"E14.right"),sQuery(id+"F0.wireOp",EDGE,"E15"),sQuery(id+"F0.wireOp",EDGE,"E17"),sQuery(id+"F0.wireOp",EDGE,"E18"),sQuery(id+"F0.wireOp",EDGE,"E20"),sQuery(id+"F0.wireOp",EDGE,"E21.rect.bottom"),sQuery(id+"F0.wireOp",EDGE,"E21.rect.top"),sQuery(id+"F0.wireOp",EDGE,"E22.left"),sQuery(id+"F0.wireOp",EDGE,"E22.right"),sQuery(id+"F0.wireOp",EDGE,"E23.top"),sQuery(id+"F0.wireOp",EDGE,"E23.left"),sQuery(id+"F0.wireOp",EDGE,"E23.right"),sQuery(id+"F0.wireOp",EDGE,"E22.top"),sQuery(id+"F0.wireOp",EDGE,"E26"),sQuery(id+"F0.wireOp",EDGE,"E29"),sQuery(id+"F0.wireOp",EDGE,"E32"),subQ0,sQuery(id+"F0.wireOp",EDGE,"E36"),sQuery(id+"F0.wireOp",EDGE,"E41"),sQuery(id+"F0.wireOp",EDGE,"E44"),sQuery(id+"F0.wireOp",EDGE,"E47"),sQuery(id+"F0.wireOp",EDGE,"E48"),sQuery(id+"F0.wireOp",EDGE,"E49"),sQuery(id+"F0.wireOp",EDGE,"E50"),sQuery(id+"F0.wireOp",EDGE,"E51")])],"isStart":true})],"blendedInto":[makeQuery(id+"F1.opExtrude","CAP_FACE",FACE,{"disambiguationData":[OSD([sQuery(id+"F0.wireOp",EDGE,"E0"),sQuery(id+"F0.wireOp",EDGE,"E1"),sQuery(id+"F0.wireOp",EDGE,"E2"),subQ1,sQuery(id+"F0.wireOp",EDGE,"E4"),sQuery(id+"F0.wireOp",EDGE,"E5"),sQuery(id+"F0.wireOp",EDGE,"E6"),sQuery(id+"F0.wireOp",EDGE,"E7"),sQuery(id+"F0.wireOp",EDGE,"E9.rect.left"),sQuery(id+"F0.wireOp",EDGE,"E9.rect.right"),sQuery(id+"F0.wireOp",EDGE,"E10.rect.bottom"),sQuery(id+"F0.wireOp",EDGE,"E10.rect.top"),sQuery(id+"F0.wireOp",EDGE,"E11.rect.bottom"),sQuery(id+"F0.wireOp",EDGE,"E11.rect.top"),sQuery(id+"F0.wireOp",EDGE,"E12.rect.left"),sQuery(id+"F0.wireOp",EDGE,"E12.rect.right"),sQuery(id+"F0.wireOp",EDGE,"E13.rect.left"),sQuery(id+"F0.wireOp",EDGE,"E13.rect.right"),sQuery(id+"F0.wireOp",EDGE,"E14.left"),sQuery(id+"F0.wireOp",EDGE,"E14.right"),sQuery(id+"F0.wireOp",EDGE,"E15"),sQuery(id+"F0.wireOp",EDGE,"E17"),sQuery(id+"F0.wireOp",EDGE,"E18"),sQuery(id+"F0.wireOp",EDGE,"E20"),sQuery(id+"F0.wireOp",EDGE,"E21.rect.bottom"),sQuery(id+"F0.wireOp",EDGE,"E21.rect.top"),sQuery(id+"F0.wireOp",EDGE,"E22.left"),sQuery(id+"F0.wireOp",EDGE,"E22.right"),sQuery(id+"F0.wireOp",EDGE,"E23.top"),sQuery(id+"F0.wireOp",EDGE,"E23.left"),sQuery(id+"F0.wireOp",EDGE,"E23.right"),sQuery(id+"F0.wireOp",EDGE,"E22.top"),sQuery(id+"F0.wireOp",EDGE,"E26"),sQuery(id+"F0.wireOp",EDGE,"E29"),sQuery(id+"F0.wireOp",EDGE,"E32"),subQ0,sQuery(id+"F0.wireOp",EDGE,"E36"),sQuery(id+"F0.wireOp",EDGE,"E41"),sQuery(id+"F0.wireOp",EDGE,"E44"),sQuery(id+"F0.wireOp",EDGE,"E47"),sQuery(id+"F0.wireOp",EDGE,"E48"),sQuery(id+"F0.wireOp",EDGE,"E49"),sQuery(id+"F0.wireOp",EDGE,"E50"),sQuery(id+"F0.wireOp",EDGE,"E51")])],"isStart":true})]});}
            var Q110;
            Q110=makeQuery(id+"F1.opExtrude","CAP_EDGE",EDGE,{"disambiguationData":[OSD([sQuery(id+"F0.wireOp",EDGE,"E36")])],"isStart":true});
            var Q111;
            {var subQ0=sQuery(id+"F0.wireOp",EDGE,"E36");var subQ1=sQuery(id+"F0.wireOp",EDGE,"E12.rect.right");var subQ2=sQuery(id+"F0.wireOp",EDGE,"E10.rect.top");Q111=makeQuery(id+"F4.opFillet","BLEND_EDGE",EDGE,{"blendedFrom":[makeQuery(id+"F1.opExtrude","SWEPT_EDGE",EDGE,{"disambiguationData":[OSD([subQ2,subQ1,subQ0])]}),makeQuery(id+"F1.opExtrude","CAP_FACE",FACE,{"disambiguationData":[OSD([sQuery(id+"F0.wireOp",EDGE,"E0"),sQuery(id+"F0.wireOp",EDGE,"E1"),sQuery(id+"F0.wireOp",EDGE,"E2"),sQuery(id+"F0.wireOp",EDGE,"E3"),sQuery(id+"F0.wireOp",EDGE,"E4"),sQuery(id+"F0.wireOp",EDGE,"E5"),sQuery(id+"F0.wireOp",EDGE,"E6"),sQuery(id+"F0.wireOp",EDGE,"E7"),sQuery(id+"F0.wireOp",EDGE,"E9.rect.left"),sQuery(id+"F0.wireOp",EDGE,"E9.rect.right"),sQuery(id+"F0.wireOp",EDGE,"E10.rect.bottom"),subQ2,sQuery(id+"F0.wireOp",EDGE,"E11.rect.bottom"),sQuery(id+"F0.wireOp",EDGE,"E11.rect.top"),sQuery(id+"F0.wireOp",EDGE,"E12.rect.left"),subQ1,sQuery(id+"F0.wireOp",EDGE,"E13.rect.left"),sQuery(id+"F0.wireOp",EDGE,"E13.rect.right"),sQuery(id+"F0.wireOp",EDGE,"E14.left"),sQuery(id+"F0.wireOp",EDGE,"E14.right"),sQuery(id+"F0.wireOp",EDGE,"E15"),sQuery(id+"F0.wireOp",EDGE,"E17"),sQuery(id+"F0.wireOp",EDGE,"E18"),sQuery(id+"F0.wireOp",EDGE,"E20"),sQuery(id+"F0.wireOp",EDGE,"E21.rect.bottom"),sQuery(id+"F0.wireOp",EDGE,"E21.rect.top"),sQuery(id+"F0.wireOp",EDGE,"E22.left"),sQuery(id+"F0.wireOp",EDGE,"E22.right"),sQuery(id+"F0.wireOp",EDGE,"E23.top"),sQuery(id+"F0.wireOp",EDGE,"E23.left"),sQuery(id+"F0.wireOp",EDGE,"E23.right"),sQuery(id+"F0.wireOp",EDGE,"E22.top"),sQuery(id+"F0.wireOp",EDGE,"E26"),sQuery(id+"F0.wireOp",EDGE,"E29"),sQuery(id+"F0.wireOp",EDGE,"E32"),sQuery(id+"F0.wireOp",EDGE,"E35"),subQ0,sQuery(id+"F0.wireOp",EDGE,"E41"),sQuery(id+"F0.wireOp",EDGE,"E44"),sQuery(id+"F0.wireOp",EDGE,"E47"),sQuery(id+"F0.wireOp",EDGE,"E48"),sQuery(id+"F0.wireOp",EDGE,"E49"),sQuery(id+"F0.wireOp",EDGE,"E50"),sQuery(id+"F0.wireOp",EDGE,"E51")])],"isStart":true})],"blendedInto":[makeQuery(id+"F1.opExtrude","CAP_FACE",FACE,{"disambiguationData":[OSD([sQuery(id+"F0.wireOp",EDGE,"E0"),sQuery(id+"F0.wireOp",EDGE,"E1"),sQuery(id+"F0.wireOp",EDGE,"E2"),sQuery(id+"F0.wireOp",EDGE,"E3"),sQuery(id+"F0.wireOp",EDGE,"E4"),sQuery(id+"F0.wireOp",EDGE,"E5"),sQuery(id+"F0.wireOp",EDGE,"E6"),sQuery(id+"F0.wireOp",EDGE,"E7"),sQuery(id+"F0.wireOp",EDGE,"E9.rect.left"),sQuery(id+"F0.wireOp",EDGE,"E9.rect.right"),sQuery(id+"F0.wireOp",EDGE,"E10.rect.bottom"),subQ2,sQuery(id+"F0.wireOp",EDGE,"E11.rect.bottom"),sQuery(id+"F0.wireOp",EDGE,"E11.rect.top"),sQuery(id+"F0.wireOp",EDGE,"E12.rect.left"),subQ1,sQuery(id+"F0.wireOp",EDGE,"E13.rect.left"),sQuery(id+"F0.wireOp",EDGE,"E13.rect.right"),sQuery(id+"F0.wireOp",EDGE,"E14.left"),sQuery(id+"F0.wireOp",EDGE,"E14.right"),sQuery(id+"F0.wireOp",EDGE,"E15"),sQuery(id+"F0.wireOp",EDGE,"E17"),sQuery(id+"F0.wireOp",EDGE,"E18"),sQuery(id+"F0.wireOp",EDGE,"E20"),sQuery(id+"F0.wireOp",EDGE,"E21.rect.bottom"),sQuery(id+"F0.wireOp",EDGE,"E21.rect.top"),sQuery(id+"F0.wireOp",EDGE,"E22.left"),sQuery(id+"F0.wireOp",EDGE,"E22.right"),sQuery(id+"F0.wireOp",EDGE,"E23.top"),sQuery(id+"F0.wireOp",EDGE,"E23.left"),sQuery(id+"F0.wireOp",EDGE,"E23.right"),sQuery(id+"F0.wireOp",EDGE,"E22.top"),sQuery(id+"F0.wireOp",EDGE,"E26"),sQuery(id+"F0.wireOp",EDGE,"E29"),sQuery(id+"F0.wireOp",EDGE,"E32"),sQuery(id+"F0.wireOp",EDGE,"E35"),subQ0,sQuery(id+"F0.wireOp",EDGE,"E41"),sQuery(id+"F0.wireOp",EDGE,"E44"),sQuery(id+"F0.wireOp",EDGE,"E47"),sQuery(id+"F0.wireOp",EDGE,"E48"),sQuery(id+"F0.wireOp",EDGE,"E49"),sQuery(id+"F0.wireOp",EDGE,"E50"),sQuery(id+"F0.wireOp",EDGE,"E51")])],"isStart":true})]});}
            var Q112;
            Q112=makeQuery(id+"F1.opExtrude","CAP_EDGE",EDGE,{"disambiguationData":[OSD([sQuery(id+"F0.wireOp",EDGE,"E3")])],"isStart":true});
            var Q113;
            {var subQ0=sQuery(id+"F0.wireOp",EDGE,"E9.rect.right");var subQ1=sQuery(id+"F0.wireOp",EDGE,"E3");Q113=makeQuery(id+"F3.opFillet","BLEND_EDGE",EDGE,{"blendedFrom":[makeQuery(id+"F1.opExtrude","SWEPT_EDGE",EDGE,{"disambiguationData":[OSD([subQ1,subQ0])]}),makeQuery(id+"F1.opExtrude","CAP_FACE",FACE,{"disambiguationData":[OSD([sQuery(id+"F0.wireOp",EDGE,"E0"),sQuery(id+"F0.wireOp",EDGE,"E1"),sQuery(id+"F0.wireOp",EDGE,"E2"),subQ1,sQuery(id+"F0.wireOp",EDGE,"E4"),sQuery(id+"F0.wireOp",EDGE,"E5"),sQuery(id+"F0.wireOp",EDGE,"E6"),sQuery(id+"F0.wireOp",EDGE,"E7"),sQuery(id+"F0.wireOp",EDGE,"E9.rect.left"),subQ0,sQuery(id+"F0.wireOp",EDGE,"E10.rect.bottom"),sQuery(id+"F0.wireOp",EDGE,"E10.rect.top"),sQuery(id+"F0.wireOp",EDGE,"E11.rect.bottom"),sQuery(id+"F0.wireOp",EDGE,"E11.rect.top"),sQuery(id+"F0.wireOp",EDGE,"E12.rect.left"),sQuery(id+"F0.wireOp",EDGE,"E12.rect.right"),sQuery(id+"F0.wireOp",EDGE,"E13.rect.left"),sQuery(id+"F0.wireOp",EDGE,"E13.rect.right"),sQuery(id+"F0.wireOp",EDGE,"E14.left"),sQuery(id+"F0.wireOp",EDGE,"E14.right"),sQuery(id+"F0.wireOp",EDGE,"E15"),sQuery(id+"F0.wireOp",EDGE,"E17"),sQuery(id+"F0.wireOp",EDGE,"E18"),sQuery(id+"F0.wireOp",EDGE,"E20"),sQuery(id+"F0.wireOp",EDGE,"E21.rect.bottom"),sQuery(id+"F0.wireOp",EDGE,"E21.rect.top"),sQuery(id+"F0.wireOp",EDGE,"E22.left"),sQuery(id+"F0.wireOp",EDGE,"E22.right"),sQuery(id+"F0.wireOp",EDGE,"E23.top"),sQuery(id+"F0.wireOp",EDGE,"E23.left"),sQuery(id+"F0.wireOp",EDGE,"E23.right"),sQuery(id+"F0.wireOp",EDGE,"E22.top"),sQuery(id+"F0.wireOp",EDGE,"E26"),sQuery(id+"F0.wireOp",EDGE,"E29"),sQuery(id+"F0.wireOp",EDGE,"E32"),sQuery(id+"F0.wireOp",EDGE,"E35"),sQuery(id+"F0.wireOp",EDGE,"E36"),sQuery(id+"F0.wireOp",EDGE,"E41"),sQuery(id+"F0.wireOp",EDGE,"E44"),sQuery(id+"F0.wireOp",EDGE,"E47"),sQuery(id+"F0.wireOp",EDGE,"E48"),sQuery(id+"F0.wireOp",EDGE,"E49"),sQuery(id+"F0.wireOp",EDGE,"E50"),sQuery(id+"F0.wireOp",EDGE,"E51")])],"isStart":true})],"blendedInto":[makeQuery(id+"F1.opExtrude","CAP_FACE",FACE,{"disambiguationData":[OSD([sQuery(id+"F0.wireOp",EDGE,"E0"),sQuery(id+"F0.wireOp",EDGE,"E1"),sQuery(id+"F0.wireOp",EDGE,"E2"),subQ1,sQuery(id+"F0.wireOp",EDGE,"E4"),sQuery(id+"F0.wireOp",EDGE,"E5"),sQuery(id+"F0.wireOp",EDGE,"E6"),sQuery(id+"F0.wireOp",EDGE,"E7"),sQuery(id+"F0.wireOp",EDGE,"E9.rect.left"),subQ0,sQuery(id+"F0.wireOp",EDGE,"E10.rect.bottom"),sQuery(id+"F0.wireOp",EDGE,"E10.rect.top"),sQuery(id+"F0.wireOp",EDGE,"E11.rect.bottom"),sQuery(id+"F0.wireOp",EDGE,"E11.rect.top"),sQuery(id+"F0.wireOp",EDGE,"E12.rect.left"),sQuery(id+"F0.wireOp",EDGE,"E12.rect.right"),sQuery(id+"F0.wireOp",EDGE,"E13.rect.left"),sQuery(id+"F0.wireOp",EDGE,"E13.rect.right"),sQuery(id+"F0.wireOp",EDGE,"E14.left"),sQuery(id+"F0.wireOp",EDGE,"E14.right"),sQuery(id+"F0.wireOp",EDGE,"E15"),sQuery(id+"F0.wireOp",EDGE,"E17"),sQuery(id+"F0.wireOp",EDGE,"E18"),sQuery(id+"F0.wireOp",EDGE,"E20"),sQuery(id+"F0.wireOp",EDGE,"E21.rect.bottom"),sQuery(id+"F0.wireOp",EDGE,"E21.rect.top"),sQuery(id+"F0.wireOp",EDGE,"E22.left"),sQuery(id+"F0.wireOp",EDGE,"E22.right"),sQuery(id+"F0.wireOp",EDGE,"E23.top"),sQuery(id+"F0.wireOp",EDGE,"E23.left"),sQuery(id+"F0.wireOp",EDGE,"E23.right"),sQuery(id+"F0.wireOp",EDGE,"E22.top"),sQuery(id+"F0.wireOp",EDGE,"E26"),sQuery(id+"F0.wireOp",EDGE,"E29"),sQuery(id+"F0.wireOp",EDGE,"E32"),sQuery(id+"F0.wireOp",EDGE,"E35"),sQuery(id+"F0.wireOp",EDGE,"E36"),sQuery(id+"F0.wireOp",EDGE,"E41"),sQuery(id+"F0.wireOp",EDGE,"E44"),sQuery(id+"F0.wireOp",EDGE,"E47"),sQuery(id+"F0.wireOp",EDGE,"E48"),sQuery(id+"F0.wireOp",EDGE,"E49"),sQuery(id+"F0.wireOp",EDGE,"E50"),sQuery(id+"F0.wireOp",EDGE,"E51")])],"isStart":true})]});}
            var Q114;
            {var subQ0=sQuery(id+"F0.wireOp",EDGE,"E12.rect.left");var subQ1=sQuery(id+"F0.wireOp",EDGE,"E11.rect.top");Q114=makeQuery(id+"F4.opFillet","BLEND_EDGE",EDGE,{"blendedFrom":[makeQuery(id+"F1.opExtrude","SWEPT_EDGE",EDGE,{"disambiguationData":[OSD([subQ1,subQ0])]}),makeQuery(id+"F1.opExtrude","CAP_FACE",FACE,{"disambiguationData":[OSD([sQuery(id+"F0.wireOp",EDGE,"E0"),sQuery(id+"F0.wireOp",EDGE,"E1"),sQuery(id+"F0.wireOp",EDGE,"E2"),sQuery(id+"F0.wireOp",EDGE,"E3"),sQuery(id+"F0.wireOp",EDGE,"E4"),sQuery(id+"F0.wireOp",EDGE,"E5"),sQuery(id+"F0.wireOp",EDGE,"E6"),sQuery(id+"F0.wireOp",EDGE,"E7"),sQuery(id+"F0.wireOp",EDGE,"E9.rect.left"),sQuery(id+"F0.wireOp",EDGE,"E9.rect.right"),sQuery(id+"F0.wireOp",EDGE,"E10.rect.bottom"),sQuery(id+"F0.wireOp",EDGE,"E10.rect.top"),sQuery(id+"F0.wireOp",EDGE,"E11.rect.bottom"),subQ1,subQ0,sQuery(id+"F0.wireOp",EDGE,"E12.rect.right"),sQuery(id+"F0.wireOp",EDGE,"E13.rect.left"),sQuery(id+"F0.wireOp",EDGE,"E13.rect.right"),sQuery(id+"F0.wireOp",EDGE,"E14.left"),sQuery(id+"F0.wireOp",EDGE,"E14.right"),sQuery(id+"F0.wireOp",EDGE,"E15"),sQuery(id+"F0.wireOp",EDGE,"E17"),sQuery(id+"F0.wireOp",EDGE,"E18"),sQuery(id+"F0.wireOp",EDGE,"E20"),sQuery(id+"F0.wireOp",EDGE,"E21.rect.bottom"),sQuery(id+"F0.wireOp",EDGE,"E21.rect.top"),sQuery(id+"F0.wireOp",EDGE,"E22.left"),sQuery(id+"F0.wireOp",EDGE,"E22.right"),sQuery(id+"F0.wireOp",EDGE,"E23.top"),sQuery(id+"F0.wireOp",EDGE,"E23.left"),sQuery(id+"F0.wireOp",EDGE,"E23.right"),sQuery(id+"F0.wireOp",EDGE,"E22.top"),sQuery(id+"F0.wireOp",EDGE,"E26"),sQuery(id+"F0.wireOp",EDGE,"E29"),sQuery(id+"F0.wireOp",EDGE,"E32"),sQuery(id+"F0.wireOp",EDGE,"E35"),sQuery(id+"F0.wireOp",EDGE,"E36"),sQuery(id+"F0.wireOp",EDGE,"E41"),sQuery(id+"F0.wireOp",EDGE,"E44"),sQuery(id+"F0.wireOp",EDGE,"E47"),sQuery(id+"F0.wireOp",EDGE,"E48"),sQuery(id+"F0.wireOp",EDGE,"E49"),sQuery(id+"F0.wireOp",EDGE,"E50"),sQuery(id+"F0.wireOp",EDGE,"E51")])],"isStart":true})],"blendedInto":[makeQuery(id+"F1.opExtrude","CAP_FACE",FACE,{"disambiguationData":[OSD([sQuery(id+"F0.wireOp",EDGE,"E0"),sQuery(id+"F0.wireOp",EDGE,"E1"),sQuery(id+"F0.wireOp",EDGE,"E2"),sQuery(id+"F0.wireOp",EDGE,"E3"),sQuery(id+"F0.wireOp",EDGE,"E4"),sQuery(id+"F0.wireOp",EDGE,"E5"),sQuery(id+"F0.wireOp",EDGE,"E6"),sQuery(id+"F0.wireOp",EDGE,"E7"),sQuery(id+"F0.wireOp",EDGE,"E9.rect.left"),sQuery(id+"F0.wireOp",EDGE,"E9.rect.right"),sQuery(id+"F0.wireOp",EDGE,"E10.rect.bottom"),sQuery(id+"F0.wireOp",EDGE,"E10.rect.top"),sQuery(id+"F0.wireOp",EDGE,"E11.rect.bottom"),subQ1,subQ0,sQuery(id+"F0.wireOp",EDGE,"E12.rect.right"),sQuery(id+"F0.wireOp",EDGE,"E13.rect.left"),sQuery(id+"F0.wireOp",EDGE,"E13.rect.right"),sQuery(id+"F0.wireOp",EDGE,"E14.left"),sQuery(id+"F0.wireOp",EDGE,"E14.right"),sQuery(id+"F0.wireOp",EDGE,"E15"),sQuery(id+"F0.wireOp",EDGE,"E17"),sQuery(id+"F0.wireOp",EDGE,"E18"),sQuery(id+"F0.wireOp",EDGE,"E20"),sQuery(id+"F0.wireOp",EDGE,"E21.rect.bottom"),sQuery(id+"F0.wireOp",EDGE,"E21.rect.top"),sQuery(id+"F0.wireOp",EDGE,"E22.left"),sQuery(id+"F0.wireOp",EDGE,"E22.right"),sQuery(id+"F0.wireOp",EDGE,"E23.top"),sQuery(id+"F0.wireOp",EDGE,"E23.left"),sQuery(id+"F0.wireOp",EDGE,"E23.right"),sQuery(id+"F0.wireOp",EDGE,"E22.top"),sQuery(id+"F0.wireOp",EDGE,"E26"),sQuery(id+"F0.wireOp",EDGE,"E29"),sQuery(id+"F0.wireOp",EDGE,"E32"),sQuery(id+"F0.wireOp",EDGE,"E35"),sQuery(id+"F0.wireOp",EDGE,"E36"),sQuery(id+"F0.wireOp",EDGE,"E41"),sQuery(id+"F0.wireOp",EDGE,"E44"),sQuery(id+"F0.wireOp",EDGE,"E47"),sQuery(id+"F0.wireOp",EDGE,"E48"),sQuery(id+"F0.wireOp",EDGE,"E49"),sQuery(id+"F0.wireOp",EDGE,"E50"),sQuery(id+"F0.wireOp",EDGE,"E51")])],"isStart":true})]});}
            var Q115;
            Q115=makeQuery(id+"F1.opExtrude","CAP_EDGE",EDGE,{"disambiguationData":[OSD([sQuery(id+"F0.wireOp",EDGE,"E12.rect.left")])],"isStart":true});
            var Q116;
            Q116=makeQuery(id+"F1.opExtrude","CAP_EDGE",EDGE,{"disambiguationData":[OSD([sQuery(id+"F0.wireOp",EDGE,"E11.rect.top"),sQuery(id+"F0.wireOp",EDGE,"E21.rect.top")])],"isStart":true});
            var Q117;
            {var subQ0=sQuery(id+"F0.wireOp",EDGE,"E12.rect.right");var subQ1=sQuery(id+"F0.wireOp",EDGE,"E11.rect.top");Q117=makeQuery(id+"F4.opFillet","BLEND_EDGE",EDGE,{"blendedFrom":[makeQuery(id+"F1.opExtrude","SWEPT_EDGE",EDGE,{"disambiguationData":[OSD([subQ1,subQ0])]}),makeQuery(id+"F1.opExtrude","CAP_FACE",FACE,{"disambiguationData":[OSD([sQuery(id+"F0.wireOp",EDGE,"E0"),sQuery(id+"F0.wireOp",EDGE,"E1"),sQuery(id+"F0.wireOp",EDGE,"E2"),sQuery(id+"F0.wireOp",EDGE,"E3"),sQuery(id+"F0.wireOp",EDGE,"E4"),sQuery(id+"F0.wireOp",EDGE,"E5"),sQuery(id+"F0.wireOp",EDGE,"E6"),sQuery(id+"F0.wireOp",EDGE,"E7"),sQuery(id+"F0.wireOp",EDGE,"E9.rect.left"),sQuery(id+"F0.wireOp",EDGE,"E9.rect.right"),sQuery(id+"F0.wireOp",EDGE,"E10.rect.bottom"),sQuery(id+"F0.wireOp",EDGE,"E10.rect.top"),sQuery(id+"F0.wireOp",EDGE,"E11.rect.bottom"),subQ1,sQuery(id+"F0.wireOp",EDGE,"E12.rect.left"),subQ0,sQuery(id+"F0.wireOp",EDGE,"E13.rect.left"),sQuery(id+"F0.wireOp",EDGE,"E13.rect.right"),sQuery(id+"F0.wireOp",EDGE,"E14.left"),sQuery(id+"F0.wireOp",EDGE,"E14.right"),sQuery(id+"F0.wireOp",EDGE,"E15"),sQuery(id+"F0.wireOp",EDGE,"E17"),sQuery(id+"F0.wireOp",EDGE,"E18"),sQuery(id+"F0.wireOp",EDGE,"E20"),sQuery(id+"F0.wireOp",EDGE,"E21.rect.bottom"),sQuery(id+"F0.wireOp",EDGE,"E21.rect.top"),sQuery(id+"F0.wireOp",EDGE,"E22.left"),sQuery(id+"F0.wireOp",EDGE,"E22.right"),sQuery(id+"F0.wireOp",EDGE,"E23.top"),sQuery(id+"F0.wireOp",EDGE,"E23.left"),sQuery(id+"F0.wireOp",EDGE,"E23.right"),sQuery(id+"F0.wireOp",EDGE,"E22.top"),sQuery(id+"F0.wireOp",EDGE,"E26"),sQuery(id+"F0.wireOp",EDGE,"E29"),sQuery(id+"F0.wireOp",EDGE,"E32"),sQuery(id+"F0.wireOp",EDGE,"E35"),sQuery(id+"F0.wireOp",EDGE,"E36"),sQuery(id+"F0.wireOp",EDGE,"E41"),sQuery(id+"F0.wireOp",EDGE,"E44"),sQuery(id+"F0.wireOp",EDGE,"E47"),sQuery(id+"F0.wireOp",EDGE,"E48"),sQuery(id+"F0.wireOp",EDGE,"E49"),sQuery(id+"F0.wireOp",EDGE,"E50"),sQuery(id+"F0.wireOp",EDGE,"E51")])],"isStart":true})],"blendedInto":[makeQuery(id+"F1.opExtrude","CAP_FACE",FACE,{"disambiguationData":[OSD([sQuery(id+"F0.wireOp",EDGE,"E0"),sQuery(id+"F0.wireOp",EDGE,"E1"),sQuery(id+"F0.wireOp",EDGE,"E2"),sQuery(id+"F0.wireOp",EDGE,"E3"),sQuery(id+"F0.wireOp",EDGE,"E4"),sQuery(id+"F0.wireOp",EDGE,"E5"),sQuery(id+"F0.wireOp",EDGE,"E6"),sQuery(id+"F0.wireOp",EDGE,"E7"),sQuery(id+"F0.wireOp",EDGE,"E9.rect.left"),sQuery(id+"F0.wireOp",EDGE,"E9.rect.right"),sQuery(id+"F0.wireOp",EDGE,"E10.rect.bottom"),sQuery(id+"F0.wireOp",EDGE,"E10.rect.top"),sQuery(id+"F0.wireOp",EDGE,"E11.rect.bottom"),subQ1,sQuery(id+"F0.wireOp",EDGE,"E12.rect.left"),subQ0,sQuery(id+"F0.wireOp",EDGE,"E13.rect.left"),sQuery(id+"F0.wireOp",EDGE,"E13.rect.right"),sQuery(id+"F0.wireOp",EDGE,"E14.left"),sQuery(id+"F0.wireOp",EDGE,"E14.right"),sQuery(id+"F0.wireOp",EDGE,"E15"),sQuery(id+"F0.wireOp",EDGE,"E17"),sQuery(id+"F0.wireOp",EDGE,"E18"),sQuery(id+"F0.wireOp",EDGE,"E20"),sQuery(id+"F0.wireOp",EDGE,"E21.rect.bottom"),sQuery(id+"F0.wireOp",EDGE,"E21.rect.top"),sQuery(id+"F0.wireOp",EDGE,"E22.left"),sQuery(id+"F0.wireOp",EDGE,"E22.right"),sQuery(id+"F0.wireOp",EDGE,"E23.top"),sQuery(id+"F0.wireOp",EDGE,"E23.left"),sQuery(id+"F0.wireOp",EDGE,"E23.right"),sQuery(id+"F0.wireOp",EDGE,"E22.top"),sQuery(id+"F0.wireOp",EDGE,"E26"),sQuery(id+"F0.wireOp",EDGE,"E29"),sQuery(id+"F0.wireOp",EDGE,"E32"),sQuery(id+"F0.wireOp",EDGE,"E35"),sQuery(id+"F0.wireOp",EDGE,"E36"),sQuery(id+"F0.wireOp",EDGE,"E41"),sQuery(id+"F0.wireOp",EDGE,"E44"),sQuery(id+"F0.wireOp",EDGE,"E47"),sQuery(id+"F0.wireOp",EDGE,"E48"),sQuery(id+"F0.wireOp",EDGE,"E49"),sQuery(id+"F0.wireOp",EDGE,"E50"),sQuery(id+"F0.wireOp",EDGE,"E51")])],"isStart":true})]});}
            var Q118;
            Q118=makeQuery(id+"F1.opExtrude","CAP_EDGE",EDGE,{"disambiguationData":[OSD([sQuery(id+"F0.wireOp",EDGE,"E12.rect.right")])],"isStart":true});
            var Q119;
            {var subQ0=sQuery(id+"F0.wireOp",EDGE,"E12.rect.right");var subQ1=sQuery(id+"F0.wireOp",EDGE,"E11.rect.bottom");Q119=makeQuery(id+"F4.opFillet","BLEND_EDGE",EDGE,{"blendedFrom":[makeQuery(id+"F1.opExtrude","SWEPT_EDGE",EDGE,{"disambiguationData":[OSD([subQ1,subQ0])]}),makeQuery(id+"F1.opExtrude","CAP_FACE",FACE,{"disambiguationData":[OSD([sQuery(id+"F0.wireOp",EDGE,"E0"),sQuery(id+"F0.wireOp",EDGE,"E1"),sQuery(id+"F0.wireOp",EDGE,"E2"),sQuery(id+"F0.wireOp",EDGE,"E3"),sQuery(id+"F0.wireOp",EDGE,"E4"),sQuery(id+"F0.wireOp",EDGE,"E5"),sQuery(id+"F0.wireOp",EDGE,"E6"),sQuery(id+"F0.wireOp",EDGE,"E7"),sQuery(id+"F0.wireOp",EDGE,"E9.rect.left"),sQuery(id+"F0.wireOp",EDGE,"E9.rect.right"),sQuery(id+"F0.wireOp",EDGE,"E10.rect.bottom"),sQuery(id+"F0.wireOp",EDGE,"E10.rect.top"),subQ1,sQuery(id+"F0.wireOp",EDGE,"E11.rect.top"),sQuery(id+"F0.wireOp",EDGE,"E12.rect.left"),subQ0,sQuery(id+"F0.wireOp",EDGE,"E13.rect.left"),sQuery(id+"F0.wireOp",EDGE,"E13.rect.right"),sQuery(id+"F0.wireOp",EDGE,"E14.left"),sQuery(id+"F0.wireOp",EDGE,"E14.right"),sQuery(id+"F0.wireOp",EDGE,"E15"),sQuery(id+"F0.wireOp",EDGE,"E17"),sQuery(id+"F0.wireOp",EDGE,"E18"),sQuery(id+"F0.wireOp",EDGE,"E20"),sQuery(id+"F0.wireOp",EDGE,"E21.rect.bottom"),sQuery(id+"F0.wireOp",EDGE,"E21.rect.top"),sQuery(id+"F0.wireOp",EDGE,"E22.left"),sQuery(id+"F0.wireOp",EDGE,"E22.right"),sQuery(id+"F0.wireOp",EDGE,"E23.top"),sQuery(id+"F0.wireOp",EDGE,"E23.left"),sQuery(id+"F0.wireOp",EDGE,"E23.right"),sQuery(id+"F0.wireOp",EDGE,"E22.top"),sQuery(id+"F0.wireOp",EDGE,"E26"),sQuery(id+"F0.wireOp",EDGE,"E29"),sQuery(id+"F0.wireOp",EDGE,"E32"),sQuery(id+"F0.wireOp",EDGE,"E35"),sQuery(id+"F0.wireOp",EDGE,"E36"),sQuery(id+"F0.wireOp",EDGE,"E41"),sQuery(id+"F0.wireOp",EDGE,"E44"),sQuery(id+"F0.wireOp",EDGE,"E47"),sQuery(id+"F0.wireOp",EDGE,"E48"),sQuery(id+"F0.wireOp",EDGE,"E49"),sQuery(id+"F0.wireOp",EDGE,"E50"),sQuery(id+"F0.wireOp",EDGE,"E51")])],"isStart":true})],"blendedInto":[makeQuery(id+"F1.opExtrude","CAP_FACE",FACE,{"disambiguationData":[OSD([sQuery(id+"F0.wireOp",EDGE,"E0"),sQuery(id+"F0.wireOp",EDGE,"E1"),sQuery(id+"F0.wireOp",EDGE,"E2"),sQuery(id+"F0.wireOp",EDGE,"E3"),sQuery(id+"F0.wireOp",EDGE,"E4"),sQuery(id+"F0.wireOp",EDGE,"E5"),sQuery(id+"F0.wireOp",EDGE,"E6"),sQuery(id+"F0.wireOp",EDGE,"E7"),sQuery(id+"F0.wireOp",EDGE,"E9.rect.left"),sQuery(id+"F0.wireOp",EDGE,"E9.rect.right"),sQuery(id+"F0.wireOp",EDGE,"E10.rect.bottom"),sQuery(id+"F0.wireOp",EDGE,"E10.rect.top"),subQ1,sQuery(id+"F0.wireOp",EDGE,"E11.rect.top"),sQuery(id+"F0.wireOp",EDGE,"E12.rect.left"),subQ0,sQuery(id+"F0.wireOp",EDGE,"E13.rect.left"),sQuery(id+"F0.wireOp",EDGE,"E13.rect.right"),sQuery(id+"F0.wireOp",EDGE,"E14.left"),sQuery(id+"F0.wireOp",EDGE,"E14.right"),sQuery(id+"F0.wireOp",EDGE,"E15"),sQuery(id+"F0.wireOp",EDGE,"E17"),sQuery(id+"F0.wireOp",EDGE,"E18"),sQuery(id+"F0.wireOp",EDGE,"E20"),sQuery(id+"F0.wireOp",EDGE,"E21.rect.bottom"),sQuery(id+"F0.wireOp",EDGE,"E21.rect.top"),sQuery(id+"F0.wireOp",EDGE,"E22.left"),sQuery(id+"F0.wireOp",EDGE,"E22.right"),sQuery(id+"F0.wireOp",EDGE,"E23.top"),sQuery(id+"F0.wireOp",EDGE,"E23.left"),sQuery(id+"F0.wireOp",EDGE,"E23.right"),sQuery(id+"F0.wireOp",EDGE,"E22.top"),sQuery(id+"F0.wireOp",EDGE,"E26"),sQuery(id+"F0.wireOp",EDGE,"E29"),sQuery(id+"F0.wireOp",EDGE,"E32"),sQuery(id+"F0.wireOp",EDGE,"E35"),sQuery(id+"F0.wireOp",EDGE,"E36"),sQuery(id+"F0.wireOp",EDGE,"E41"),sQuery(id+"F0.wireOp",EDGE,"E44"),sQuery(id+"F0.wireOp",EDGE,"E47"),sQuery(id+"F0.wireOp",EDGE,"E48"),sQuery(id+"F0.wireOp",EDGE,"E49"),sQuery(id+"F0.wireOp",EDGE,"E50"),sQuery(id+"F0.wireOp",EDGE,"E51")])],"isStart":true})]});}
            var Q120;
            Q120=makeQuery(id+"F1.opExtrude","CAP_EDGE",EDGE,{"disambiguationData":[OSD([sQuery(id+"F0.wireOp",EDGE,"E11.rect.bottom"),sQuery(id+"F0.wireOp",EDGE,"E21.rect.bottom")])],"isStart":true});
            var Q121;
            {var subQ0=sQuery(id+"F0.wireOp",EDGE,"E12.rect.left");var subQ1=sQuery(id+"F0.wireOp",EDGE,"E11.rect.bottom");Q121=makeQuery(id+"F4.opFillet","BLEND_EDGE",EDGE,{"blendedFrom":[makeQuery(id+"F1.opExtrude","SWEPT_EDGE",EDGE,{"disambiguationData":[OSD([subQ1,subQ0])]}),makeQuery(id+"F1.opExtrude","CAP_FACE",FACE,{"disambiguationData":[OSD([sQuery(id+"F0.wireOp",EDGE,"E0"),sQuery(id+"F0.wireOp",EDGE,"E1"),sQuery(id+"F0.wireOp",EDGE,"E2"),sQuery(id+"F0.wireOp",EDGE,"E3"),sQuery(id+"F0.wireOp",EDGE,"E4"),sQuery(id+"F0.wireOp",EDGE,"E5"),sQuery(id+"F0.wireOp",EDGE,"E6"),sQuery(id+"F0.wireOp",EDGE,"E7"),sQuery(id+"F0.wireOp",EDGE,"E9.rect.left"),sQuery(id+"F0.wireOp",EDGE,"E9.rect.right"),sQuery(id+"F0.wireOp",EDGE,"E10.rect.bottom"),sQuery(id+"F0.wireOp",EDGE,"E10.rect.top"),subQ1,sQuery(id+"F0.wireOp",EDGE,"E11.rect.top"),subQ0,sQuery(id+"F0.wireOp",EDGE,"E12.rect.right"),sQuery(id+"F0.wireOp",EDGE,"E13.rect.left"),sQuery(id+"F0.wireOp",EDGE,"E13.rect.right"),sQuery(id+"F0.wireOp",EDGE,"E14.left"),sQuery(id+"F0.wireOp",EDGE,"E14.right"),sQuery(id+"F0.wireOp",EDGE,"E15"),sQuery(id+"F0.wireOp",EDGE,"E17"),sQuery(id+"F0.wireOp",EDGE,"E18"),sQuery(id+"F0.wireOp",EDGE,"E20"),sQuery(id+"F0.wireOp",EDGE,"E21.rect.bottom"),sQuery(id+"F0.wireOp",EDGE,"E21.rect.top"),sQuery(id+"F0.wireOp",EDGE,"E22.left"),sQuery(id+"F0.wireOp",EDGE,"E22.right"),sQuery(id+"F0.wireOp",EDGE,"E23.top"),sQuery(id+"F0.wireOp",EDGE,"E23.left"),sQuery(id+"F0.wireOp",EDGE,"E23.right"),sQuery(id+"F0.wireOp",EDGE,"E22.top"),sQuery(id+"F0.wireOp",EDGE,"E26"),sQuery(id+"F0.wireOp",EDGE,"E29"),sQuery(id+"F0.wireOp",EDGE,"E32"),sQuery(id+"F0.wireOp",EDGE,"E35"),sQuery(id+"F0.wireOp",EDGE,"E36"),sQuery(id+"F0.wireOp",EDGE,"E41"),sQuery(id+"F0.wireOp",EDGE,"E44"),sQuery(id+"F0.wireOp",EDGE,"E47"),sQuery(id+"F0.wireOp",EDGE,"E48"),sQuery(id+"F0.wireOp",EDGE,"E49"),sQuery(id+"F0.wireOp",EDGE,"E50"),sQuery(id+"F0.wireOp",EDGE,"E51")])],"isStart":true})],"blendedInto":[makeQuery(id+"F1.opExtrude","CAP_FACE",FACE,{"disambiguationData":[OSD([sQuery(id+"F0.wireOp",EDGE,"E0"),sQuery(id+"F0.wireOp",EDGE,"E1"),sQuery(id+"F0.wireOp",EDGE,"E2"),sQuery(id+"F0.wireOp",EDGE,"E3"),sQuery(id+"F0.wireOp",EDGE,"E4"),sQuery(id+"F0.wireOp",EDGE,"E5"),sQuery(id+"F0.wireOp",EDGE,"E6"),sQuery(id+"F0.wireOp",EDGE,"E7"),sQuery(id+"F0.wireOp",EDGE,"E9.rect.left"),sQuery(id+"F0.wireOp",EDGE,"E9.rect.right"),sQuery(id+"F0.wireOp",EDGE,"E10.rect.bottom"),sQuery(id+"F0.wireOp",EDGE,"E10.rect.top"),subQ1,sQuery(id+"F0.wireOp",EDGE,"E11.rect.top"),subQ0,sQuery(id+"F0.wireOp",EDGE,"E12.rect.right"),sQuery(id+"F0.wireOp",EDGE,"E13.rect.left"),sQuery(id+"F0.wireOp",EDGE,"E13.rect.right"),sQuery(id+"F0.wireOp",EDGE,"E14.left"),sQuery(id+"F0.wireOp",EDGE,"E14.right"),sQuery(id+"F0.wireOp",EDGE,"E15"),sQuery(id+"F0.wireOp",EDGE,"E17"),sQuery(id+"F0.wireOp",EDGE,"E18"),sQuery(id+"F0.wireOp",EDGE,"E20"),sQuery(id+"F0.wireOp",EDGE,"E21.rect.bottom"),sQuery(id+"F0.wireOp",EDGE,"E21.rect.top"),sQuery(id+"F0.wireOp",EDGE,"E22.left"),sQuery(id+"F0.wireOp",EDGE,"E22.right"),sQuery(id+"F0.wireOp",EDGE,"E23.top"),sQuery(id+"F0.wireOp",EDGE,"E23.left"),sQuery(id+"F0.wireOp",EDGE,"E23.right"),sQuery(id+"F0.wireOp",EDGE,"E22.top"),sQuery(id+"F0.wireOp",EDGE,"E26"),sQuery(id+"F0.wireOp",EDGE,"E29"),sQuery(id+"F0.wireOp",EDGE,"E32"),sQuery(id+"F0.wireOp",EDGE,"E35"),sQuery(id+"F0.wireOp",EDGE,"E36"),sQuery(id+"F0.wireOp",EDGE,"E41"),sQuery(id+"F0.wireOp",EDGE,"E44"),sQuery(id+"F0.wireOp",EDGE,"E47"),sQuery(id+"F0.wireOp",EDGE,"E48"),sQuery(id+"F0.wireOp",EDGE,"E49"),sQuery(id+"F0.wireOp",EDGE,"E50"),sQuery(id+"F0.wireOp",EDGE,"E51")])],"isStart":true})]});}
            fillet(context, id + "F5", {"entities" : qUnion([Q0, Q1, Q2, Q3, Q4, Q5, Q6, Q7, Q8, Q9, Q10, Q11, Q12, Q13, Q14, Q15, Q16, Q17, Q18, Q19, Q20, Q21, Q22, Q23, Q24, Q25, Q26, Q27, Q28, Q29, Q30, Q31, Q32, Q33, Q34, Q35, Q36, Q37, Q38, Q39, Q40, Q41, Q42, Q43, Q44, Q45, Q46, Q47, Q48, Q49, Q50, Q51, Q52, Q53, Q54, Q55, Q56, Q57, Q58, Q59, Q60, Q61, Q62, Q63, Q64, Q65, Q66, Q67, Q68, Q69, Q70, Q71, Q72, Q73, Q74, Q75, Q76, Q77, Q78, Q79, Q80, Q81, Q82, Q83, Q84, Q85, Q86, Q87, Q88, Q89, Q90, Q91, Q92, Q93, Q94, Q95, Q96, Q97, Q98, Q99, Q100, Q101, Q102, Q103, Q104, Q105, Q106, Q107, Q108, Q109, Q110, Q111, Q112, Q113, Q114, Q115, Q116, Q117, Q118, Q119, Q120, Q121]), "radius" : 0.76 * mm, "allowEdgeOverflow" : false});
        }
    });
